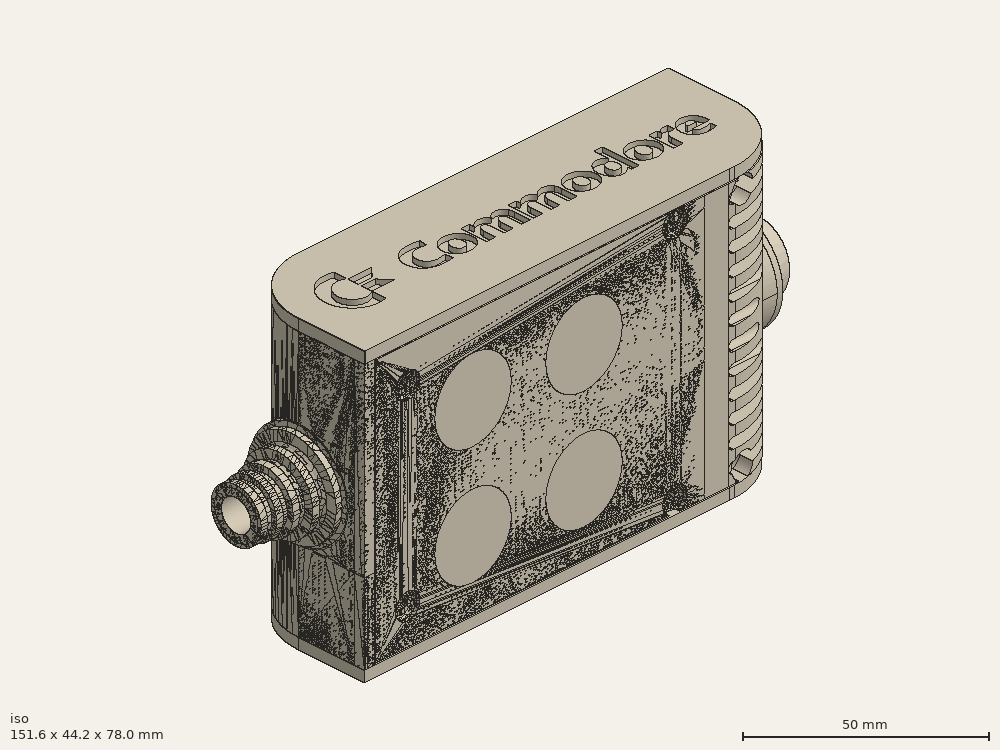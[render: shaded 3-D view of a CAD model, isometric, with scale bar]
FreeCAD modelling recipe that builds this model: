
FCSTD DOCUMENT  (FreeCAD 0.19R0.19.2)
Label: enclosure_225FCStd
License: All rights reserved
LicenseURL: http://en.wikipedia.org/wiki/All_rights_reserved
objects: Part::Revolution×152, Part::MultiFuse×148, Part::Feature×146, Sketcher::SketchObject×94, Part::Extrusion×79, Part::Cut×75, Part::Cylinder×71, Part::Fillet×58, Part::Box×38, App::MeasureDistance×4, Part::Chamfer×4, Part::FeaturePython×2, Image::ImagePlane×1, PartDesign::Body×1, Part::Mirroring×1
note: 869 computed .brp shape members not serialized (recipe doc carries the construction recipe); baked Part::Feature solids carry a one-line shape summary decoded from their .brp

FEATURE [Sketcher::SketchObject] Sketch  label="topSketch"
  FullyConstrained = true
  sketch-geometry (20):
    g0: LineSegment StartX=5.21097e-06 StartY=3 StartZ=0 EndX=5.21097e-06 EndY=19 EndZ=0
    g1: ArcOfCircle CenterX=19 CenterY=19 CenterZ=0 NormalX=0 NormalY=0 NormalZ=1 AngleXU=0 Radius=19 StartAngle=1.5708 EndAngle=3.14159
    g2: ArcOfCircle CenterX=19 CenterY=19 CenterZ=0 NormalX=0 NormalY=0 NormalZ=1 AngleXU=0 Radius=16 StartAngle=1.5708 EndAngle=3.14159
    g3: LineSegment StartX=114 StartY=35 StartZ=0 EndX=19 EndY=35 EndZ=0
    g4: LineSegment StartX=5.21097e-06 StartY=3 StartZ=0 EndX=5.21097e-06 EndY=0 EndZ=0
    g5: LineSegment StartX=3 StartY=0 StartZ=0 EndX=5.21097e-06 EndY=0 EndZ=0
    g6: LineSegment StartX=3 StartY=19 StartZ=0 EndX=3 EndY=0 EndZ=0
    g7: LineSegment StartX=19 StartY=38 StartZ=0 EndX=124 EndY=38 EndZ=0
    g8: Circle CenterX=119 CenterY=35 CenterZ=0 NormalX=0 NormalY=0 NormalZ=1 AngleXU=0 Radius=1
    g9: Circle CenterX=121 CenterY=35 CenterZ=0 NormalX=0 NormalY=0 NormalZ=1 AngleXU=0 Radius=1
    g10: Circle CenterX=121 CenterY=33 CenterZ=0 NormalX=0 NormalY=0 NormalZ=1 AngleXU=0 Radius=1
    g11: BSplineCurve PolesCount=3 KnotsCount=2 Degree=2 IsPeriodic=0
    g12: GeomPoint X=119 Y=35 Z=0
    g13: GeomPoint X=121 Y=33 Z=0
    g14: LineSegment StartX=119 StartY=35 StartZ=0 EndX=114 EndY=35 EndZ=0
    g15: ArcOfCircle CenterX=105 CenterY=19 CenterZ=0 NormalX=0 NormalY=0 NormalZ=1 AngleXU=0 Radius=19 StartAngle=5.7297 EndAngle=6.28319
    g16: ArcOfCircle CenterX=105 CenterY=19 CenterZ=0 NormalX=0 NormalY=0 NormalZ=1 AngleXU=0 Radius=16 StartAngle=5.60905 EndAngle=6.28319
    g17: LineSegment StartX=121 StartY=33 StartZ=0 EndX=121 EndY=19 EndZ=0
    g18: LineSegment StartX=124 StartY=38 StartZ=0 EndX=124 EndY=19 EndZ=0
    g19: LineSegment StartX=117.5 StartY=9.01251 StartZ=0 EndX=121.163 EndY=9.0125 EndZ=0
  constraints (46):
    c: Vertical(g0)
    c: Block(g0)
    c: Coincident(g1,g0)
    c: Block(g1)
    c: Coincident(g2,g1)
    c: Block(g2)
    c: Coincident(g3,g2)
    c: Horizontal(g3)
    c: Tangent(g3,g2)
    c: Coincident(g4,g0)
    c: Distance(g4) = 3
    c: Vertical(g4)
    c: Coincident(g5,g4)
    c: Horizontal(g5)
    c: Coincident(g6,g2)
    c: Coincident(g6,g5)
    c: Vertical(g6)
    c: Horizontal(g7)
    c: Distance(g7) = 105
    c: Coincident(g7,g1)
    c: Block(g3)
    c: Weight(g8) = 1
    c: Equal(g8,g9)
    c: Equal(g8,g10)
    c: InternalAlignment(g8,g11)
    c: InternalAlignment(g9,g11)
    c: InternalAlignment(g10,g11)
    c: InternalAlignment(g12,g11)
    c: InternalAlignment(g13,g11)
    c: Block(g11)
    c: Coincident(g14,g11)
    c: Coincident(g14,g3)
    c: Horizontal(g14)
    c: Block(g15)
    c: Coincident(g16,g15)
    c: Block(g16)
    c: Coincident(g17,g11)
    c: Coincident(g17,g16)
    c: Vertical(g17)
    c: Distance(g17) = 14
    c: Coincident(g18,g7)
    c: Coincident(g18,g15)
    c: Vertical(g18)
    c: Distance(g18) = 19
    c: Coincident(g19,g16)
    c: Coincident(g19,g15)
FEATURE [Sketcher::SketchObject] Sketch001  label="bottomSketch"
  FullyConstrained = true
  sketch-geometry (32):
    g0: LineSegment StartX=3.3 StartY=-6.03275e-07 StartZ=0 EndX=98 EndY=-6.03275e-07 EndZ=0
    g1: ArcOfCircle CenterX=98 CenterY=19 CenterZ=0 NormalX=0 NormalY=0 NormalZ=1 AngleXU=0 Radius=19 StartAngle=4.71239 EndAngle=5.71103
    g2: LineSegment StartX=6.3 StartY=8 StartZ=0 EndX=3.3 EndY=8 EndZ=0
    g3: LineSegment StartX=3.3 StartY=8 StartZ=0 EndX=3.3 EndY=-6.03275e-07 EndZ=0
    g4: ArcOfCircle CenterX=8.3 CenterY=5 CenterZ=0 NormalX=0 NormalY=0 NormalZ=1 AngleXU=0 Radius=2 StartAngle=3.14159 EndAngle=4.71239
    g5: LineSegment StartX=6.3 StartY=8 StartZ=0 EndX=6.3 EndY=5 EndZ=0
    g6: ArcOfCircle CenterX=98 CenterY=19 CenterZ=0 NormalX=0 NormalY=0 NormalZ=1 AngleXU=0 Radius=12.7 StartAngle=4.71239 EndAngle=6.28319
    g7: LineSegment StartX=94.7 StartY=3 StartZ=0 EndX=8.3 EndY=3 EndZ=0
    g8-g12: Circle x5 (B-spline internal-alignment scaffolding for g13; pole/knot coordinates omitted)
    g13: BSplineCurve PolesCount=5 KnotsCount=3 Degree=3 IsPeriodic=0
    g14: GeomPoint X=98 Y=6.3 Z=0
    g15: GeomPoint X=96.3938 Y=4.71946 Z=0
    g16: GeomPoint X=94.7 Y=3 Z=0
    g17-g23: Circle x7 (B-spline internal-alignment scaffolding for g24; pole/knot coordinates omitted)
    g24: BSplineCurve PolesCount=7 KnotsCount=5 Degree=3 IsPeriodic=0
    g25-g29: GeomPoint x5 (B-spline internal-alignment scaffolding for g24; pole/knot coordinates omitted)
    g30: ArcOfCircle CenterX=98 CenterY=19 CenterZ=0 NormalX=0 NormalY=0 NormalZ=1 AngleXU=0 Radius=15.7 StartAngle=5.81226 EndAngle=6.28319
    g31: LineSegment StartX=110.7 StartY=19 StartZ=0 EndX=113.7 EndY=19 EndZ=0
  constraints (41):
    c: Horizontal(g0)
    c: Coincident(g1,g0)
    c: Block(g1)
    c: Horizontal(g2)
    c: Distance(g2) = 3
    c: Coincident(g3,g2)
    c: Vertical(g3)
    c: Coincident(g3,g0)
    c: Block(g4)
    c: Block(g2)
    c: Coincident(g5,g2)
    c: Coincident(g5,g4)
    c: Vertical(g5)
    c: Coincident(g6,g1)
    c: Block(g6)
    c: Coincident(g7,g4)
    c: Horizontal(g7)
    c: Block(g0)
    c: Block(g7)
    c: Block(g3)
    c: Coincident(g13,g6)
    c: Weight(g8) = 1
    c: Equal(g8, g9-g12) x4
    c: Coincident(g13,g7)
    c: InternalAlignment(g8-g12 -> g13) x5
    c: InternalAlignment(g14,g13)
    c: InternalAlignment(g15,g13)
    c: InternalAlignment(g16,g13)
    c: Block(g13)
    c: Weight(g17) = 1
    c: Equal(g17, g18-g23) x6
    c: Coincident(g24,g1)
    c: InternalAlignment(g17-g23 -> g24) x7
    c: InternalAlignment(g25-g29 -> g24) x5
    c: Block(g24)
    c: Coincident(g30,g24)
    c: Coincident(g31,g6)
    c: Coincident(g31,g30)
    c: Horizontal(g31)
    c: Block(g31)
    c: Block(g30)
FEATURE [Part::Extrusion] Extrude  label="top"
  Base = -> Sketch
  Dir = (0,0,1)
  DirMode = 2
  FaceMakerClass = Part::FaceMakerBullseye
  LengthFwd = 72
  LengthRev = 0
  Solid = true
  Symmetric = false
FEATURE [Part::Extrusion] Extrude001  label="bottom"
  Base = -> Sketch001
  Dir = (0,0,1)
  DirMode = 2
  FaceMakerClass = Part::FaceMakerBullseye
  LengthFwd = 71.4
  LengthRev = 0
  Placement = pos=(0,0,0.3) rot=(0,0,1;0rad)
  Solid = true
  Symmetric = false
FEATURE [Sketcher::SketchObject] Sketch002  label="topSketch001"
  FullyConstrained = true
  sketch-geometry (8):
    g0: ArcOfCircle CenterX=19 CenterY=19.0975 CenterZ=0 NormalX=0 NormalY=0 NormalZ=1 AngleXU=0 Radius=18.9025 StartAngle=1.5708 EndAngle=3.14674
    g1: LineSegment StartX=0.0977805 StartY=19.0003 StartZ=0 EndX=0.0977805 EndY=0.000251602 EndZ=0
    g2: LineSegment StartX=19 StartY=38 StartZ=0 EndX=124 EndY=38 EndZ=0
    g3: LineSegment StartX=0.0977805 StartY=0.000251602 StartZ=0 EndX=105.098 EndY=0.000251602 EndZ=0
    g4: LineSegment StartX=124 StartY=38 StartZ=0 EndX=125.616 EndY=38 EndZ=0
    g5: LineSegment StartX=105.098 StartY=0.000251602 StartZ=0 EndX=106.713 EndY=0.000251602 EndZ=0
    g6: ArcOfCircle CenterX=106.616 CenterY=19 CenterZ=0 NormalX=0 NormalY=0 NormalZ=1 AngleXU=0 Radius=19 StartAngle=4.71754 EndAngle=6.28319
    g7: LineSegment StartX=125.616 StartY=38 StartZ=0 EndX=125.616 EndY=19 EndZ=0
  constraints (21):
    c: Block(g0)
    c: Coincident(g1,g0)
    c: Vertical(g1)
    c: Horizontal(g2)
    c: Distance(g2) = 105
    c: Coincident(g2,g0)
    c: Distance(g1) = 19
    c: Coincident(g3,g1)
    c: Horizontal(g3)
    c: Distance(g3) = 105
    c: Coincident(g4,g2)
    c: Horizontal(g4)
    c: Distance(g4) = 1.61553
    c: Horizontal(g5)
    c: Equal(g4,g5) = 1.61553
    c: Coincident(g5,g3)
    c: Block(g6)
    c: Coincident(g6,g5)
    c: Coincident(g7,g4)
    c: Coincident(g7,g6)
    c: Vertical(g7)
FEATURE [Part::Extrusion] Extrude002  label="sideA"
  Base = -> Sketch002
  Dir = (0,0,1)
  DirMode = 2
  FaceMakerClass = Part::FaceMakerBullseye
  LengthFwd = 3
  LengthRev = 0
  Placement = pos=(0,0,-3) rot=(0,0,1;0rad)
  Solid = true
  Symmetric = false
FEATURE [Sketcher::SketchObject] Sketch003  label="topSketch002"
  FullyConstrained = true
  sketch-geometry (6):
    g0: LineSegment StartX=19 StartY=38 StartZ=0 EndX=117 EndY=38 EndZ=0
    g1: ArcOfCircle CenterX=19 CenterY=19 CenterZ=0 NormalX=0 NormalY=0 NormalZ=1 AngleXU=0 Radius=19 StartAngle=1.5708 EndAngle=3.14159
    g2: LineSegment StartX=117 StartY=38 StartZ=0 EndX=117 EndY=19 EndZ=0
    g3: LineSegment StartX=98 StartY=1.0161e-12 StartZ=0 EndX=5.22862e-06 EndY=1.0161e-12 EndZ=0
    g4: LineSegment StartX=5.22862e-06 StartY=19 StartZ=0 EndX=5.22862e-06 EndY=1.0161e-12 EndZ=0
    g5: ArcOfCircle CenterX=98 CenterY=19 CenterZ=0 NormalX=0 NormalY=0 NormalZ=1 AngleXU=0 Radius=19 StartAngle=4.71239 EndAngle=6.28319
  constraints (16):
    c: Horizontal(g0)
    c: Distance(g0) = 98
    c: Coincident(g1,g0)
    c: Block(g1)
    c: Coincident(g2,g0)
    c: Vertical(g2)
    c: Distance(g2) = 19
    c: Horizontal(g3)
    c: Coincident(g4,g1)
    c: Vertical(g4)
    c: Coincident(g3,g4)
    c: Block(g3)
    c: Coincident(g5,g2)
    c: Coincident(g5,g3)
    c: Block(g0)
    c: Block(g5)
FEATURE [Sketcher::SketchObject] Sketch004
  FullyConstrained = true
  MapMode = 3
  Placement = pos=(0,0,0) rot=(1,0,0;1.5708rad)
  Support = -> [Extrude]
  sketch-geometry (8):
    g0: Circle CenterX=80.351 CenterY=-67.6202 CenterZ=0 NormalX=0 NormalY=0 NormalZ=1 AngleXU=0 Radius=2
    g1: Circle CenterX=80.351 CenterY=-67.6202 CenterZ=0 NormalX=0 NormalY=0 NormalZ=1 AngleXU=0 Radius=3
    g2: Circle CenterX=80.351 CenterY=-4.92017 CenterZ=0 NormalX=0 NormalY=0 NormalZ=1 AngleXU=0 Radius=2
    g3: Circle CenterX=80.351 CenterY=-4.92017 CenterZ=0 NormalX=0 NormalY=0 NormalZ=1 AngleXU=0 Radius=3
    g4: Circle CenterX=23.851 CenterY=-4.92017 CenterZ=0 NormalX=0 NormalY=0 NormalZ=1 AngleXU=0 Radius=2
    g5: Circle CenterX=23.851 CenterY=-4.92017 CenterZ=0 NormalX=0 NormalY=0 NormalZ=1 AngleXU=0 Radius=3
    g6: Circle CenterX=23.851 CenterY=-67.6202 CenterZ=0 NormalX=0 NormalY=0 NormalZ=1 AngleXU=0 Radius=2
    g7: Circle CenterX=23.851 CenterY=-67.6202 CenterZ=0 NormalX=0 NormalY=0 NormalZ=1 AngleXU=0 Radius=3
  constraints (8):
    c: Block(g3)
    c: Block(g2)
    c: Block(g1)
    c: Block(g0)
    c: Block(g6)
    c: Block(g7)
    c: Block(g4)
    c: Block(g5)
FEATURE [Part::Extrusion] Extrude004
  Base = -> Sketch004
  Dir = (0,-1,2e-16)
  DirMode = 2
  FaceMakerClass = Part::FaceMakerBullseye
  LengthFwd = 6
  LengthRev = 0
  Placement = pos=(0,9,0) rot=(0,0,1;0rad)
  Solid = true
  Symmetric = false
FEATURE [Sketcher::SketchObject] Sketch005
  FullyConstrained = true
  MapMode = 3
  Placement = pos=(0,0,0) rot=(1,0,0;1.5708rad)
  Support = -> [Extrude]
  sketch-geometry (8):
    g0: Circle CenterX=80.351 CenterY=-67.6202 CenterZ=0 NormalX=0 NormalY=0 NormalZ=1 AngleXU=0 Radius=3
    g1: Circle CenterX=80.351 CenterY=-4.92017 CenterZ=0 NormalX=0 NormalY=0 NormalZ=1 AngleXU=0 Radius=3
    g2: Circle CenterX=23.851 CenterY=-4.92017 CenterZ=0 NormalX=0 NormalY=0 NormalZ=1 AngleXU=0 Radius=3
    g3: Circle CenterX=23.851 CenterY=-67.6202 CenterZ=0 NormalX=0 NormalY=0 NormalZ=1 AngleXU=0 Radius=3
    g4: Circle CenterX=23.851 CenterY=-67.6202 CenterZ=0 NormalX=0 NormalY=0 NormalZ=1 AngleXU=0 Radius=5
    g5: Circle CenterX=80.351 CenterY=-67.6202 CenterZ=0 NormalX=0 NormalY=0 NormalZ=1 AngleXU=0 Radius=5
    g6: Circle CenterX=23.851 CenterY=-4.92017 CenterZ=0 NormalX=0 NormalY=0 NormalZ=1 AngleXU=0 Radius=5
    g7: Circle CenterX=80.351 CenterY=-4.92017 CenterZ=0 NormalX=0 NormalY=0 NormalZ=1 AngleXU=0 Radius=5
  constraints (8):
    c: Block(g1)
    c: Block(g0)
    c: Block(g3)
    c: Block(g2)
    c: Block(g5)
    c: Block(g4)
    c: Block(g6)
    c: Block(g7)
FEATURE [Part::Extrusion] Extrude005
  Base = -> Sketch005
  Dir = (0,-1,2e-16)
  DirMode = 2
  FaceMakerClass = Part::FaceMakerBullseye
  LengthFwd = 2
  LengthRev = 0
  Solid = true
  Symmetric = false
FEATURE [Sketcher::SketchObject] Sketch006
  FullyConstrained = true
  MapMode = 3
  Placement = pos=(0,0,0) rot=(1,0,0;1.5708rad)
  sketch-geometry (8):
    g0: Circle CenterX=80.351 CenterY=-67.6202 CenterZ=0 NormalX=0 NormalY=0 NormalZ=1 AngleXU=0 Radius=3
    g1: Circle CenterX=80.351 CenterY=-4.92017 CenterZ=0 NormalX=0 NormalY=0 NormalZ=1 AngleXU=0 Radius=3
    g2: Circle CenterX=23.851 CenterY=-4.92017 CenterZ=0 NormalX=0 NormalY=0 NormalZ=1 AngleXU=0 Radius=3
    g3: Circle CenterX=23.851 CenterY=-67.6202 CenterZ=0 NormalX=0 NormalY=0 NormalZ=1 AngleXU=0 Radius=3
    g4: Circle CenterX=23.851 CenterY=-67.6202 CenterZ=0 NormalX=0 NormalY=0 NormalZ=1 AngleXU=0 Radius=5
    g5: Circle CenterX=80.351 CenterY=-67.6202 CenterZ=0 NormalX=0 NormalY=0 NormalZ=1 AngleXU=0 Radius=5
    g6: Circle CenterX=23.851 CenterY=-4.92017 CenterZ=0 NormalX=0 NormalY=0 NormalZ=1 AngleXU=0 Radius=5
    g7: Circle CenterX=80.351 CenterY=-4.92017 CenterZ=0 NormalX=0 NormalY=0 NormalZ=1 AngleXU=0 Radius=5
  constraints (8):
    c: Block(g1)
    c: Block(g0)
    c: Block(g3)
    c: Block(g2)
    c: Block(g5)
    c: Block(g4)
    c: Block(g6)
    c: Block(g7)
FEATURE [Part::Extrusion] Extrude007
  Base = -> Sketch006
  Dir = (0,-1,2e-16)
  DirMode = 2
  FaceMakerClass = Part::FaceMakerBullseye
  LengthFwd = 2
  LengthRev = 0
  Solid = true
  Symmetric = false
FEATURE [Part::Fillet] Fillet
  Base = -> Extrude007
  Edges = 4 edges r=1.99: [Edge6,Edge12,Edge18,Edge24]
FEATURE [Part::Cut] Cut
  Base = -> Extrude005
  Placement = pos=(0,5,0) rot=(0,0,1;0rad)
  Tool = -> Fillet
FEATURE [Part::MultiFuse] Fusion  label="pCBScrews"
  Placement = pos=(-2.5,0,72.3) rot=(0,0,1;0rad)
  Shapes = -> [Extrude004,Cut]
FEATURE [App::MeasureDistance] Distance  label="Distance: 0.69 mm"
  Distance = 0.685967
  P1 = (24.0138,2.9647,0.3)
  P2 = (23.8901,3,-0.373787)
FEATURE [App::MeasureDistance] Distance001  label="Distance: 0.53 mm"
  Distance = 0.533607
  P1 = (80.2939,3,72.2334)
  P2 = (80.281,2.99661,71.7)
FEATURE [Part::Fillet] Fillet001
  Base = -> Extrude001
  Edges = 1 edges r=2.4: [Edge17]
FEATURE [Part::Fillet] Fillet002  label="bottom001"
  Base = -> Fillet001
  Edges = 1 edges r=2.4: [Edge36]
FEATURE [Part::Fillet] Fillet003  label="top001"
  Base = -> Extrude
  Edges = 1 edges r=2: [Edge1]
FEATURE [Sketcher::SketchObject] Sketch007
  FullyConstrained = true
  sketch-geometry (16):
    g0: LineSegment StartX=4 StartY=0 StartZ=0 EndX=4 EndY=2.4 EndZ=0
    g1: LineSegment StartX=4 StartY=2.4 StartZ=0 EndX=7 EndY=2.4 EndZ=0
    g2: LineSegment StartX=4 StartY=0 StartZ=0 EndX=5.7 EndY=0 EndZ=0
    g3: LineSegment StartX=5.7 StartY=0 StartZ=0 EndX=5.7 EndY=-5.6 EndZ=0
    g4-g8: Circle x5 (B-spline internal-alignment scaffolding for g9; pole/knot coordinates omitted)
    g9: BSplineCurve PolesCount=5 KnotsCount=3 Degree=3 IsPeriodic=0
    g10: GeomPoint X=7 Y=2.4 Z=0
    g11: GeomPoint X=10.4582 Y=-1.55472 Z=0
    g12: GeomPoint X=14 Y=-5.6 Z=0
    g13: LineSegment StartX=14 StartY=-5.6 StartZ=0 EndX=14 EndY=-14.1 EndZ=0
    g14: LineSegment StartX=14 StartY=-14.1 StartZ=0 EndX=6.5 EndY=-14.1 EndZ=0
    g15: LineSegment StartX=5.7 StartY=-5.6 StartZ=0 EndX=6.5 EndY=-14.1 EndZ=0
  constraints (28):
    c: Distance(g0) = 2.4
    c: Vertical(g0)
    c: Block(g0)
    c: Coincident(g1,g0)
    c: Horizontal(g1)
    c: Distance(g1) = 3
    c: Coincident(g2,g0)
    c: Horizontal(g2)
    c: Distance(g2) = 1.7
    c: Coincident(g3,g2)
    c: Vertical(g3)
    c: Distance(g3) = 5.6
    c: Coincident(g9,g1)
    c: Weight(g4) = 1
    c: Equal(g4, g5-g8) x4
    c: InternalAlignment(g4-g8 -> g9) x5
    c: InternalAlignment(g10,g9)
    c: InternalAlignment(g11,g9)
    c: InternalAlignment(g12,g9)
    c: Block(g9)
    c: Coincident(g13,g9)
    c: Vertical(g13)
    c: Distance(g13) = 8.5
    c: Coincident(g14,g13)
    c: Horizontal(g14)
    c: Distance(g14) = 7.5
    c: Coincident(g15,g3)
    c: Coincident(g15,g14)
FEATURE [Part::Feature] Face
  shape: bbox 10 x 16.5 x 2e-07 mm, 1 faces, 0 solids (baked)
FEATURE [Part::Revolution] Revolve  label="plugHousing"
  Angle = 360
  Axis = (0,1,0)
  Base = (0,0,0)
  FaceMakerClass = Part::FaceMakerBullseye
  Placement = pos=(0,0,36.15) rot=(0,0,1;0rad)
  Solid = false
  Source = -> Face
  Symmetric = false
FEATURE [Part::Feature] Face001
  shape: bbox 10 x 16.5 x 2e-07 mm, 1 faces, 0 solids (baked)
FEATURE [Part::Revolution] Revolve001  label="plugHousing001"
  Angle = 360
  Axis = (0,1,0)
  Base = (0,0,0)
  FaceMakerClass = Part::FaceMakerBullseye
  Placement = pos=(0,0,36.15) rot=(0,0,1;0rad)
  Solid = false
  Source = -> Face001
  Symmetric = false
FEATURE [Part::MultiFuse] Fusion001  label="plugHousing002"
  Placement = pos=(0,0,0) rot=(0,0,1;1.5708rad)
  Shapes = -> [Revolve001,Revolve]
FEATURE [Part::Feature] Face002
  shape: bbox 10 x 16.5 x 2e-07 mm, 1 faces, 0 solids (baked)
FEATURE [Part::Revolution] Revolve003  label="plugHousing005"
  Angle = 360
  Axis = (0,1,0)
  Base = (0,0,0)
  FaceMakerClass = Part::FaceMakerBullseye
  Placement = pos=(0,0,36.15) rot=(0,0,1;0rad)
  Solid = false
  Source = -> Face002
  Symmetric = false
FEATURE [Part::Feature] Face003
  shape: bbox 10 x 16.5 x 2e-07 mm, 1 faces, 0 solids (baked)
FEATURE [Part::Revolution] Revolve002  label="plugHousing003"
  Angle = 360
  Axis = (0,1,0)
  Base = (0,0,0)
  FaceMakerClass = Part::FaceMakerBullseye
  Placement = pos=(0,0,36.15) rot=(0,0,1;0rad)
  Solid = false
  Source = -> Face003
  Symmetric = false
FEATURE [Part::MultiFuse] Fusion002  label="plugHousing004"
  Placement = pos=(0,0,0) rot=(0,0,1;1.5708rad)
  Shapes = -> [Revolve002,Revolve003]
FEATURE [Part::MultiFuse] Fusion003  label="plugHousing006"
  Placement = pos=(0,19,0) rot=(0,0,1;3.14159rad)
  Shapes = -> [Fusion002,Fusion001]
FEATURE [Part::Feature] Face004
  shape: bbox 10 x 16.5 x 2e-07 mm, 1 faces, 0 solids (baked)
FEATURE [Part::Revolution] Revolve006  label="plugHousing010"
  Angle = 360
  Axis = (0,1,0)
  Base = (0,0,0)
  FaceMakerClass = Part::FaceMakerBullseye
  Placement = pos=(0,0,36.15) rot=(0,0,1;0rad)
  Solid = false
  Source = -> Face004
  Symmetric = false
FEATURE [Part::Feature] Face005
  shape: bbox 10 x 16.5 x 2e-07 mm, 1 faces, 0 solids (baked)
FEATURE [Part::Revolution] Revolve007  label="plugHousing011"
  Angle = 360
  Axis = (0,1,0)
  Base = (0,0,0)
  FaceMakerClass = Part::FaceMakerBullseye
  Placement = pos=(0,0,36.15) rot=(0,0,1;0rad)
  Solid = false
  Source = -> Face005
  Symmetric = false
FEATURE [Part::Feature] Face006
  shape: bbox 10 x 16.5 x 2e-07 mm, 1 faces, 0 solids (baked)
FEATURE [Part::Revolution] Revolve004  label="plugHousing007"
  Angle = 360
  Axis = (0,1,0)
  Base = (0,0,0)
  FaceMakerClass = Part::FaceMakerBullseye
  Placement = pos=(0,0,36.15) rot=(0,0,1;0rad)
  Solid = false
  Source = -> Face006
  Symmetric = false
FEATURE [Part::MultiFuse] Fusion004  label="plugHousing009"
  Placement = pos=(0,0,0) rot=(0,0,1;1.5708rad)
  Shapes = -> [Revolve004,Revolve007]
FEATURE [Part::Feature] Face007
  shape: bbox 10 x 16.5 x 2e-07 mm, 1 faces, 0 solids (baked)
FEATURE [Part::Revolution] Revolve005  label="plugHousing008"
  Angle = 360
  Axis = (0,1,0)
  Base = (0,0,0)
  FaceMakerClass = Part::FaceMakerBullseye
  Placement = pos=(0,0,36.15) rot=(0,0,1;0rad)
  Solid = false
  Source = -> Face007
  Symmetric = false
FEATURE [Part::MultiFuse] Fusion005  label="plugHousing012"
  Placement = pos=(0,0,0) rot=(0,0,1;1.5708rad)
  Shapes = -> [Revolve006,Revolve005]
FEATURE [Part::MultiFuse] Fusion006  label="plugHousing013"
  Placement = pos=(0,19,0) rot=(0,0,1;3.14159rad)
  Shapes = -> [Fusion005,Fusion004]
FEATURE [Part::MultiFuse] Fusion007  label="plugHousing014"
  Placement = pos=(122.621,0,-0.15) rot=(0,0,1;0rad)
  Shapes = -> [Fusion003,Fusion006]
FEATURE [Part::Cylinder] Cylinder002
  Angle = 360
  AttacherType = Attacher::AttachEngine3D
  Height = 20
  Placement = pos=(0,0,36.15) rot=(0,0,1;0rad)
  Radius = 4
FEATURE [Part::Cylinder] Cylinder003
  Angle = 360
  AttacherType = Attacher::AttachEngine3D
  Height = 10
  Placement = pos=(0,0,36.15) rot=(0,0,1;0rad)
  Radius = 4
FEATURE [Part::MultiFuse] Fusion009  label="removeToCreateHoleForPlugHousing"
  Placement = pos=(70,19,36.15) rot=(0,1,0;1.5708rad)
  Shapes = -> [Cylinder002,Cylinder003]
FEATURE [Part::Cylinder] Cylinder004
  Angle = 360
  AttacherType = Attacher::AttachEngine3D
  Height = 20
  Placement = pos=(0,0,36.15) rot=(0,0,1;0rad)
  Radius = 4
FEATURE [Part::Cylinder] Cylinder005
  Angle = 360
  AttacherType = Attacher::AttachEngine3D
  Height = 10
  Placement = pos=(0,0,36.15) rot=(0,0,1;0rad)
  Radius = 4
FEATURE [Part::MultiFuse] Fusion010  label="removeToCreateHoleForPlugHousing001"
  Placement = pos=(70,19,36.15) rot=(0,1,0;1.5708rad)
  Shapes = -> [Cylinder004,Cylinder005]
FEATURE [Part::Cut] Cut001
  Base = -> Fillet003
  Tool = -> Fusion010
FEATURE [Part::Cut] Cut002  label="Bottom"
  Base = -> Fillet002
  Tool = -> Fusion009
FEATURE [Part::Feature] Face008
  shape: bbox 10 x 16.5 x 2e-07 mm, 1 faces, 0 solids (baked)
FEATURE [Part::Revolution] Revolve011  label="plugHousing021"
  Angle = 360
  Axis = (0,1,0)
  Base = (0,0,0)
  FaceMakerClass = Part::FaceMakerBullseye
  Placement = pos=(0,0,36.15) rot=(0,0,1;0rad)
  Solid = false
  Source = -> Face008
  Symmetric = false
FEATURE [Part::Feature] Face009
  shape: bbox 10 x 16.5 x 2e-07 mm, 1 faces, 0 solids (baked)
FEATURE [Part::Revolution] Revolve012  label="plugHousing022"
  Angle = 360
  Axis = (0,1,0)
  Base = (0,0,0)
  FaceMakerClass = Part::FaceMakerBullseye
  Placement = pos=(0,0,36.15) rot=(0,0,1;0rad)
  Solid = false
  Source = -> Face009
  Symmetric = false
FEATURE [Part::Feature] Face010 .. Face013  x4 (patterned run collapsed; names and placements below)
  shape: bbox 10 x 16.5 x 2e-07 mm, 1 faces, 0 solids (baked)
FEATURE [Part::Revolution] Revolve015  label="plugHousing027"
  Angle = 360
  Axis = (0,1,0)
  Base = (0,0,0)
  FaceMakerClass = Part::FaceMakerBullseye
  Placement = pos=(0,0,36.15) rot=(0,0,1;0rad)
  Solid = false
  Source = -> Face013
  Symmetric = false
FEATURE [Part::Feature] Face014
  shape: bbox 10 x 16.5 x 2e-07 mm, 1 faces, 0 solids (baked)
FEATURE [Part::Feature] Face015
  shape: bbox 10 x 16.5 x 2e-07 mm, 1 faces, 0 solids (baked)
FEATURE [Part::Feature] Face016
  shape: bbox 10 x 16.5 x 2e-07 mm, 1 faces, 0 solids (baked)
FEATURE [Part::Revolution] Revolve019  label="plugHousing033"
  Angle = 360
  Axis = (0,1,0)
  Base = (0,0,0)
  FaceMakerClass = Part::FaceMakerBullseye
  Placement = pos=(0,0,36.15) rot=(0,0,1;0rad)
  Solid = false
  Source = -> Face016
  Symmetric = false
FEATURE [Part::Feature] Face017
  shape: bbox 10 x 16.5 x 2e-07 mm, 1 faces, 0 solids (baked)
FEATURE [Part::Revolution] Revolve020  label="plugHousing034"
  Angle = 360
  Axis = (0,1,0)
  Base = (0,0,0)
  FaceMakerClass = Part::FaceMakerBullseye
  Placement = pos=(0,0,36.15) rot=(0,0,1;0rad)
  Solid = false
  Source = -> Face017
  Symmetric = false
FEATURE [Part::Feature] Face018
  shape: bbox 10 x 16.5 x 2e-07 mm, 1 faces, 0 solids (baked)
FEATURE [Part::Revolution] Revolve016  label="plugHousing030"
  Angle = 360
  Axis = (0,1,0)
  Base = (0,0,0)
  FaceMakerClass = Part::FaceMakerBullseye
  Placement = pos=(0,0,36.15) rot=(0,0,1;0rad)
  Solid = false
  Source = -> Face018
  Symmetric = false
FEATURE [Part::MultiFuse] Fusion020  label="plugHousing038"
  Placement = pos=(0,0,0) rot=(0,0,1;1.5708rad)
  Shapes = -> [Revolve016,Revolve020]
FEATURE [Part::Feature] Face019
  shape: bbox 10 x 16.5 x 2e-07 mm, 1 faces, 0 solids (baked)
FEATURE [Part::Feature] Face020
  shape: bbox 10 x 16.5 x 2e-07 mm, 1 faces, 0 solids (baked)
FEATURE [Part::Revolution] Revolve017  label="plugHousing031"
  Angle = 360
  Axis = (0,1,0)
  Base = (0,0,0)
  FaceMakerClass = Part::FaceMakerBullseye
  Placement = pos=(0,0,36.15) rot=(0,0,1;0rad)
  Solid = false
  Source = -> Face020
  Symmetric = false
FEATURE [Part::MultiFuse] Fusion021  label="plugHousing039"
  Placement = pos=(0,0,0) rot=(0,0,1;1.5708rad)
  Shapes = -> [Revolve019,Revolve017]
FEATURE [Part::MultiFuse] Fusion023  label="plugHousing041"
  Placement = pos=(0,19,0) rot=(0,0,1;3.14159rad)
  Shapes = -> [Fusion021,Fusion020]
FEATURE [Part::Revolution] Revolve022  label="plugHousing043"
  Angle = 360
  Axis = (0,1,0)
  Base = (0,0,0)
  FaceMakerClass = Part::FaceMakerBullseye
  Placement = pos=(0,0,36.15) rot=(0,0,1;0rad)
  Solid = false
  Source = -> Face019
  Symmetric = false
FEATURE [Part::Feature] Face021
  shape: bbox 10 x 16.5 x 2e-07 mm, 1 faces, 0 solids (baked)
FEATURE [Part::Revolution] Revolve023  label="plugHousing044"
  Angle = 360
  Axis = (0,1,0)
  Base = (0,0,0)
  FaceMakerClass = Part::FaceMakerBullseye
  Placement = pos=(0,0,36.15) rot=(0,0,1;0rad)
  Solid = false
  Source = -> Face021
  Symmetric = false
FEATURE [Part::Feature] Face022
  shape: bbox 10 x 16.5 x 2e-07 mm, 1 faces, 0 solids (baked)
FEATURE [Part::Revolution] Revolve018  label="plugHousing032"
  Angle = 360
  Axis = (0,1,0)
  Base = (0,0,0)
  FaceMakerClass = Part::FaceMakerBullseye
  Placement = pos=(0,0,36.15) rot=(0,0,1;0rad)
  Solid = false
  Source = -> Face022
  Symmetric = false
FEATURE [Part::MultiFuse] Fusion022  label="plugHousing040"
  Placement = pos=(0,0,0) rot=(0,0,1;1.5708rad)
  Shapes = -> [Revolve018,Revolve023]
FEATURE [Part::Feature] Face023
  shape: bbox 10 x 16.5 x 2e-07 mm, 1 faces, 0 solids (baked)
FEATURE [Part::Revolution] Revolve021  label="plugHousing035"
  Angle = 360
  Axis = (0,1,0)
  Base = (0,0,0)
  FaceMakerClass = Part::FaceMakerBullseye
  Placement = pos=(0,0,36.15) rot=(0,0,1;0rad)
  Solid = false
  Source = -> Face023
  Symmetric = false
FEATURE [Part::MultiFuse] Fusion018  label="plugHousing036"
  Placement = pos=(0,0,0) rot=(0,0,1;1.5708rad)
  Shapes = -> [Revolve022,Revolve021]
FEATURE [Part::MultiFuse] Fusion019  label="plugHousing037"
  Placement = pos=(0,19,0) rot=(0,0,1;3.14159rad)
  Shapes = -> [Fusion018,Fusion022]
FEATURE [Part::MultiFuse] Fusion024  label="plugHousing042"
  Placement = pos=(122.621,0,-0.15) rot=(0,0,1;0rad)
  Shapes = -> [Fusion023,Fusion019]
FEATURE [Part::Cylinder] Cylinder006
  Angle = 360
  AttacherType = Attacher::AttachEngine3D
  Height = 20
  Placement = pos=(0,0,36.15) rot=(0,0,1;0rad)
  Radius = 14.3
FEATURE [Part::Cylinder] Cylinder007
  Angle = 360
  AttacherType = Attacher::AttachEngine3D
  Height = 10
  Placement = pos=(0,0,36.15) rot=(0,0,1;0rad)
  Radius = 4
FEATURE [Part::MultiFuse] Fusion026  label="removeToCreteHoleForPlugHousing"
  Placement = pos=(70,19,36) rot=(0,1,0;1.5708rad)
  Shapes = -> [Cylinder006,Cylinder007]
FEATURE [Part::Box] Box001  label="Cube001"
  AttacherType = Attacher::AttachEngine3D
  Height = 28
  Length = 3
  Placement = pos=(110.7,19,22) rot=(0,0,1;0rad)
  Width = 15.7
FEATURE [Part::Cut] Cut003  label="top002"
  Base = -> Cut001
  Tool = -> Fusion007
FEATURE [Part::Revolution] Revolve008  label="plugHousing015"
  Angle = 360
  Axis = (0,1,0)
  Base = (0,0,0)
  FaceMakerClass = Part::FaceMakerBullseye
  Placement = pos=(0,0,36.15) rot=(0,0,1;0rad)
  Solid = false
  Source = -> Face010
  Symmetric = false
FEATURE [Part::MultiFuse] Fusion013  label="plugHousing020"
  Placement = pos=(0,0,0) rot=(0,0,1;1.5708rad)
  Shapes = -> [Revolve008,Revolve012]
FEATURE [Part::Cut] Cut004  label="top003"
  Base = -> Cut003
  Placement = pos=(1,0,0) rot=(0,0,1;0rad)
  Tool = -> Fusion026
FEATURE [Part::Cylinder] Cylinder008
  Angle = 360
  AttacherType = Attacher::AttachEngine3D
  Height = 20
  Placement = pos=(0,0,36.15) rot=(0,0,1;0rad)
  Radius = 10.3
FEATURE [Part::Cylinder] Cylinder009
  Angle = 360
  AttacherType = Attacher::AttachEngine3D
  Height = 10
  Placement = pos=(0,0,36.15) rot=(0,0,1;0rad)
  Radius = 4
FEATURE [Part::MultiFuse] Fusion027  label="removeToCreteHoleForPlugHousing001"
  Placement = pos=(70,19,36) rot=(0,1,0;1.5708rad)
  Shapes = -> [Cylinder008,Cylinder009]
FEATURE [Part::Cut] Cut005  label="plugHousingTab"
  Base = -> Box001
  Tool = -> Fusion027
FEATURE [Part::MultiFuse] Fusion028  label="plugHousing045"
  Shapes = -> [Fusion024,Cut005]
FEATURE [Part::Box] Box002  label="Cube002"
  AttacherType = Attacher::AttachEngine3D
  Height = 28.8
  Length = 3
  Placement = pos=(107.3,28,21.6) rot=(0,0,1;0rad)
  Width = 7
FEATURE [Part::Box] Box003  label="Cube003"
  AttacherType = Attacher::AttachEngine3D
  Height = 3
  Length = 6.4
  Placement = pos=(107.3,28,18.6) rot=(0,0,1;0rad)
  Width = 7
FEATURE [Part::Box] Box004  label="Cube004"
  AttacherType = Attacher::AttachEngine3D
  Height = 3
  Length = 6.4
  Placement = pos=(107.3,28,50.4) rot=(0,0,1;0rad)
  Width = 7
FEATURE [Part::MultiFuse] Fusion029  label="plugHousingBracketHolder"
  Shapes = -> [Box004,Box002,Box003]
FEATURE [Part::Cylinder] Cylinder010
  Angle = 360
  AttacherType = Attacher::AttachEngine3D
  Height = 20
  Placement = pos=(0,0,36.15) rot=(0,0,1;0rad)
  Radius = 14.3
FEATURE [Part::Cylinder] Cylinder011
  Angle = 360
  AttacherType = Attacher::AttachEngine3D
  Height = 10
  Placement = pos=(0,0,36.15) rot=(0,0,1;0rad)
  Radius = 4
FEATURE [Part::MultiFuse] Fusion030  label="removeToCreteHoleForPlugHousing002"
  Placement = pos=(70,19,36) rot=(0,1,0;1.5708rad)
  Shapes = -> [Cylinder010,Cylinder011]
FEATURE [Part::Cut] Cut006  label="plugHousingBracketHolder001"
  Base = -> Fusion029
  Tool = -> Fusion030
FEATURE [Part::Cylinder] Cylinder012
  Angle = 360
  AttacherType = Attacher::AttachEngine3D
  Height = 20
  Placement = pos=(0,0,36.15) rot=(0,0,1;0rad)
  Radius = 7
FEATURE [Part::Cylinder] Cylinder013
  Angle = 360
  AttacherType = Attacher::AttachEngine3D
  Height = 10
  Placement = pos=(0,0,36.15) rot=(0,0,1;0rad)
  Radius = 4
FEATURE [Part::MultiFuse] Fusion032  label="removeToCreteHoleForPlugHousing003"
  Placement = pos=(70,19,36) rot=(0,1,0;1.5708rad)
  Shapes = -> [Cylinder012,Cylinder013]
FEATURE [Part::Cut] Cut007  label="bottom002"
  Base = -> Cut002
  Tool = -> Fusion032
FEATURE [Sketcher::SketchObject] Sketch008
  FullyConstrained = true
  sketch-geometry (54):
    g0: LineSegment StartX=-4.2 StartY=0 StartZ=0 EndX=-6.2 EndY=0 EndZ=0
    g1: LineSegment StartX=-14 StartY=-18 StartZ=0 EndX=-14 EndY=-26.5 EndZ=0
    g2: LineSegment StartX=-4.2 StartY=0 StartZ=0 EndX=-4.2 EndY=-13.4877 EndZ=0
    g3: Circle CenterX=-4.2 CenterY=-13.4877 CenterZ=0 NormalX=0 NormalY=0 NormalZ=1 AngleXU=0 Radius=1
    g4: Circle CenterX=-4.2 CenterY=-26.5 CenterZ=0 NormalX=0 NormalY=0 NormalZ=1 AngleXU=0 Radius=1
    g5: Circle CenterX=-8.2 CenterY=-26.5 CenterZ=0 NormalX=0 NormalY=0 NormalZ=1 AngleXU=0 Radius=1
    g6: BSplineCurve PolesCount=3 KnotsCount=2 Degree=2 IsPeriodic=0
    g7: GeomPoint X=-4.2 Y=-13.4877 Z=0
    g8: GeomPoint X=-8.2 Y=-26.5 Z=0
    g9: LineSegment StartX=-14 StartY=-26.5 StartZ=0 EndX=-8.2 EndY=-26.5 EndZ=0
    g10: LineSegment StartX=-10.15 StartY=-12 StartZ=0 EndX=-10.15 EndY=-14 EndZ=0
    g11: LineSegment StartX=-12.8401 StartY=-16 StartZ=0 EndX=-10.1571 EndY=-16 EndZ=0
    g12: LineSegment StartX=-10.15 StartY=-14 StartZ=0 EndX=-8.70761 EndY=-14 EndZ=0
    g13: LineSegment StartX=-12.8401 StartY=-16 StartZ=0 EndX=-12.8401 EndY=-17.6958 EndZ=0
    g14: LineSegment StartX=-10.15 StartY=-12 StartZ=0 EndX=-7.79258 EndY=-12 EndZ=0
    g15: Circle CenterX=-6.2215 CenterY=-2 CenterZ=0 NormalX=0 NormalY=0 NormalZ=1 AngleXU=0 Radius=1
    g16: Circle CenterX=-6.22762 CenterY=-2.58724 CenterZ=0 NormalX=0 NormalY=0 NormalZ=1 AngleXU=0 Radius=1
    g17: Circle CenterX=-6.32538 CenterY=-4 CenterZ=0 NormalX=0 NormalY=0 NormalZ=1 AngleXU=0 Radius=1
    g18: BSplineCurve PolesCount=3 KnotsCount=2 Degree=2 IsPeriodic=0
    g19: GeomPoint X=-6.2215 Y=-2 Z=0
    g20: GeomPoint X=-6.32538 Y=-4 Z=0
    g21: Circle CenterX=-6.48644 CenterY=-5.99526 CenterZ=0 NormalX=0 NormalY=0 NormalZ=1 AngleXU=0 Radius=1
    g22: Circle CenterX=-6.58486 CenterY=-6.99526 CenterZ=0 NormalX=0 NormalY=0 NormalZ=1 AngleXU=0 Radius=1
    g23: Circle CenterX=-6.77343 CenterY=-8 CenterZ=0 NormalX=0 NormalY=0 NormalZ=1 AngleXU=0 Radius=1
    g24: BSplineCurve PolesCount=3 KnotsCount=2 Degree=2 IsPeriodic=0
    g25: GeomPoint X=-6.48644 Y=-5.99526 Z=0
    g26: GeomPoint X=-6.77343 Y=-8 Z=0
    g27: Circle CenterX=-7.19003 CenterY=-10 CenterZ=0 NormalX=0 NormalY=0 NormalZ=1 AngleXU=0 Radius=1
    g28: Circle CenterX=-7.44407 CenterY=-11.0915 CenterZ=0 NormalX=0 NormalY=0 NormalZ=1 AngleXU=0 Radius=1
    g29: Circle CenterX=-7.79258 CenterY=-12 CenterZ=0 NormalX=0 NormalY=0 NormalZ=1 AngleXU=0 Radius=1
    g30: BSplineCurve PolesCount=3 KnotsCount=2 Degree=2 IsPeriodic=0
    g31: GeomPoint X=-7.19003 Y=-10 Z=0
    g32: GeomPoint X=-7.79258 Y=-12 Z=0
    g33: Circle CenterX=-8.70761 CenterY=-14 CenterZ=0 NormalX=0 NormalY=0 NormalZ=1 AngleXU=0 Radius=1
    g34: Circle CenterX=-9.33087 CenterY=-15.1837 CenterZ=0 NormalX=0 NormalY=0 NormalZ=1 AngleXU=0 Radius=1
    g35: Circle CenterX=-10.1571 CenterY=-16 CenterZ=0 NormalX=0 NormalY=0 NormalZ=1 AngleXU=0 Radius=1
    g36: BSplineCurve PolesCount=3 KnotsCount=2 Degree=2 IsPeriodic=0
    g37: GeomPoint X=-8.70761 Y=-14 Z=0
    g38: GeomPoint X=-10.1571 Y=-16 Z=0
    g39: Circle CenterX=-12.8401 CenterY=-17.6958 CenterZ=0 NormalX=0 NormalY=0 NormalZ=1 AngleXU=0 Radius=1
    g40: Circle CenterX=-13.3521 CenterY=-17.9027 CenterZ=0 NormalX=0 NormalY=0 NormalZ=1 AngleXU=0 Radius=1
    g41: Circle CenterX=-14 CenterY=-18 CenterZ=0 NormalX=0 NormalY=0 NormalZ=1 AngleXU=0 Radius=1
    g42: BSplineCurve PolesCount=3 KnotsCount=2 Degree=2 IsPeriodic=0
    g43: GeomPoint X=-12.8401 Y=-17.6958 Z=0
    g44: GeomPoint X=-14 Y=-18 Z=0
    g45: LineSegment StartX=-6.2 StartY=0 StartZ=0 EndX=-7.2 EndY=0 EndZ=0
    g46: LineSegment StartX=-7.2 StartY=0 StartZ=0 EndX=-7.2 EndY=-2 EndZ=0
    g47: LineSegment StartX=-7.2 StartY=-2 StartZ=0 EndX=-6.2215 EndY=-2 EndZ=0
    g48: LineSegment StartX=-6.32538 StartY=-4 StartZ=0 EndX=-7.65538 EndY=-4 EndZ=0
    g49: LineSegment StartX=-7.65538 StartY=-4 StartZ=0 EndX=-7.65538 EndY=-5.99526 EndZ=0
    g50: LineSegment StartX=-7.65538 StartY=-5.99526 StartZ=0 EndX=-6.48644 EndY=-5.99526 EndZ=0
    g51: LineSegment StartX=-6.77343 StartY=-8 StartZ=0 EndX=-8.43343 EndY=-8 EndZ=0
    g52: LineSegment StartX=-8.43343 StartY=-8 StartZ=0 EndX=-8.43343 EndY=-10 EndZ=0
    g53: LineSegment StartX=-8.43343 StartY=-10 StartZ=0 EndX=-7.19003 EndY=-10 EndZ=0
  constraints (112):
    c: Horizontal(g0)
    c: Distance(g0) = 2
    c: Block(g0)
    c: Vertical(g1)
    c: Coincident(g2,g0)
    c: Vertical(g2)
    c: Block(g2)
    c: Coincident(g6,g2)
    c: Weight(g3) = 1
    c: Equal(g3,g4)
    c: Equal(g3,g5)
    c: InternalAlignment(g3,g6)
    c: InternalAlignment(g4,g6)
    c: InternalAlignment(g5,g6)
    c: InternalAlignment(g7,g6)
    c: InternalAlignment(g8,g6)
    c: Block(g6)
    c: Coincident(g9,g1)
    c: Coincident(g9,g6)
    c: Horizontal(g9)
    c: Vertical(g10)
    c: Block(g10)
    c: Horizontal(g11)
    c: Block(g11)
    c: Coincident(g12,g10)
    c: Horizontal(g12)
    c: Block(g12)
    c: Coincident(g13,g11)
    c: Vertical(g13)
    c: Block(g13)
    c: Coincident(g14,g10)
    c: Horizontal(g14)
    c: Block(g14)
    c: Block(g9)
    c: Block(g1)
    c: Weight(g15) = 1
    c: Equal(g15,g16)
    c: Equal(g15,g17)
    c: InternalAlignment(g15,g18)
    c: InternalAlignment(g16,g18)
    c: InternalAlignment(g17,g18)
    c: InternalAlignment(g19,g18)
    c: InternalAlignment(g20,g18)
    c: Weight(g21) = 1
    c: Equal(g21,g22)
    c: Equal(g21,g23)
    c: InternalAlignment(g21,g24)
    c: InternalAlignment(g22,g24)
    c: InternalAlignment(g23,g24)
    c: InternalAlignment(g25,g24)
    c: InternalAlignment(g26,g24)
    c: Weight(g27) = 1
    c: Equal(g27,g28)
    c: Equal(g27,g29)
    c: Coincident(g30,g14)
    c: InternalAlignment(g27,g30)
    c: InternalAlignment(g28,g30)
    c: InternalAlignment(g29,g30)
    c: InternalAlignment(g31,g30)
    c: InternalAlignment(g32,g30)
    c: Coincident(g36,g12)
    c: Weight(g33) = 1
    c: Equal(g33,g34)
    c: Equal(g33,g35)
    c: Coincident(g36,g11)
    c: InternalAlignment(g33,g36)
    c: InternalAlignment(g34,g36)
    c: InternalAlignment(g35,g36)
    c: InternalAlignment(g37,g36)
    c: InternalAlignment(g38,g36)
    c: Coincident(g42,g13)
    c: Weight(g39) = 1
    c: Equal(g39,g40)
    c: Equal(g39,g41)
    c: Coincident(g42,g1)
    c: InternalAlignment(g39,g42)
    c: InternalAlignment(g40,g42)
    c: InternalAlignment(g41,g42)
    c: InternalAlignment(g43,g42)
    c: InternalAlignment(g44,g42)
    c: Block(g18)
    c: Block(g24)
    c: Block(g30)
    c: Block(g36)
    c: Block(g42)
    c: Horizontal(g45)
    c: Coincident(g45,g0)
    c: Vertical(g46)
    c: Coincident(g46,g45)
    c: Coincident(g47,g46)
    c: Coincident(g47,g18)
    c: Horizontal(g47)
    c: Block(g46)
    c: Coincident(g48,g18)
    c: Horizontal(g48)
    c: Distance(g48) = 1.33
    c: Vertical(g49)
    c: Coincident(g49,g48)
    c: Coincident(g50,g49)
    c: Coincident(g50,g24)
    c: Horizontal(g50)
    c: Tangent(g50,g22)
    c: Horizontal(g51)
    c: Coincident(g51,g24)
    c: Block(g51)
    c: Vertical(g52)
    c: Block(g52)
    c: Coincident(g52,g51)
    c: Coincident(g53,g52)
    c: Coincident(g53,g30)
    c: Horizontal(g53)
    c: Distance(g1) = 8.5
FEATURE [Part::Feature] Face024
  shape: bbox 9.8 x 26.5 x 2e-07 mm, 1 faces, 0 solids (baked)
FEATURE [Part::Revolution] Revolve024
  Angle = 360
  Axis = (0,1,0)
  Base = (0,0,0)
  FaceMakerClass = Part::FaceMakerBullseye
  Placement = pos=(0,0,0) rot=(0,0,1;1.5708rad)
  Solid = false
  Source = -> Face024
  Symmetric = false
FEATURE [Part::Feature] Face025
  shape: bbox 9.8 x 26.5 x 2e-07 mm, 1 faces, 0 solids (baked)
FEATURE [Part::Revolution] Revolve025
  Angle = 360
  Axis = (0,1,0)
  Base = (0,0,0)
  FaceMakerClass = Part::FaceMakerBullseye
  Placement = pos=(0,0,0) rot=(0,0,1;1.5708rad)
  Solid = false
  Source = -> Face025
  Symmetric = false
FEATURE [Part::MultiFuse] Fusion033
  Placement = pos=(-18,19,36) rot=(0,0,1;0rad)
  Shapes = -> [Revolve025,Revolve024]
FEATURE [Part::Cylinder] Cylinder014
  Angle = 360
  AttacherType = Attacher::AttachEngine3D
  Height = 20
  Placement = pos=(0,0,36.15) rot=(0,0,1;0rad)
  Radius = 14.3
FEATURE [Part::Cylinder] Cylinder015
  Angle = 360
  AttacherType = Attacher::AttachEngine3D
  Height = 10
  Placement = pos=(0,0,36.15) rot=(0,0,1;0rad)
  Radius = 4
FEATURE [Part::MultiFuse] Fusion034  label="removeToCreteHoleForPlugHousing004"
  Placement = pos=(-42,19,36) rot=(0,1,0;1.5708rad)
  Shapes = -> [Cylinder014,Cylinder015]
FEATURE [Part::Cut] Cut008  label="top004"
  Base = -> Cut004
  Placement = pos=(-1,0,0) rot=(0,0,1;0rad)
  Tool = -> Fusion034
FEATURE [Part::Box] Box005  label="Cube005"
  AttacherType = Attacher::AttachEngine3D
  Height = 28
  Length = 3
  Placement = pos=(110.7,19,22) rot=(0,0,1;0rad)
  Width = 15.7
FEATURE [Part::Cylinder] Cylinder016
  Angle = 360
  AttacherType = Attacher::AttachEngine3D
  Height = 10
  Placement = pos=(0,0,36.15) rot=(0,0,1;0rad)
  Radius = 4
FEATURE [Part::Cylinder] Cylinder017
  Angle = 360
  AttacherType = Attacher::AttachEngine3D
  Height = 20
  Placement = pos=(0,0,36.15) rot=(0,0,1;0rad)
  Radius = 10.3
FEATURE [Part::MultiFuse] Fusion035  label="removeToCreteHoleForPlugHousing005"
  Placement = pos=(70,19,36) rot=(0,1,0;1.5708rad)
  Shapes = -> [Cylinder017,Cylinder016]
FEATURE [Part::Cut] Cut009  label="plugHousingTab001"
  Base = -> Box005
  Placement = pos=(-107.4,-14,0) rot=(0,0,1;0rad)
  Tool = -> Fusion035
FEATURE [Part::Box] Box006  label="Cube006"
  AttacherType = Attacher::AttachEngine3D
  Height = 28
  Length = 3
  Placement = pos=(110.7,19,22) rot=(0,0,1;0rad)
  Width = 15.7
FEATURE [Part::Cylinder] Cylinder018
  Angle = 360
  AttacherType = Attacher::AttachEngine3D
  Height = 10
  Placement = pos=(0,0,36.15) rot=(0,0,1;0rad)
  Radius = 4
FEATURE [Part::Cylinder] Cylinder019
  Angle = 360
  AttacherType = Attacher::AttachEngine3D
  Height = 20
  Placement = pos=(0,0,36.15) rot=(0,0,1;0rad)
  Radius = 10.3
FEATURE [Part::MultiFuse] Fusion036  label="removeToCreteHoleForPlugHousing006"
  Placement = pos=(70,19,36) rot=(0,1,0;1.5708rad)
  Shapes = -> [Cylinder019,Cylinder018]
FEATURE [Part::Cut] Cut010  label="plugHousingTab002"
  Base = -> Box006
  Placement = pos=(-107.4,-14,0) rot=(0,0,1;0rad)
  Tool = -> Fusion036
FEATURE [Part::MultiFuse] Fusion037
  Placement = pos=(9.6,23,0) rot=(0,0,1;3.14159rad)
  Shapes = -> [Cut009,Cut010]
FEATURE [Part::Box] Box  label="Cube"
  AttacherType = Attacher::AttachEngine3D
  Height = 10
  Length = 3
  Placement = pos=(3.3,4,12) rot=(0,0,1;0rad)
  Width = 10
FEATURE [Part::Fillet] Fillet004
  Base = -> Fusion028
  Edges = 1 edges r=2: [Edge25]
FEATURE [Part::Fillet] Fillet005  label="plugHousing046"
  Base = -> Fillet004
  Edges = 1 edges r=2: [Edge8]
FEATURE [Part::Fillet] Fillet006
  Base = -> Box
  Edges = 1 edges r=2: [Edge11]
FEATURE [Part::Box] Box007  label="Cube007"
  AttacherType = Attacher::AttachEngine3D
  Height = 10
  Length = 3
  Placement = pos=(3.3,4,50) rot=(0,0,1;0rad)
  Width = 10
FEATURE [Part::Fillet] Fillet007
  Base = -> Box007
  Edges = 1 edges r=2: [Edge12]
FEATURE [Part::Box] Box008  label="Cube008"
  AttacherType = Attacher::AttachEngine3D
  Height = 28
  Length = 4
  Placement = pos=(5,0,22) rot=(0,0,1;0rad)
  Width = 10
FEATURE [Part::Fillet] Fillet008
  Base = -> Box008
  Edges = 1 edges r=1: [Edge7]
FEATURE [Part::Fillet] Fillet009
  Base = -> Fillet008
  Edges = 1 edges r=2: [Edge5]
FEATURE [Part::Fillet] Fillet010
  Base = -> Fillet009
  Edges = 1 edges r=2: [Edge2]
FEATURE [Sketcher::SketchObject] Sketch009  label="topSketch003"
  FullyConstrained = true
  sketch-geometry (4):
    g0: LineSegment StartX=16.8446 StartY=31.512 StartZ=0 EndX=16.3251 EndY=34.4666 EndZ=0
    g1: ArcOfCircle CenterX=19 CenterY=19.2524 CenterZ=0 NormalX=0 NormalY=0 NormalZ=1 AngleXU=0 Radius=15.4476 StartAngle=1.74483 EndAngle=2.72717
    g2: ArcOfCircle CenterX=19 CenterY=19.2524 CenterZ=0 NormalX=0 NormalY=0 NormalZ=1 AngleXU=0 Radius=12.4476 StartAngle=1.74483 EndAngle=2.73189
    g3: LineSegment StartX=4.86004 StartY=25.4725 StartZ=0 EndX=7.58253 EndY=24.2107 EndZ=0
  constraints (7):
    c: Block(g0)
    c: Coincident(g1,g0)
    c: Coincident(g2,g0)
    c: Coincident(g3,g1)
    c: Coincident(g3,g2)
    c: Block(g1)
    c: Block(g2)
FEATURE [Part::Extrusion] Extrude008
  Base = -> Sketch009
  Dir = (0,0,1)
  DirMode = 2
  FaceMakerClass = Part::FaceMakerBullseye
  LengthFwd = 10
  LengthRev = 0
  Placement = pos=(0,0,31) rot=(0,0,1;0rad)
  Solid = true
  Symmetric = false
FEATURE [Part::Cylinder] Cylinder020
  Angle = 360
  AttacherType = Attacher::AttachEngine3D
  Height = 20
  Placement = pos=(0,0,36.15) rot=(0,0,1;0rad)
  Radius = 8.2
FEATURE [Part::Cylinder] Cylinder021
  Angle = 360
  AttacherType = Attacher::AttachEngine3D
  Height = 10
  Placement = pos=(0,0,36.15) rot=(0,0,1;0rad)
  Radius = 4
FEATURE [Part::MultiFuse] Fusion038  label="removeToCreteHoleForPlugHousing007"
  Placement = pos=(-42,19,36) rot=(0,1,0;1.5708rad)
  Shapes = -> [Cylinder020,Cylinder021]
FEATURE [Part::Cut] Cut011
  Base = -> Extrude008
  Tool = -> Fusion038
FEATURE [Part::Fillet] Fillet011
  Base = -> Cut011
  Edges = 1 edges r=2: [Edge1]
FEATURE [Part::Fillet] Fillet012
  Base = -> Fillet011
  Edges = 1 edges r=2.5: [Edge1]
FEATURE [Part::Fillet] Fillet013
  Base = -> Fillet012
  Edges = 1 edges r=2.5: [Edge2]
FEATURE [Part::Box] Box010  label="Cube010"
  AttacherType = Attacher::AttachEngine3D
  Height = 16
  Length = 8
  Placement = pos=(12.7,31.52,28) rot=(0,0,1;0rad)
  Width = 4
FEATURE [Sketcher::SketchObject] Sketch010  label="topSketch004"
  FullyConstrained = true
  sketch-geometry (4):
    g0: LineSegment StartX=16.8446 StartY=31.512 StartZ=0 EndX=16.3251 EndY=34.4666 EndZ=0
    g1: ArcOfCircle CenterX=19 CenterY=19.2524 CenterZ=0 NormalX=0 NormalY=0 NormalZ=1 AngleXU=0 Radius=15.4476 StartAngle=1.74483 EndAngle=2.72717
    g2: ArcOfCircle CenterX=19 CenterY=19.2524 CenterZ=0 NormalX=0 NormalY=0 NormalZ=1 AngleXU=0 Radius=12.4476 StartAngle=1.74483 EndAngle=2.73189
    g3: LineSegment StartX=4.86004 StartY=25.4725 StartZ=0 EndX=7.58253 EndY=24.2107 EndZ=0
  constraints (7):
    c: Block(g0)
    c: Coincident(g1,g0)
    c: Coincident(g2,g0)
    c: Coincident(g3,g1)
    c: Coincident(g3,g2)
    c: Block(g1)
    c: Block(g2)
FEATURE [Part::Cylinder] Cylinder022
  Angle = 360
  AttacherType = Attacher::AttachEngine3D
  Height = 10
  Placement = pos=(0,0,36.15) rot=(0,0,1;0rad)
  Radius = 4
FEATURE [Sketcher::SketchObject] Sketch011  label="topSketch005"
  FullyConstrained = true
  sketch-geometry (4):
    g0: LineSegment StartX=16.8446 StartY=31.512 StartZ=0 EndX=16.3251 EndY=34.4666 EndZ=0
    g1: ArcOfCircle CenterX=19 CenterY=19.2524 CenterZ=0 NormalX=0 NormalY=0 NormalZ=1 AngleXU=0 Radius=15.4476 StartAngle=1.74483 EndAngle=2.72717
    g2: ArcOfCircle CenterX=19 CenterY=19.2524 CenterZ=0 NormalX=0 NormalY=0 NormalZ=1 AngleXU=0 Radius=12.4476 StartAngle=1.74483 EndAngle=2.73189
    g3: LineSegment StartX=4.86004 StartY=25.4725 StartZ=0 EndX=7.58253 EndY=24.2107 EndZ=0
  constraints (7):
    c: Block(g0)
    c: Coincident(g1,g0)
    c: Coincident(g2,g0)
    c: Coincident(g3,g1)
    c: Coincident(g3,g2)
    c: Block(g1)
    c: Block(g2)
FEATURE [Part::Extrusion] Extrude010
  Base = -> Sketch011
  Dir = (0,0,1)
  DirMode = 2
  FaceMakerClass = Part::FaceMakerBullseye
  LengthFwd = 10.6
  LengthRev = 0
  Placement = pos=(0,0,31) rot=(0,0,1;0rad)
  Solid = true
  Symmetric = false
FEATURE [Part::Cylinder] Cylinder023
  Angle = 360
  AttacherType = Attacher::AttachEngine3D
  Height = 20
  Placement = pos=(0,0,36.15) rot=(0,0,1;0rad)
  Radius = 8.2
FEATURE [Part::MultiFuse] Fusion039  label="removeToCreteHoleForPlugHousing008"
  Placement = pos=(-42,19,36) rot=(0,1,0;1.5708rad)
  Shapes = -> [Cylinder023,Cylinder022]
FEATURE [Part::Cut] Cut012
  Base = -> Extrude010
  Placement = pos=(0,0,-0.3) rot=(0,0,1;0rad)
  Tool = -> Fusion039
FEATURE [Part::Cut] Cut013
  Base = -> Box010
  Tool = -> Cut012
FEATURE [Part::Fillet] Fillet014
  Base = -> Cut013
  Edges = 1 edges r=0.7: [Edge13]
FEATURE [Part::Fillet] Fillet015
  Base = -> Fillet014
  Edges = 1 edges r=0.7: [Edge13]
FEATURE [Part::Fillet] Fillet016
  Base = -> Fillet015
  Edges = 1 edges r=0.7: [Edge16]
FEATURE [Part::Fillet] Fillet017
  Base = -> Fillet016
  Edges = 1 edges r=0.7: [Edge11]
FEATURE [Part::Fillet] Fillet018
  Base = -> Fillet017
  Edges = 1 edges r=0.7: [Edge10]
FEATURE [Part::Fillet] Fillet019
  Base = -> Fillet018
  Edges = 1 edges r=1.2: [Edge5]
FEATURE [Part::Fillet] Fillet020
  Base = -> Fillet019
  Edges = 1 edges r=1.2: [Edge12]
FEATURE [Part::Fillet] Fillet021
  Base = -> Fillet020
  Edges = 1 edges r=2: [Edge1]
  Placement = pos=(0.3,0,0) rot=(0,0,1;0rad)
FEATURE [Part::MultiFuse] Fusion040  label="top005"
  Shapes = -> [Cut008,Fillet021]
FEATURE [Part::MultiFuse] Fusion041  label="wireHolder"
  Shapes = -> [Fusion033,Fillet013]
FEATURE [Part::MultiFuse] Fusion042
  Shapes = -> [Fillet007,Fusion041]
FEATURE [Part::MultiFuse] Fusion043  label="wireHolder001"
  Shapes = -> [Fusion042,Fillet010]
FEATURE [Part::MultiFuse] Fusion044  label="wireHolder002"
  Shapes = -> [Fillet006,Fusion037,Fusion043]
FEATURE [Part::Feature] Face026
  shape: bbox 11 x 6 x 2e-07 mm, 1 faces, 0 solids (baked)
FEATURE [Part::Revolution] Revolve026
  Angle = 360
  Axis = (0,1,0)
  Base = (0,0,0)
  FaceMakerClass = Part::FaceMakerBullseye
  Placement = pos=(30.3,-1,19.7) rot=(0,0,1;0rad)
  Solid = false
  Source = -> Face026
  Symmetric = false
FEATURE [Sketcher::SketchObject] Sketch013  label="topSketch006"
  FullyConstrained = true
  sketch-geometry (13):
    g0: LineSegment StartX=117 StartY=19 StartZ=0 EndX=117 EndY=38 EndZ=0
    g1: ArcOfCircle CenterX=98 CenterY=19 CenterZ=0 NormalX=0 NormalY=0 NormalZ=1 AngleXU=0 Radius=19 StartAngle=5.7297 EndAngle=6.28319
    g2: LineSegment StartX=0 StartY=3 StartZ=0 EndX=0 EndY=19 EndZ=0
    g3: LineSegment StartX=19 StartY=38 StartZ=0 EndX=117 EndY=38 EndZ=0
    g4: ArcOfCircle CenterX=19 CenterY=19 CenterZ=0 NormalX=0 NormalY=0 NormalZ=1 AngleXU=0 Radius=19 StartAngle=1.5708 EndAngle=3.14159
    g5: ArcOfCircle CenterX=19 CenterY=19 CenterZ=0 NormalX=0 NormalY=0 NormalZ=1 AngleXU=0 Radius=16 StartAngle=1.5708 EndAngle=3.14159
    g6: ArcOfCircle CenterX=98 CenterY=19 CenterZ=0 NormalX=0 NormalY=0 NormalZ=1 AngleXU=0 Radius=16 StartAngle=5.60905 EndAngle=6.28319
    g7: LineSegment StartX=114 StartY=19 StartZ=0 EndX=114 EndY=35 EndZ=0
    g8: LineSegment StartX=110.5 StartY=9.01251 StartZ=0 EndX=114.163 EndY=9.01251 EndZ=0
    g9: LineSegment StartX=114 StartY=35 StartZ=0 EndX=19 EndY=35 EndZ=0
    g10: LineSegment StartX=0 StartY=3 StartZ=0 EndX=0 EndY=0 EndZ=0
    g11: LineSegment StartX=3 StartY=0 StartZ=0 EndX=0 EndY=0 EndZ=0
    g12: LineSegment StartX=3 StartY=19 StartZ=0 EndX=3 EndY=0 EndZ=0
  constraints (33):
    c: Vertical(g0)
    c: Distance(g0) = 19
    c: Block(g0)
    c: Coincident(g1,g0)
    c: Block(g1)
    c: Vertical(g2)
    c: Block(g2)
    c: Coincident(g3,g0)
    c: Horizontal(g3)
    c: Distance(g3) = 98
    c: Coincident(g4,g3)
    c: Coincident(g4,g2)
    c: Block(g4)
    c: Coincident(g5,g4)
    c: Coincident(g6,g1)
    c: Block(g6)
    c: Block(g5)
    c: Coincident(g7,g6)
    c: Vertical(g7)
    c: Coincident(g8,g6)
    c: Coincident(g8,g1)
    c: Coincident(g9,g7)
    c: Coincident(g9,g5)
    c: Horizontal(g9)
    c: Tangent(g9,g5)
    c: Coincident(g10,g2)
    c: Distance(g10) = 3
    c: Vertical(g10)
    c: Coincident(g11,g10)
    c: Horizontal(g11)
    c: Coincident(g12,g5)
    c: Coincident(g12,g11)
    c: Vertical(g12)
FEATURE [Part::Extrusion] Extrude011  label="top006"
  Base = -> Sketch013
  Dir = (0,0,1)
  DirMode = 2
  FaceMakerClass = Part::FaceMakerBullseye
  LengthFwd = 72
  LengthRev = 0
  Solid = true
  Symmetric = false
FEATURE [Sketcher::SketchObject] Sketch014
  FullyConstrained = true
  MapMode = 3
  Placement = pos=(0,0,0) rot=(1,0,0;1.5708rad)
  Support = -> [Extrude011]
  sketch-geometry (8):
    g0: Circle CenterX=80.351 CenterY=-67.6202 CenterZ=0 NormalX=0 NormalY=0 NormalZ=1 AngleXU=0 Radius=2
    g1: Circle CenterX=80.351 CenterY=-67.6202 CenterZ=0 NormalX=0 NormalY=0 NormalZ=1 AngleXU=0 Radius=3
    g2: Circle CenterX=80.351 CenterY=-4.92017 CenterZ=0 NormalX=0 NormalY=0 NormalZ=1 AngleXU=0 Radius=2
    g3: Circle CenterX=80.351 CenterY=-4.92017 CenterZ=0 NormalX=0 NormalY=0 NormalZ=1 AngleXU=0 Radius=3
    g4: Circle CenterX=23.851 CenterY=-4.92017 CenterZ=0 NormalX=0 NormalY=0 NormalZ=1 AngleXU=0 Radius=2
    g5: Circle CenterX=23.851 CenterY=-4.92017 CenterZ=0 NormalX=0 NormalY=0 NormalZ=1 AngleXU=0 Radius=3
    g6: Circle CenterX=23.851 CenterY=-67.6202 CenterZ=0 NormalX=0 NormalY=0 NormalZ=1 AngleXU=0 Radius=2
    g7: Circle CenterX=23.851 CenterY=-67.6202 CenterZ=0 NormalX=0 NormalY=0 NormalZ=1 AngleXU=0 Radius=3
  constraints (8):
    c: Block(g3)
    c: Block(g2)
    c: Block(g1)
    c: Block(g0)
    c: Block(g6)
    c: Block(g7)
    c: Block(g4)
    c: Block(g5)
FEATURE [Part::Feature] Face027
  shape: bbox 11 x 6 x 2e-07 mm, 1 faces, 0 solids (baked)
FEATURE [Part::Revolution] Revolve027
  Angle = 360
  Axis = (0,1,0)
  Base = (0,0,0)
  FaceMakerClass = Part::FaceMakerBullseye
  Placement = pos=(30.3,-1,51.7) rot=(0,0,1;0rad)
  Solid = false
  Source = -> Face027
  Symmetric = false
FEATURE [Part::Feature] Face028
  shape: bbox 11 x 6 x 2e-07 mm, 1 faces, 0 solids (baked)
FEATURE [Part::Revolution] Revolve028
  Angle = 360
  Axis = (0,1,0)
  Base = (0,0,0)
  FaceMakerClass = Part::FaceMakerBullseye
  Placement = pos=(62.3,-1,19.7) rot=(0,0,1;0rad)
  Solid = false
  Source = -> Face028
  Symmetric = false
FEATURE [Part::Feature] Face029
  shape: bbox 11 x 6 x 2e-07 mm, 1 faces, 0 solids (baked)
FEATURE [Part::Revolution] Revolve029
  Angle = 360
  Axis = (0,1,0)
  Base = (0,0,0)
  FaceMakerClass = Part::FaceMakerBullseye
  Placement = pos=(62.3,-1,51.7) rot=(0,0,1;0rad)
  Solid = false
  Source = -> Face029
  Symmetric = false
FEATURE [Part::Feature] Wire
  shape: bbox 11 x 5.2 x 2e-07 mm, 0 faces, 0 solids (baked)
FEATURE [Part::Revolution] Revolve030
  Angle = 360
  Axis = (0,1,0)
  Base = (0,0,0)
  FaceMakerClass = Part::FaceMakerBullseye
  Placement = pos=(30.3,38,19.7) rot=(0,0,1;0rad)
  Solid = true
  Source = -> Wire
  Symmetric = false
FEATURE [Part::Feature] Wire001
  shape: bbox 11 x 5.2 x 2e-07 mm, 0 faces, 0 solids (baked)
FEATURE [Part::Revolution] Revolve031
  Angle = 360
  Axis = (0,1,0)
  Base = (0,0,0)
  FaceMakerClass = Part::FaceMakerBullseye
  Placement = pos=(30.3,38,51.7) rot=(0,0,1;0rad)
  Solid = true
  Source = -> Wire001
  Symmetric = false
FEATURE [Part::Feature] Wire002
  shape: bbox 11 x 5.2 x 2e-07 mm, 0 faces, 0 solids (baked)
FEATURE [Part::Revolution] Revolve032
  Angle = 360
  Axis = (0,1,0)
  Base = (0,0,0)
  FaceMakerClass = Part::FaceMakerBullseye
  Placement = pos=(62.3,38,51.7) rot=(0,0,1;0rad)
  Solid = true
  Source = -> Wire002
  Symmetric = false
FEATURE [Part::Feature] Wire003
  shape: bbox 11 x 5.2 x 2e-07 mm, 0 faces, 0 solids (baked)
FEATURE [Part::Revolution] Revolve033
  Angle = 360
  Axis = (0,1,0)
  Base = (0,0,0)
  FaceMakerClass = Part::FaceMakerBullseye
  Placement = pos=(62.3,38,19.7) rot=(0,0,1;0rad)
  Solid = true
  Source = -> Wire003
  Symmetric = false
FEATURE [Part::MultiFuse] Fusion045  label="altRandScrewHousing"
  Shapes = -> [Revolve029,Revolve027,Revolve028,Revolve026]
FEATURE [Part::MultiFuse] Fusion046  label="fanScrewHousing"
  Shapes = -> [Revolve033,Revolve032,Revolve031,Revolve030]
FEATURE [Sketcher::SketchObject] Sketch015
  FullyConstrained = true
  sketch-geometry (17):
    g0: Circle CenterX=-3.5 CenterY=23.5 CenterZ=0 NormalX=0 NormalY=0 NormalZ=1 AngleXU=0 Radius=1
    g1: Circle CenterX=-1 CenterY=15.25 CenterZ=0 NormalX=0 NormalY=0 NormalZ=1 AngleXU=0 Radius=1
    g2: Circle CenterX=-3.5 CenterY=7 CenterZ=0 NormalX=0 NormalY=0 NormalZ=1 AngleXU=0 Radius=1
    g3: BSplineCurve PolesCount=3 KnotsCount=2 Degree=2 IsPeriodic=0
    g4: GeomPoint X=-3.5 Y=23.5 Z=0
    g5: GeomPoint X=-3.5 Y=7 Z=0
    g6: Circle CenterX=-4.8 CenterY=30.5 CenterZ=0 NormalX=0 NormalY=0 NormalZ=1 AngleXU=0 Radius=1
    g7: Circle CenterX=-3.5 CenterY=30.5 CenterZ=0 NormalX=0 NormalY=0 NormalZ=1 AngleXU=0 Radius=1
    g8: Circle CenterX=-3.5 CenterY=29.2 CenterZ=0 NormalX=0 NormalY=0 NormalZ=1 AngleXU=0 Radius=1
    g9: BSplineCurve PolesCount=3 KnotsCount=2 Degree=2 IsPeriodic=0
    g10: GeomPoint X=-4.8 Y=30.5 Z=0
    g11: GeomPoint X=-3.5 Y=29.2 Z=0
    g12: LineSegment StartX=-3.5 StartY=29.2 StartZ=0 EndX=-3.5 EndY=23.5 EndZ=0
    g13: LineSegment StartX=-4.8 StartY=30.5 StartZ=0 EndX=0 EndY=30.5 EndZ=0
    g14: LineSegment StartX=-3.5 StartY=0.3 StartZ=0 EndX=0 EndY=0.3 EndZ=0
    g15: LineSegment StartX=-3.5 StartY=0.3 StartZ=0 EndX=-3.5 EndY=7 EndZ=0
    g16: LineSegment StartX=0 StartY=0.3 StartZ=0 EndX=0 EndY=30.5 EndZ=0
  constraints (34):
    c: Weight(g0) = 1
    c: Equal(g0,g1)
    c: Equal(g0,g2)
    c: InternalAlignment(g0,g3)
    c: InternalAlignment(g1,g3)
    c: InternalAlignment(g2,g3)
    c: InternalAlignment(g4,g3)
    c: InternalAlignment(g5,g3)
    c: Block(g3)
    c: Weight(g6) = 1
    c: Equal(g6,g7)
    c: Equal(g6,g8)
    c: InternalAlignment(g6,g9)
    c: InternalAlignment(g7,g9)
    c: InternalAlignment(g8,g9)
    c: InternalAlignment(g10,g9)
    c: InternalAlignment(g11,g9)
    c: Block(g9)
    c: Coincident(g12,g9)
    c: Coincident(g12,g3)
    c: Vertical(g12)
    c: Coincident(g13,g9)
    c: Horizontal(g13)
    c: Distance(g13) = 4.8
    c: Horizontal(g14)
    c: Block(g14)
    c: Coincident(g15,g14)
    c: Coincident(g15,g3)
    c: Vertical(g15)
    c: Coincident(g16,g14)
    c: Coincident(g16,g13)
    c: Vertical(g16)
    c: Tangent(g16,g1)
    c: Distance(g14) = 3.5
FEATURE [Sketcher::SketchObject] Sketch016
  FullyConstrained = true
  sketch-geometry (16):
    g0: Circle CenterX=-3.5 CenterY=23.5 CenterZ=0 NormalX=0 NormalY=0 NormalZ=1 AngleXU=0 Radius=1
    g1: Circle CenterX=-1 CenterY=15.25 CenterZ=0 NormalX=0 NormalY=0 NormalZ=1 AngleXU=0 Radius=1
    g2: Circle CenterX=-3.5 CenterY=7 CenterZ=0 NormalX=0 NormalY=0 NormalZ=1 AngleXU=0 Radius=1
    g3: BSplineCurve PolesCount=3 KnotsCount=2 Degree=2 IsPeriodic=0
    g4: GeomPoint X=-3.5 Y=23.5 Z=0
    g5: GeomPoint X=-3.5 Y=7 Z=0
    g6: LineSegment StartX=-3.5 StartY=28.2 StartZ=0 EndX=-3.5 EndY=23.5 EndZ=0
    g7: LineSegment StartX=0 StartY=29.5 StartZ=0 EndX=0 EndY=30 EndZ=0
    g8: LineSegment StartX=-3.5 StartY=28.2 StartZ=0 EndX=-3.5 EndY=30 EndZ=0
    g9: LineSegment StartX=0 StartY=30 StartZ=0 EndX=0 EndY=30.5 EndZ=0
    g10: LineSegment StartX=0 StartY=30.5 StartZ=0 EndX=-3.5 EndY=30.5 EndZ=0
    g11: LineSegment StartX=-3.5 StartY=30.5 StartZ=0 EndX=-3.5 EndY=30 EndZ=0
    g12: LineSegment StartX=0 StartY=29.5 StartZ=0 EndX=0 EndY=5 EndZ=0
    g13: LineSegment StartX=-3.5 StartY=0.3 StartZ=0 EndX=-3.5 EndY=7 EndZ=0
    g14: LineSegment StartX=-3.5 StartY=0.3 StartZ=0 EndX=0 EndY=0.3 EndZ=0
    g15: LineSegment StartX=0 StartY=5 StartZ=0 EndX=0 EndY=0.3 EndZ=0
  constraints (39):
    c: Weight(g0) = 1
    c: Equal(g0,g1)
    c: Equal(g0,g2)
    c: InternalAlignment(g0,g3)
    c: InternalAlignment(g1,g3)
    c: InternalAlignment(g2,g3)
    c: InternalAlignment(g4,g3)
    c: InternalAlignment(g5,g3)
    c: Block(g3)
    c: Coincident(g6,g3)
    c: Vertical(g6)
    c: Vertical(g7)
    c: Distance(g7) = 0.5
    c: Coincident(g8,g6)
    c: Vertical(g8)
    c: Block(g6)
    c: Block(g7)
    c: Vertical(g9)
    c: Equal(g7,g9) = 0.5
    c: Block(g9)
    c: Coincident(g9,g7)
    c: Horizontal(g10)
    c: Coincident(g10,g9)
    c: Coincident(g11,g10)
    c: Coincident(g11,g8)
    c: Vertical(g11)
    c: Block(g11)
    c: Coincident(g12,g7)
    c: Vertical(g12)
    c: Coincident(g13,g3)
    c: Vertical(g13)
    c: Distance(g13) = 6.7
    c: Coincident(g14,g13)
    c: Horizontal(g14)
    c: Block(g14)
    c: Coincident(g15,g12)
    c: Coincident(g15,g14)
    c: Vertical(g15)
    c: Block(g15)
FEATURE [Sketcher::SketchObject] Sketch017
  FullyConstrained = true
  sketch-geometry (11):
    g0: LineSegment StartX=-3.5 StartY=1e-16 StartZ=0 EndX=-1.6 EndY=1e-16 EndZ=0
    g1: LineSegment StartX=-1.6 StartY=1e-16 StartZ=0 EndX=-1.6 EndY=1.5 EndZ=0
    g2: LineSegment StartX=-3.5 StartY=1.5 StartZ=0 EndX=-1.6 EndY=1.5 EndZ=0
    g3: LineSegment StartX=-3.5 StartY=1e-16 StartZ=0 EndX=-4.8 EndY=1e-16 EndZ=0
    g4: Circle CenterX=-3.5 CenterY=1.3 CenterZ=0 NormalX=0 NormalY=0 NormalZ=1 AngleXU=0 Radius=1
    g5: Circle CenterX=-3.5 CenterY=1e-16 CenterZ=0 NormalX=0 NormalY=0 NormalZ=1 AngleXU=0 Radius=1
    g6: Circle CenterX=-4.8 CenterY=1e-16 CenterZ=0 NormalX=0 NormalY=0 NormalZ=1 AngleXU=0 Radius=1
    g7: BSplineCurve PolesCount=3 KnotsCount=2 Degree=2 IsPeriodic=0
    g8: GeomPoint X=-3.5 Y=1.3 Z=0
    g9: GeomPoint X=-4.8 Y=1e-16 Z=0
    g10: LineSegment StartX=-3.5 StartY=1.3 StartZ=0 EndX=-3.5 EndY=1.5 EndZ=0
  constraints (24):
    c: Horizontal(g0)
    c: Distance(g0) = 1.9
    c: Block(g0)
    c: Coincident(g1,g0)
    c: Vertical(g1)
    c: Coincident(g2,g1)
    c: Horizontal(g2)
    c: Coincident(g3,g0)
    c: Horizontal(g3)
    c: Distance(g3) = 1.3
    c: Weight(g4) = 1
    c: Equal(g4,g5)
    c: Coincident(g5,g0)
    c: Equal(g4,g6)
    c: Coincident(g7,g3)
    c: InternalAlignment(g4,g7)
    c: InternalAlignment(g5,g7)
    c: InternalAlignment(g6,g7)
    c: InternalAlignment(g8,g7)
    c: InternalAlignment(g9,g7)
    c: Coincident(g10,g7)
    c: Coincident(g10,g2)
    c: Vertical(g10)
    c: Block(g10)
FEATURE [Part::Feature] Face035
  shape: bbox 3.2 x 1.5 x 2e-07 mm, 1 faces, 0 solids (baked)
FEATURE [Part::Revolution] Revolve039  label="backCaseScrewRetainer"
  Angle = 360
  Axis = (0,1,0)
  Base = (0,0,0)
  FaceMakerClass = Part::FaceMakerBullseye
  Placement = pos=(12.5,3,62) rot=(0,0,1;0rad)
  Solid = false
  Source = -> Face035
  Symmetric = false
FEATURE [Part::Feature] Face036
  shape: bbox 3.2 x 1.5 x 2e-07 mm, 1 faces, 0 solids (baked)
FEATURE [Part::Feature] Face039
  shape: bbox 4.8 x 30.2 x 2e-07 mm, 1 faces, 0 solids (baked)
FEATURE [Part::Revolution] Revolve043  label="frontCaseScrewPost002"
  Angle = 360
  Axis = (0,1,0)
  Base = (0,0,0)
  FaceMakerClass = Part::FaceMakerBullseye
  Placement = pos=(89.5,4.5,3.5) rot=(0,0,1;0rad)
  Solid = false
  Source = -> Face039
  Symmetric = false
FEATURE [Part::Feature] Face042
  shape: bbox 4.8 x 30.2 x 2e-07 mm, 1 faces, 0 solids (baked)
FEATURE [Part::Revolution] Revolve046  label="frontCaseScrewPost003"
  Angle = 360
  Axis = (0,1,0)
  Base = (0,0,0)
  FaceMakerClass = Part::FaceMakerBullseye
  Placement = pos=(89.5,4.5,68.5) rot=(0,0,1;0rad)
  Solid = false
  Source = -> Face042
  Symmetric = false
FEATURE [Part::Feature] Face043
  shape: bbox 3.2 x 1.5 x 2e-07 mm, 1 faces, 0 solids (baked)
FEATURE [Part::Revolution] Revolve047  label="frontCaseScrewRetainer002"
  Angle = 360
  Axis = (0,1,0)
  Base = (0,0,0)
  FaceMakerClass = Part::FaceMakerBullseye
  Placement = pos=(89.5,3,68.5) rot=(0,0,1;0rad)
  Solid = false
  Source = -> Face043
  Symmetric = false
FEATURE [Part::Feature] Face044
  shape: bbox 3.2 x 1.5 x 2e-07 mm, 1 faces, 0 solids (baked)
FEATURE [Part::Revolution] Revolve048  label="frontCaseScrewRetainer003"
  Angle = 360
  Axis = (0,1,0)
  Base = (0,0,0)
  FaceMakerClass = Part::FaceMakerBullseye
  Placement = pos=(89.5,3,3.5) rot=(0,0,1;0rad)
  Solid = false
  Source = -> Face044
  Symmetric = false
FEATURE [App::MeasureDistance] Distance002  label="Distance: 1.67 mm"
  Distance = 1.66921
  P1 = (99.2361,4.7524,71.7)
  P2 = (99.2347,6.42161,71.7)
FEATURE [Sketcher::SketchObject] Sketch018
  FullyConstrained = true
  sketch-geometry (7):
    g0: LineSegment StartX=0 StartY=0 StartZ=0 EndX=0 EndY=6 EndZ=0
    g1: Circle CenterX=0 CenterY=0 CenterZ=0 NormalX=0 NormalY=0 NormalZ=1 AngleXU=0 Radius=1
    g2: Circle CenterX=8 CenterY=6 CenterZ=0 NormalX=0 NormalY=0 NormalZ=1 AngleXU=0 Radius=1
    g3: BSplineCurve PolesCount=3 KnotsCount=2 Degree=2 IsPeriodic=0
    g4: GeomPoint X=0 Y=0 Z=0
    g5: GeomPoint X=8 Y=6 Z=0
    g6: LineSegment StartX=0 StartY=6 StartZ=0 EndX=8 EndY=6 EndZ=0
  constraints (14):
    c: Coincident(g0,g-1)
    c: Distance(g0) = 6
    c: Vertical(g0)
    c: Coincident(g3,g0)
    c: Weight(g1) = 1
    c: Equal(g1,g2)
    c: InternalAlignment(g1,g3)
    c: InternalAlignment(g2,g3)
    c: InternalAlignment(g4,g3)
    c: InternalAlignment(g5,g3)
    c: Block(g3)
    c: Coincident(g6,g0)
    c: Coincident(g6,g3)
    c: Horizontal(g6)
FEATURE [Part::Extrusion] Extrude012  label="caseScrewPillarBracket"
  Base = -> Sketch018
  Dir = (0,0,1)
  DirMode = 2
  FaceMakerClass = Part::FaceMakerBullseye
  LengthFwd = 2.4
  LengthRev = 0
  Placement = pos=(15.76,29,8.8) rot=(0,1,0;0rad)
  Solid = true
  Symmetric = false
FEATURE [Sketcher::SketchObject] Sketch019
  FullyConstrained = true
  sketch-geometry (7):
    g0: LineSegment StartX=0 StartY=0 StartZ=0 EndX=0 EndY=6 EndZ=0
    g1: Circle CenterX=0 CenterY=0 CenterZ=0 NormalX=0 NormalY=0 NormalZ=1 AngleXU=0 Radius=1
    g2: Circle CenterX=8 CenterY=6 CenterZ=0 NormalX=0 NormalY=0 NormalZ=1 AngleXU=0 Radius=1
    g3: BSplineCurve PolesCount=3 KnotsCount=2 Degree=2 IsPeriodic=0
    g4: GeomPoint X=0 Y=0 Z=0
    g5: GeomPoint X=8 Y=6 Z=0
    g6: LineSegment StartX=0 StartY=6 StartZ=0 EndX=8 EndY=6 EndZ=0
  constraints (14):
    c: Coincident(g0,g-1)
    c: Distance(g0) = 6
    c: Vertical(g0)
    c: Coincident(g3,g0)
    c: Weight(g1) = 1
    c: Equal(g1,g2)
    c: InternalAlignment(g1,g3)
    c: InternalAlignment(g2,g3)
    c: InternalAlignment(g4,g3)
    c: InternalAlignment(g5,g3)
    c: Block(g3)
    c: Coincident(g6,g0)
    c: Coincident(g6,g3)
    c: Horizontal(g6)
FEATURE [Part::Extrusion] Extrude013  label="caseScrewPillarBracket001"
  Base = -> Sketch019
  Dir = (0,0,1)
  DirMode = 2
  FaceMakerClass = Part::FaceMakerBullseye
  LengthFwd = 2.4
  LengthRev = 0
  Placement = pos=(15.76,29,60.8) rot=(0,0,1;0rad)
  Solid = true
  Symmetric = false
FEATURE [Sketcher::SketchObject] Sketch020
  FullyConstrained = true
  sketch-geometry (7):
    g0: LineSegment StartX=0 StartY=0 StartZ=0 EndX=0 EndY=6 EndZ=0
    g1: Circle CenterX=0 CenterY=0 CenterZ=0 NormalX=0 NormalY=0 NormalZ=1 AngleXU=0 Radius=1
    g2: Circle CenterX=8 CenterY=6 CenterZ=0 NormalX=0 NormalY=0 NormalZ=1 AngleXU=0 Radius=1
    g3: BSplineCurve PolesCount=3 KnotsCount=2 Degree=2 IsPeriodic=0
    g4: GeomPoint X=0 Y=0 Z=0
    g5: GeomPoint X=8 Y=6 Z=0
    g6: LineSegment StartX=0 StartY=6 StartZ=0 EndX=8 EndY=6 EndZ=0
  constraints (14):
    c: Coincident(g0,g-1)
    c: Distance(g0) = 6
    c: Vertical(g0)
    c: Coincident(g3,g0)
    c: Weight(g1) = 1
    c: Equal(g1,g2)
    c: InternalAlignment(g1,g3)
    c: InternalAlignment(g2,g3)
    c: InternalAlignment(g4,g3)
    c: InternalAlignment(g5,g3)
    c: Block(g3)
    c: Coincident(g6,g0)
    c: Coincident(g6,g3)
    c: Horizontal(g6)
FEATURE [Part::Extrusion] Extrude014  label="caseScrewPillarBracket002"
  Base = -> Sketch020
  Dir = (0,0,1)
  DirMode = 2
  FaceMakerClass = Part::FaceMakerBullseye
  LengthFwd = 2.4
  LengthRev = 0
  Placement = pos=(13.7,29,13.26) rot=(0,-1,0;1.5708rad)
  Solid = true
  Symmetric = false
FEATURE [Sketcher::SketchObject] Sketch021
  FullyConstrained = true
  sketch-geometry (7):
    g0: LineSegment StartX=0 StartY=0 StartZ=0 EndX=0 EndY=6 EndZ=0
    g1: Circle CenterX=0 CenterY=0 CenterZ=0 NormalX=0 NormalY=0 NormalZ=1 AngleXU=0 Radius=1
    g2: Circle CenterX=8 CenterY=6 CenterZ=0 NormalX=0 NormalY=0 NormalZ=1 AngleXU=0 Radius=1
    g3: BSplineCurve PolesCount=3 KnotsCount=2 Degree=2 IsPeriodic=0
    g4: GeomPoint X=0 Y=0 Z=0
    g5: GeomPoint X=8 Y=6 Z=0
    g6: LineSegment StartX=0 StartY=6 StartZ=0 EndX=8 EndY=6 EndZ=0
  constraints (14):
    c: Coincident(g0,g-1)
    c: Distance(g0) = 6
    c: Vertical(g0)
    c: Coincident(g3,g0)
    c: Weight(g1) = 1
    c: Equal(g1,g2)
    c: InternalAlignment(g1,g3)
    c: InternalAlignment(g2,g3)
    c: InternalAlignment(g4,g3)
    c: InternalAlignment(g5,g3)
    c: Block(g3)
    c: Coincident(g6,g0)
    c: Coincident(g6,g3)
    c: Horizontal(g6)
FEATURE [Part::Extrusion] Extrude015  label="caseScrewPillarBracket003"
  Base = -> Sketch021
  Dir = (0,0,1)
  DirMode = 2
  FaceMakerClass = Part::FaceMakerBullseye
  LengthFwd = 2.4
  LengthRev = 0
  Placement = pos=(11.3,29,58.74) rot=(0,1,0;1.5708rad)
  Solid = true
  Symmetric = false
FEATURE [Sketcher::SketchObject] Sketch022
  FullyConstrained = true
  sketch-geometry (7):
    g0: LineSegment StartX=0 StartY=0 StartZ=0 EndX=0 EndY=6 EndZ=0
    g1: Circle CenterX=0 CenterY=0 CenterZ=0 NormalX=0 NormalY=0 NormalZ=1 AngleXU=0 Radius=1
    g2: Circle CenterX=8 CenterY=6 CenterZ=0 NormalX=0 NormalY=0 NormalZ=1 AngleXU=0 Radius=1
    g3: BSplineCurve PolesCount=3 KnotsCount=2 Degree=2 IsPeriodic=0
    g4: GeomPoint X=0 Y=0 Z=0
    g5: GeomPoint X=8 Y=6 Z=0
    g6: LineSegment StartX=0 StartY=6 StartZ=0 EndX=8 EndY=6 EndZ=0
  constraints (14):
    c: Coincident(g0,g-1)
    c: Distance(g0) = 6
    c: Vertical(g0)
    c: Coincident(g3,g0)
    c: Weight(g1) = 1
    c: Equal(g1,g2)
    c: InternalAlignment(g1,g3)
    c: InternalAlignment(g2,g3)
    c: InternalAlignment(g4,g3)
    c: InternalAlignment(g5,g3)
    c: Block(g3)
    c: Coincident(g6,g0)
    c: Coincident(g6,g3)
    c: Horizontal(g6)
FEATURE [Part::Extrusion] Extrude016  label="caseScrewPillarBracket004"
  Base = -> Sketch022
  Dir = (0,0,1)
  DirMode = 2
  FaceMakerClass = Part::FaceMakerBullseye
  LengthFwd = 2.4
  LengthRev = 0
  Placement = pos=(88.3,29,65.23) rot=(0,1,0;1.5708rad)
  Solid = true
  Symmetric = false
FEATURE [Sketcher::SketchObject] Sketch023
  FullyConstrained = true
  sketch-geometry (7):
    g0: LineSegment StartX=0 StartY=0 StartZ=0 EndX=0 EndY=6 EndZ=0
    g1: Circle CenterX=0 CenterY=0 CenterZ=0 NormalX=0 NormalY=0 NormalZ=1 AngleXU=0 Radius=1
    g2: Circle CenterX=8 CenterY=6 CenterZ=0 NormalX=0 NormalY=0 NormalZ=1 AngleXU=0 Radius=1
    g3: BSplineCurve PolesCount=3 KnotsCount=2 Degree=2 IsPeriodic=0
    g4: GeomPoint X=0 Y=0 Z=0
    g5: GeomPoint X=8 Y=6 Z=0
    g6: LineSegment StartX=0 StartY=6 StartZ=0 EndX=8 EndY=6 EndZ=0
  constraints (14):
    c: Coincident(g0,g-1)
    c: Distance(g0) = 6
    c: Vertical(g0)
    c: Coincident(g3,g0)
    c: Weight(g1) = 1
    c: Equal(g1,g2)
    c: InternalAlignment(g1,g3)
    c: InternalAlignment(g2,g3)
    c: InternalAlignment(g4,g3)
    c: InternalAlignment(g5,g3)
    c: Block(g3)
    c: Coincident(g6,g0)
    c: Coincident(g6,g3)
    c: Horizontal(g6)
FEATURE [Part::Extrusion] Extrude017  label="caseScrewPillarBracket005"
  Base = -> Sketch023
  Dir = (0,0,1)
  DirMode = 2
  FaceMakerClass = Part::FaceMakerBullseye
  LengthFwd = 2.4
  LengthRev = 0
  Placement = pos=(90.7,29,6.77) rot=(0,-1,0;1.5708rad)
  Solid = true
  Symmetric = false
FEATURE [Sketcher::SketchObject] Sketch024
  FullyConstrained = true
  sketch-geometry (7):
    g0: LineSegment StartX=0 StartY=0 StartZ=0 EndX=0 EndY=6 EndZ=0
    g1: Circle CenterX=0 CenterY=0 CenterZ=0 NormalX=0 NormalY=0 NormalZ=1 AngleXU=0 Radius=1
    g2: Circle CenterX=8 CenterY=6 CenterZ=0 NormalX=0 NormalY=0 NormalZ=1 AngleXU=0 Radius=1
    g3: BSplineCurve PolesCount=3 KnotsCount=2 Degree=2 IsPeriodic=0
    g4: GeomPoint X=0 Y=0 Z=0
    g5: GeomPoint X=8 Y=6 Z=0
    g6: LineSegment StartX=0 StartY=6 StartZ=0 EndX=8 EndY=6 EndZ=0
  constraints (14):
    c: Coincident(g0,g-1)
    c: Distance(g0) = 6
    c: Vertical(g0)
    c: Coincident(g3,g0)
    c: Weight(g1) = 1
    c: Equal(g1,g2)
    c: InternalAlignment(g1,g3)
    c: InternalAlignment(g2,g3)
    c: InternalAlignment(g4,g3)
    c: InternalAlignment(g5,g3)
    c: Block(g3)
    c: Coincident(g6,g0)
    c: Coincident(g6,g3)
    c: Horizontal(g6)
FEATURE [Part::Extrusion] Extrude018  label="caseScrewPillarBracket006"
  Base = -> Sketch024
  Dir = (0,0,1)
  DirMode = 2
  FaceMakerClass = Part::FaceMakerBullseye
  LengthFwd = 2.4
  LengthRev = 0
  Placement = pos=(103.7,29,6.77) rot=(0,-1,0;1.5708rad)
  Solid = true
  Symmetric = false
FEATURE [Sketcher::SketchObject] Sketch025
  FullyConstrained = true
  sketch-geometry (7):
    g0: LineSegment StartX=0 StartY=0 StartZ=0 EndX=0 EndY=6 EndZ=0
    g1: Circle CenterX=0 CenterY=0 CenterZ=0 NormalX=0 NormalY=0 NormalZ=1 AngleXU=0 Radius=1
    g2: Circle CenterX=8 CenterY=6 CenterZ=0 NormalX=0 NormalY=0 NormalZ=1 AngleXU=0 Radius=1
    g3: BSplineCurve PolesCount=3 KnotsCount=2 Degree=2 IsPeriodic=0
    g4: GeomPoint X=0 Y=0 Z=0
    g5: GeomPoint X=8 Y=6 Z=0
    g6: LineSegment StartX=0 StartY=6 StartZ=0 EndX=8 EndY=6 EndZ=0
  constraints (14):
    c: Coincident(g0,g-1)
    c: Distance(g0) = 6
    c: Vertical(g0)
    c: Coincident(g3,g0)
    c: Weight(g1) = 1
    c: Equal(g1,g2)
    c: InternalAlignment(g1,g3)
    c: InternalAlignment(g2,g3)
    c: InternalAlignment(g4,g3)
    c: InternalAlignment(g5,g3)
    c: Block(g3)
    c: Coincident(g6,g0)
    c: Coincident(g6,g3)
    c: Horizontal(g6)
FEATURE [Part::Extrusion] Extrude019  label="caseScrewPillarBracket007"
  Base = -> Sketch025
  Dir = (0,0,1)
  DirMode = 2
  FaceMakerClass = Part::FaceMakerBullseye
  LengthFwd = 2.4
  LengthRev = 0
  Placement = pos=(101.3,29,65.23) rot=(0,1,0;1.5708rad)
  Solid = true
  Symmetric = false
FEATURE [Part::Box] Box011  label="frontCaseScrewPillarBracket"
  AttacherType = Attacher::AttachEngine3D
  Height = 2.4
  Length = 16
  Placement = pos=(87,28,2.3) rot=(0,0,1;0rad)
  Width = 7
FEATURE [Part::Box] Box012  label="frontCaseScrewPillarBracket001"
  AttacherType = Attacher::AttachEngine3D
  Height = 2.4
  Length = 16
  Placement = pos=(87,28,67.3) rot=(0,0,1;0rad)
  Width = 7
FEATURE [Sketcher::SketchObject] Sketch026
  FullyConstrained = true
  sketch-geometry (17):
    g0: Circle CenterX=-3.5 CenterY=23.5 CenterZ=0 NormalX=0 NormalY=0 NormalZ=1 AngleXU=0 Radius=1
    g1: Circle CenterX=-1 CenterY=15.25 CenterZ=0 NormalX=0 NormalY=0 NormalZ=1 AngleXU=0 Radius=1
    g2: Circle CenterX=-3.5 CenterY=7 CenterZ=0 NormalX=0 NormalY=0 NormalZ=1 AngleXU=0 Radius=1
    g3: BSplineCurve PolesCount=3 KnotsCount=2 Degree=2 IsPeriodic=0
    g4: GeomPoint X=-3.5 Y=23.5 Z=0
    g5: GeomPoint X=-3.5 Y=7 Z=0
    g6: Circle CenterX=-4.8 CenterY=30.5 CenterZ=0 NormalX=0 NormalY=0 NormalZ=1 AngleXU=0 Radius=1
    g7: Circle CenterX=-3.5 CenterY=30.5 CenterZ=0 NormalX=0 NormalY=0 NormalZ=1 AngleXU=0 Radius=1
    g8: Circle CenterX=-3.5 CenterY=29.2 CenterZ=0 NormalX=0 NormalY=0 NormalZ=1 AngleXU=0 Radius=1
    g9: BSplineCurve PolesCount=3 KnotsCount=2 Degree=2 IsPeriodic=0
    g10: GeomPoint X=-4.8 Y=30.5 Z=0
    g11: GeomPoint X=-3.5 Y=29.2 Z=0
    g12: LineSegment StartX=-3.5 StartY=29.2 StartZ=0 EndX=-3.5 EndY=23.5 EndZ=0
    g13: LineSegment StartX=-4.8 StartY=30.5 StartZ=0 EndX=0 EndY=30.5 EndZ=0
    g14: LineSegment StartX=-3.5 StartY=5 StartZ=0 EndX=-3.5 EndY=7 EndZ=0
    g15: LineSegment StartX=0 StartY=5 StartZ=0 EndX=0 EndY=30.5 EndZ=0
    g16: LineSegment StartX=-3.5 StartY=5 StartZ=0 EndX=0 EndY=5 EndZ=0
  constraints (33):
    c: Weight(g0) = 1
    c: Equal(g0,g1)
    c: Equal(g0,g2)
    c: InternalAlignment(g0,g3)
    c: InternalAlignment(g1,g3)
    c: InternalAlignment(g2,g3)
    c: InternalAlignment(g4,g3)
    c: InternalAlignment(g5,g3)
    c: Block(g3)
    c: Weight(g6) = 1
    c: Equal(g6,g7)
    c: Equal(g6,g8)
    c: InternalAlignment(g6,g9)
    c: InternalAlignment(g7,g9)
    c: InternalAlignment(g8,g9)
    c: InternalAlignment(g10,g9)
    c: InternalAlignment(g11,g9)
    c: Block(g9)
    c: Coincident(g12,g9)
    c: Coincident(g12,g3)
    c: Vertical(g12)
    c: Coincident(g13,g9)
    c: Horizontal(g13)
    c: Distance(g13) = 4.8
    c: Coincident(g14,g3)
    c: Vertical(g14)
    c: Coincident(g15,g13)
    c: Vertical(g15)
    c: Tangent(g15,g1)
    c: Distance(g14) = 2
    c: Coincident(g16,g14)
    c: Horizontal(g16)
    c: Coincident(g15,g16)
FEATURE [Part::Feature] Face050
  shape: bbox 4.8 x 25.5 x 2e-07 mm, 1 faces, 0 solids (baked)
FEATURE [Part::Revolution] Revolve054  label="moreFrontCaseScrewPost001"
  Angle = 360
  Axis = (0,1,0)
  Base = (0,0,0)
  FaceMakerClass = Part::FaceMakerBullseye
  Placement = pos=(102.5,4.5,3.5) rot=(0,0,1;0rad)
  Solid = false
  Source = -> Face050
  Symmetric = false
FEATURE [Part::Feature] Face051
  shape: bbox 4.8 x 25.5 x 2e-07 mm, 1 faces, 0 solids (baked)
FEATURE [Part::Revolution] Revolve055  label="moreFrontCaseScrewPost002"
  Angle = 360
  Axis = (0,1,0)
  Base = (0,0,0)
  FaceMakerClass = Part::FaceMakerBullseye
  Placement = pos=(102.5,4.5,68.5) rot=(0,0,1;0rad)
  Solid = false
  Source = -> Face051
  Symmetric = false
FEATURE [Sketcher::SketchObject] Sketch027
  FullyConstrained = true
  sketch-geometry (10):
    g0: LineSegment StartX=-1.6 StartY=4.7 StartZ=0 EndX=-1.6 EndY=1.7 EndZ=0
    g1: LineSegment StartX=-3.5 StartY=4.7 StartZ=0 EndX=-1.6 EndY=4.7 EndZ=0
    g2: LineSegment StartX=-1.6 StartY=1.7 StartZ=0 EndX=-1.6 EndY=1.5 EndZ=0
    g3: LineSegment StartX=-1.6 StartY=1.5 StartZ=0 EndX=-5.2 EndY=1.5 EndZ=0
    g4: Circle CenterX=-3.5 CenterY=4.7 CenterZ=0 NormalX=0 NormalY=0 NormalZ=1 AngleXU=0 Radius=1
    g5: Circle CenterX=-3.59627 CenterY=2.99743 CenterZ=0 NormalX=0 NormalY=0 NormalZ=1 AngleXU=0 Radius=1
    g6: Circle CenterX=-5.2 CenterY=1.5 CenterZ=0 NormalX=0 NormalY=0 NormalZ=1 AngleXU=0 Radius=1
    g7: BSplineCurve PolesCount=3 KnotsCount=2 Degree=2 IsPeriodic=0
    g8: GeomPoint X=-3.5 Y=4.7 Z=0
    g9: GeomPoint X=-5.2 Y=1.5 Z=0
  constraints (23):
    c: Vertical(g0)
    c: Distance(g0) = 3
    c: Coincident(g1,g0)
    c: Horizontal(g1)
    c: Block(g0)
    c: Block(g1)
    c: Coincident(g2,g0)
    c: Vertical(g2)
    c: Distance(g2) = 0.2
    c: Coincident(g3,g2)
    c: Horizontal(g3)
    c: Block(g3)
    c: Coincident(g7,g1)
    c: Weight(g4) = 1
    c: Equal(g4,g5)
    c: Equal(g4,g6)
    c: Coincident(g7,g3)
    c: InternalAlignment(g4,g7)
    c: InternalAlignment(g5,g7)
    c: InternalAlignment(g6,g7)
    c: InternalAlignment(g8,g7)
    c: InternalAlignment(g9,g7)
    c: Block(g7)
FEATURE [Sketcher::SketchObject] Sketch028
  FullyConstrained = true
  sketch-geometry (18):
    g0: LineSegment StartX=0 StartY=3e-16 StartZ=0 EndX=0 EndY=1.7 EndZ=0
    g1: LineSegment StartX=-3.5 StartY=0 StartZ=0 EndX=-3.5 EndY=0.9 EndZ=0
    g2: Circle CenterX=-2.7 CenterY=1.7 CenterZ=0 NormalX=0 NormalY=0 NormalZ=1 AngleXU=0 Radius=1
    g3: Circle CenterX=-3.5 CenterY=1.7 CenterZ=0 NormalX=0 NormalY=0 NormalZ=1 AngleXU=0 Radius=1
    g4: Circle CenterX=-3.5 CenterY=0.9 CenterZ=0 NormalX=0 NormalY=0 NormalZ=1 AngleXU=0 Radius=1
    g5: BSplineCurve PolesCount=3 KnotsCount=2 Degree=2 IsPeriodic=0
    g6: GeomPoint X=-2.7 Y=1.7 Z=0
    g7: GeomPoint X=-3.5 Y=0.9 Z=0
    g8: LineSegment StartX=-3.5 StartY=0 StartZ=0 EndX=-3.5 EndY=-7 EndZ=0
    g9: LineSegment StartX=0 StartY=3e-16 StartZ=0 EndX=0 EndY=-7 EndZ=0
    g10: LineSegment StartX=-3.5 StartY=-7 StartZ=0 EndX=0 EndY=-7 EndZ=0
    g11: LineSegment StartX=-2.7 StartY=1.7 StartZ=0 EndX=-1.6 EndY=1.7 EndZ=0
    g12: LineSegment StartX=0 StartY=1.7 StartZ=0 EndX=0 EndY=4.5 EndZ=0
    g13: LineSegment StartX=0 StartY=4.5 StartZ=0 EndX=0 EndY=10.8 EndZ=0
    g14: LineSegment StartX=0 StartY=10.8 StartZ=0 EndX=-2 EndY=10.8 EndZ=0
    g15: LineSegment StartX=-1.6 StartY=4.7 StartZ=0 EndX=-1.6 EndY=1.7 EndZ=0
    g16: LineSegment StartX=-1.6 StartY=4.7 StartZ=0 EndX=-2 EndY=4.7 EndZ=0
    g17: LineSegment StartX=-2 StartY=4.7 StartZ=0 EndX=-2 EndY=10.8 EndZ=0
  constraints (44):
    c: Vertical(g0)
    c: Vertical(g1)
    c: Distance(g1) = 0.9
    c: Block(g0)
    c: Distance(g0) = 1.7
    c: Weight(g2) = 1
    c: Equal(g2,g3)
    c: Equal(g2,g4)
    c: Coincident(g5,g1)
    c: InternalAlignment(g2,g5)
    c: InternalAlignment(g3,g5)
    c: InternalAlignment(g4,g5)
    c: InternalAlignment(g6,g5)
    c: InternalAlignment(g7,g5)
    c: Block(g5)
    c: Coincident(g8,g1)
    c: Vertical(g8)
    c: Distance(g8) = 7
    c: Vertical(g9)
    c: Equal(g8,g9) = 7
    c: Coincident(g9,g0)
    c: Coincident(g10,g8)
    c: Coincident(g10,g9)
    c: Horizontal(g10)
    c: Coincident(g11,g5)
    c: Horizontal(g11)
    c: Coincident(g12,g0)
    c: Vertical(g12)
    c: Distance(g12) = 2.8
    c: Coincident(g13,g12)
    c: Vertical(g13)
    c: Distance(g13) = 6.3
    c: Coincident(g14,g13)
    c: Horizontal(g14)
    c: Distance(g14) = 2
    c: Vertical(g15)
    c: Distance(g15) = 3
    c: Block(g11)
    c: Coincident(g15,g11)
    c: Coincident(g16,g15)
    c: Horizontal(g16)
    c: Coincident(g17,g16)
    c: Coincident(g17,g14)
    c: Vertical(g17)
FEATURE [Part::Revolution] Revolve040  label="backCaseScrewRetainer001"
  Angle = 360
  Axis = (0,1,0)
  Base = (0,0,0)
  FaceMakerClass = Part::FaceMakerBullseye
  Placement = pos=(12.5,3,10) rot=(0,0,1;0rad)
  Solid = false
  Source = -> Face036
  Symmetric = false
FEATURE [Part::Feature] Face055
  shape: bbox 3.5 x 30.2 x 2e-07 mm, 1 faces, 0 solids (baked)
FEATURE [Part::Revolution] Revolve059  label="backCaseScrewPost"
  Angle = 360
  Axis = (0,1,0)
  Base = (0,0,0)
  FaceMakerClass = Part::FaceMakerBullseye
  Placement = pos=(12.5,4.5,10) rot=(0,0,1;0rad)
  Solid = false
  Source = -> Face055
  Symmetric = false
FEATURE [Part::Feature] Face056
  shape: bbox 3.5 x 30.2 x 2e-07 mm, 1 faces, 0 solids (baked)
FEATURE [Part::Revolution] Revolve060  label="backCaseScrewPost001"
  Angle = 360
  Axis = (0,1,0)
  Base = (0,0,0)
  FaceMakerClass = Part::FaceMakerBullseye
  Placement = pos=(12.5,4.5,62) rot=(0,0,1;0rad)
  Solid = false
  Source = -> Face056
  Symmetric = false
FEATURE [Part::Feature] Face057
  shape: bbox 3.5 x 17.8 x 2e-07 mm, 1 faces, 0 solids (baked)
FEATURE [Part::Revolution] Revolve061  label="removeToCreateScrewAndThreadedInsertHole"
  Angle = 360
  Axis = (0,1,0)
  Base = (0,0,0)
  FaceMakerClass = Part::FaceMakerBullseye
  Placement = pos=(12.5,0,10) rot=(0,0,1;0rad)
  Solid = false
  Source = -> Face057
  Symmetric = false
FEATURE [Part::Feature] Face058
  shape: bbox 3.5 x 17.8 x 2e-07 mm, 1 faces, 0 solids (baked)
FEATURE [Part::Revolution] Revolve062  label="removeToCreateScrewAndThreadedInsertHole001"
  Angle = 360
  Axis = (0,1,0)
  Base = (0,0,0)
  FaceMakerClass = Part::FaceMakerBullseye
  Placement = pos=(12.5,0,62) rot=(0,0,1;0rad)
  Solid = false
  Source = -> Face058
  Symmetric = false
FEATURE [Part::Feature] Face059
  shape: bbox 3.5 x 17.8 x 2e-07 mm, 1 faces, 0 solids (baked)
FEATURE [Part::Revolution] Revolve063  label="removeToCreateScrewAndThreadedInsertHole002"
  Angle = 360
  Axis = (0,1,0)
  Base = (0,0,0)
  FaceMakerClass = Part::FaceMakerBullseye
  Placement = pos=(89.5,0,68.5) rot=(0,0,1;0rad)
  Solid = false
  Source = -> Face059
  Symmetric = false
FEATURE [Part::Feature] Face060
  shape: bbox 3.5 x 17.8 x 2e-07 mm, 1 faces, 0 solids (baked)
FEATURE [Part::Revolution] Revolve064  label="removeToCreateScrewAndThreadedInsertHole003"
  Angle = 360
  Axis = (0,1,0)
  Base = (0,0,0)
  FaceMakerClass = Part::FaceMakerBullseye
  Placement = pos=(89.5,0,3.5) rot=(0,0,1;0rad)
  Solid = false
  Source = -> Face060
  Symmetric = false
FEATURE [Part::Feature] Face061
  shape: bbox 3.5 x 17.8 x 2e-07 mm, 1 faces, 0 solids (baked)
FEATURE [Part::Revolution] Revolve065  label="removeToCreateScrewAndThreadedInsertHole004"
  Angle = 360
  Axis = (0,1,0)
  Base = (0,0,0)
  FaceMakerClass = Part::FaceMakerBullseye
  Placement = pos=(102.5,4.7,3.5) rot=(0,0,1;0rad)
  Solid = false
  Source = -> Face061
  Symmetric = false
FEATURE [Part::Feature] Face062
  shape: bbox 3.5 x 17.8 x 2e-07 mm, 1 faces, 0 solids (baked)
FEATURE [Part::Revolution] Revolve066  label="removeToCreateScrewAndThreadedInsertHole005"
  Angle = 360
  Axis = (0,1,0)
  Base = (0,0,0)
  FaceMakerClass = Part::FaceMakerBullseye
  Placement = pos=(102.5,4.7,68.5) rot=(0,0,1;0rad)
  Solid = false
  Source = -> Face062
  Symmetric = false
FEATURE [Part::MultiFuse] Fusion047  label="makeHoles"
  Shapes = -> [Revolve066,Revolve065,Revolve064,Revolve063,Revolve062,Revolve061]
FEATURE [Part::Feature] Face063
  shape: bbox 3.6 x 3.2 x 2e-07 mm, 1 faces, 0 solids (baked)
FEATURE [Part::Revolution] Revolve067  label="moreFrontCaseScrewRetainer002"
  Angle = 360
  Axis = (0,1,0)
  Base = (0,0,0)
  FaceMakerClass = Part::FaceMakerBullseye
  Placement = pos=(102.5,4.5,68.5) rot=(0,0,1;0rad)
  Solid = false
  Source = -> Face063
  Symmetric = false
FEATURE [Part::Feature] Face064
  shape: bbox 3.6 x 3.2 x 2e-07 mm, 1 faces, 0 solids (baked)
FEATURE [Part::Revolution] Revolve068  label="moreFrontCaseScrewRetainer003"
  Angle = 360
  Axis = (0,1,0)
  Base = (0,0,0)
  FaceMakerClass = Part::FaceMakerBullseye
  Placement = pos=(102.5,4.5,3.5) rot=(0,0,1;0rad)
  Solid = false
  Source = -> Face064
  Symmetric = false
FEATURE [Part::Feature] Face065
  shape: bbox 3.5 x 17.8 x 2e-07 mm, 1 faces, 0 solids (baked)
FEATURE [Part::Revolution] Revolve069  label="removeToCreateScrewAndThreadedInsertHole006"
  Angle = 360
  Axis = (0,1,0)
  Base = (0,0,0)
  FaceMakerClass = Part::FaceMakerBullseye
  Placement = pos=(12.5,0,10) rot=(0,0,1;0rad)
  Solid = false
  Source = -> Face065
  Symmetric = false
FEATURE [Part::Feature] Face066
  shape: bbox 3.5 x 17.8 x 2e-07 mm, 1 faces, 0 solids (baked)
FEATURE [Part::Revolution] Revolve070  label="removeToCreateScrewAndThreadedInsertHole007"
  Angle = 360
  Axis = (0,1,0)
  Base = (0,0,0)
  FaceMakerClass = Part::FaceMakerBullseye
  Placement = pos=(12.5,0,62) rot=(0,0,1;0rad)
  Solid = false
  Source = -> Face066
  Symmetric = false
FEATURE [Part::Feature] Face067
  shape: bbox 3.5 x 17.8 x 2e-07 mm, 1 faces, 0 solids (baked)
FEATURE [Part::Revolution] Revolve071  label="removeToCreateScrewAndThreadedInsertHole008"
  Angle = 360
  Axis = (0,1,0)
  Base = (0,0,0)
  FaceMakerClass = Part::FaceMakerBullseye
  Placement = pos=(89.5,0,68.5) rot=(0,0,1;0rad)
  Solid = false
  Source = -> Face067
  Symmetric = false
FEATURE [Part::Feature] Face068
  shape: bbox 3.5 x 17.8 x 2e-07 mm, 1 faces, 0 solids (baked)
FEATURE [Part::Revolution] Revolve072  label="removeToCreateScrewAndThreadedInsertHole009"
  Angle = 360
  Axis = (0,1,0)
  Base = (0,0,0)
  FaceMakerClass = Part::FaceMakerBullseye
  Placement = pos=(89.5,0,3.5) rot=(0,0,1;0rad)
  Solid = false
  Source = -> Face068
  Symmetric = false
FEATURE [Part::Feature] Face069
  shape: bbox 3.5 x 17.8 x 2e-07 mm, 1 faces, 0 solids (baked)
FEATURE [Part::Feature] Face070
  shape: bbox 3.5 x 17.8 x 2e-07 mm, 1 faces, 0 solids (baked)
FEATURE [Part::Revolution] Revolve073  label="removeToCreateScrewAndThreadedInsertHole010"
  Angle = 360
  Axis = (0,1,0)
  Base = (0,0,0)
  FaceMakerClass = Part::FaceMakerBullseye
  Placement = pos=(102.5,4.7,3.5) rot=(0,0,1;0rad)
  Solid = false
  Source = -> Face069
  Symmetric = false
FEATURE [Part::Revolution] Revolve074  label="removeToCreateScrewAndThreadedInsertHole011"
  Angle = 360
  Axis = (0,1,0)
  Base = (0,0,0)
  FaceMakerClass = Part::FaceMakerBullseye
  Placement = pos=(102.5,4.7,68.5) rot=(0,0,1;0rad)
  Solid = false
  Source = -> Face070
  Symmetric = false
FEATURE [Part::MultiFuse] Fusion048  label="makeHoles001"
  Shapes = -> [Revolve074,Revolve073,Revolve072,Revolve071,Revolve070,Revolve069]
FEATURE [Part::MultiFuse] Fusion049  label="caseScrewRetainers"
  Shapes = -> [Revolve067,Revolve068,Revolve048,Revolve047,Revolve039,Revolve040]
FEATURE [Part::Cut] Cut015  label="caseScrewRetainers001"
  Base = -> Fusion049
  Tool = -> Fusion048
FEATURE [Part::MultiFuse] Fusion050  label="casePillars"
  Shapes = -> [Revolve055,Revolve054,Revolve043,Revolve046,Revolve059,Revolve060]
FEATURE [Part::Feature] Face071 .. Face076  x6 (patterned run collapsed; names and placements below)
  shape: bbox 3.5 x 17.8 x 2e-07 mm, 1 faces, 0 solids (baked)
FEATURE [Part::Revolution] Revolve075  label="removeToCreateScrewAndThreadedInsertHole012"
  Angle = 360
  Axis = (0,1,0)
  Base = (0,0,0)
  FaceMakerClass = Part::FaceMakerBullseye
  Placement = pos=(12.5,0,10) rot=(0,0,1;0rad)
  Solid = false
  Source = -> Face071
  Symmetric = false
FEATURE [Part::Revolution] Revolve076  label="removeToCreateScrewAndThreadedInsertHole013"
  Angle = 360
  Axis = (0,1,0)
  Base = (0,0,0)
  FaceMakerClass = Part::FaceMakerBullseye
  Placement = pos=(12.5,0,62) rot=(0,0,1;0rad)
  Solid = false
  Source = -> Face072
  Symmetric = false
FEATURE [Part::Revolution] Revolve077  label="removeToCreateScrewAndThreadedInsertHole014"
  Angle = 360
  Axis = (0,1,0)
  Base = (0,0,0)
  FaceMakerClass = Part::FaceMakerBullseye
  Placement = pos=(89.5,0,68.5) rot=(0,0,1;0rad)
  Solid = false
  Source = -> Face073
  Symmetric = false
FEATURE [Part::Revolution] Revolve078  label="removeToCreateScrewAndThreadedInsertHole015"
  Angle = 360
  Axis = (0,1,0)
  Base = (0,0,0)
  FaceMakerClass = Part::FaceMakerBullseye
  Placement = pos=(89.5,0,3.5) rot=(0,0,1;0rad)
  Solid = false
  Source = -> Face074
  Symmetric = false
FEATURE [Part::Revolution] Revolve079  label="removeToCreateScrewAndThreadedInsertHole016"
  Angle = 360
  Axis = (0,1,0)
  Base = (0,0,0)
  FaceMakerClass = Part::FaceMakerBullseye
  Placement = pos=(102.5,4.7,3.5) rot=(0,0,1;0rad)
  Solid = false
  Source = -> Face075
  Symmetric = false
FEATURE [Part::Revolution] Revolve080  label="removeToCreateScrewAndThreadedInsertHole017"
  Angle = 360
  Axis = (0,1,0)
  Base = (0,0,0)
  FaceMakerClass = Part::FaceMakerBullseye
  Placement = pos=(102.5,4.7,68.5) rot=(0,0,1;0rad)
  Solid = false
  Source = -> Face076
  Symmetric = false
FEATURE [Part::MultiFuse] Fusion051  label="makeHoles002"
  Shapes = -> [Revolve080,Revolve079,Revolve078,Revolve077,Revolve076,Revolve075]
FEATURE [Part::Cut] Cut016  label="caesPillars"
  Base = -> Fusion050
  Tool = -> Fusion051
FEATURE [Part::Revolution] Revolve009  label="plugHousing016"
  Angle = 360
  Axis = (0,1,0)
  Base = (0,0,0)
  FaceMakerClass = Part::FaceMakerBullseye
  Placement = pos=(0,0,36.15) rot=(0,0,1;0rad)
  Solid = false
  Source = -> Face012
  Symmetric = false
FEATURE [Part::MultiFuse] Fusion014  label="plugHousing023"
  Placement = pos=(0,0,0) rot=(0,0,1;1.5708rad)
  Shapes = -> [Revolve011,Revolve009]
FEATURE [Part::Revolution] Revolve010  label="plugHousing017"
  Angle = 360
  Axis = (0,1,0)
  Base = (0,0,0)
  FaceMakerClass = Part::FaceMakerBullseye
  Placement = pos=(0,0,36.15) rot=(0,0,1;0rad)
  Solid = false
  Source = -> Face014
  Symmetric = false
FEATURE [Part::MultiFuse] Fusion015  label="plugHousing024"
  Placement = pos=(0,0,0) rot=(0,0,1;1.5708rad)
  Shapes = -> [Revolve010,Revolve015]
FEATURE [Part::Revolution] Revolve014  label="plugHousing026"
  Angle = 360
  Axis = (0,1,0)
  Base = (0,0,0)
  FaceMakerClass = Part::FaceMakerBullseye
  Placement = pos=(0,0,36.15) rot=(0,0,1;0rad)
  Solid = false
  Source = -> Face011
  Symmetric = false
FEATURE [Part::Revolution] Revolve013  label="plugHousing025"
  Angle = 360
  Axis = (0,1,0)
  Base = (0,0,0)
  FaceMakerClass = Part::FaceMakerBullseye
  Placement = pos=(0,0,36.15) rot=(0,0,1;0rad)
  Solid = false
  Source = -> Face015
  Symmetric = false
FEATURE [Part::MultiFuse] Fusion016  label="plugHousing028"
  Placement = pos=(0,19,0) rot=(0,0,1;3.14159rad)
  Shapes = -> [Fusion014,Fusion013]
FEATURE [Part::MultiFuse] Fusion011  label="plugHousing018"
  Placement = pos=(0,0,0) rot=(0,0,1;1.5708rad)
  Shapes = -> [Revolve014,Revolve013]
FEATURE [Part::MultiFuse] Fusion012  label="plugHousing019"
  Placement = pos=(0,19,0) rot=(0,0,1;3.14159rad)
  Shapes = -> [Fusion011,Fusion015]
FEATURE [Part::MultiFuse] Fusion017  label="plugHousing029"
  Placement = pos=(122.621,0,-0.15) rot=(0,0,1;0rad)
  Shapes = -> [Fusion016,Fusion012]
FEATURE [Part::MultiFuse] Fusion052  label="casePillarRetainers"
  Shapes = -> [Extrude012,Extrude013,Extrude014,Extrude015,Extrude016,Extrude017,Extrude018,Extrude019,Box011,Box012]
FEATURE [Part::Feature] Face077
  shape: bbox 3.5 x 17.8 x 2e-07 mm, 1 faces, 0 solids (baked)
FEATURE [Part::Revolution] Revolve081  label="removeToCreateScrewAndThreadedInsertHole018"
  Angle = 360
  Axis = (0,1,0)
  Base = (0,0,0)
  FaceMakerClass = Part::FaceMakerBullseye
  Placement = pos=(62.3,30.3,19.7) rot=(0,0,1;0rad)
  Solid = false
  Source = -> Face077
  Symmetric = false
FEATURE [Part::Feature] Face078
  shape: bbox 3.5 x 17.8 x 2e-07 mm, 1 faces, 0 solids (baked)
FEATURE [Part::Revolution] Revolve082  label="removeToCreateScrewAndThreadedInsertHole019"
  Angle = 360
  Axis = (0,1,0)
  Base = (0,0,0)
  FaceMakerClass = Part::FaceMakerBullseye
  Placement = pos=(62.3,30.3,51.7) rot=(0,0,1;0rad)
  Solid = false
  Source = -> Face078
  Symmetric = false
FEATURE [Part::Feature] Face079
  shape: bbox 3.5 x 17.8 x 2e-07 mm, 1 faces, 0 solids (baked)
FEATURE [Part::Revolution] Revolve083  label="removeToCreateScrewAndThreadedInsertHole020"
  Angle = 360
  Axis = (0,1,0)
  Base = (0,0,0)
  FaceMakerClass = Part::FaceMakerBullseye
  Placement = pos=(30.3,30.3,19.7) rot=(0,0,1;0rad)
  Solid = false
  Source = -> Face079
  Symmetric = false
FEATURE [Part::Feature] Face080
  shape: bbox 3.5 x 17.8 x 2e-07 mm, 1 faces, 0 solids (baked)
FEATURE [Part::Revolution] Revolve084  label="removeToCreateScrewAndThreadedInsertHole021"
  Angle = 360
  Axis = (0,1,0)
  Base = (0,0,0)
  FaceMakerClass = Part::FaceMakerBullseye
  Placement = pos=(30.3,30.3,51.7) rot=(0,0,1;0rad)
  Solid = false
  Source = -> Face080
  Symmetric = false
FEATURE [Part::MultiFuse] Fusion053  label="createThreadedInsertHolesForFan"
  Shapes = -> [Revolve081,Revolve082,Revolve083,Revolve084]
FEATURE [Part::Cut] Cut017  label="fanScrewHousing001"
  Base = -> Fusion046
  Tool = -> Fusion053
FEATURE [Part::Feature] Face081
  shape: bbox 3.5 x 17.8 x 2e-07 mm, 1 faces, 0 solids (baked)
FEATURE [Part::Revolution] Revolve085  label="removeToCreateScrewAndThreadedInsertHole022"
  Angle = 360
  Axis = (0,1,0)
  Base = (0,0,0)
  FaceMakerClass = Part::FaceMakerBullseye
  Placement = pos=(62.3,30.3,19.7) rot=(0,0,1;0rad)
  Solid = false
  Source = -> Face081
  Symmetric = false
FEATURE [Part::Feature] Face082
  shape: bbox 3.5 x 17.8 x 2e-07 mm, 1 faces, 0 solids (baked)
FEATURE [Part::Revolution] Revolve086  label="removeToCreateScrewAndThreadedInsertHole023"
  Angle = 360
  Axis = (0,1,0)
  Base = (0,0,0)
  FaceMakerClass = Part::FaceMakerBullseye
  Placement = pos=(62.3,30.3,51.7) rot=(0,0,1;0rad)
  Solid = false
  Source = -> Face082
  Symmetric = false
FEATURE [Part::Feature] Face083
  shape: bbox 3.5 x 17.8 x 2e-07 mm, 1 faces, 0 solids (baked)
FEATURE [Part::Revolution] Revolve087  label="removeToCreateScrewAndThreadedInsertHole024"
  Angle = 360
  Axis = (0,1,0)
  Base = (0,0,0)
  FaceMakerClass = Part::FaceMakerBullseye
  Placement = pos=(30.3,30.3,19.7) rot=(0,0,1;0rad)
  Solid = false
  Source = -> Face083
  Symmetric = false
FEATURE [Part::Feature] Face084
  shape: bbox 3.5 x 17.8 x 2e-07 mm, 1 faces, 0 solids (baked)
FEATURE [Part::Revolution] Revolve088  label="removeToCreateScrewAndThreadedInsertHole025"
  Angle = 360
  Axis = (0,1,0)
  Base = (0,0,0)
  FaceMakerClass = Part::FaceMakerBullseye
  Placement = pos=(30.3,30.3,51.7) rot=(0,0,1;0rad)
  Solid = false
  Source = -> Face084
  Symmetric = false
FEATURE [Part::MultiFuse] Fusion054  label="createThreadedInsertHolesForFan001"
  Shapes = -> [Revolve085,Revolve086,Revolve087,Revolve088]
FEATURE [Part::Cut] Cut018  label="top007"
  Base = -> Fusion040
  Tool = -> Fusion054
FEATURE [Sketcher::SketchObject] Sketch029
  FullyConstrained = false
  Placement = pos=(0,0,0) rot=(1,0,0;1.5708rad)
  sketch-geometry (24):
    g0: ArcOfCircle CenterX=-4 CenterY=-10.5 CenterZ=0 NormalX=0 NormalY=0 NormalZ=1 AngleXU=0 Radius=1.5 StartAngle=6e-16 EndAngle=3.14159
    g1: ArcOfCircle CenterX=-34.2 CenterY=-10.5 CenterZ=0 NormalX=0 NormalY=0 NormalZ=1 AngleXU=0 Radius=1.5 StartAngle=0 EndAngle=3.14159
    g2: ArcOfCircle CenterX=-34.2 CenterY=-27.7 CenterZ=0 NormalX=0 NormalY=0 NormalZ=1 AngleXU=0 Radius=1.5 StartAngle=3.14159 EndAngle=6.28319
    g3: ArcOfCircle CenterX=-4 CenterY=-27.7 CenterZ=0 NormalX=0 NormalY=0 NormalZ=1 AngleXU=0 Radius=1.5 StartAngle=3.1416 EndAngle=6.28319
    g4: ArcOfCircle CenterX=-10 CenterY=-4.3 CenterZ=0 NormalX=0 NormalY=0 NormalZ=1 AngleXU=0 Radius=1.5 StartAngle=2e-16 EndAngle=3.14159
    g5: ArcOfCircle CenterX=-16.1 CenterY=-1.8 CenterZ=0 NormalX=0 NormalY=0 NormalZ=1 AngleXU=0 Radius=1.5 StartAngle=5e-16 EndAngle=3.14159
    g6: ArcOfCircle CenterX=-22.1 CenterY=-1.8 CenterZ=0 NormalX=0 NormalY=0 NormalZ=1 AngleXU=0 Radius=1.5 StartAngle=5e-16 EndAngle=3.14159
    g7: ArcOfCircle CenterX=-28.2 CenterY=-4.3 CenterZ=0 NormalX=0 NormalY=0 NormalZ=1 AngleXU=0 Radius=1.5 StartAngle=2e-16 EndAngle=3.14159
    g8: ArcOfCircle CenterX=-10 CenterY=-33.9 CenterZ=0 NormalX=0 NormalY=0 NormalZ=1 AngleXU=0 Radius=1.5 StartAngle=3.14159 EndAngle=6.28319
    g9: ArcOfCircle CenterX=-16.1 CenterY=-36.4 CenterZ=0 NormalX=0 NormalY=0 NormalZ=1 AngleXU=0 Radius=1.5 StartAngle=3.14159 EndAngle=6.28319
    g10: ArcOfCircle CenterX=-22.1 CenterY=-36.4 CenterZ=0 NormalX=0 NormalY=0 NormalZ=1 AngleXU=0 Radius=1.5 StartAngle=3.14159 EndAngle=6.28319
    g11: ArcOfCircle CenterX=-28.2 CenterY=-33.9 CenterZ=0 NormalX=0 NormalY=0 NormalZ=1 AngleXU=0 Radius=1.5 StartAngle=3.14159 EndAngle=6.28319
    g12: LineSegment StartX=-35.7 StartY=-10.5 StartZ=0 EndX=-35.7 EndY=-27.7 EndZ=0
    g13: LineSegment StartX=-32.7 StartY=-10.5 StartZ=0 EndX=-32.7 EndY=-27.7 EndZ=0
    g14: LineSegment StartX=-29.7 StartY=-33.9 StartZ=0 EndX=-29.7 EndY=-4.3 EndZ=0
    g15: LineSegment StartX=-26.7 StartY=-33.9 StartZ=0 EndX=-26.7 EndY=-4.3 EndZ=0
    g16: LineSegment StartX=-2.5 StartY=-10.5 StartZ=0 EndX=-2.5 EndY=-27.7 EndZ=0
    g17: LineSegment StartX=-8.5 StartY=-4.3 StartZ=0 EndX=-8.5 EndY=-33.9 EndZ=0
    g18: LineSegment StartX=-5.5 StartY=-10.5 StartZ=0 EndX=-5.5 EndY=-27.7 EndZ=0
    g19: LineSegment StartX=-11.5 StartY=-4.3 StartZ=0 EndX=-11.5 EndY=-33.9 EndZ=0
    g20: LineSegment StartX=-14.6 StartY=-1.8 StartZ=0 EndX=-14.6 EndY=-36.4 EndZ=0
    g21: LineSegment StartX=-17.6 StartY=-1.8 StartZ=0 EndX=-17.6 EndY=-36.4 EndZ=0
    g22: LineSegment StartX=-20.6 StartY=-36.4 StartZ=0 EndX=-20.6 EndY=-1.8 EndZ=0
    g23: LineSegment StartX=-23.6 StartY=-1.8 StartZ=0 EndX=-23.6 EndY=-36.4 EndZ=0
  constraints (48):
    c: Block(g0)
    c: Block(g1)
    c: Block(g2)
    c: Block(g3)
    c: Block(g4)
    c: Block(g5)
    c: Block(g6)
    c: Block(g7)
    c: Block(g8)
    c: Block(g9)
    c: Block(g10)
    c: Block(g11)
    c: Coincident(g12,g1)
    c: Coincident(g12,g2)
    c: Vertical(g12)
    c: Coincident(g13,g1)
    c: Coincident(g13,g2)
    c: Vertical(g13)
    c: Coincident(g14,g11)
    c: Coincident(g14,g7)
    c: Vertical(g14)
    c: Coincident(g15,g11)
    c: Coincident(g15,g7)
    c: Vertical(g15)
    c: Coincident(g16,g0)
    c: Coincident(g16,g3)
    c: Vertical(g16)
    c: Coincident(g17,g4)
    c: Coincident(g17,g8)
    c: Vertical(g17)
    c: Coincident(g18,g0)
    c: Coincident(g18,g3)
    c: Vertical(g18)
    c: Coincident(g19,g4)
    c: Coincident(g19,g8)
    c: Vertical(g19)
    c: Coincident(g20,g5)
    c: Coincident(g20,g9)
    c: Vertical(g20)
    c: Coincident(g21,g5)
    c: Coincident(g21,g9)
    c: Vertical(g21)
    c: Coincident(g22,g10)
    c: Coincident(g22,g6)
    c: Vertical(g22)
    c: Coincident(g23,g6)
    c: Coincident(g23,g10)
    c: Vertical(g23)
FEATURE [Part::Extrusion] Extrude020  label="removeToCreateFanGrillHoles"
  Base = -> Sketch029
  Dir = (0,-1,6e-16)
  DirMode = 2
  FaceMakerClass = Part::FaceMakerBullseye
  LengthFwd = 10
  LengthRev = 0
  Placement = pos=(65.4,44,54.82) rot=(0,0,1;0rad)
  Solid = true
  Symmetric = false
FEATURE [Part::MultiFuse] Fusion055  label="top008"
  Shapes = -> [Cut017,Cut018]
FEATURE [Part::Cut] Cut019  label="top009"
  Base = -> Fusion055
  Tool = -> Extrude020
FEATURE [App::MeasureDistance] Distance003  label="Distance: 71.95 mm"
  Distance = 71.9513
  P1 = (117,38,72)
  P2 = (117,38,0.0487319)
FEATURE [Sketcher::SketchObject] Sketch030
  FullyConstrained = true
  Placement = pos=(117,19,0) rot=(0.57735,0.57735,0.57735;2.0944rad)
  sketch-geometry (48):
    g0: LineSegment StartX=-49.19 StartY=69.25 StartZ=0 EndX=-49.19 EndY=66.25 EndZ=0
    g1: LineSegment StartX=-49.19 StartY=63.5 StartZ=0 EndX=-49.19 EndY=60.5 EndZ=0
    g2: LineSegment StartX=-49.19 StartY=57.75 StartZ=0 EndX=-49.19 EndY=54.75 EndZ=0
    g3: LineSegment StartX=-49.19 StartY=52 StartZ=0 EndX=-49.19 EndY=49 EndZ=0
    g4: LineSegment StartX=-49.19 StartY=46.25 StartZ=0 EndX=-49.19 EndY=43.25 EndZ=0
    g5: LineSegment StartX=-49.19 StartY=40.5 StartZ=0 EndX=-49.19 EndY=37.5 EndZ=0
    g6: LineSegment StartX=-49.19 StartY=34.5 StartZ=0 EndX=-49.19 EndY=31.5 EndZ=0
    g7: LineSegment StartX=-49.19 StartY=28.75 StartZ=0 EndX=-49.19 EndY=25.75 EndZ=0
    g8: LineSegment StartX=-49.19 StartY=23 StartZ=0 EndX=-49.19 EndY=20 EndZ=0
    g9: LineSegment StartX=-49.19 StartY=17.25 StartZ=0 EndX=-49.19 EndY=14.25 EndZ=0
    g10: LineSegment StartX=-49.19 StartY=11.5 StartZ=0 EndX=-49.19 EndY=8.5 EndZ=0
    g11: LineSegment StartX=-49.19 StartY=5.75 StartZ=0 EndX=-49.19 EndY=2.75 EndZ=0
    g12: ArcOfCircle CenterX=-1.5 CenterY=67.75 CenterZ=0 NormalX=0 NormalY=0 NormalZ=1 AngleXU=0 Radius=1.5 StartAngle=4.71239 EndAngle=7.85398
    g13: ArcOfCircle CenterX=-1.5 CenterY=62 CenterZ=0 NormalX=0 NormalY=0 NormalZ=1 AngleXU=0 Radius=1.5 StartAngle=4.71239 EndAngle=7.85398
    g14: ArcOfCircle CenterX=-1.5 CenterY=56.25 CenterZ=0 NormalX=0 NormalY=0 NormalZ=1 AngleXU=0 Radius=1.5 StartAngle=4.71239 EndAngle=7.85398
    g15: ArcOfCircle CenterX=-11.49 CenterY=50.5 CenterZ=0 NormalX=0 NormalY=0 NormalZ=1 AngleXU=0 Radius=1.5 StartAngle=4.71239 EndAngle=7.85398
    g16: ArcOfCircle CenterX=-16.28 CenterY=44.75 CenterZ=0 NormalX=0 NormalY=0 NormalZ=1 AngleXU=0 Radius=1.5 StartAngle=4.71239 EndAngle=7.85398
    g17: ArcOfCircle CenterX=-18.2337 CenterY=39 CenterZ=0 NormalX=0 NormalY=0 NormalZ=1 AngleXU=0 Radius=1.5 StartAngle=4.71485 EndAngle=7.85398
    g18: ArcOfCircle CenterX=-16.2837 CenterY=27.25 CenterZ=0 NormalX=0 NormalY=0 NormalZ=1 AngleXU=0 Radius=1.5 StartAngle=4.71485 EndAngle=7.85398
    g19: ArcOfCircle CenterX=-18.2337 CenterY=33 CenterZ=0 NormalX=0 NormalY=0 NormalZ=1 AngleXU=0 Radius=1.5 StartAngle=4.71485 EndAngle=7.85398
    g20: ArcOfCircle CenterX=-11.49 CenterY=21.5 CenterZ=0 NormalX=0 NormalY=0 NormalZ=1 AngleXU=0 Radius=1.5 StartAngle=4.71239 EndAngle=7.85398
    g21: ArcOfCircle CenterX=-1.5 CenterY=4.25 CenterZ=0 NormalX=0 NormalY=0 NormalZ=1 AngleXU=0 Radius=1.5 StartAngle=4.71239 EndAngle=7.85398
    g22: ArcOfCircle CenterX=-1.5 CenterY=10 CenterZ=0 NormalX=0 NormalY=0 NormalZ=1 AngleXU=0 Radius=1.5 StartAngle=4.71239 EndAngle=7.85398
    g23: ArcOfCircle CenterX=-1.5 CenterY=15.75 CenterZ=0 NormalX=0 NormalY=0 NormalZ=1 AngleXU=0 Radius=1.5 StartAngle=4.71239 EndAngle=7.85398
    g24: LineSegment StartX=-49.19 StartY=69.25 StartZ=0 EndX=-1.5 EndY=69.25 EndZ=0
    g25: LineSegment StartX=-49.19 StartY=66.25 StartZ=0 EndX=-1.5 EndY=66.25 EndZ=0
    g26: LineSegment StartX=-49.19 StartY=63.5 StartZ=0 EndX=-1.5 EndY=63.5 EndZ=0
    g27: LineSegment StartX=-49.19 StartY=60.5 StartZ=0 EndX=-1.5 EndY=60.5 EndZ=0
    g28: LineSegment StartX=-49.19 StartY=57.75 StartZ=0 EndX=-1.5 EndY=57.75 EndZ=0
    g29: LineSegment StartX=-49.19 StartY=54.75 StartZ=0 EndX=-1.5 EndY=54.75 EndZ=0
    g30: LineSegment StartX=-49.19 StartY=52 StartZ=0 EndX=-11.49 EndY=52 EndZ=0
    g31: LineSegment StartX=-49.19 StartY=49 StartZ=0 EndX=-11.49 EndY=49 EndZ=0
    g32: LineSegment StartX=-49.19 StartY=46.25 StartZ=0 EndX=-16.28 EndY=46.25 EndZ=0
    g33: LineSegment StartX=-49.19 StartY=43.25 StartZ=0 EndX=-16.28 EndY=43.25 EndZ=0
    g34: LineSegment StartX=-49.19 StartY=40.5 StartZ=0 EndX=-18.2337 EndY=40.5 EndZ=0
    g35: LineSegment StartX=-49.19 StartY=37.5 StartZ=0 EndX=-18.23 EndY=37.5 EndZ=0
    g36: LineSegment StartX=-49.19 StartY=34.5 StartZ=0 EndX=-18.2337 EndY=34.5 EndZ=0
    g37: LineSegment StartX=-49.19 StartY=31.5 StartZ=0 EndX=-18.23 EndY=31.5 EndZ=0
    g38: LineSegment StartX=-49.19 StartY=28.75 StartZ=0 EndX=-16.2837 EndY=28.75 EndZ=0
    g39: LineSegment StartX=-49.19 StartY=25.75 StartZ=0 EndX=-16.28 EndY=25.75 EndZ=0
    g40: LineSegment StartX=-49.19 StartY=23 StartZ=0 EndX=-11.49 EndY=23 EndZ=0
    g41: LineSegment StartX=-49.19 StartY=20 StartZ=0 EndX=-11.49 EndY=20 EndZ=0
    g42: LineSegment StartX=-49.19 StartY=17.25 StartZ=0 EndX=-1.5 EndY=17.25 EndZ=0
    g43: LineSegment StartX=-49.19 StartY=14.25 StartZ=0 EndX=-1.5 EndY=14.25 EndZ=0
    g44: LineSegment StartX=-49.19 StartY=11.5 StartZ=0 EndX=-1.5 EndY=11.5 EndZ=0
    g45: LineSegment StartX=-49.19 StartY=8.5 StartZ=0 EndX=-1.5 EndY=8.5 EndZ=0
    g46: LineSegment StartX=-49.19 StartY=5.75 StartZ=0 EndX=-1.5 EndY=5.75 EndZ=0
    g47: LineSegment StartX=-49.19 StartY=2.75 StartZ=0 EndX=-1.5 EndY=2.75 EndZ=0
  constraints (120):
    c: Vertical(g0)
    c: Distance(g0) = 3
    c: Block(g0)
    c: Vertical(g1)
    c: Distance(g1) = 3
    c: Vertical(g2)
    c: Equal(g0,g2) = 3
    c: Block(g2)
    c: Vertical(g3)
    c: Equal(g1,g3) = 3
    c: Vertical(g4)
    c: Equal(g0,g4) = 3
    c: Block(g4)
    c: Vertical(g5)
    c: Equal(g1,g5) = 3
    c: Vertical(g6)
    c: Equal(g0,g6) = 3
    c: Block(g6)
    c: Vertical(g7)
    c: Equal(g1,g7) = 3
    c: Vertical(g8)
    c: Equal(g0,g8) = 3
    c: Block(g8)
    c: Vertical(g9)
    c: Equal(g1,g9) = 3
    c: Vertical(g10)
    c: Equal(g0,g10) = 3
    c: Block(g10)
    c: Vertical(g11)
    c: Equal(g1,g11) = 3
    c: Block(g12)
    c: Block(g13)
    c: Block(g14)
    c: Block(g15)
    c: Block(g16)
    c: Block(g17)
    c: Block(g18)
    c: Block(g19)
    c: Block(g20)
    c: Block(g21)
    c: Block(g22)
    c: Block(g23)
    c: Block(g11)
    c: Block(g9)
    c: Block(g7)
    c: Block(g5)
    c: Block(g3)
    c: Block(g1)
    c: Coincident(g24,g0)
    c: Coincident(g24,g12)
    c: Horizontal(g24)
    c: Coincident(g25,g0)
    c: Coincident(g25,g12)
    c: Horizontal(g25)
    c: Coincident(g26,g1)
    c: Coincident(g26,g13)
    c: Horizontal(g26)
    c: Coincident(g27,g1)
    c: Coincident(g27,g13)
    c: Horizontal(g27)
    c: Coincident(g28,g2)
    c: Coincident(g28,g14)
    c: Horizontal(g28)
    c: Coincident(g29,g2)
    c: Coincident(g29,g14)
    c: Horizontal(g29)
    c: Coincident(g30,g3)
    c: Coincident(g30,g15)
    c: Horizontal(g30)
    c: Coincident(g31,g3)
    c: Coincident(g31,g15)
    c: Horizontal(g31)
    c: Coincident(g32,g4)
    c: Coincident(g32,g16)
    c: Horizontal(g32)
    c: Coincident(g33,g4)
    c: Coincident(g33,g16)
    c: Horizontal(g33)
    c: Coincident(g34,g5)
    c: Coincident(g34,g17)
    c: Horizontal(g34)
    c: Coincident(g35,g5)
    c: Coincident(g35,g17)
    c: Horizontal(g35)
    c: Coincident(g36,g6)
    c: Coincident(g36,g19)
    c: Horizontal(g36)
    c: Coincident(g37,g6)
    c: Coincident(g37,g19)
    c: Horizontal(g37)
    c: Coincident(g38,g7)
    c: Coincident(g38,g18)
    c: Horizontal(g38)
    c: Coincident(g39,g7)
    c: Coincident(g39,g18)
    c: Horizontal(g39)
    c: Coincident(g40,g8)
    c: Coincident(g40,g20)
    c: Horizontal(g40)
    c: Coincident(g41,g8)
    c: Coincident(g41,g20)
    c: Horizontal(g41)
    c: Coincident(g42,g9)
    c: Coincident(g42,g23)
    c: Horizontal(g42)
    c: Coincident(g43,g9)
    c: Coincident(g43,g23)
    c: Horizontal(g43)
    c: Coincident(g44,g10)
    c: Coincident(g44,g22)
    c: Horizontal(g44)
    c: Coincident(g45,g10)
    c: Coincident(g45,g22)
    c: Horizontal(g45)
    c: Coincident(g46,g11)
    c: Coincident(g46,g21)
    c: Horizontal(g46)
    c: Coincident(g47,g11)
    c: Coincident(g47,g21)
    c: Horizontal(g47)
FEATURE [Sketcher::SketchObject] Sketch031
  FullyConstrained = true
  Placement = pos=(117,19,0) rot=(0.57735,0.57735,0.57735;2.0944rad)
  sketch-geometry (24):
    g0: ArcOfCircle CenterX=-49.19 CenterY=67.75 CenterZ=0 NormalX=0 NormalY=0 NormalZ=1 AngleXU=0 Radius=1.5 StartAngle=1.5708 EndAngle=4.71239
    g1: ArcOfCircle CenterX=-49.19 CenterY=62 CenterZ=0 NormalX=0 NormalY=0 NormalZ=1 AngleXU=0 Radius=1.5 StartAngle=1.5708 EndAngle=4.71239
    g2: ArcOfCircle CenterX=-49.19 CenterY=56.25 CenterZ=0 NormalX=0 NormalY=0 NormalZ=1 AngleXU=0 Radius=1.5 StartAngle=1.5708 EndAngle=4.71239
    g3: ArcOfCircle CenterX=-49.19 CenterY=50.5 CenterZ=0 NormalX=0 NormalY=0 NormalZ=1 AngleXU=0 Radius=1.5 StartAngle=1.5708 EndAngle=4.71239
    g4: ArcOfCircle CenterX=-49.19 CenterY=44.75 CenterZ=0 NormalX=0 NormalY=0 NormalZ=1 AngleXU=0 Radius=1.5 StartAngle=1.5708 EndAngle=4.71239
    g5: ArcOfCircle CenterX=-49.19 CenterY=39 CenterZ=0 NormalX=0 NormalY=0 NormalZ=1 AngleXU=0 Radius=1.5 StartAngle=1.5708 EndAngle=4.71239
    g6: ArcOfCircle CenterX=-49.19 CenterY=33 CenterZ=0 NormalX=0 NormalY=0 NormalZ=1 AngleXU=0 Radius=1.5 StartAngle=1.5708 EndAngle=4.71239
    g7: ArcOfCircle CenterX=-49.19 CenterY=27.25 CenterZ=0 NormalX=0 NormalY=0 NormalZ=1 AngleXU=0 Radius=1.5 StartAngle=1.5708 EndAngle=4.71239
    g8: ArcOfCircle CenterX=-49.19 CenterY=21.5 CenterZ=0 NormalX=0 NormalY=0 NormalZ=1 AngleXU=0 Radius=1.5 StartAngle=1.5708 EndAngle=4.71239
    g9: ArcOfCircle CenterX=-49.19 CenterY=15.75 CenterZ=0 NormalX=0 NormalY=0 NormalZ=1 AngleXU=0 Radius=1.5 StartAngle=1.5708 EndAngle=4.71239
    g10: ArcOfCircle CenterX=-49.19 CenterY=10 CenterZ=0 NormalX=0 NormalY=0 NormalZ=1 AngleXU=0 Radius=1.5 StartAngle=1.5708 EndAngle=4.71239
    g11: ArcOfCircle CenterX=-49.19 CenterY=4.25 CenterZ=0 NormalX=0 NormalY=0 NormalZ=1 AngleXU=0 Radius=1.5 StartAngle=1.5708 EndAngle=4.71239
    g12: LineSegment StartX=-49.19 StartY=69.25 StartZ=0 EndX=-49.19 EndY=66.25 EndZ=0
    g13: LineSegment StartX=-49.19 StartY=63.5 StartZ=0 EndX=-49.19 EndY=60.5 EndZ=0
    g14: LineSegment StartX=-49.19 StartY=57.75 StartZ=0 EndX=-49.19 EndY=54.75 EndZ=0
    g15: LineSegment StartX=-49.19 StartY=52 StartZ=0 EndX=-49.19 EndY=49 EndZ=0
    g16: LineSegment StartX=-49.19 StartY=46.25 StartZ=0 EndX=-49.19 EndY=43.25 EndZ=0
    g17: LineSegment StartX=-49.19 StartY=40.5 StartZ=0 EndX=-49.19 EndY=37.5 EndZ=0
    g18: LineSegment StartX=-49.19 StartY=34.5 StartZ=0 EndX=-49.19 EndY=31.5 EndZ=0
    g19: LineSegment StartX=-49.19 StartY=28.75 StartZ=0 EndX=-49.19 EndY=25.75 EndZ=0
    g20: LineSegment StartX=-49.19 StartY=23 StartZ=0 EndX=-49.19 EndY=20 EndZ=0
    g21: LineSegment StartX=-49.19 StartY=17.25 StartZ=0 EndX=-49.19 EndY=14.25 EndZ=0
    g22: LineSegment StartX=-49.19 StartY=11.5 StartZ=0 EndX=-49.19 EndY=8.5 EndZ=0
    g23: LineSegment StartX=-49.19 StartY=5.75 StartZ=0 EndX=-49.19 EndY=2.75 EndZ=0
  constraints (48):
    c: Block(g0)
    c: Block(g1)
    c: Block(g2)
    c: Block(g3)
    c: Block(g4)
    c: Block(g5)
    c: Block(g6)
    c: Block(g7)
    c: Block(g8)
    c: Block(g9)
    c: Block(g10)
    c: Block(g11)
    c: Coincident(g12,g0)
    c: Coincident(g12,g0)
    c: Vertical(g12)
    c: Vertical(g13)
    c: Coincident(g13,g1)
    c: Vertical(g14)
    c: Coincident(g14,g2)
    c: Vertical(g15)
    c: Coincident(g15,g3)
    c: Vertical(g16)
    c: Coincident(g16,g4)
    c: Vertical(g17)
    c: Coincident(g17,g5)
    c: Vertical(g18)
    c: Coincident(g18,g6)
    c: Vertical(g19)
    c: Coincident(g19,g7)
    c: Vertical(g20)
    c: Coincident(g20,g8)
    c: Vertical(g21)
    c: Coincident(g21,g9)
    c: Vertical(g22)
    c: Coincident(g22,g10)
    c: Vertical(g23)
    c: Coincident(g23,g11)
    c: Block(g23)
    c: Block(g22)
    c: Block(g21)
    c: Block(g20)
    c: Block(g13)
    c: Block(g14)
    c: Block(g15)
    c: Block(g16)
    c: Block(g17)
    c: Block(g18)
    c: Block(g19)
FEATURE [Part::Extrusion] Extrude022
  Base = -> Sketch030
  Dir = (1,-2e-16,2e-16)
  DirMode = 2
  FaceMakerClass = Part::FaceMakerBullseye
  LengthFwd = 19
  LengthRev = 0
  Placement = pos=(-19,0,0) rot=(0,0,1;0rad)
  Solid = true
  Symmetric = false
FEATURE [Part::Fillet] Fillet022
  Base = -> Extrude022
  Edges = 24 edges r=1.49: [Edge6,Edge11,Edge18,Edge23,Edge30,Edge35,Edge42,Edge47,Edge54,Edge59,Edge66,Edge71,Edge78,Edge83,Edge90,Edge95,Edge102,Edge107,Edge114,Edge119,Edge126,Edge131,Edge138,Edge143]
FEATURE [Part::Cut] Cut020  label="top010"
  Base = -> Cut019
  Tool = -> Fillet022
FEATURE [Sketcher::SketchObject] Sketch032
  FullyConstrained = true
  Placement = pos=(117,19,0) rot=(0.57735,0.57735,0.57735;2.0944rad)
  sketch-geometry (48):
    g0: LineSegment StartX=-49.19 StartY=69.25 StartZ=0 EndX=-49.19 EndY=66.25 EndZ=0
    g1: LineSegment StartX=-49.19 StartY=63.5 StartZ=0 EndX=-49.19 EndY=60.5 EndZ=0
    g2: LineSegment StartX=-49.19 StartY=57.75 StartZ=0 EndX=-49.19 EndY=54.75 EndZ=0
    g3: LineSegment StartX=-49.19 StartY=52 StartZ=0 EndX=-49.19 EndY=49 EndZ=0
    g4: LineSegment StartX=-49.19 StartY=46.25 StartZ=0 EndX=-49.19 EndY=43.25 EndZ=0
    g5: LineSegment StartX=-49.19 StartY=40.5 StartZ=0 EndX=-49.19 EndY=37.5 EndZ=0
    g6: LineSegment StartX=-49.19 StartY=34.5 StartZ=0 EndX=-49.19 EndY=31.5 EndZ=0
    g7: LineSegment StartX=-49.19 StartY=28.75 StartZ=0 EndX=-49.19 EndY=25.75 EndZ=0
    g8: LineSegment StartX=-49.19 StartY=23 StartZ=0 EndX=-49.19 EndY=20 EndZ=0
    g9: LineSegment StartX=-49.19 StartY=17.25 StartZ=0 EndX=-49.19 EndY=14.25 EndZ=0
    g10: LineSegment StartX=-49.19 StartY=11.5 StartZ=0 EndX=-49.19 EndY=8.5 EndZ=0
    g11: LineSegment StartX=-49.19 StartY=5.75 StartZ=0 EndX=-49.19 EndY=2.75 EndZ=0
    g12: ArcOfCircle CenterX=-1.5 CenterY=67.75 CenterZ=0 NormalX=0 NormalY=0 NormalZ=1 AngleXU=0 Radius=1.5 StartAngle=4.71239 EndAngle=7.85398
    g13: ArcOfCircle CenterX=-1.5 CenterY=62 CenterZ=0 NormalX=0 NormalY=0 NormalZ=1 AngleXU=0 Radius=1.5 StartAngle=4.71239 EndAngle=7.85398
    g14: ArcOfCircle CenterX=-1.5 CenterY=56.25 CenterZ=0 NormalX=0 NormalY=0 NormalZ=1 AngleXU=0 Radius=1.5 StartAngle=4.71239 EndAngle=7.85398
    g15: ArcOfCircle CenterX=-11.49 CenterY=50.5 CenterZ=0 NormalX=0 NormalY=0 NormalZ=1 AngleXU=0 Radius=1.5 StartAngle=4.71239 EndAngle=7.85398
    g16: ArcOfCircle CenterX=-16.28 CenterY=44.75 CenterZ=0 NormalX=0 NormalY=0 NormalZ=1 AngleXU=0 Radius=1.5 StartAngle=4.71239 EndAngle=7.85398
    g17: ArcOfCircle CenterX=-18.2337 CenterY=39 CenterZ=0 NormalX=0 NormalY=0 NormalZ=1 AngleXU=0 Radius=1.5 StartAngle=4.71485 EndAngle=7.85398
    g18: ArcOfCircle CenterX=-16.2837 CenterY=27.25 CenterZ=0 NormalX=0 NormalY=0 NormalZ=1 AngleXU=0 Radius=1.5 StartAngle=4.71485 EndAngle=7.85398
    g19: ArcOfCircle CenterX=-18.2337 CenterY=33 CenterZ=0 NormalX=0 NormalY=0 NormalZ=1 AngleXU=0 Radius=1.5 StartAngle=4.71485 EndAngle=7.85398
    g20: ArcOfCircle CenterX=-11.49 CenterY=21.5 CenterZ=0 NormalX=0 NormalY=0 NormalZ=1 AngleXU=0 Radius=1.5 StartAngle=4.71239 EndAngle=7.85398
    g21: ArcOfCircle CenterX=-1.5 CenterY=4.25 CenterZ=0 NormalX=0 NormalY=0 NormalZ=1 AngleXU=0 Radius=1.5 StartAngle=4.71239 EndAngle=7.85398
    g22: ArcOfCircle CenterX=-1.5 CenterY=10 CenterZ=0 NormalX=0 NormalY=0 NormalZ=1 AngleXU=0 Radius=1.5 StartAngle=4.71239 EndAngle=7.85398
    g23: ArcOfCircle CenterX=-1.5 CenterY=15.75 CenterZ=0 NormalX=0 NormalY=0 NormalZ=1 AngleXU=0 Radius=1.5 StartAngle=4.71239 EndAngle=7.85398
    g24: LineSegment StartX=-49.19 StartY=69.25 StartZ=0 EndX=-1.5 EndY=69.25 EndZ=0
    g25: LineSegment StartX=-49.19 StartY=66.25 StartZ=0 EndX=-1.5 EndY=66.25 EndZ=0
    g26: LineSegment StartX=-49.19 StartY=63.5 StartZ=0 EndX=-1.5 EndY=63.5 EndZ=0
    g27: LineSegment StartX=-49.19 StartY=60.5 StartZ=0 EndX=-1.5 EndY=60.5 EndZ=0
    g28: LineSegment StartX=-49.19 StartY=57.75 StartZ=0 EndX=-1.5 EndY=57.75 EndZ=0
    g29: LineSegment StartX=-49.19 StartY=54.75 StartZ=0 EndX=-1.5 EndY=54.75 EndZ=0
    g30: LineSegment StartX=-49.19 StartY=52 StartZ=0 EndX=-11.49 EndY=52 EndZ=0
    g31: LineSegment StartX=-49.19 StartY=49 StartZ=0 EndX=-11.49 EndY=49 EndZ=0
    g32: LineSegment StartX=-49.19 StartY=46.25 StartZ=0 EndX=-16.28 EndY=46.25 EndZ=0
    g33: LineSegment StartX=-49.19 StartY=43.25 StartZ=0 EndX=-16.28 EndY=43.25 EndZ=0
    g34: LineSegment StartX=-49.19 StartY=40.5 StartZ=0 EndX=-18.2337 EndY=40.5 EndZ=0
    g35: LineSegment StartX=-49.19 StartY=37.5 StartZ=0 EndX=-18.23 EndY=37.5 EndZ=0
    g36: LineSegment StartX=-49.19 StartY=34.5 StartZ=0 EndX=-18.2337 EndY=34.5 EndZ=0
    g37: LineSegment StartX=-49.19 StartY=31.5 StartZ=0 EndX=-18.23 EndY=31.5 EndZ=0
    g38: LineSegment StartX=-49.19 StartY=28.75 StartZ=0 EndX=-16.2837 EndY=28.75 EndZ=0
    g39: LineSegment StartX=-49.19 StartY=25.75 StartZ=0 EndX=-16.28 EndY=25.75 EndZ=0
    g40: LineSegment StartX=-49.19 StartY=23 StartZ=0 EndX=-11.49 EndY=23 EndZ=0
    g41: LineSegment StartX=-49.19 StartY=20 StartZ=0 EndX=-11.49 EndY=20 EndZ=0
    g42: LineSegment StartX=-49.19 StartY=17.25 StartZ=0 EndX=-1.5 EndY=17.25 EndZ=0
    g43: LineSegment StartX=-49.19 StartY=14.25 StartZ=0 EndX=-1.5 EndY=14.25 EndZ=0
    g44: LineSegment StartX=-49.19 StartY=11.5 StartZ=0 EndX=-1.5 EndY=11.5 EndZ=0
    g45: LineSegment StartX=-49.19 StartY=8.5 StartZ=0 EndX=-1.5 EndY=8.5 EndZ=0
    g46: LineSegment StartX=-49.19 StartY=5.75 StartZ=0 EndX=-1.5 EndY=5.75 EndZ=0
    g47: LineSegment StartX=-49.19 StartY=2.75 StartZ=0 EndX=-1.5 EndY=2.75 EndZ=0
  constraints (120):
    c: Vertical(g0)
    c: Distance(g0) = 3
    c: Block(g0)
    c: Vertical(g1)
    c: Distance(g1) = 3
    c: Vertical(g2)
    c: Equal(g0,g2) = 3
    c: Block(g2)
    c: Vertical(g3)
    c: Equal(g1,g3) = 3
    c: Vertical(g4)
    c: Equal(g0,g4) = 3
    c: Block(g4)
    c: Vertical(g5)
    c: Equal(g1,g5) = 3
    c: Vertical(g6)
    c: Equal(g0,g6) = 3
    c: Block(g6)
    c: Vertical(g7)
    c: Equal(g1,g7) = 3
    c: Vertical(g8)
    c: Equal(g0,g8) = 3
    c: Block(g8)
    c: Vertical(g9)
    c: Equal(g1,g9) = 3
    c: Vertical(g10)
    c: Equal(g0,g10) = 3
    c: Block(g10)
    c: Vertical(g11)
    c: Equal(g1,g11) = 3
    c: Block(g12)
    c: Block(g13)
    c: Block(g14)
    c: Block(g15)
    c: Block(g16)
    c: Block(g17)
    c: Block(g18)
    c: Block(g19)
    c: Block(g20)
    c: Block(g21)
    c: Block(g22)
    c: Block(g23)
    c: Block(g11)
    c: Block(g9)
    c: Block(g7)
    c: Block(g5)
    c: Block(g3)
    c: Block(g1)
    c: Coincident(g24,g0)
    c: Coincident(g24,g12)
    c: Horizontal(g24)
    c: Coincident(g25,g0)
    c: Coincident(g25,g12)
    c: Horizontal(g25)
    c: Coincident(g26,g1)
    c: Coincident(g26,g13)
    c: Horizontal(g26)
    c: Coincident(g27,g1)
    c: Coincident(g27,g13)
    c: Horizontal(g27)
    c: Coincident(g28,g2)
    c: Coincident(g28,g14)
    c: Horizontal(g28)
    c: Coincident(g29,g2)
    c: Coincident(g29,g14)
    c: Horizontal(g29)
    c: Coincident(g30,g3)
    c: Coincident(g30,g15)
    c: Horizontal(g30)
    c: Coincident(g31,g3)
    c: Coincident(g31,g15)
    c: Horizontal(g31)
    c: Coincident(g32,g4)
    c: Coincident(g32,g16)
    c: Horizontal(g32)
    c: Coincident(g33,g4)
    c: Coincident(g33,g16)
    c: Horizontal(g33)
    c: Coincident(g34,g5)
    c: Coincident(g34,g17)
    c: Horizontal(g34)
    c: Coincident(g35,g5)
    c: Coincident(g35,g17)
    c: Horizontal(g35)
    c: Coincident(g36,g6)
    c: Coincident(g36,g19)
    c: Horizontal(g36)
    c: Coincident(g37,g6)
    c: Coincident(g37,g19)
    c: Horizontal(g37)
    c: Coincident(g38,g7)
    c: Coincident(g38,g18)
    c: Horizontal(g38)
    c: Coincident(g39,g7)
    c: Coincident(g39,g18)
    c: Horizontal(g39)
    c: Coincident(g40,g8)
    c: Coincident(g40,g20)
    c: Horizontal(g40)
    c: Coincident(g41,g8)
    c: Coincident(g41,g20)
    c: Horizontal(g41)
    c: Coincident(g42,g9)
    c: Coincident(g42,g23)
    c: Horizontal(g42)
    c: Coincident(g43,g9)
    c: Coincident(g43,g23)
    c: Horizontal(g43)
    c: Coincident(g44,g10)
    c: Coincident(g44,g22)
    c: Horizontal(g44)
    c: Coincident(g45,g10)
    c: Coincident(g45,g22)
    c: Horizontal(g45)
    c: Coincident(g46,g11)
    c: Coincident(g46,g21)
    c: Horizontal(g46)
    c: Coincident(g47,g11)
    c: Coincident(g47,g21)
    c: Horizontal(g47)
FEATURE [Part::Extrusion] Extrude023
  Base = -> Sketch032
  Dir = (1,-2e-16,2e-16)
  DirMode = 2
  FaceMakerClass = Part::FaceMakerBullseye
  LengthFwd = 19
  LengthRev = 0
  Placement = pos=(-19,0,0) rot=(0,0,1;0rad)
  Solid = true
  Symmetric = false
FEATURE [Part::Fillet] Fillet023
  Base = -> Extrude023
  Edges = <same value as first occurrence — deduplicated (x6 in doc)>
  Placement = pos=(0,0.05,0) rot=(0,0,1;0rad)
FEATURE [Part::Cut] Cut014  label="bottom003"
  Base = -> Cut007
  Tool = -> Fusion047
FEATURE [Part::Cut] Cut021  label="bottom004"
  Base = -> Cut014
  Tool = -> Fillet023
FEATURE [Sketcher::SketchObject] Sketch033
  FullyConstrained = true
  Placement = pos=(117,19,0) rot=(0.57735,0.57735,0.57735;2.0944rad)
  sketch-geometry (8):
    g0: LineSegment StartX=-49.19 StartY=69.25 StartZ=0 EndX=-49.19 EndY=66.25 EndZ=0
    g1: LineSegment StartX=-49.19 StartY=5.75 StartZ=0 EndX=-49.19 EndY=2.75 EndZ=0
    g2: ArcOfCircle CenterX=-1.5 CenterY=67.75 CenterZ=0 NormalX=0 NormalY=0 NormalZ=1 AngleXU=0 Radius=1.5 StartAngle=4.71239 EndAngle=7.85398
    g3: ArcOfCircle CenterX=-1.5 CenterY=4.25 CenterZ=0 NormalX=0 NormalY=0 NormalZ=1 AngleXU=0 Radius=1.5 StartAngle=4.71239 EndAngle=7.85398
    g4: LineSegment StartX=-49.19 StartY=69.25 StartZ=0 EndX=-1.5 EndY=69.25 EndZ=0
    g5: LineSegment StartX=-49.19 StartY=66.25 StartZ=0 EndX=-1.5 EndY=66.25 EndZ=0
    g6: LineSegment StartX=-49.19 StartY=5.75 StartZ=0 EndX=-1.5 EndY=5.75 EndZ=0
    g7: LineSegment StartX=-49.19 StartY=2.75 StartZ=0 EndX=-1.5 EndY=2.75 EndZ=0
  constraints (19):
    c: Vertical(g0)
    c: Distance(g0) = 3
    c: Block(g0)
    c: Vertical(g1)
    c: Block(g2)
    c: Block(g3)
    c: Block(g1)
    c: Coincident(g4,g0)
    c: Coincident(g4,g2)
    c: Horizontal(g4)
    c: Coincident(g5,g0)
    c: Coincident(g5,g2)
    c: Horizontal(g5)
    c: Coincident(g6,g1)
    c: Coincident(g6,g3)
    c: Horizontal(g6)
    c: Coincident(g7,g1)
    c: Coincident(g7,g3)
    c: Horizontal(g7)
FEATURE [Sketcher::SketchObject] Sketch034
  FullyConstrained = true
  Placement = pos=(117,19,0) rot=(0.57735,0.57735,0.57735;2.0944rad)
  sketch-geometry (8):
    g0: LineSegment StartX=-49.19 StartY=63.5 StartZ=0 EndX=-49.19 EndY=60.5 EndZ=0
    g1: LineSegment StartX=-49.19 StartY=11.5 StartZ=0 EndX=-49.19 EndY=8.5 EndZ=0
    g2: ArcOfCircle CenterX=-1.5 CenterY=62 CenterZ=0 NormalX=0 NormalY=0 NormalZ=1 AngleXU=0 Radius=1.5 StartAngle=4.71239 EndAngle=7.85398
    g3: ArcOfCircle CenterX=-1.5 CenterY=10 CenterZ=0 NormalX=0 NormalY=0 NormalZ=1 AngleXU=0 Radius=1.5 StartAngle=4.71239 EndAngle=7.85398
    g4: LineSegment StartX=-49.19 StartY=63.5 StartZ=0 EndX=-1.5 EndY=63.5 EndZ=0
    g5: LineSegment StartX=-49.19 StartY=60.5 StartZ=0 EndX=-1.5 EndY=60.5 EndZ=0
    g6: LineSegment StartX=-49.19 StartY=11.5 StartZ=0 EndX=-1.5 EndY=11.5 EndZ=0
    g7: LineSegment StartX=-49.19 StartY=8.5 StartZ=0 EndX=-1.5 EndY=8.5 EndZ=0
  constraints (19):
    c: Vertical(g0)
    c: Distance(g0) = 3
    c: Vertical(g1)
    c: Block(g1)
    c: Block(g2)
    c: Block(g3)
    c: Block(g0)
    c: Coincident(g4,g0)
    c: Coincident(g4,g2)
    c: Horizontal(g4)
    c: Coincident(g5,g0)
    c: Coincident(g5,g2)
    c: Horizontal(g5)
    c: Coincident(g6,g1)
    c: Coincident(g6,g3)
    c: Horizontal(g6)
    c: Coincident(g7,g1)
    c: Coincident(g7,g3)
    c: Horizontal(g7)
FEATURE [Part::Extrusion] Extrude024
  Base = -> Sketch033
  Dir = (1,0,0)
  DirMode = 2
  FaceMakerClass = Part::FaceMakerBullseye
  LengthFwd = 10
  LengthRev = 0
  Solid = true
  Symmetric = false
FEATURE [Part::Extrusion] Extrude025
  Base = -> Sketch034
  Dir = (1,0,0)
  DirMode = 2
  FaceMakerClass = Part::FaceMakerBullseye
  LengthFwd = 10
  LengthRev = 0
  Solid = true
  Symmetric = false
FEATURE [Part::Fillet] Fillet024  label="removeFromtMoreFrontCaseScrewRetainers"
  Base = -> Extrude024
  Edges = 4 edges r=1.49: [Edge6,Edge11,Edge18,Edge23]
  Placement = pos=(-11,0,0) rot=(0,0,1;0rad)
FEATURE [Part::Fillet] Fillet025  label="removeFromtMoreFrontCaseScrewRetainers001"
  Base = -> Extrude025
  Edges = 4 edges r=1.49: [Edge6,Edge11,Edge18,Edge23]
  Placement = pos=(-19,0,0) rot=(0,0,1;0rad)
FEATURE [Part::Cut] Cut022
  Base = -> Cut015
  Tool = -> Fillet025
FEATURE [Part::Cut] Cut023  label="screwRetainers"
  Base = -> Cut022
  Tool = -> Fillet024
FEATURE [Part::MultiFuse] Fusion056  label="bottom005"
  Shapes = -> [Fusion044,Cut021]
FEATURE [Part::MultiFuse] Fusion057  label="casePillars001"
  Shapes = -> [Cut016,Fusion052]
FEATURE [Part::MultiFuse] Fusion058  label="bottom006"
  Shapes = -> [Fusion056,Cut023]
FEATURE [Part::MultiFuse] Fusion059  label="bottom007"
  Shapes = -> [Fusion058,Fillet005]
FEATURE [Part::MultiFuse] Fusion060  label="bottom008"
  Shapes = -> [Fusion059,Fusion]
FEATURE [Part::MultiFuse] Fusion061  label="top011"
  Shapes = -> [Cut006,Cut020]
FEATURE [Part::MultiFuse] Fusion062  label="top012"
  Shapes = -> [Fusion057,Fusion061]
FEATURE [Sketcher::SketchObject] Sketch035  label="topSketch007"
  FullyConstrained = true
  sketch-geometry (6):
    g0: LineSegment StartX=19 StartY=38 StartZ=0 EndX=117 EndY=38 EndZ=0
    g1: ArcOfCircle CenterX=19 CenterY=19 CenterZ=0 NormalX=0 NormalY=0 NormalZ=1 AngleXU=0 Radius=19 StartAngle=1.5708 EndAngle=3.14159
    g2: LineSegment StartX=117 StartY=38 StartZ=0 EndX=117 EndY=19 EndZ=0
    g3: LineSegment StartX=98 StartY=1.0161e-12 StartZ=0 EndX=5.22862e-06 EndY=1.0161e-12 EndZ=0
    g4: LineSegment StartX=5.22862e-06 StartY=19 StartZ=0 EndX=5.22862e-06 EndY=1.0161e-12 EndZ=0
    g5: ArcOfCircle CenterX=98 CenterY=19 CenterZ=0 NormalX=0 NormalY=0 NormalZ=1 AngleXU=0 Radius=19 StartAngle=4.71239 EndAngle=6.28319
  constraints (16):
    c: Horizontal(g0)
    c: Distance(g0) = 98
    c: Coincident(g1,g0)
    c: Block(g1)
    c: Coincident(g2,g0)
    c: Vertical(g2)
    c: Distance(g2) = 19
    c: Horizontal(g3)
    c: Coincident(g4,g1)
    c: Vertical(g4)
    c: Coincident(g3,g4)
    c: Block(g3)
    c: Coincident(g5,g2)
    c: Coincident(g5,g3)
    c: Block(g0)
    c: Block(g5)
FEATURE [Part::Extrusion] Extrude026  label="sideA001"
  Base = -> Sketch035
  Dir = (0,0,1)
  DirMode = 2
  FaceMakerClass = Part::FaceMakerBullseye
  LengthFwd = 3
  LengthRev = 0
  Placement = pos=(0,0,-2.7) rot=(0,0,1;0rad)
  Solid = true
  Symmetric = false
FEATURE [Sketcher::SketchObject] Sketch036  label="topSketch008"
  FullyConstrained = true
  sketch-geometry (6):
    g0: LineSegment StartX=19 StartY=38 StartZ=0 EndX=117 EndY=38 EndZ=0
    g1: ArcOfCircle CenterX=19 CenterY=19 CenterZ=0 NormalX=0 NormalY=0 NormalZ=1 AngleXU=0 Radius=19 StartAngle=1.5708 EndAngle=3.14159
    g2: LineSegment StartX=117 StartY=38 StartZ=0 EndX=117 EndY=19 EndZ=0
    g3: LineSegment StartX=98 StartY=1.0161e-12 StartZ=0 EndX=5.22862e-06 EndY=1.0161e-12 EndZ=0
    g4: LineSegment StartX=5.22862e-06 StartY=19 StartZ=0 EndX=5.22862e-06 EndY=1.0161e-12 EndZ=0
    g5: ArcOfCircle CenterX=98 CenterY=19 CenterZ=0 NormalX=0 NormalY=0 NormalZ=1 AngleXU=0 Radius=19 StartAngle=4.71239 EndAngle=6.28319
  constraints (16):
    c: Horizontal(g0)
    c: Distance(g0) = 98
    c: Coincident(g1,g0)
    c: Block(g1)
    c: Coincident(g2,g0)
    c: Vertical(g2)
    c: Distance(g2) = 19
    c: Horizontal(g3)
    c: Coincident(g4,g1)
    c: Vertical(g4)
    c: Coincident(g3,g4)
    c: Block(g3)
    c: Coincident(g5,g2)
    c: Coincident(g5,g3)
    c: Block(g0)
    c: Block(g5)
FEATURE [Part::Extrusion] Extrude027  label="sideB001"
  Base = -> Sketch036
  Dir = (0,0,1)
  DirMode = 2
  FaceMakerClass = Part::FaceMakerBullseye
  LengthFwd = 3
  LengthRev = 0
  Placement = pos=(0,0,71.7) rot=(0,0,1;0rad)
  Solid = true
  Symmetric = false
FEATURE [Part::MultiFuse] Fusion064  label="removeFromBottom"
  Shapes = -> [Extrude026,Extrude027]
FEATURE [Part::Cut] Cut024  label="bottom009"
  Base = -> Fusion060
  Tool = -> Fusion064
FEATURE [Sketcher::SketchObject] Sketch037  label="topSketch009"
  FullyConstrained = true
  sketch-geometry (8):
    g0: ArcOfCircle CenterX=19 CenterY=19.1201 CenterZ=0 NormalX=0 NormalY=0 NormalZ=1 AngleXU=0 Radius=18.8799 StartAngle=1.5708 EndAngle=3.14793
    g1: LineSegment StartX=0.120501 StartY=19.0004 StartZ=0 EndX=0.120501 EndY=0.000382114 EndZ=0
    g2: LineSegment StartX=19 StartY=38 StartZ=0 EndX=124 EndY=38 EndZ=0
    g3: LineSegment StartX=0.120501 StartY=0.000382114 StartZ=0 EndX=105.121 EndY=0.000382114 EndZ=0
    g4: LineSegment StartX=124 StartY=38 StartZ=0 EndX=125.616 EndY=38 EndZ=0
    g5: LineSegment StartX=105.121 StartY=0.000382114 StartZ=0 EndX=106.736 EndY=0.000382114 EndZ=0
    g6: ArcOfCircle CenterX=106.616 CenterY=19 CenterZ=0 NormalX=0 NormalY=0 NormalZ=1 AngleXU=0 Radius=19 StartAngle=4.71873 EndAngle=6.28319
    g7: LineSegment StartX=125.616 StartY=38 StartZ=0 EndX=125.616 EndY=19 EndZ=0
  constraints (21):
    c: Block(g0)
    c: Coincident(g1,g0)
    c: Vertical(g1)
    c: Horizontal(g2)
    c: Distance(g2) = 105
    c: Coincident(g2,g0)
    c: Distance(g1) = 19
    c: Coincident(g3,g1)
    c: Horizontal(g3)
    c: Distance(g3) = 105
    c: Coincident(g4,g2)
    c: Horizontal(g4)
    c: Distance(g4) = 1.61553
    c: Horizontal(g5)
    c: Equal(g4,g5) = 1.61553
    c: Coincident(g5,g3)
    c: Block(g6)
    c: Coincident(g6,g5)
    c: Coincident(g7,g4)
    c: Coincident(g7,g6)
    c: Vertical(g7)
FEATURE [Part::Extrusion] Extrude028  label="sideB"
  Base = -> Sketch037
  Dir = (0,0,1)
  DirMode = 2
  FaceMakerClass = Part::FaceMakerBullseye
  LengthFwd = 3
  LengthRev = 0
  Placement = pos=(0,0,72) rot=(0,0,1;0rad)
  Solid = true
  Symmetric = false
FEATURE [Sketcher::SketchObject] Sketch038  label="topSketch010"
  FullyConstrained = true
  sketch-geometry (22):
    g0: LineSegment StartX=5.21097e-06 StartY=3 StartZ=0 EndX=5.21097e-06 EndY=19 EndZ=0
    g1: ArcOfCircle CenterX=19 CenterY=19 CenterZ=0 NormalX=0 NormalY=0 NormalZ=1 AngleXU=0 Radius=19 StartAngle=1.5708 EndAngle=3.14159
    g2: ArcOfCircle CenterX=19 CenterY=19 CenterZ=0 NormalX=0 NormalY=0 NormalZ=1 AngleXU=0 Radius=16 StartAngle=1.5708 EndAngle=3.14159
    g3: LineSegment StartX=114 StartY=35 StartZ=0 EndX=19 EndY=35 EndZ=0
    g4: LineSegment StartX=5.21097e-06 StartY=3 StartZ=0 EndX=5.21097e-06 EndY=0 EndZ=0
    g5: LineSegment StartX=3 StartY=0 StartZ=0 EndX=5.21097e-06 EndY=0 EndZ=0
    g6: LineSegment StartX=3 StartY=19 StartZ=0 EndX=3 EndY=0 EndZ=0
    g7: LineSegment StartX=19 StartY=38 StartZ=0 EndX=124 EndY=38 EndZ=0
    g8: Circle CenterX=119 CenterY=35 CenterZ=0 NormalX=0 NormalY=0 NormalZ=1 AngleXU=0 Radius=1
    g9: Circle CenterX=121 CenterY=35 CenterZ=0 NormalX=0 NormalY=0 NormalZ=1 AngleXU=0 Radius=1
    g10: Circle CenterX=121 CenterY=33 CenterZ=0 NormalX=0 NormalY=0 NormalZ=1 AngleXU=0 Radius=1
    g11: BSplineCurve PolesCount=3 KnotsCount=2 Degree=2 IsPeriodic=0
    g12: GeomPoint X=119 Y=35 Z=0
    g13: GeomPoint X=121 Y=33 Z=0
    g14: LineSegment StartX=119 StartY=35 StartZ=0 EndX=114 EndY=35 EndZ=0
    g15: ArcOfCircle CenterX=105 CenterY=19 CenterZ=0 NormalX=0 NormalY=0 NormalZ=1 AngleXU=0 Radius=16 StartAngle=5.60905 EndAngle=6.28319
    g16: LineSegment StartX=121 StartY=33 StartZ=0 EndX=121 EndY=19 EndZ=0
    g17: LineSegment StartX=117.5 StartY=9.01251 StartZ=0 EndX=121.163 EndY=9.0125 EndZ=0
    g18: ArcOfCircle CenterX=105 CenterY=19 CenterZ=0 NormalX=0 NormalY=0 NormalZ=1 AngleXU=0 Radius=20.6155 StartAngle=5.7297 EndAngle=6.28319
    g19: LineSegment StartX=121.163 StartY=9.0125 StartZ=0 EndX=122.538 EndY=8.16329 EndZ=0
    g20: LineSegment StartX=124 StartY=38 StartZ=0 EndX=125.616 EndY=38 EndZ=0
    g21: LineSegment StartX=125.616 StartY=19 StartZ=0 EndX=125.616 EndY=38 EndZ=0
  constraints (49):
    c: Vertical(g0)
    c: Block(g0)
    c: Coincident(g1,g0)
    c: Block(g1)
    c: Coincident(g2,g1)
    c: Block(g2)
    c: Coincident(g3,g2)
    c: Horizontal(g3)
    c: Tangent(g3,g2)
    c: Coincident(g4,g0)
    c: Distance(g4) = 3
    c: Vertical(g4)
    c: Coincident(g5,g4)
    c: Horizontal(g5)
    c: Coincident(g6,g2)
    c: Coincident(g6,g5)
    c: Vertical(g6)
    c: Horizontal(g7)
    c: Distance(g7) = 105
    c: Coincident(g7,g1)
    c: Block(g3)
    c: Weight(g8) = 1
    c: Equal(g8,g9)
    c: Equal(g8,g10)
    c: InternalAlignment(g8,g11)
    c: InternalAlignment(g9,g11)
    c: InternalAlignment(g10,g11)
    c: InternalAlignment(g12,g11)
    c: InternalAlignment(g13,g11)
    c: Block(g11)
    c: Coincident(g14,g11)
    c: Coincident(g14,g3)
    c: Horizontal(g14)
    c: Block(g15)
    c: Coincident(g16,g11)
    c: Coincident(g16,g15)
    c: Vertical(g16)
    c: Distance(g16) = 14
    c: Coincident(g17,g15)
    c: Block(g18)
    c: Coincident(g19,g18)
    c: Coincident(g20,g7)
    c: Horizontal(g20)
    c: Vertical(g21)
    c: Coincident(g20,g21)
    c: Block(g20)
    c: Block(g21)
    c: Block(g19)
    c: Block(g17)
FEATURE [Part::Extrusion] Extrude029
  Base = -> Sketch038
  Dir = (0,0,1)
  DirMode = 2
  FaceMakerClass = Part::FaceMakerBullseye
  LengthFwd = 72
  LengthRev = 0
  Solid = true
  Symmetric = false
FEATURE [Part::Feature] Face085
  shape: bbox 4.8 x 25.5 x 2e-07 mm, 1 faces, 0 solids (baked)
FEATURE [Part::Revolution] Revolve089  label="moreFrontCaseScrewPost003"
  Angle = 360
  Axis = (0,1,0)
  Base = (0,0,0)
  FaceMakerClass = Part::FaceMakerBullseye
  Placement = pos=(109.5,4.5,3.5) rot=(0,0,1;0rad)
  Solid = false
  Source = -> Face085
  Symmetric = false
FEATURE [Part::Feature] Face086
  shape: bbox 4.8 x 25.5 x 2e-07 mm, 1 faces, 0 solids (baked)
FEATURE [Part::Revolution] Revolve090  label="moreFrontCaseScrewPost004"
  Angle = 360
  Axis = (0,1,0)
  Base = (0,0,0)
  FaceMakerClass = Part::FaceMakerBullseye
  Placement = pos=(109.5,4.5,68.5) rot=(0,0,1;0rad)
  Solid = false
  Source = -> Face086
  Symmetric = false
FEATURE [Part::Fillet] Fillet026  label="top013"
  Base = -> Extrude029
  Edges = 1 edges r=2: [Edge35]
FEATURE [Sketcher::SketchObject] Sketch039
  FullyConstrained = true
  sketch-geometry (7):
    g0: LineSegment StartX=0 StartY=0 StartZ=0 EndX=0 EndY=6 EndZ=0
    g1: Circle CenterX=0 CenterY=0 CenterZ=0 NormalX=0 NormalY=0 NormalZ=1 AngleXU=0 Radius=1
    g2: Circle CenterX=8 CenterY=6 CenterZ=0 NormalX=0 NormalY=0 NormalZ=1 AngleXU=0 Radius=1
    g3: BSplineCurve PolesCount=3 KnotsCount=2 Degree=2 IsPeriodic=0
    g4: GeomPoint X=0 Y=0 Z=0
    g5: GeomPoint X=8 Y=6 Z=0
    g6: LineSegment StartX=0 StartY=6 StartZ=0 EndX=8 EndY=6 EndZ=0
  constraints (14):
    c: Coincident(g0,g-1)
    c: Distance(g0) = 6
    c: Vertical(g0)
    c: Coincident(g3,g0)
    c: Weight(g1) = 1
    c: Equal(g1,g2)
    c: InternalAlignment(g1,g3)
    c: InternalAlignment(g2,g3)
    c: InternalAlignment(g4,g3)
    c: InternalAlignment(g5,g3)
    c: Block(g3)
    c: Coincident(g6,g0)
    c: Coincident(g6,g3)
    c: Horizontal(g6)
FEATURE [Sketcher::SketchObject] Sketch040
  FullyConstrained = true
  sketch-geometry (7):
    g0: LineSegment StartX=0 StartY=0 StartZ=0 EndX=0 EndY=6 EndZ=0
    g1: Circle CenterX=0 CenterY=0 CenterZ=0 NormalX=0 NormalY=0 NormalZ=1 AngleXU=0 Radius=1
    g2: Circle CenterX=8 CenterY=6 CenterZ=0 NormalX=0 NormalY=0 NormalZ=1 AngleXU=0 Radius=1
    g3: BSplineCurve PolesCount=3 KnotsCount=2 Degree=2 IsPeriodic=0
    g4: GeomPoint X=0 Y=0 Z=0
    g5: GeomPoint X=8 Y=6 Z=0
    g6: LineSegment StartX=0 StartY=6 StartZ=0 EndX=8 EndY=6 EndZ=0
  constraints (14):
    c: Coincident(g0,g-1)
    c: Distance(g0) = 6
    c: Vertical(g0)
    c: Coincident(g3,g0)
    c: Weight(g1) = 1
    c: Equal(g1,g2)
    c: InternalAlignment(g1,g3)
    c: InternalAlignment(g2,g3)
    c: InternalAlignment(g4,g3)
    c: InternalAlignment(g5,g3)
    c: Block(g3)
    c: Coincident(g6,g0)
    c: Coincident(g6,g3)
    c: Horizontal(g6)
FEATURE [Sketcher::SketchObject] Sketch041
  FullyConstrained = true
  sketch-geometry (7):
    g0: LineSegment StartX=0 StartY=0 StartZ=0 EndX=0 EndY=6 EndZ=0
    g1: Circle CenterX=0 CenterY=0 CenterZ=0 NormalX=0 NormalY=0 NormalZ=1 AngleXU=0 Radius=1
    g2: Circle CenterX=8 CenterY=6 CenterZ=0 NormalX=0 NormalY=0 NormalZ=1 AngleXU=0 Radius=1
    g3: BSplineCurve PolesCount=3 KnotsCount=2 Degree=2 IsPeriodic=0
    g4: GeomPoint X=0 Y=0 Z=0
    g5: GeomPoint X=8 Y=6 Z=0
    g6: LineSegment StartX=0 StartY=6 StartZ=0 EndX=8 EndY=6 EndZ=0
  constraints (14):
    c: Coincident(g0,g-1)
    c: Distance(g0) = 6
    c: Vertical(g0)
    c: Coincident(g3,g0)
    c: Weight(g1) = 1
    c: Equal(g1,g2)
    c: InternalAlignment(g1,g3)
    c: InternalAlignment(g2,g3)
    c: InternalAlignment(g4,g3)
    c: InternalAlignment(g5,g3)
    c: Block(g3)
    c: Coincident(g6,g0)
    c: Coincident(g6,g3)
    c: Horizontal(g6)
FEATURE [Sketcher::SketchObject] Sketch042
  FullyConstrained = true
  sketch-geometry (7):
    g0: LineSegment StartX=0 StartY=0 StartZ=0 EndX=0 EndY=6 EndZ=0
    g1: Circle CenterX=0 CenterY=0 CenterZ=0 NormalX=0 NormalY=0 NormalZ=1 AngleXU=0 Radius=1
    g2: Circle CenterX=8 CenterY=6 CenterZ=0 NormalX=0 NormalY=0 NormalZ=1 AngleXU=0 Radius=1
    g3: BSplineCurve PolesCount=3 KnotsCount=2 Degree=2 IsPeriodic=0
    g4: GeomPoint X=0 Y=0 Z=0
    g5: GeomPoint X=8 Y=6 Z=0
    g6: LineSegment StartX=0 StartY=6 StartZ=0 EndX=8 EndY=6 EndZ=0
  constraints (14):
    c: Coincident(g0,g-1)
    c: Distance(g0) = 6
    c: Vertical(g0)
    c: Coincident(g3,g0)
    c: Weight(g1) = 1
    c: Equal(g1,g2)
    c: InternalAlignment(g1,g3)
    c: InternalAlignment(g2,g3)
    c: InternalAlignment(g4,g3)
    c: InternalAlignment(g5,g3)
    c: Block(g3)
    c: Coincident(g6,g0)
    c: Coincident(g6,g3)
    c: Horizontal(g6)
FEATURE [Part::Extrusion] Extrude030  label="caseScrewPillarBracket008"
  Base = -> Sketch039
  Dir = (0,0,1)
  DirMode = 2
  FaceMakerClass = Part::FaceMakerBullseye
  LengthFwd = 2.4
  LengthRev = 0
  Placement = pos=(15.76,29,8.8) rot=(0,1,0;0rad)
  Solid = true
  Symmetric = false
FEATURE [Part::Extrusion] Extrude031  label="caseScrewPillarBracket009"
  Base = -> Sketch040
  Dir = (0,0,1)
  DirMode = 2
  FaceMakerClass = Part::FaceMakerBullseye
  LengthFwd = 2.4
  LengthRev = 0
  Placement = pos=(15.76,29,60.8) rot=(0,0,1;0rad)
  Solid = true
  Symmetric = false
FEATURE [Part::Extrusion] Extrude032  label="caseScrewPillarBracket010"
  Base = -> Sketch041
  Dir = (0,0,1)
  DirMode = 2
  FaceMakerClass = Part::FaceMakerBullseye
  LengthFwd = 2.4
  LengthRev = 0
  Placement = pos=(13.7,29,13.26) rot=(0,-1,0;1.5708rad)
  Solid = true
  Symmetric = false
FEATURE [Part::Extrusion] Extrude033  label="caseScrewPillarBracket011"
  Base = -> Sketch042
  Dir = (0,0,1)
  DirMode = 2
  FaceMakerClass = Part::FaceMakerBullseye
  LengthFwd = 2.4
  LengthRev = 0
  Placement = pos=(11.3,29,58.74) rot=(0,1,0;1.5708rad)
  Solid = true
  Symmetric = false
FEATURE [Sketcher::SketchObject] Sketch043
  FullyConstrained = true
  sketch-geometry (7):
    g0: LineSegment StartX=0 StartY=0 StartZ=0 EndX=0 EndY=6 EndZ=0
    g1: Circle CenterX=0 CenterY=0 CenterZ=0 NormalX=0 NormalY=0 NormalZ=1 AngleXU=0 Radius=1
    g2: Circle CenterX=8 CenterY=6 CenterZ=0 NormalX=0 NormalY=0 NormalZ=1 AngleXU=0 Radius=1
    g3: BSplineCurve PolesCount=3 KnotsCount=2 Degree=2 IsPeriodic=0
    g4: GeomPoint X=0 Y=0 Z=0
    g5: GeomPoint X=8 Y=6 Z=0
    g6: LineSegment StartX=0 StartY=6 StartZ=0 EndX=8 EndY=6 EndZ=0
  constraints (14):
    c: Coincident(g0,g-1)
    c: Distance(g0) = 6
    c: Vertical(g0)
    c: Coincident(g3,g0)
    c: Weight(g1) = 1
    c: Equal(g1,g2)
    c: InternalAlignment(g1,g3)
    c: InternalAlignment(g2,g3)
    c: InternalAlignment(g4,g3)
    c: InternalAlignment(g5,g3)
    c: Block(g3)
    c: Coincident(g6,g0)
    c: Coincident(g6,g3)
    c: Horizontal(g6)
FEATURE [Part::Extrusion] Extrude034  label="caseScrewPillarBracket012"
  Base = -> Sketch043
  Dir = (0,0,1)
  DirMode = 2
  FaceMakerClass = Part::FaceMakerBullseye
  LengthFwd = 2.4
  LengthRev = 0
  Placement = pos=(88.3,29,65.23) rot=(0,1,0;1.5708rad)
  Solid = true
  Symmetric = false
FEATURE [Sketcher::SketchObject] Sketch044
  FullyConstrained = true
  sketch-geometry (7):
    g0: LineSegment StartX=0 StartY=0 StartZ=0 EndX=0 EndY=6 EndZ=0
    g1: Circle CenterX=0 CenterY=0 CenterZ=0 NormalX=0 NormalY=0 NormalZ=1 AngleXU=0 Radius=1
    g2: Circle CenterX=8 CenterY=6 CenterZ=0 NormalX=0 NormalY=0 NormalZ=1 AngleXU=0 Radius=1
    g3: BSplineCurve PolesCount=3 KnotsCount=2 Degree=2 IsPeriodic=0
    g4: GeomPoint X=0 Y=0 Z=0
    g5: GeomPoint X=8 Y=6 Z=0
    g6: LineSegment StartX=0 StartY=6 StartZ=0 EndX=8 EndY=6 EndZ=0
  constraints (14):
    c: Coincident(g0,g-1)
    c: Distance(g0) = 6
    c: Vertical(g0)
    c: Coincident(g3,g0)
    c: Weight(g1) = 1
    c: Equal(g1,g2)
    c: InternalAlignment(g1,g3)
    c: InternalAlignment(g2,g3)
    c: InternalAlignment(g4,g3)
    c: InternalAlignment(g5,g3)
    c: Block(g3)
    c: Coincident(g6,g0)
    c: Coincident(g6,g3)
    c: Horizontal(g6)
FEATURE [Part::Extrusion] Extrude035  label="caseScrewPillarBracket013"
  Base = -> Sketch044
  Dir = (0,0,1)
  DirMode = 2
  FaceMakerClass = Part::FaceMakerBullseye
  LengthFwd = 2.4
  LengthRev = 0
  Placement = pos=(90.7,29,6.77) rot=(0,-1,0;1.5708rad)
  Solid = true
  Symmetric = false
FEATURE [Sketcher::SketchObject] Sketch045
  FullyConstrained = true
  sketch-geometry (7):
    g0: LineSegment StartX=0 StartY=0 StartZ=0 EndX=0 EndY=6 EndZ=0
    g1: Circle CenterX=0 CenterY=0 CenterZ=0 NormalX=0 NormalY=0 NormalZ=1 AngleXU=0 Radius=1
    g2: Circle CenterX=8 CenterY=6 CenterZ=0 NormalX=0 NormalY=0 NormalZ=1 AngleXU=0 Radius=1
    g3: BSplineCurve PolesCount=3 KnotsCount=2 Degree=2 IsPeriodic=0
    g4: GeomPoint X=0 Y=0 Z=0
    g5: GeomPoint X=8 Y=6 Z=0
    g6: LineSegment StartX=0 StartY=6 StartZ=0 EndX=8 EndY=6 EndZ=0
  constraints (14):
    c: Coincident(g0,g-1)
    c: Distance(g0) = 6
    c: Vertical(g0)
    c: Coincident(g3,g0)
    c: Weight(g1) = 1
    c: Equal(g1,g2)
    c: InternalAlignment(g1,g3)
    c: InternalAlignment(g2,g3)
    c: InternalAlignment(g4,g3)
    c: InternalAlignment(g5,g3)
    c: Block(g3)
    c: Coincident(g6,g0)
    c: Coincident(g6,g3)
    c: Horizontal(g6)
FEATURE [Sketcher::SketchObject] Sketch046
  FullyConstrained = true
  sketch-geometry (7):
    g0: LineSegment StartX=0 StartY=0 StartZ=0 EndX=0 EndY=6 EndZ=0
    g1: Circle CenterX=0 CenterY=0 CenterZ=0 NormalX=0 NormalY=0 NormalZ=1 AngleXU=0 Radius=1
    g2: Circle CenterX=8 CenterY=6 CenterZ=0 NormalX=0 NormalY=0 NormalZ=1 AngleXU=0 Radius=1
    g3: BSplineCurve PolesCount=3 KnotsCount=2 Degree=2 IsPeriodic=0
    g4: GeomPoint X=0 Y=0 Z=0
    g5: GeomPoint X=8 Y=6 Z=0
    g6: LineSegment StartX=0 StartY=6 StartZ=0 EndX=8 EndY=6 EndZ=0
  constraints (14):
    c: Coincident(g0,g-1)
    c: Distance(g0) = 6
    c: Vertical(g0)
    c: Coincident(g3,g0)
    c: Weight(g1) = 1
    c: Equal(g1,g2)
    c: InternalAlignment(g1,g3)
    c: InternalAlignment(g2,g3)
    c: InternalAlignment(g4,g3)
    c: InternalAlignment(g5,g3)
    c: Block(g3)
    c: Coincident(g6,g0)
    c: Coincident(g6,g3)
    c: Horizontal(g6)
FEATURE [Part::Extrusion] Extrude036  label="caseScrewPillarBracket014"
  Base = -> Sketch045
  Dir = (0,0,1)
  DirMode = 2
  FaceMakerClass = Part::FaceMakerBullseye
  LengthFwd = 2.4
  LengthRev = 0
  Placement = pos=(110.7,29,6.77) rot=(0,-1,0;1.5708rad)
  Solid = true
  Symmetric = false
FEATURE [Part::Extrusion] Extrude037  label="caseScrewPillarBracket015"
  Base = -> Sketch046
  Dir = (0,0,1)
  DirMode = 2
  FaceMakerClass = Part::FaceMakerBullseye
  LengthFwd = 2.4
  LengthRev = 0
  Placement = pos=(108.3,29,65.23) rot=(0,1,0;1.5708rad)
  Solid = true
  Symmetric = false
FEATURE [Part::Box] Box013  label="frontCaseScrewPillarBracket002"
  AttacherType = Attacher::AttachEngine3D
  Height = 2.4
  Length = 22
  Placement = pos=(87,28,2.3) rot=(0,0,1;0rad)
  Width = 7
FEATURE [Part::Box] Box014  label="frontCaseScrewPillarBracket003"
  AttacherType = Attacher::AttachEngine3D
  Height = 2.4
  Length = 22
  Placement = pos=(87,28,67.3) rot=(0,0,1;0rad)
  Width = 7
FEATURE [Part::Feature] Face087
  shape: bbox 4.8 x 30.2 x 2e-07 mm, 1 faces, 0 solids (baked)
FEATURE [Part::Revolution] Revolve091  label="frontCaseScrewPost004"
  Angle = 360
  Axis = (0,1,0)
  Base = (0,0,0)
  FaceMakerClass = Part::FaceMakerBullseye
  Placement = pos=(89.5,4.5,3.5) rot=(0,0,1;0rad)
  Solid = false
  Source = -> Face087
  Symmetric = false
FEATURE [Part::Feature] Face088
  shape: bbox 4.8 x 30.2 x 2e-07 mm, 1 faces, 0 solids (baked)
FEATURE [Part::Revolution] Revolve092  label="frontCaseScrewPost005"
  Angle = 360
  Axis = (0,1,0)
  Base = (0,0,0)
  FaceMakerClass = Part::FaceMakerBullseye
  Placement = pos=(89.5,4.5,68.5) rot=(0,0,1;0rad)
  Solid = false
  Source = -> Face088
  Symmetric = false
FEATURE [Part::Feature] Face089
  shape: bbox 3.5 x 30.2 x 2e-07 mm, 1 faces, 0 solids (baked)
FEATURE [Part::Revolution] Revolve093  label="backCaseScrewPost002"
  Angle = 360
  Axis = (0,1,0)
  Base = (0,0,0)
  FaceMakerClass = Part::FaceMakerBullseye
  Placement = pos=(12.5,4.5,10) rot=(0,0,1;0rad)
  Solid = false
  Source = -> Face089
  Symmetric = false
FEATURE [Part::Feature] Face090
  shape: bbox 3.5 x 30.2 x 2e-07 mm, 1 faces, 0 solids (baked)
FEATURE [Part::Revolution] Revolve094  label="backCaseScrewPost003"
  Angle = 360
  Axis = (0,1,0)
  Base = (0,0,0)
  FaceMakerClass = Part::FaceMakerBullseye
  Placement = pos=(12.5,4.5,62) rot=(0,0,1;0rad)
  Solid = false
  Source = -> Face090
  Symmetric = false
FEATURE [Part::Box] Box015  label="Cube011"
  AttacherType = Attacher::AttachEngine3D
  Height = 28.8
  Length = 3
  Placement = pos=(107.3,28,21.6) rot=(0,0,1;0rad)
  Width = 7
FEATURE [Part::Box] Box016  label="Cube012"
  AttacherType = Attacher::AttachEngine3D
  Height = 3
  Length = 7.4
  Placement = pos=(107.3,28,18.6) rot=(0,0,1;0rad)
  Width = 7
FEATURE [Part::Box] Box017  label="Cube013"
  AttacherType = Attacher::AttachEngine3D
  Height = 3
  Length = 7.4
  Placement = pos=(107.3,28,50.4) rot=(0,0,1;0rad)
  Width = 7
FEATURE [Part::Cylinder] Cylinder024
  Angle = 360
  AttacherType = Attacher::AttachEngine3D
  Height = 20
  Placement = pos=(0,0,36.15) rot=(0,0,1;0rad)
  Radius = 14.3
FEATURE [Part::Cylinder] Cylinder025
  Angle = 360
  AttacherType = Attacher::AttachEngine3D
  Height = 10
  Placement = pos=(0,0,36.15) rot=(0,0,1;0rad)
  Radius = 4
FEATURE [Part::MultiFuse] Fusion066  label="removeToCreteHoleForPlugHousing009"
  Placement = pos=(70,19,36) rot=(0,1,0;1.5708rad)
  Shapes = -> [Cylinder024,Cylinder025]
FEATURE [Part::MultiFuse] Fusion065  label="plugHousingBracketHolder002"
  Shapes = -> [Box017,Box015,Box016]
FEATURE [Part::Cut] Cut025  label="plugHousingBracketHolder003"
  Base = -> Fusion065
  Placement = pos=(7,0,0) rot=(0,0,1;0rad)
  Tool = -> Fusion066
FEATURE [Sketcher::SketchObject] Sketch047
  FullyConstrained = false
  Placement = pos=(0,0,0) rot=(1,0,0;1.5708rad)
  sketch-geometry (24):
    g0: ArcOfCircle CenterX=-4 CenterY=-10.5 CenterZ=0 NormalX=0 NormalY=0 NormalZ=1 AngleXU=0 Radius=1.5 StartAngle=6e-16 EndAngle=3.14159
    g1: ArcOfCircle CenterX=-34.2 CenterY=-10.5 CenterZ=0 NormalX=0 NormalY=0 NormalZ=1 AngleXU=0 Radius=1.5 StartAngle=0 EndAngle=3.14159
    g2: ArcOfCircle CenterX=-34.2 CenterY=-27.7 CenterZ=0 NormalX=0 NormalY=0 NormalZ=1 AngleXU=0 Radius=1.5 StartAngle=3.14159 EndAngle=6.28319
    g3: ArcOfCircle CenterX=-4 CenterY=-27.7 CenterZ=0 NormalX=0 NormalY=0 NormalZ=1 AngleXU=0 Radius=1.5 StartAngle=3.1416 EndAngle=6.28319
    g4: ArcOfCircle CenterX=-10 CenterY=-4.3 CenterZ=0 NormalX=0 NormalY=0 NormalZ=1 AngleXU=0 Radius=1.5 StartAngle=2e-16 EndAngle=3.14159
    g5: ArcOfCircle CenterX=-16.1 CenterY=-1.8 CenterZ=0 NormalX=0 NormalY=0 NormalZ=1 AngleXU=0 Radius=1.5 StartAngle=5e-16 EndAngle=3.14159
    g6: ArcOfCircle CenterX=-22.1 CenterY=-1.8 CenterZ=0 NormalX=0 NormalY=0 NormalZ=1 AngleXU=0 Radius=1.5 StartAngle=5e-16 EndAngle=3.14159
    g7: ArcOfCircle CenterX=-28.2 CenterY=-4.3 CenterZ=0 NormalX=0 NormalY=0 NormalZ=1 AngleXU=0 Radius=1.5 StartAngle=2e-16 EndAngle=3.14159
    g8: ArcOfCircle CenterX=-10 CenterY=-33.9 CenterZ=0 NormalX=0 NormalY=0 NormalZ=1 AngleXU=0 Radius=1.5 StartAngle=3.14159 EndAngle=6.28319
    g9: ArcOfCircle CenterX=-16.1 CenterY=-36.4 CenterZ=0 NormalX=0 NormalY=0 NormalZ=1 AngleXU=0 Radius=1.5 StartAngle=3.14159 EndAngle=6.28319
    g10: ArcOfCircle CenterX=-22.1 CenterY=-36.4 CenterZ=0 NormalX=0 NormalY=0 NormalZ=1 AngleXU=0 Radius=1.5 StartAngle=3.14159 EndAngle=6.28319
    g11: ArcOfCircle CenterX=-28.2 CenterY=-33.9 CenterZ=0 NormalX=0 NormalY=0 NormalZ=1 AngleXU=0 Radius=1.5 StartAngle=3.14159 EndAngle=6.28319
    g12: LineSegment StartX=-35.7 StartY=-10.5 StartZ=0 EndX=-35.7 EndY=-27.7 EndZ=0
    g13: LineSegment StartX=-32.7 StartY=-10.5 StartZ=0 EndX=-32.7 EndY=-27.7 EndZ=0
    g14: LineSegment StartX=-29.7 StartY=-33.9 StartZ=0 EndX=-29.7 EndY=-4.3 EndZ=0
    g15: LineSegment StartX=-26.7 StartY=-33.9 StartZ=0 EndX=-26.7 EndY=-4.3 EndZ=0
    g16: LineSegment StartX=-2.5 StartY=-10.5 StartZ=0 EndX=-2.5 EndY=-27.7 EndZ=0
    g17: LineSegment StartX=-8.5 StartY=-4.3 StartZ=0 EndX=-8.5 EndY=-33.9 EndZ=0
    g18: LineSegment StartX=-5.5 StartY=-10.5 StartZ=0 EndX=-5.5 EndY=-27.7 EndZ=0
    g19: LineSegment StartX=-11.5 StartY=-4.3 StartZ=0 EndX=-11.5 EndY=-33.9 EndZ=0
    g20: LineSegment StartX=-14.6 StartY=-1.8 StartZ=0 EndX=-14.6 EndY=-36.4 EndZ=0
    g21: LineSegment StartX=-17.6 StartY=-1.8 StartZ=0 EndX=-17.6 EndY=-36.4 EndZ=0
    g22: LineSegment StartX=-20.6 StartY=-36.4 StartZ=0 EndX=-20.6 EndY=-1.8 EndZ=0
    g23: LineSegment StartX=-23.6 StartY=-1.8 StartZ=0 EndX=-23.6 EndY=-36.4 EndZ=0
  constraints (48):
    c: Block(g0)
    c: Block(g1)
    c: Block(g2)
    c: Block(g3)
    c: Block(g4)
    c: Block(g5)
    c: Block(g6)
    c: Block(g7)
    c: Block(g8)
    c: Block(g9)
    c: Block(g10)
    c: Block(g11)
    c: Coincident(g12,g1)
    c: Coincident(g12,g2)
    c: Vertical(g12)
    c: Coincident(g13,g1)
    c: Coincident(g13,g2)
    c: Vertical(g13)
    c: Coincident(g14,g11)
    c: Coincident(g14,g7)
    c: Vertical(g14)
    c: Coincident(g15,g11)
    c: Coincident(g15,g7)
    c: Vertical(g15)
    c: Coincident(g16,g0)
    c: Coincident(g16,g3)
    c: Vertical(g16)
    c: Coincident(g17,g4)
    c: Coincident(g17,g8)
    c: Vertical(g17)
    c: Coincident(g18,g0)
    c: Coincident(g18,g3)
    c: Vertical(g18)
    c: Coincident(g19,g4)
    c: Coincident(g19,g8)
    c: Vertical(g19)
    c: Coincident(g20,g5)
    c: Coincident(g20,g9)
    c: Vertical(g20)
    c: Coincident(g21,g5)
    c: Coincident(g21,g9)
    c: Vertical(g21)
    c: Coincident(g22,g10)
    c: Coincident(g22,g6)
    c: Vertical(g22)
    c: Coincident(g23,g6)
    c: Coincident(g23,g10)
    c: Vertical(g23)
FEATURE [Part::Extrusion] Extrude038  label="removeToCreateFanGrillHoles001"
  Base = -> Sketch047
  Dir = (0,-1,6e-16)
  DirMode = 2
  FaceMakerClass = Part::FaceMakerBullseye
  LengthFwd = 10
  LengthRev = 0
  Placement = pos=(65.4,44,54.82) rot=(0,0,1;0rad)
  Solid = true
  Symmetric = false
FEATURE [Part::Feature] Wire004
  shape: bbox 11 x 5.2 x 2e-07 mm, 0 faces, 0 solids (baked)
FEATURE [Part::Revolution] Revolve095
  Angle = 360
  Axis = (0,1,0)
  Base = (0,0,0)
  FaceMakerClass = Part::FaceMakerBullseye
  Placement = pos=(30.3,38,19.7) rot=(0,0,1;0rad)
  Solid = true
  Source = -> Wire004
  Symmetric = false
FEATURE [Part::Feature] Wire005
  shape: bbox 11 x 5.2 x 2e-07 mm, 0 faces, 0 solids (baked)
FEATURE [Part::Revolution] Revolve096
  Angle = 360
  Axis = (0,1,0)
  Base = (0,0,0)
  FaceMakerClass = Part::FaceMakerBullseye
  Placement = pos=(30.3,38,51.7) rot=(0,0,1;0rad)
  Solid = true
  Source = -> Wire005
  Symmetric = false
FEATURE [Part::Feature] Wire006
  shape: bbox 11 x 5.2 x 2e-07 mm, 0 faces, 0 solids (baked)
FEATURE [Part::Revolution] Revolve097
  Angle = 360
  Axis = (0,1,0)
  Base = (0,0,0)
  FaceMakerClass = Part::FaceMakerBullseye
  Placement = pos=(62.3,38,51.7) rot=(0,0,1;0rad)
  Solid = true
  Source = -> Wire006
  Symmetric = false
FEATURE [Part::Feature] Wire007
  shape: bbox 11 x 5.2 x 2e-07 mm, 0 faces, 0 solids (baked)
FEATURE [Part::Revolution] Revolve098
  Angle = 360
  Axis = (0,1,0)
  Base = (0,0,0)
  FaceMakerClass = Part::FaceMakerBullseye
  Placement = pos=(62.3,38,19.7) rot=(0,0,1;0rad)
  Solid = true
  Source = -> Wire007
  Symmetric = false
FEATURE [Part::MultiFuse] Fusion067  label="fanScrewHousing002"
  Shapes = -> [Revolve098,Revolve097,Revolve096,Revolve095]
FEATURE [Part::Feature] Face091 .. Face094  x4 (patterned run collapsed; names and placements below)
  shape: bbox 3.5 x 17.8 x 2e-07 mm, 1 faces, 0 solids (baked)
FEATURE [Part::Revolution] Revolve099  label="removeToCreateScrewAndThreadedInsertHole026"
  Angle = 360
  Axis = (0,1,0)
  Base = (0,0,0)
  FaceMakerClass = Part::FaceMakerBullseye
  Placement = pos=(62.3,30.3,19.7) rot=(0,0,1;0rad)
  Solid = false
  Source = -> Face091
  Symmetric = false
FEATURE [Part::Revolution] Revolve100  label="removeToCreateScrewAndThreadedInsertHole027"
  Angle = 360
  Axis = (0,1,0)
  Base = (0,0,0)
  FaceMakerClass = Part::FaceMakerBullseye
  Placement = pos=(62.3,30.3,51.7) rot=(0,0,1;0rad)
  Solid = false
  Source = -> Face092
  Symmetric = false
FEATURE [Part::Revolution] Revolve101  label="removeToCreateScrewAndThreadedInsertHole028"
  Angle = 360
  Axis = (0,1,0)
  Base = (0,0,0)
  FaceMakerClass = Part::FaceMakerBullseye
  Placement = pos=(30.3,30.3,19.7) rot=(0,0,1;0rad)
  Solid = false
  Source = -> Face093
  Symmetric = false
FEATURE [Part::Revolution] Revolve102  label="removeToCreateScrewAndThreadedInsertHole029"
  Angle = 360
  Axis = (0,1,0)
  Base = (0,0,0)
  FaceMakerClass = Part::FaceMakerBullseye
  Placement = pos=(30.3,30.3,51.7) rot=(0,0,1;0rad)
  Solid = false
  Source = -> Face094
  Symmetric = false
FEATURE [Part::MultiFuse] Fusion068  label="createThreadedInsertHolesForFan002"
  Shapes = -> [Revolve099,Revolve100,Revolve101,Revolve102]
FEATURE [Part::Cut] Cut026  label="fanScrewHousing003"
  Base = -> Fusion067
  Tool = -> Fusion068
FEATURE [Sketcher::SketchObject] Sketch048
  FullyConstrained = false
  Placement = pos=(0,0,0) rot=(1,0,0;1.5708rad)
  sketch-geometry (24):
    g0: ArcOfCircle CenterX=-4 CenterY=-10.5 CenterZ=0 NormalX=0 NormalY=0 NormalZ=1 AngleXU=0 Radius=1.5 StartAngle=6e-16 EndAngle=3.14159
    g1: ArcOfCircle CenterX=-34.2 CenterY=-10.5 CenterZ=0 NormalX=0 NormalY=0 NormalZ=1 AngleXU=0 Radius=1.5 StartAngle=0 EndAngle=3.14159
    g2: ArcOfCircle CenterX=-34.2 CenterY=-27.7 CenterZ=0 NormalX=0 NormalY=0 NormalZ=1 AngleXU=0 Radius=1.5 StartAngle=3.14159 EndAngle=6.28319
    g3: ArcOfCircle CenterX=-4 CenterY=-27.7 CenterZ=0 NormalX=0 NormalY=0 NormalZ=1 AngleXU=0 Radius=1.5 StartAngle=3.1416 EndAngle=6.28319
    g4: ArcOfCircle CenterX=-10 CenterY=-4.3 CenterZ=0 NormalX=0 NormalY=0 NormalZ=1 AngleXU=0 Radius=1.5 StartAngle=2e-16 EndAngle=3.14159
    g5: ArcOfCircle CenterX=-16.1 CenterY=-1.8 CenterZ=0 NormalX=0 NormalY=0 NormalZ=1 AngleXU=0 Radius=1.5 StartAngle=5e-16 EndAngle=3.14159
    g6: ArcOfCircle CenterX=-22.1 CenterY=-1.8 CenterZ=0 NormalX=0 NormalY=0 NormalZ=1 AngleXU=0 Radius=1.5 StartAngle=5e-16 EndAngle=3.14159
    g7: ArcOfCircle CenterX=-28.2 CenterY=-4.3 CenterZ=0 NormalX=0 NormalY=0 NormalZ=1 AngleXU=0 Radius=1.5 StartAngle=2e-16 EndAngle=3.14159
    g8: ArcOfCircle CenterX=-10 CenterY=-33.9 CenterZ=0 NormalX=0 NormalY=0 NormalZ=1 AngleXU=0 Radius=1.5 StartAngle=3.14159 EndAngle=6.28319
    g9: ArcOfCircle CenterX=-16.1 CenterY=-36.4 CenterZ=0 NormalX=0 NormalY=0 NormalZ=1 AngleXU=0 Radius=1.5 StartAngle=3.14159 EndAngle=6.28319
    g10: ArcOfCircle CenterX=-22.1 CenterY=-36.4 CenterZ=0 NormalX=0 NormalY=0 NormalZ=1 AngleXU=0 Radius=1.5 StartAngle=3.14159 EndAngle=6.28319
    g11: ArcOfCircle CenterX=-28.2 CenterY=-33.9 CenterZ=0 NormalX=0 NormalY=0 NormalZ=1 AngleXU=0 Radius=1.5 StartAngle=3.14159 EndAngle=6.28319
    g12: LineSegment StartX=-35.7 StartY=-10.5 StartZ=0 EndX=-35.7 EndY=-27.7 EndZ=0
    g13: LineSegment StartX=-32.7 StartY=-10.5 StartZ=0 EndX=-32.7 EndY=-27.7 EndZ=0
    g14: LineSegment StartX=-29.7 StartY=-33.9 StartZ=0 EndX=-29.7 EndY=-4.3 EndZ=0
    g15: LineSegment StartX=-26.7 StartY=-33.9 StartZ=0 EndX=-26.7 EndY=-4.3 EndZ=0
    g16: LineSegment StartX=-2.5 StartY=-10.5 StartZ=0 EndX=-2.5 EndY=-27.7 EndZ=0
    g17: LineSegment StartX=-8.5 StartY=-4.3 StartZ=0 EndX=-8.5 EndY=-33.9 EndZ=0
    g18: LineSegment StartX=-5.5 StartY=-10.5 StartZ=0 EndX=-5.5 EndY=-27.7 EndZ=0
    g19: LineSegment StartX=-11.5 StartY=-4.3 StartZ=0 EndX=-11.5 EndY=-33.9 EndZ=0
    g20: LineSegment StartX=-14.6 StartY=-1.8 StartZ=0 EndX=-14.6 EndY=-36.4 EndZ=0
    g21: LineSegment StartX=-17.6 StartY=-1.8 StartZ=0 EndX=-17.6 EndY=-36.4 EndZ=0
    g22: LineSegment StartX=-20.6 StartY=-36.4 StartZ=0 EndX=-20.6 EndY=-1.8 EndZ=0
    g23: LineSegment StartX=-23.6 StartY=-1.8 StartZ=0 EndX=-23.6 EndY=-36.4 EndZ=0
  constraints (48):
    c: Block(g0)
    c: Block(g1)
    c: Block(g2)
    c: Block(g3)
    c: Block(g4)
    c: Block(g5)
    c: Block(g6)
    c: Block(g7)
    c: Block(g8)
    c: Block(g9)
    c: Block(g10)
    c: Block(g11)
    c: Coincident(g12,g1)
    c: Coincident(g12,g2)
    c: Vertical(g12)
    c: Coincident(g13,g1)
    c: Coincident(g13,g2)
    c: Vertical(g13)
    c: Coincident(g14,g11)
    c: Coincident(g14,g7)
    c: Vertical(g14)
    c: Coincident(g15,g11)
    c: Coincident(g15,g7)
    c: Vertical(g15)
    c: Coincident(g16,g0)
    c: Coincident(g16,g3)
    c: Vertical(g16)
    c: Coincident(g17,g4)
    c: Coincident(g17,g8)
    c: Vertical(g17)
    c: Coincident(g18,g0)
    c: Coincident(g18,g3)
    c: Vertical(g18)
    c: Coincident(g19,g4)
    c: Coincident(g19,g8)
    c: Vertical(g19)
    c: Coincident(g20,g5)
    c: Coincident(g20,g9)
    c: Vertical(g20)
    c: Coincident(g21,g5)
    c: Coincident(g21,g9)
    c: Vertical(g21)
    c: Coincident(g22,g10)
    c: Coincident(g22,g6)
    c: Vertical(g22)
    c: Coincident(g23,g6)
    c: Coincident(g23,g10)
    c: Vertical(g23)
FEATURE [Part::Extrusion] Extrude039  label="removeToCreateFanGrillHoles002"
  Base = -> Sketch048
  Dir = (0,-1,6e-16)
  DirMode = 2
  FaceMakerClass = Part::FaceMakerBullseye
  LengthFwd = 10
  LengthRev = 0
  Placement = pos=(65.4,44,54.82) rot=(0,0,1;0rad)
  Solid = true
  Symmetric = false
FEATURE [Part::Cut] Cut027  label="fanScrewHousing004"
  Base = -> Cut026
  Tool = -> Extrude038
FEATURE [Part::Cut] Cut028  label="top014"
  Base = -> Fillet026
  Tool = -> Extrude039
FEATURE [Part::Feature] Face095 .. Face098  x4 (patterned run collapsed; names and placements below)
  shape: bbox 3.5 x 17.8 x 2e-07 mm, 1 faces, 0 solids (baked)
FEATURE [Part::Revolution] Revolve103  label="removeToCreateScrewAndThreadedInsertHole030"
  Angle = 360
  Axis = (0,1,0)
  Base = (0,0,0)
  FaceMakerClass = Part::FaceMakerBullseye
  Placement = pos=(62.3,30.3,19.7) rot=(0,0,1;0rad)
  Solid = false
  Source = -> Face095
  Symmetric = false
FEATURE [Part::Revolution] Revolve104  label="removeToCreateScrewAndThreadedInsertHole031"
  Angle = 360
  Axis = (0,1,0)
  Base = (0,0,0)
  FaceMakerClass = Part::FaceMakerBullseye
  Placement = pos=(62.3,30.3,51.7) rot=(0,0,1;0rad)
  Solid = false
  Source = -> Face096
  Symmetric = false
FEATURE [Part::Revolution] Revolve105  label="removeToCreateScrewAndThreadedInsertHole032"
  Angle = 360
  Axis = (0,1,0)
  Base = (0,0,0)
  FaceMakerClass = Part::FaceMakerBullseye
  Placement = pos=(30.3,30.3,19.7) rot=(0,0,1;0rad)
  Solid = false
  Source = -> Face097
  Symmetric = false
FEATURE [Part::Revolution] Revolve106  label="removeToCreateScrewAndThreadedInsertHole033"
  Angle = 360
  Axis = (0,1,0)
  Base = (0,0,0)
  FaceMakerClass = Part::FaceMakerBullseye
  Placement = pos=(30.3,30.3,51.7) rot=(0,0,1;0rad)
  Solid = false
  Source = -> Face098
  Symmetric = false
FEATURE [Part::MultiFuse] Fusion069  label="createThreadedInsertHolesForFan003"
  Shapes = -> [Revolve103,Revolve104,Revolve105,Revolve106]
FEATURE [Part::Cut] Cut029  label="top015"
  Base = -> Cut028
  Tool = -> Fusion054
FEATURE [Part::Cut] Cut030  label="fanScrewHousing005"
  Base = -> Cut027
  Tool = -> Fusion069
FEATURE [Part::Cylinder] Cylinder026  label="removeToCreteHoleForPlugHousing010"
  Angle = 360
  AttacherType = Attacher::AttachEngine3D
  Height = 20
  Placement = pos=(-2,19,36) rot=(0,1,0;1.5708rad)
  Radius = 14.3
FEATURE [Part::Box] Box018  label="removeToCreteHoleForPlugHousing011"
  AttacherType = Attacher::AttachEngine3D
  Height = 28.6
  Length = 10
  Placement = pos=(-2,0,21.7) rot=(0,0,1;0rad)
  Width = 19
FEATURE [Part::Box] Box019  label="wireHolderBottomCaseBit"
  AttacherType = Attacher::AttachEngine3D
  Height = 28
  Length = 3
  Placement = pos=(0,0,22) rot=(0,0,1;0rad)
  Width = 21
FEATURE [Part::Cylinder] Cylinder027  label="removeToCreteHoleForPlugHousing012"
  Angle = 360
  AttacherType = Attacher::AttachEngine3D
  Height = 20
  Placement = pos=(-2,19,36) rot=(0,1,0;1.5708rad)
  Radius = 14.3
FEATURE [Part::Cut] Cut031  label="wireHolderBottomCaseBit001"
  Base = -> Box019
  Tool = -> Cylinder027
FEATURE [Part::MultiFuse] Fusion070  label="removeToCreteHoleForPlugHousing013"
  Shapes = -> [Box018,Cylinder026]
FEATURE [Part::Cut] Cut032  label="top016"
  Base = -> Cut029
  Tool = -> Fusion070
FEATURE [Part::Cylinder] Cylinder028
  Angle = 360
  AttacherType = Attacher::AttachEngine3D
  Height = 20
  Placement = pos=(0,0,36.15) rot=(0,0,1;0rad)
  Radius = 14.3
FEATURE [Part::Cylinder] Cylinder029
  Angle = 360
  AttacherType = Attacher::AttachEngine3D
  Height = 10
  Placement = pos=(0,0,36.15) rot=(0,0,1;0rad)
  Radius = 4
FEATURE [Part::MultiFuse] Fusion071  label="removeToCreteHoleForPlugHousing014"
  Placement = pos=(70,19,36) rot=(0,1,0;1.5708rad)
  Shapes = -> [Cylinder028,Cylinder029]
FEATURE [Sketcher::SketchObject] Sketch049  label="topSketch011"
  FullyConstrained = true
  sketch-geometry (4):
    g0: ArcOfCircle CenterX=105 CenterY=19 CenterZ=0 NormalX=0 NormalY=0 NormalZ=1 AngleXU=0 Radius=20.6155 StartAngle=5.54125 EndAngle=6.28319
    g1: ArcOfCircle CenterX=105 CenterY=19 CenterZ=0 NormalX=0 NormalY=0 NormalZ=1 AngleXU=0 Radius=13 StartAngle=5.54125 EndAngle=6.28319
    g2: LineSegment StartX=118 StartY=19 StartZ=0 EndX=125.616 EndY=19 EndZ=0
    g3: LineSegment StartX=114.583 StartY=10.2157 StartZ=0 EndX=120.197 EndY=5.06982 EndZ=0
  constraints (7):
    c: Block(g0)
    c: Block(g1)
    c: Coincident(g2,g1)
    c: Coincident(g2,g0)
    c: Horizontal(g2)
    c: Coincident(g3,g1)
    c: Coincident(g3,g0)
FEATURE [Part::Box] Box020  label="removeToCreteHoleForPlugHousing015"
  AttacherType = Attacher::AttachEngine3D
  Height = 28.6
  Length = 20
  Placement = pos=(106.15,0,21.7) rot=(0,0,1;0rad)
  Width = 19
FEATURE [Part::MultiFuse] Fusion072  label="removeToCreteHoleForPlugHousing016"
  Shapes = -> [Box020,Fusion071]
FEATURE [Part::Cut] Cut033  label="removeToCreteHoleForPlugHousing017"
  Base = -> Cut032
  Tool = -> Fusion072
FEATURE [Part::Cylinder] Cylinder030
  Angle = 360
  AttacherType = Attacher::AttachEngine3D
  Height = 20
  Placement = pos=(0,0,36.15) rot=(0,0,1;0rad)
  Radius = 14.3
FEATURE [Part::Cylinder] Cylinder031
  Angle = 360
  AttacherType = Attacher::AttachEngine3D
  Height = 10
  Placement = pos=(0,0,36.15) rot=(0,0,1;0rad)
  Radius = 4
FEATURE [Part::Box] Box021  label="removeToCreteHoleForPlugHousing019"
  AttacherType = Attacher::AttachEngine3D
  Height = 28.6
  Length = 20
  Placement = pos=(106.15,0,21.7) rot=(0,0,1;0rad)
  Width = 19
FEATURE [Part::MultiFuse] Fusion074  label="removeToCreteHoleForPlugHousing020"
  Placement = pos=(70,19,36) rot=(0,1,0;1.5708rad)
  Shapes = -> [Cylinder030,Cylinder031]
FEATURE [Part::MultiFuse] Fusion073  label="removeToCreteHoleForPlugHousing018"
  Placement = pos=(0,0,28.3) rot=(0,0,1;0rad)
  Shapes = -> [Box021,Fusion074]
FEATURE [Part::Cylinder] Cylinder032
  Angle = 360
  AttacherType = Attacher::AttachEngine3D
  Height = 20
  Placement = pos=(0,0,36.15) rot=(0,0,1;0rad)
  Radius = 14.3
FEATURE [Part::Cylinder] Cylinder033
  Angle = 360
  AttacherType = Attacher::AttachEngine3D
  Height = 10
  Placement = pos=(0,0,36.15) rot=(0,0,1;0rad)
  Radius = 4
FEATURE [Part::Box] Box022  label="removeToCreteHoleForPlugHousing021"
  AttacherType = Attacher::AttachEngine3D
  Height = 28.6
  Length = 20
  Placement = pos=(106.15,0,21.7) rot=(0,0,1;0rad)
  Width = 19
FEATURE [Part::MultiFuse] Fusion076  label="removeToCreteHoleForPlugHousing023"
  Placement = pos=(70,19,36) rot=(0,1,0;1.5708rad)
  Shapes = -> [Cylinder032,Cylinder033]
FEATURE [Part::MultiFuse] Fusion075  label="removeToCreteHoleForPlugHousing022"
  Placement = pos=(0,0,-28.3) rot=(0,0,1;0rad)
  Shapes = -> [Box022,Fusion076]
FEATURE [Part::MultiFuse] Fusion077  label="removeToCreatePlugHousingBottomBit"
  Shapes = -> [Fusion075,Fusion073]
FEATURE [Part::Cylinder] Cylinder034
  Angle = 360
  AttacherType = Attacher::AttachEngine3D
  Height = 20
  Placement = pos=(0,0,36.15) rot=(0,0,1;0rad)
  Radius = 14
FEATURE [Part::Cylinder] Cylinder035
  Angle = 360
  AttacherType = Attacher::AttachEngine3D
  Height = 10
  Placement = pos=(0,0,36.15) rot=(0,0,1;0rad)
  Radius = 4
FEATURE [Part::MultiFuse] Fusion078  label="removeToCreteHoleForPlugHousing024"
  Placement = pos=(70,19,36) rot=(0,1,0;1.5708rad)
  Shapes = -> [Cylinder034,Cylinder035]
FEATURE [Part::MultiFuse] Fusion079  label="removeToCreatePlugHousingBottomBit001"
  Shapes = -> [Fusion078,Fusion077]
FEATURE [Part::Extrusion] Extrude040  label="bottomPlugHousingBit"
  Base = -> Sketch049
  Dir = (0,0,1)
  DirMode = 2
  FaceMakerClass = Part::FaceMakerBullseye
  LengthFwd = 72
  LengthRev = 0
  Solid = true
  Symmetric = false
FEATURE [Part::Cut] Cut034  label="bottomPlugHousingBit001"
  Base = -> Extrude040
  Placement = pos=(-0.09,0,0) rot=(0,0,1;0rad)
  Tool = -> Fusion079
FEATURE [Part::Box] Box023  label="Cube014"
  AttacherType = Attacher::AttachEngine3D
  Height = 16
  Length = 8
  Placement = pos=(12.7,31.52,28) rot=(0,0,1;0rad)
  Width = 4
FEATURE [Part::Cylinder] Cylinder036
  Angle = 360
  AttacherType = Attacher::AttachEngine3D
  Height = 10
  Placement = pos=(0,0,36.15) rot=(0,0,1;0rad)
  Radius = 4
FEATURE [Part::Cylinder] Cylinder037
  Angle = 360
  AttacherType = Attacher::AttachEngine3D
  Height = 20
  Placement = pos=(0,0,36.15) rot=(0,0,1;0rad)
  Radius = 8.2
FEATURE [Part::MultiFuse] Fusion080  label="removeToCreteHoleForPlugHousing025"
  Placement = pos=(-42,19,36) rot=(0,1,0;1.5708rad)
  Shapes = -> [Cylinder037,Cylinder036]
FEATURE [Sketcher::SketchObject] Sketch050  label="topSketch012"
  FullyConstrained = true
  sketch-geometry (4):
    g0: LineSegment StartX=16.8446 StartY=31.512 StartZ=0 EndX=16.3251 EndY=34.4666 EndZ=0
    g1: ArcOfCircle CenterX=19 CenterY=19.2524 CenterZ=0 NormalX=0 NormalY=0 NormalZ=1 AngleXU=0 Radius=15.4476 StartAngle=1.74483 EndAngle=2.72717
    g2: ArcOfCircle CenterX=19 CenterY=19.2524 CenterZ=0 NormalX=0 NormalY=0 NormalZ=1 AngleXU=0 Radius=12.4476 StartAngle=1.74483 EndAngle=2.73189
    g3: LineSegment StartX=4.86004 StartY=25.4725 StartZ=0 EndX=7.58253 EndY=24.2107 EndZ=0
  constraints (7):
    c: Block(g0)
    c: Coincident(g1,g0)
    c: Coincident(g2,g0)
    c: Coincident(g3,g1)
    c: Coincident(g3,g2)
    c: Block(g1)
    c: Block(g2)
FEATURE [Part::Extrusion] Extrude041
  Base = -> Sketch050
  Dir = (0,0,1)
  DirMode = 2
  FaceMakerClass = Part::FaceMakerBullseye
  LengthFwd = 10.6
  LengthRev = 0
  Placement = pos=(0,0,31) rot=(0,0,1;0rad)
  Solid = true
  Symmetric = false
FEATURE [Part::Cut] Cut035
  Base = -> Extrude041
  Placement = pos=(0,0,-0.3) rot=(0,0,1;0rad)
  Tool = -> Fusion080
FEATURE [Part::Cut] Cut036
  Base = -> Box023
  Tool = -> Cut035
FEATURE [Part::Fillet] Fillet027
  Base = -> Cut036
  Edges = 1 edges r=0.7: [Edge13]
FEATURE [Part::Fillet] Fillet028
  Base = -> Fillet027
  Edges = 1 edges r=0.7: [Edge13]
FEATURE [Part::Fillet] Fillet029
  Base = -> Fillet028
  Edges = 1 edges r=0.7: [Edge16]
FEATURE [Part::Fillet] Fillet030
  Base = -> Fillet029
  Edges = 1 edges r=0.7: [Edge11]
FEATURE [Part::Fillet] Fillet031
  Base = -> Fillet030
  Edges = 1 edges r=0.7: [Edge10]
FEATURE [Part::Fillet] Fillet032
  Base = -> Fillet031
  Edges = 1 edges r=1.2: [Edge5]
FEATURE [Part::Fillet] Fillet033
  Base = -> Fillet032
  Edges = 1 edges r=1.2: [Edge12]
FEATURE [Part::Fillet] Fillet034  label="wireHousingRetainer"
  Base = -> Fillet033
  Edges = 1 edges r=2: [Edge1]
  Placement = pos=(0.3,0,0) rot=(0,0,1;0rad)
FEATURE [Part::Feature] Face099
  shape: bbox 3.5 x 17.8 x 2e-07 mm, 1 faces, 0 solids (baked)
FEATURE [Part::Revolution] Revolve107  label="removeToCreateScrewAndThreadedInsertHole034"
  Angle = 360
  Axis = (0,1,0)
  Base = (0,0,0)
  FaceMakerClass = Part::FaceMakerBullseye
  Placement = pos=(12.5,0,10) rot=(0,0,1;0rad)
  Solid = false
  Source = -> Face099
  Symmetric = false
FEATURE [Part::Feature] Face100
  shape: bbox 3.5 x 17.8 x 2e-07 mm, 1 faces, 0 solids (baked)
FEATURE [Part::Revolution] Revolve108  label="removeToCreateScrewAndThreadedInsertHole035"
  Angle = 360
  Axis = (0,1,0)
  Base = (0,0,0)
  FaceMakerClass = Part::FaceMakerBullseye
  Placement = pos=(12.5,0,62) rot=(0,0,1;0rad)
  Solid = false
  Source = -> Face100
  Symmetric = false
FEATURE [Part::Feature] Face101
  shape: bbox 3.5 x 17.8 x 2e-07 mm, 1 faces, 0 solids (baked)
FEATURE [Part::Revolution] Revolve109  label="removeToCreateScrewAndThreadedInsertHole036"
  Angle = 360
  Axis = (0,1,0)
  Base = (0,0,0)
  FaceMakerClass = Part::FaceMakerBullseye
  Placement = pos=(89.5,0,68.5) rot=(0,0,1;0rad)
  Solid = false
  Source = -> Face101
  Symmetric = false
FEATURE [Part::Feature] Face102
  shape: bbox 3.5 x 17.8 x 2e-07 mm, 1 faces, 0 solids (baked)
FEATURE [Part::Revolution] Revolve110  label="removeToCreateScrewAndThreadedInsertHole037"
  Angle = 360
  Axis = (0,1,0)
  Base = (0,0,0)
  FaceMakerClass = Part::FaceMakerBullseye
  Placement = pos=(89.5,0,3.5) rot=(0,0,1;0rad)
  Solid = false
  Source = -> Face102
  Symmetric = false
FEATURE [Part::Feature] Face103
  shape: bbox 3.5 x 17.8 x 2e-07 mm, 1 faces, 0 solids (baked)
FEATURE [Part::Revolution] Revolve111  label="removeToCreateScrewAndThreadedInsertHole038"
  Angle = 360
  Axis = (0,1,0)
  Base = (0,0,0)
  FaceMakerClass = Part::FaceMakerBullseye
  Placement = pos=(109.5,4.7,3.5) rot=(0,0,1;0rad)
  Solid = false
  Source = -> Face103
  Symmetric = false
FEATURE [Part::Feature] Face104
  shape: bbox 3.5 x 17.8 x 2e-07 mm, 1 faces, 0 solids (baked)
FEATURE [Part::Revolution] Revolve112  label="removeToCreateScrewAndThreadedInsertHole039"
  Angle = 360
  Axis = (0,1,0)
  Base = (0,0,0)
  FaceMakerClass = Part::FaceMakerBullseye
  Placement = pos=(109.5,4.7,68.5) rot=(0,0,1;0rad)
  Solid = false
  Source = -> Face104
  Symmetric = false
FEATURE [Part::MultiFuse] Fusion081  label="removeToCreateScrewAndThreadedInsertHole040"
  Shapes = -> [Revolve107,Revolve108,Revolve109,Revolve110,Revolve111,Revolve112]
FEATURE [Part::MultiFuse] Fusion082  label="casePillars002"
  Shapes = -> [Revolve094,Revolve092,Revolve090,Revolve089,Revolve091,Revolve093]
FEATURE [Part::Cut] Cut037  label="casePillars003"
  Base = -> Fusion082
  Tool = -> Fusion081
FEATURE [Sketcher::SketchObject] Sketch051
  FullyConstrained = true
  Placement = pos=(117,19,0) rot=(0.57735,0.57735,0.57735;2.0944rad)
  sketch-geometry (48):
    g0: LineSegment StartX=-49.19 StartY=69.25 StartZ=0 EndX=-49.19 EndY=66.25 EndZ=0
    g1: LineSegment StartX=-49.19 StartY=63.5 StartZ=0 EndX=-49.19 EndY=60.5 EndZ=0
    g2: LineSegment StartX=-49.19 StartY=57.75 StartZ=0 EndX=-49.19 EndY=54.75 EndZ=0
    g3: LineSegment StartX=-49.19 StartY=52 StartZ=0 EndX=-49.19 EndY=49 EndZ=0
    g4: LineSegment StartX=-49.19 StartY=46.25 StartZ=0 EndX=-49.19 EndY=43.25 EndZ=0
    g5: LineSegment StartX=-49.19 StartY=40.5 StartZ=0 EndX=-49.19 EndY=37.5 EndZ=0
    g6: LineSegment StartX=-49.19 StartY=34.5 StartZ=0 EndX=-49.19 EndY=31.5 EndZ=0
    g7: LineSegment StartX=-49.19 StartY=28.75 StartZ=0 EndX=-49.19 EndY=25.75 EndZ=0
    g8: LineSegment StartX=-49.19 StartY=23 StartZ=0 EndX=-49.19 EndY=20 EndZ=0
    g9: LineSegment StartX=-49.19 StartY=17.25 StartZ=0 EndX=-49.19 EndY=14.25 EndZ=0
    g10: LineSegment StartX=-49.19 StartY=11.5 StartZ=0 EndX=-49.19 EndY=8.5 EndZ=0
    g11: LineSegment StartX=-49.19 StartY=5.75 StartZ=0 EndX=-49.19 EndY=2.75 EndZ=0
    g12: ArcOfCircle CenterX=-1.5 CenterY=67.75 CenterZ=0 NormalX=0 NormalY=0 NormalZ=1 AngleXU=0 Radius=1.5 StartAngle=4.71239 EndAngle=7.85398
    g13: ArcOfCircle CenterX=-1.5 CenterY=62 CenterZ=0 NormalX=0 NormalY=0 NormalZ=1 AngleXU=0 Radius=1.5 StartAngle=4.71239 EndAngle=7.85398
    g14: ArcOfCircle CenterX=-1.5 CenterY=56.25 CenterZ=0 NormalX=0 NormalY=0 NormalZ=1 AngleXU=0 Radius=1.5 StartAngle=4.71239 EndAngle=7.85398
    g15: ArcOfCircle CenterX=-11.49 CenterY=50.5 CenterZ=0 NormalX=0 NormalY=0 NormalZ=1 AngleXU=0 Radius=1.5 StartAngle=4.71239 EndAngle=7.85398
    g16: ArcOfCircle CenterX=-16.28 CenterY=44.75 CenterZ=0 NormalX=0 NormalY=0 NormalZ=1 AngleXU=0 Radius=1.5 StartAngle=4.71239 EndAngle=7.85398
    g17: ArcOfCircle CenterX=-18.2337 CenterY=39 CenterZ=0 NormalX=0 NormalY=0 NormalZ=1 AngleXU=0 Radius=1.5 StartAngle=4.71485 EndAngle=7.85398
    g18: ArcOfCircle CenterX=-16.2837 CenterY=27.25 CenterZ=0 NormalX=0 NormalY=0 NormalZ=1 AngleXU=0 Radius=1.5 StartAngle=4.71485 EndAngle=7.85398
    g19: ArcOfCircle CenterX=-18.2337 CenterY=33 CenterZ=0 NormalX=0 NormalY=0 NormalZ=1 AngleXU=0 Radius=1.5 StartAngle=4.71485 EndAngle=7.85398
    g20: ArcOfCircle CenterX=-11.49 CenterY=21.5 CenterZ=0 NormalX=0 NormalY=0 NormalZ=1 AngleXU=0 Radius=1.5 StartAngle=4.71239 EndAngle=7.85398
    g21: ArcOfCircle CenterX=-1.5 CenterY=4.25 CenterZ=0 NormalX=0 NormalY=0 NormalZ=1 AngleXU=0 Radius=1.5 StartAngle=4.71239 EndAngle=7.85398
    g22: ArcOfCircle CenterX=-1.5 CenterY=10 CenterZ=0 NormalX=0 NormalY=0 NormalZ=1 AngleXU=0 Radius=1.5 StartAngle=4.71239 EndAngle=7.85398
    g23: ArcOfCircle CenterX=-1.5 CenterY=15.75 CenterZ=0 NormalX=0 NormalY=0 NormalZ=1 AngleXU=0 Radius=1.5 StartAngle=4.71239 EndAngle=7.85398
    g24: LineSegment StartX=-49.19 StartY=69.25 StartZ=0 EndX=-1.5 EndY=69.25 EndZ=0
    g25: LineSegment StartX=-49.19 StartY=66.25 StartZ=0 EndX=-1.5 EndY=66.25 EndZ=0
    g26: LineSegment StartX=-49.19 StartY=63.5 StartZ=0 EndX=-1.5 EndY=63.5 EndZ=0
    g27: LineSegment StartX=-49.19 StartY=60.5 StartZ=0 EndX=-1.5 EndY=60.5 EndZ=0
    g28: LineSegment StartX=-49.19 StartY=57.75 StartZ=0 EndX=-1.5 EndY=57.75 EndZ=0
    g29: LineSegment StartX=-49.19 StartY=54.75 StartZ=0 EndX=-1.5 EndY=54.75 EndZ=0
    g30: LineSegment StartX=-49.19 StartY=52 StartZ=0 EndX=-11.49 EndY=52 EndZ=0
    g31: LineSegment StartX=-49.19 StartY=49 StartZ=0 EndX=-11.49 EndY=49 EndZ=0
    g32: LineSegment StartX=-49.19 StartY=46.25 StartZ=0 EndX=-16.28 EndY=46.25 EndZ=0
    g33: LineSegment StartX=-49.19 StartY=43.25 StartZ=0 EndX=-16.28 EndY=43.25 EndZ=0
    g34: LineSegment StartX=-49.19 StartY=40.5 StartZ=0 EndX=-18.2337 EndY=40.5 EndZ=0
    g35: LineSegment StartX=-49.19 StartY=37.5 StartZ=0 EndX=-18.23 EndY=37.5 EndZ=0
    g36: LineSegment StartX=-49.19 StartY=34.5 StartZ=0 EndX=-18.2337 EndY=34.5 EndZ=0
    g37: LineSegment StartX=-49.19 StartY=31.5 StartZ=0 EndX=-18.23 EndY=31.5 EndZ=0
    g38: LineSegment StartX=-49.19 StartY=28.75 StartZ=0 EndX=-16.2837 EndY=28.75 EndZ=0
    g39: LineSegment StartX=-49.19 StartY=25.75 StartZ=0 EndX=-16.28 EndY=25.75 EndZ=0
    g40: LineSegment StartX=-49.19 StartY=23 StartZ=0 EndX=-11.49 EndY=23 EndZ=0
    g41: LineSegment StartX=-49.19 StartY=20 StartZ=0 EndX=-11.49 EndY=20 EndZ=0
    g42: LineSegment StartX=-49.19 StartY=17.25 StartZ=0 EndX=-1.5 EndY=17.25 EndZ=0
    g43: LineSegment StartX=-49.19 StartY=14.25 StartZ=0 EndX=-1.5 EndY=14.25 EndZ=0
    g44: LineSegment StartX=-49.19 StartY=11.5 StartZ=0 EndX=-1.5 EndY=11.5 EndZ=0
    g45: LineSegment StartX=-49.19 StartY=8.5 StartZ=0 EndX=-1.5 EndY=8.5 EndZ=0
    g46: LineSegment StartX=-49.19 StartY=5.75 StartZ=0 EndX=-1.5 EndY=5.75 EndZ=0
    g47: LineSegment StartX=-49.19 StartY=2.75 StartZ=0 EndX=-1.5 EndY=2.75 EndZ=0
  constraints (120):
    c: Vertical(g0)
    c: Distance(g0) = 3
    c: Block(g0)
    c: Vertical(g1)
    c: Distance(g1) = 3
    c: Vertical(g2)
    c: Equal(g0,g2) = 3
    c: Block(g2)
    c: Vertical(g3)
    c: Equal(g1,g3) = 3
    c: Vertical(g4)
    c: Equal(g0,g4) = 3
    c: Block(g4)
    c: Vertical(g5)
    c: Equal(g1,g5) = 3
    c: Vertical(g6)
    c: Equal(g0,g6) = 3
    c: Block(g6)
    c: Vertical(g7)
    c: Equal(g1,g7) = 3
    c: Vertical(g8)
    c: Equal(g0,g8) = 3
    c: Block(g8)
    c: Vertical(g9)
    c: Equal(g1,g9) = 3
    c: Vertical(g10)
    c: Equal(g0,g10) = 3
    c: Block(g10)
    c: Vertical(g11)
    c: Equal(g1,g11) = 3
    c: Block(g12)
    c: Block(g13)
    c: Block(g14)
    c: Block(g15)
    c: Block(g16)
    c: Block(g17)
    c: Block(g18)
    c: Block(g19)
    c: Block(g20)
    c: Block(g21)
    c: Block(g22)
    c: Block(g23)
    c: Block(g11)
    c: Block(g9)
    c: Block(g7)
    c: Block(g5)
    c: Block(g3)
    c: Block(g1)
    c: Coincident(g24,g0)
    c: Coincident(g24,g12)
    c: Horizontal(g24)
    c: Coincident(g25,g0)
    c: Coincident(g25,g12)
    c: Horizontal(g25)
    c: Coincident(g26,g1)
    c: Coincident(g26,g13)
    c: Horizontal(g26)
    c: Coincident(g27,g1)
    c: Coincident(g27,g13)
    c: Horizontal(g27)
    c: Coincident(g28,g2)
    c: Coincident(g28,g14)
    c: Horizontal(g28)
    c: Coincident(g29,g2)
    c: Coincident(g29,g14)
    c: Horizontal(g29)
    c: Coincident(g30,g3)
    c: Coincident(g30,g15)
    c: Horizontal(g30)
    c: Coincident(g31,g3)
    c: Coincident(g31,g15)
    c: Horizontal(g31)
    c: Coincident(g32,g4)
    c: Coincident(g32,g16)
    c: Horizontal(g32)
    c: Coincident(g33,g4)
    c: Coincident(g33,g16)
    c: Horizontal(g33)
    c: Coincident(g34,g5)
    c: Coincident(g34,g17)
    c: Horizontal(g34)
    c: Coincident(g35,g5)
    c: Coincident(g35,g17)
    c: Horizontal(g35)
    c: Coincident(g36,g6)
    c: Coincident(g36,g19)
    c: Horizontal(g36)
    c: Coincident(g37,g6)
    c: Coincident(g37,g19)
    c: Horizontal(g37)
    c: Coincident(g38,g7)
    c: Coincident(g38,g18)
    c: Horizontal(g38)
    c: Coincident(g39,g7)
    c: Coincident(g39,g18)
    c: Horizontal(g39)
    c: Coincident(g40,g8)
    c: Coincident(g40,g20)
    c: Horizontal(g40)
    c: Coincident(g41,g8)
    c: Coincident(g41,g20)
    c: Horizontal(g41)
    c: Coincident(g42,g9)
    c: Coincident(g42,g23)
    c: Horizontal(g42)
    c: Coincident(g43,g9)
    c: Coincident(g43,g23)
    c: Horizontal(g43)
    c: Coincident(g44,g10)
    c: Coincident(g44,g22)
    c: Horizontal(g44)
    c: Coincident(g45,g10)
    c: Coincident(g45,g22)
    c: Horizontal(g45)
    c: Coincident(g46,g11)
    c: Coincident(g46,g21)
    c: Horizontal(g46)
    c: Coincident(g47,g11)
    c: Coincident(g47,g21)
    c: Horizontal(g47)
FEATURE [Part::Extrusion] Extrude042
  Base = -> Sketch051
  Dir = (1,-2e-16,2e-16)
  DirMode = 2
  FaceMakerClass = Part::FaceMakerBullseye
  LengthFwd = 19
  LengthRev = 0
  Placement = pos=(-19,0,0) rot=(0,0,1;0rad)
  Solid = true
  Symmetric = false
FEATURE [Part::Fillet] Fillet035  label="removeToCreateVentalationHoles"
  Base = -> Extrude042
  Edges = <same value as first occurrence — deduplicated (x6 in doc)>
  Placement = pos=(7,0,0) rot=(0,0,1;0rad)
FEATURE [Part::Cut] Cut038  label="top017"
  Base = -> Cut033
  Tool = -> Fillet035
FEATURE [Sketcher::SketchObject] Sketch052  label="bottomSketch001"
  FullyConstrained = true
  sketch-geometry (45):
    g0: LineSegment StartX=6.29999 StartY=8 StartZ=0 EndX=3.29999 EndY=8 EndZ=0
    g1: LineSegment StartX=3.29999 StartY=8 StartZ=0 EndX=3.29999 EndY=-6.03275e-07 EndZ=0
    g2: ArcOfCircle CenterX=8.29999 CenterY=5 CenterZ=0 NormalX=0 NormalY=0 NormalZ=1 AngleXU=0 Radius=2 StartAngle=3.14159 EndAngle=4.71239
    g3: LineSegment StartX=6.29999 StartY=8 StartZ=0 EndX=6.29999 EndY=5 EndZ=0
    g4: ArcOfCircle CenterX=105 CenterY=19 CenterZ=0 NormalX=0 NormalY=0 NormalZ=1 AngleXU=0 Radius=12.7 StartAngle=4.71239 EndAngle=5.94289
    g5-g11: Circle x7 (B-spline internal-alignment scaffolding for g12; pole/knot coordinates omitted)
    g12: BSplineCurve PolesCount=7 KnotsCount=5 Degree=3 IsPeriodic=0
    g13-g17: GeomPoint x5 (B-spline internal-alignment scaffolding for g12; pole/knot coordinates omitted)
    g18: ArcOfCircle CenterX=105 CenterY=19 CenterZ=0 NormalX=0 NormalY=0 NormalZ=1 AngleXU=0 Radius=15.7 StartAngle=5.81226 EndAngle=6.28319
    g19: BSplineCurve PolesCount=5 KnotsCount=3 Degree=3 IsPeriodic=0
    g20: LineSegment StartX=8.29999 StartY=3 StartZ=0 EndX=101.7 EndY=3 EndZ=0
    g21: LineSegment StartX=3.29999 StartY=-6.03275e-07 StartZ=0 EndX=105 EndY=-6.03275e-07 EndZ=0
    g22: LineSegment StartX=120.974 StartY=8.71251 StartZ=0 EndX=122.332 EndY=7.83778 EndZ=0
    g23: LineSegment StartX=105 StartY=-6.03274e-07 StartZ=0 EndX=113 EndY=-6.03274e-07 EndZ=0
    g24: ArcOfCircle CenterX=105 CenterY=19 CenterZ=0 NormalX=0 NormalY=0 NormalZ=1 AngleXU=0 Radius=20.6155 StartAngle=5.11091 EndAngle=5.71103
    g25: ArcOfCircle CenterX=117.7 CenterY=19 CenterZ=0 NormalX=0 NormalY=0 NormalZ=1 AngleXU=0 Radius=3 StartAngle=1.2e-15 EndAngle=2.10468
    g26: Circle CenterX=116.345 CenterY=16.3232 CenterZ=0 NormalX=0 NormalY=0 NormalZ=1 AngleXU=0 Radius=1
    g27: Circle CenterX=117.24 CenterY=15.7584 CenterZ=0 NormalX=0 NormalY=0 NormalZ=1 AngleXU=0 Radius=1
    g28: Circle CenterX=116.972 CenterY=14.7612 CenterZ=0 NormalX=0 NormalY=0 NormalZ=1 AngleXU=0 Radius=1
    g29: BSplineCurve PolesCount=3 KnotsCount=2 Degree=2 IsPeriodic=0
    g30: GeomPoint X=116.345 Y=16.3232 Z=0
    g31: GeomPoint X=116.972 Y=14.7612 Z=0
    g32: Circle CenterX=115.828 CenterY=17.157 CenterZ=0 NormalX=0 NormalY=0 NormalZ=1 AngleXU=0 Radius=1
    g33: Circle CenterX=115.841 CenterY=16.639 CenterZ=0 NormalX=0 NormalY=0 NormalZ=1 AngleXU=0 Radius=1
    g34: Circle CenterX=116.345 CenterY=16.3232 CenterZ=0 NormalX=0 NormalY=0 NormalZ=1 AngleXU=0 Radius=1
    g35: BSplineCurve PolesCount=3 KnotsCount=2 Degree=2 IsPeriodic=0
    g36: GeomPoint X=115.828 Y=17.157 Z=0
    g37: GeomPoint X=116.345 Y=16.3232 Z=0
    g38: LineSegment StartX=115.828 StartY=17.157 StartZ=0 EndX=115.828 EndY=20.8307 EndZ=0
    g39: Circle CenterX=115.828 CenterY=20.8307 CenterZ=0 NormalX=0 NormalY=0 NormalZ=1 AngleXU=0 Radius=1
    g40: Circle CenterX=115.831 CenterY=21.3396 CenterZ=0 NormalX=0 NormalY=0 NormalZ=1 AngleXU=0 Radius=1
    g41: Circle CenterX=116.173 CenterY=21.5825 CenterZ=0 NormalX=0 NormalY=0 NormalZ=1 AngleXU=0 Radius=1
    g42: BSplineCurve PolesCount=3 KnotsCount=2 Degree=2 IsPeriodic=0
    g43: GeomPoint X=115.828 Y=20.8307 Z=0
    g44: GeomPoint X=116.173 Y=21.5825 Z=0
  constraints (70):
    c: Horizontal(g0)
    c: Distance(g0) = 3
    c: Coincident(g1,g0)
    c: Vertical(g1)
    c: Block(g2)
    c: Block(g0)
    c: Coincident(g3,g0)
    c: Coincident(g3,g2)
    c: Vertical(g3)
    c: Block(g1)
    c: Block(g4)
    c: Coincident(g19,g4)
    c: Block(g19)
    c: Equal(g5, g6-g11) x6
    c: InternalAlignment(g5-g11 -> g12) x7
    c: InternalAlignment(g13-g17 -> g12) x5
    c: Block(g12)
    c: Coincident(g18,g12)
    c: Block(g18)
    c: Coincident(g20,g2)
    c: Coincident(g20,g19)
    c: Horizontal(g20)
    c: Distance(g20) = 93.4
    c: Coincident(g21,g1)
    c: Horizontal(g21)
    c: Distance(g21) = 101.7
    c: Horizontal(g23)
    c: Distance(g23) = 8
    c: Coincident(g24,g23)
    c: Block(g23)
    c: Coincident(g22,g24)
    c: Block(g24)
    c: Block(g22)
    c: Distance(g22) = 1.61553
    c: Coincident(g25,g18)
    c: Block(g25)
    c: Weight(g26) = 1
    c: Equal(g26,g27)
    c: Equal(g26,g28)
    c: Coincident(g29,g4)
    c: InternalAlignment(g26,g29)
    c: InternalAlignment(g27,g29)
    c: InternalAlignment(g28,g29)
    c: InternalAlignment(g30,g29)
    c: InternalAlignment(g31,g29)
    c: Block(g29)
    c: Weight(g32) = 1
    c: Equal(g32,g33)
    c: Equal(g32,g34)
    c: Coincident(g35,g29)
    c: InternalAlignment(g32,g35)
    c: InternalAlignment(g33,g35)
    c: InternalAlignment(g34,g35)
    c: InternalAlignment(g36,g35)
    c: InternalAlignment(g37,g35)
    c: Block(g35)
    c: Coincident(g38,g35)
    c: Vertical(g38)
    c: Block(g38)
    c: Coincident(g42,g38)
    c: Weight(g39) = 1
    c: Equal(g39,g40)
    c: Equal(g39,g41)
    c: Coincident(g42,g25)
    c: InternalAlignment(g39,g42)
    c: InternalAlignment(g40,g42)
    c: InternalAlignment(g41,g42)
    c: InternalAlignment(g43,g42)
    c: InternalAlignment(g44,g42)
    c: Block(g42)
FEATURE [Part::Extrusion] Extrude043  label="bottom010"
  Base = -> Sketch052
  Dir = (0,0,1)
  DirMode = 2
  FaceMakerClass = Part::FaceMakerBullseye
  LengthFwd = 71.4
  LengthRev = 0
  Placement = pos=(0,0,0.3) rot=(0,0,1;0rad)
  Solid = true
  Symmetric = false
FEATURE [Sketcher::SketchObject] Sketch053  label="topSketch013"
  FullyConstrained = true
  sketch-geometry (22):
    g0: LineSegment StartX=5.21097e-06 StartY=3 StartZ=0 EndX=5.21097e-06 EndY=19 EndZ=0
    g1: ArcOfCircle CenterX=19 CenterY=19 CenterZ=0 NormalX=0 NormalY=0 NormalZ=1 AngleXU=0 Radius=19 StartAngle=1.5708 EndAngle=3.14159
    g2: ArcOfCircle CenterX=19 CenterY=19 CenterZ=0 NormalX=0 NormalY=0 NormalZ=1 AngleXU=0 Radius=16 StartAngle=1.5708 EndAngle=3.14159
    g3: LineSegment StartX=114 StartY=35 StartZ=0 EndX=19 EndY=35 EndZ=0
    g4: LineSegment StartX=5.21097e-06 StartY=3 StartZ=0 EndX=5.21097e-06 EndY=0 EndZ=0
    g5: LineSegment StartX=3 StartY=0 StartZ=0 EndX=5.21097e-06 EndY=0 EndZ=0
    g6: LineSegment StartX=3 StartY=19 StartZ=0 EndX=3 EndY=0 EndZ=0
    g7: LineSegment StartX=19 StartY=38 StartZ=0 EndX=124 EndY=38 EndZ=0
    g8: Circle CenterX=119 CenterY=35 CenterZ=0 NormalX=0 NormalY=0 NormalZ=1 AngleXU=0 Radius=1
    g9: Circle CenterX=121 CenterY=35 CenterZ=0 NormalX=0 NormalY=0 NormalZ=1 AngleXU=0 Radius=1
    g10: Circle CenterX=121 CenterY=33 CenterZ=0 NormalX=0 NormalY=0 NormalZ=1 AngleXU=0 Radius=1
    g11: BSplineCurve PolesCount=3 KnotsCount=2 Degree=2 IsPeriodic=0
    g12: GeomPoint X=119 Y=35 Z=0
    g13: GeomPoint X=121 Y=33 Z=0
    g14: LineSegment StartX=119 StartY=35 StartZ=0 EndX=114 EndY=35 EndZ=0
    g15: ArcOfCircle CenterX=105 CenterY=19 CenterZ=0 NormalX=0 NormalY=0 NormalZ=1 AngleXU=0 Radius=16 StartAngle=5.60905 EndAngle=6.28319
    g16: LineSegment StartX=121 StartY=33 StartZ=0 EndX=121 EndY=19 EndZ=0
    g17: LineSegment StartX=117.5 StartY=9.01251 StartZ=0 EndX=121.163 EndY=9.0125 EndZ=0
    g18: ArcOfCircle CenterX=105 CenterY=19 CenterZ=0 NormalX=0 NormalY=0 NormalZ=1 AngleXU=0 Radius=20.6155 StartAngle=5.7297 EndAngle=6.28319
    g19: LineSegment StartX=121.163 StartY=9.0125 StartZ=0 EndX=122.538 EndY=8.16329 EndZ=0
    g20: LineSegment StartX=124 StartY=38 StartZ=0 EndX=125.616 EndY=38 EndZ=0
    g21: LineSegment StartX=125.616 StartY=19 StartZ=0 EndX=125.616 EndY=38 EndZ=0
  constraints (50):
    c: Vertical(g0)
    c: Block(g0)
    c: Coincident(g1,g0)
    c: Block(g1)
    c: Coincident(g2,g1)
    c: Block(g2)
    c: Coincident(g3,g2)
    c: Horizontal(g3)
    c: Tangent(g3,g2)
    c: Coincident(g4,g0)
    c: Distance(g4) = 3
    c: Vertical(g4)
    c: Coincident(g5,g4)
    c: Horizontal(g5)
    c: Coincident(g6,g2)
    c: Coincident(g6,g5)
    c: Vertical(g6)
    c: Horizontal(g7)
    c: Distance(g7) = 105
    c: Coincident(g7,g1)
    c: Block(g3)
    c: Weight(g8) = 1
    c: Equal(g8,g9)
    c: Equal(g8,g10)
    c: InternalAlignment(g8,g11)
    c: InternalAlignment(g9,g11)
    c: InternalAlignment(g10,g11)
    c: InternalAlignment(g12,g11)
    c: InternalAlignment(g13,g11)
    c: Block(g11)
    c: Coincident(g14,g11)
    c: Coincident(g14,g3)
    c: Horizontal(g14)
    c: Block(g15)
    c: Coincident(g16,g11)
    c: Coincident(g16,g15)
    c: Vertical(g16)
    c: Distance(g16) = 14
    c: Coincident(g17,g15)
    c: Block(g18)
    c: Coincident(g19,g18)
    c: Coincident(g20,g7)
    c: Horizontal(g20)
    c: Vertical(g21)
    c: Coincident(g20,g21)
    c: Block(g20)
    c: Block(g21)
    c: Block(g19)
    c: Block(g17)
    c: Distance(g20) = 1.61553
FEATURE [Part::Extrusion] Extrude044
  Base = -> Sketch053
  Dir = (0,0,1)
  DirMode = 2
  FaceMakerClass = Part::FaceMakerBullseye
  LengthFwd = 72
  LengthRev = 0
  Solid = true
  Symmetric = false
FEATURE [Part::Fillet] Fillet036  label="top018"
  Base = -> Extrude044
  Edges = 1 edges r=2: [Edge41]
FEATURE [Sketcher::SketchObject] Sketch054
  FullyConstrained = false
  Placement = pos=(0,0,0) rot=(1,0,0;1.5708rad)
  sketch-geometry (24):
    g0: ArcOfCircle CenterX=-4 CenterY=-10.5 CenterZ=0 NormalX=0 NormalY=0 NormalZ=1 AngleXU=0 Radius=1.5 StartAngle=6e-16 EndAngle=3.14159
    g1: ArcOfCircle CenterX=-34.2 CenterY=-10.5 CenterZ=0 NormalX=0 NormalY=0 NormalZ=1 AngleXU=0 Radius=1.5 StartAngle=0 EndAngle=3.14159
    g2: ArcOfCircle CenterX=-34.2 CenterY=-27.7 CenterZ=0 NormalX=0 NormalY=0 NormalZ=1 AngleXU=0 Radius=1.5 StartAngle=3.14159 EndAngle=6.28319
    g3: ArcOfCircle CenterX=-4 CenterY=-27.7 CenterZ=0 NormalX=0 NormalY=0 NormalZ=1 AngleXU=0 Radius=1.5 StartAngle=3.1416 EndAngle=6.28319
    g4: ArcOfCircle CenterX=-10 CenterY=-4.3 CenterZ=0 NormalX=0 NormalY=0 NormalZ=1 AngleXU=0 Radius=1.5 StartAngle=2e-16 EndAngle=3.14159
    g5: ArcOfCircle CenterX=-16.1 CenterY=-1.8 CenterZ=0 NormalX=0 NormalY=0 NormalZ=1 AngleXU=0 Radius=1.5 StartAngle=5e-16 EndAngle=3.14159
    g6: ArcOfCircle CenterX=-22.1 CenterY=-1.8 CenterZ=0 NormalX=0 NormalY=0 NormalZ=1 AngleXU=0 Radius=1.5 StartAngle=5e-16 EndAngle=3.14159
    g7: ArcOfCircle CenterX=-28.2 CenterY=-4.3 CenterZ=0 NormalX=0 NormalY=0 NormalZ=1 AngleXU=0 Radius=1.5 StartAngle=2e-16 EndAngle=3.14159
    g8: ArcOfCircle CenterX=-10 CenterY=-33.9 CenterZ=0 NormalX=0 NormalY=0 NormalZ=1 AngleXU=0 Radius=1.5 StartAngle=3.14159 EndAngle=6.28319
    g9: ArcOfCircle CenterX=-16.1 CenterY=-36.4 CenterZ=0 NormalX=0 NormalY=0 NormalZ=1 AngleXU=0 Radius=1.5 StartAngle=3.14159 EndAngle=6.28319
    g10: ArcOfCircle CenterX=-22.1 CenterY=-36.4 CenterZ=0 NormalX=0 NormalY=0 NormalZ=1 AngleXU=0 Radius=1.5 StartAngle=3.14159 EndAngle=6.28319
    g11: ArcOfCircle CenterX=-28.2 CenterY=-33.9 CenterZ=0 NormalX=0 NormalY=0 NormalZ=1 AngleXU=0 Radius=1.5 StartAngle=3.14159 EndAngle=6.28319
    g12: LineSegment StartX=-35.7 StartY=-10.5 StartZ=0 EndX=-35.7 EndY=-27.7 EndZ=0
    g13: LineSegment StartX=-32.7 StartY=-10.5 StartZ=0 EndX=-32.7 EndY=-27.7 EndZ=0
    g14: LineSegment StartX=-29.7 StartY=-33.9 StartZ=0 EndX=-29.7 EndY=-4.3 EndZ=0
    g15: LineSegment StartX=-26.7 StartY=-33.9 StartZ=0 EndX=-26.7 EndY=-4.3 EndZ=0
    g16: LineSegment StartX=-2.5 StartY=-10.5 StartZ=0 EndX=-2.5 EndY=-27.7 EndZ=0
    g17: LineSegment StartX=-8.5 StartY=-4.3 StartZ=0 EndX=-8.5 EndY=-33.9 EndZ=0
    g18: LineSegment StartX=-5.5 StartY=-10.5 StartZ=0 EndX=-5.5 EndY=-27.7 EndZ=0
    g19: LineSegment StartX=-11.5 StartY=-4.3 StartZ=0 EndX=-11.5 EndY=-33.9 EndZ=0
    g20: LineSegment StartX=-14.6 StartY=-1.8 StartZ=0 EndX=-14.6 EndY=-36.4 EndZ=0
    g21: LineSegment StartX=-17.6 StartY=-1.8 StartZ=0 EndX=-17.6 EndY=-36.4 EndZ=0
    g22: LineSegment StartX=-20.6 StartY=-36.4 StartZ=0 EndX=-20.6 EndY=-1.8 EndZ=0
    g23: LineSegment StartX=-23.6 StartY=-1.8 StartZ=0 EndX=-23.6 EndY=-36.4 EndZ=0
  constraints (48):
    c: Block(g0)
    c: Block(g1)
    c: Block(g2)
    c: Block(g3)
    c: Block(g4)
    c: Block(g5)
    c: Block(g6)
    c: Block(g7)
    c: Block(g8)
    c: Block(g9)
    c: Block(g10)
    c: Block(g11)
    c: Coincident(g12,g1)
    c: Coincident(g12,g2)
    c: Vertical(g12)
    c: Coincident(g13,g1)
    c: Coincident(g13,g2)
    c: Vertical(g13)
    c: Coincident(g14,g11)
    c: Coincident(g14,g7)
    c: Vertical(g14)
    c: Coincident(g15,g11)
    c: Coincident(g15,g7)
    c: Vertical(g15)
    c: Coincident(g16,g0)
    c: Coincident(g16,g3)
    c: Vertical(g16)
    c: Coincident(g17,g4)
    c: Coincident(g17,g8)
    c: Vertical(g17)
    c: Coincident(g18,g0)
    c: Coincident(g18,g3)
    c: Vertical(g18)
    c: Coincident(g19,g4)
    c: Coincident(g19,g8)
    c: Vertical(g19)
    c: Coincident(g20,g5)
    c: Coincident(g20,g9)
    c: Vertical(g20)
    c: Coincident(g21,g5)
    c: Coincident(g21,g9)
    c: Vertical(g21)
    c: Coincident(g22,g10)
    c: Coincident(g22,g6)
    c: Vertical(g22)
    c: Coincident(g23,g6)
    c: Coincident(g23,g10)
    c: Vertical(g23)
FEATURE [Part::Extrusion] Extrude045  label="removeToCreateFanGrillHoles003"
  Base = -> Sketch054
  Dir = (0,-1,6e-16)
  DirMode = 2
  FaceMakerClass = Part::FaceMakerBullseye
  LengthFwd = 10
  LengthRev = 0
  Placement = pos=(65.4,44,54.82) rot=(0,0,1;0rad)
  Solid = true
  Symmetric = false
FEATURE [Part::Feature] Face105 .. Face108  x4 (patterned run collapsed; names and placements below)
  shape: bbox 3.5 x 17.8 x 2e-07 mm, 1 faces, 0 solids (baked)
FEATURE [Part::Revolution] Revolve113  label="removeToCreateScrewAndThreadedInsertHole041"
  Angle = 360
  Axis = (0,1,0)
  Base = (0,0,0)
  FaceMakerClass = Part::FaceMakerBullseye
  Placement = pos=(62.3,30.3,19.7) rot=(0,0,1;0rad)
  Solid = false
  Source = -> Face105
  Symmetric = false
FEATURE [Part::Revolution] Revolve114  label="removeToCreateScrewAndThreadedInsertHole042"
  Angle = 360
  Axis = (0,1,0)
  Base = (0,0,0)
  FaceMakerClass = Part::FaceMakerBullseye
  Placement = pos=(62.3,30.3,51.7) rot=(0,0,1;0rad)
  Solid = false
  Source = -> Face106
  Symmetric = false
FEATURE [Part::Revolution] Revolve115  label="removeToCreateScrewAndThreadedInsertHole043"
  Angle = 360
  Axis = (0,1,0)
  Base = (0,0,0)
  FaceMakerClass = Part::FaceMakerBullseye
  Placement = pos=(30.3,30.3,19.7) rot=(0,0,1;0rad)
  Solid = false
  Source = -> Face107
  Symmetric = false
FEATURE [Part::Revolution] Revolve116  label="removeToCreateScrewAndThreadedInsertHole044"
  Angle = 360
  Axis = (0,1,0)
  Base = (0,0,0)
  FaceMakerClass = Part::FaceMakerBullseye
  Placement = pos=(30.3,30.3,51.7) rot=(0,0,1;0rad)
  Solid = false
  Source = -> Face108
  Symmetric = false
FEATURE [Part::MultiFuse] Fusion083  label="createThreadedInsertHolesForFan004"
  Shapes = -> [Revolve113,Revolve114,Revolve115,Revolve116]
FEATURE [Part::Box] Box024  label="removeToCreteHoleForPlugHousing026"
  AttacherType = Attacher::AttachEngine3D
  Height = 28.6
  Length = 10
  Placement = pos=(-2,0,21.7) rot=(0,0,1;0rad)
  Width = 19
FEATURE [Part::Cylinder] Cylinder038  label="removeToCreteHoleForPlugHousing027"
  Angle = 360
  AttacherType = Attacher::AttachEngine3D
  Height = 20
  Placement = pos=(-2,19,36) rot=(0,1,0;1.5708rad)
  Radius = 14.3
FEATURE [Part::MultiFuse] Fusion084  label="removeToCreteHoleForPlugHousing028"
  Shapes = -> [Box024,Cylinder038]
FEATURE [Part::Cylinder] Cylinder039
  Angle = 360
  AttacherType = Attacher::AttachEngine3D
  Height = 20
  Placement = pos=(0,0,36.15) rot=(0,0,1;0rad)
  Radius = 14.3
FEATURE [Part::Cylinder] Cylinder040
  Angle = 360
  AttacherType = Attacher::AttachEngine3D
  Height = 10
  Placement = pos=(0,0,36.15) rot=(0,0,1;0rad)
  Radius = 4
FEATURE [Part::Box] Box025  label="removeToCreteHoleForPlugHousing030"
  AttacherType = Attacher::AttachEngine3D
  Height = 28.6
  Length = 20
  Placement = pos=(106.15,0,21.7) rot=(0,0,1;0rad)
  Width = 19
FEATURE [Part::MultiFuse] Fusion086  label="removeToCreteHoleForPlugHousing031"
  Placement = pos=(70,19,36) rot=(0,1,0;1.5708rad)
  Shapes = -> [Cylinder039,Cylinder040]
FEATURE [Part::MultiFuse] Fusion085  label="removeToCreteHoleForPlugHousing029"
  Shapes = -> [Box025,Fusion086]
FEATURE [Sketcher::SketchObject] Sketch055
  FullyConstrained = true
  Placement = pos=(117,19,0) rot=(0.57735,0.57735,0.57735;2.0944rad)
  sketch-geometry (48):
    g0: LineSegment StartX=-49.19 StartY=69.25 StartZ=0 EndX=-49.19 EndY=66.25 EndZ=0
    g1: LineSegment StartX=-49.19 StartY=63.5 StartZ=0 EndX=-49.19 EndY=60.5 EndZ=0
    g2: LineSegment StartX=-49.19 StartY=57.75 StartZ=0 EndX=-49.19 EndY=54.75 EndZ=0
    g3: LineSegment StartX=-49.19 StartY=52 StartZ=0 EndX=-49.19 EndY=49 EndZ=0
    g4: LineSegment StartX=-49.19 StartY=46.25 StartZ=0 EndX=-49.19 EndY=43.25 EndZ=0
    g5: LineSegment StartX=-49.19 StartY=40.5 StartZ=0 EndX=-49.19 EndY=37.5 EndZ=0
    g6: LineSegment StartX=-49.19 StartY=34.5 StartZ=0 EndX=-49.19 EndY=31.5 EndZ=0
    g7: LineSegment StartX=-49.19 StartY=28.75 StartZ=0 EndX=-49.19 EndY=25.75 EndZ=0
    g8: LineSegment StartX=-49.19 StartY=23 StartZ=0 EndX=-49.19 EndY=20 EndZ=0
    g9: LineSegment StartX=-49.19 StartY=17.25 StartZ=0 EndX=-49.19 EndY=14.25 EndZ=0
    g10: LineSegment StartX=-49.19 StartY=11.5 StartZ=0 EndX=-49.19 EndY=8.5 EndZ=0
    g11: LineSegment StartX=-49.19 StartY=5.75 StartZ=0 EndX=-49.19 EndY=2.75 EndZ=0
    g12: ArcOfCircle CenterX=-1.5 CenterY=67.75 CenterZ=0 NormalX=0 NormalY=0 NormalZ=1 AngleXU=0 Radius=1.5 StartAngle=4.71239 EndAngle=7.85398
    g13: ArcOfCircle CenterX=-1.5 CenterY=62 CenterZ=0 NormalX=0 NormalY=0 NormalZ=1 AngleXU=0 Radius=1.5 StartAngle=4.71239 EndAngle=7.85398
    g14: ArcOfCircle CenterX=-1.5 CenterY=56.25 CenterZ=0 NormalX=0 NormalY=0 NormalZ=1 AngleXU=0 Radius=1.5 StartAngle=4.71239 EndAngle=7.85398
    g15: ArcOfCircle CenterX=-11.49 CenterY=50.5 CenterZ=0 NormalX=0 NormalY=0 NormalZ=1 AngleXU=0 Radius=1.5 StartAngle=4.71239 EndAngle=7.85398
    g16: ArcOfCircle CenterX=-16.28 CenterY=44.75 CenterZ=0 NormalX=0 NormalY=0 NormalZ=1 AngleXU=0 Radius=1.5 StartAngle=4.71239 EndAngle=7.85398
    g17: ArcOfCircle CenterX=-18.2337 CenterY=39 CenterZ=0 NormalX=0 NormalY=0 NormalZ=1 AngleXU=0 Radius=1.5 StartAngle=4.71485 EndAngle=7.85398
    g18: ArcOfCircle CenterX=-16.2837 CenterY=27.25 CenterZ=0 NormalX=0 NormalY=0 NormalZ=1 AngleXU=0 Radius=1.5 StartAngle=4.71485 EndAngle=7.85398
    g19: ArcOfCircle CenterX=-18.2337 CenterY=33 CenterZ=0 NormalX=0 NormalY=0 NormalZ=1 AngleXU=0 Radius=1.5 StartAngle=4.71485 EndAngle=7.85398
    g20: ArcOfCircle CenterX=-11.49 CenterY=21.5 CenterZ=0 NormalX=0 NormalY=0 NormalZ=1 AngleXU=0 Radius=1.5 StartAngle=4.71239 EndAngle=7.85398
    g21: ArcOfCircle CenterX=-1.5 CenterY=4.25 CenterZ=0 NormalX=0 NormalY=0 NormalZ=1 AngleXU=0 Radius=1.5 StartAngle=4.71239 EndAngle=7.85398
    g22: ArcOfCircle CenterX=-1.5 CenterY=10 CenterZ=0 NormalX=0 NormalY=0 NormalZ=1 AngleXU=0 Radius=1.5 StartAngle=4.71239 EndAngle=7.85398
    g23: ArcOfCircle CenterX=-1.5 CenterY=15.75 CenterZ=0 NormalX=0 NormalY=0 NormalZ=1 AngleXU=0 Radius=1.5 StartAngle=4.71239 EndAngle=7.85398
    g24: LineSegment StartX=-49.19 StartY=69.25 StartZ=0 EndX=-1.5 EndY=69.25 EndZ=0
    g25: LineSegment StartX=-49.19 StartY=66.25 StartZ=0 EndX=-1.5 EndY=66.25 EndZ=0
    g26: LineSegment StartX=-49.19 StartY=63.5 StartZ=0 EndX=-1.5 EndY=63.5 EndZ=0
    g27: LineSegment StartX=-49.19 StartY=60.5 StartZ=0 EndX=-1.5 EndY=60.5 EndZ=0
    g28: LineSegment StartX=-49.19 StartY=57.75 StartZ=0 EndX=-1.5 EndY=57.75 EndZ=0
    g29: LineSegment StartX=-49.19 StartY=54.75 StartZ=0 EndX=-1.5 EndY=54.75 EndZ=0
    g30: LineSegment StartX=-49.19 StartY=52 StartZ=0 EndX=-11.49 EndY=52 EndZ=0
    g31: LineSegment StartX=-49.19 StartY=49 StartZ=0 EndX=-11.49 EndY=49 EndZ=0
    g32: LineSegment StartX=-49.19 StartY=46.25 StartZ=0 EndX=-16.28 EndY=46.25 EndZ=0
    g33: LineSegment StartX=-49.19 StartY=43.25 StartZ=0 EndX=-16.28 EndY=43.25 EndZ=0
    g34: LineSegment StartX=-49.19 StartY=40.5 StartZ=0 EndX=-18.2337 EndY=40.5 EndZ=0
    g35: LineSegment StartX=-49.19 StartY=37.5 StartZ=0 EndX=-18.23 EndY=37.5 EndZ=0
    g36: LineSegment StartX=-49.19 StartY=34.5 StartZ=0 EndX=-18.2337 EndY=34.5 EndZ=0
    g37: LineSegment StartX=-49.19 StartY=31.5 StartZ=0 EndX=-18.23 EndY=31.5 EndZ=0
    g38: LineSegment StartX=-49.19 StartY=28.75 StartZ=0 EndX=-16.2837 EndY=28.75 EndZ=0
    g39: LineSegment StartX=-49.19 StartY=25.75 StartZ=0 EndX=-16.28 EndY=25.75 EndZ=0
    g40: LineSegment StartX=-49.19 StartY=23 StartZ=0 EndX=-11.49 EndY=23 EndZ=0
    g41: LineSegment StartX=-49.19 StartY=20 StartZ=0 EndX=-11.49 EndY=20 EndZ=0
    g42: LineSegment StartX=-49.19 StartY=17.25 StartZ=0 EndX=-1.5 EndY=17.25 EndZ=0
    g43: LineSegment StartX=-49.19 StartY=14.25 StartZ=0 EndX=-1.5 EndY=14.25 EndZ=0
    g44: LineSegment StartX=-49.19 StartY=11.5 StartZ=0 EndX=-1.5 EndY=11.5 EndZ=0
    g45: LineSegment StartX=-49.19 StartY=8.5 StartZ=0 EndX=-1.5 EndY=8.5 EndZ=0
    g46: LineSegment StartX=-49.19 StartY=5.75 StartZ=0 EndX=-1.5 EndY=5.75 EndZ=0
    g47: LineSegment StartX=-49.19 StartY=2.75 StartZ=0 EndX=-1.5 EndY=2.75 EndZ=0
  constraints (120):
    c: Vertical(g0)
    c: Distance(g0) = 3
    c: Block(g0)
    c: Vertical(g1)
    c: Distance(g1) = 3
    c: Vertical(g2)
    c: Equal(g0,g2) = 3
    c: Block(g2)
    c: Vertical(g3)
    c: Equal(g1,g3) = 3
    c: Vertical(g4)
    c: Equal(g0,g4) = 3
    c: Block(g4)
    c: Vertical(g5)
    c: Equal(g1,g5) = 3
    c: Vertical(g6)
    c: Equal(g0,g6) = 3
    c: Block(g6)
    c: Vertical(g7)
    c: Equal(g1,g7) = 3
    c: Vertical(g8)
    c: Equal(g0,g8) = 3
    c: Block(g8)
    c: Vertical(g9)
    c: Equal(g1,g9) = 3
    c: Vertical(g10)
    c: Equal(g0,g10) = 3
    c: Block(g10)
    c: Vertical(g11)
    c: Equal(g1,g11) = 3
    c: Block(g12)
    c: Block(g13)
    c: Block(g14)
    c: Block(g15)
    c: Block(g16)
    c: Block(g17)
    c: Block(g18)
    c: Block(g19)
    c: Block(g20)
    c: Block(g21)
    c: Block(g22)
    c: Block(g23)
    c: Block(g11)
    c: Block(g9)
    c: Block(g7)
    c: Block(g5)
    c: Block(g3)
    c: Block(g1)
    c: Coincident(g24,g0)
    c: Coincident(g24,g12)
    c: Horizontal(g24)
    c: Coincident(g25,g0)
    c: Coincident(g25,g12)
    c: Horizontal(g25)
    c: Coincident(g26,g1)
    c: Coincident(g26,g13)
    c: Horizontal(g26)
    c: Coincident(g27,g1)
    c: Coincident(g27,g13)
    c: Horizontal(g27)
    c: Coincident(g28,g2)
    c: Coincident(g28,g14)
    c: Horizontal(g28)
    c: Coincident(g29,g2)
    c: Coincident(g29,g14)
    c: Horizontal(g29)
    c: Coincident(g30,g3)
    c: Coincident(g30,g15)
    c: Horizontal(g30)
    c: Coincident(g31,g3)
    c: Coincident(g31,g15)
    c: Horizontal(g31)
    c: Coincident(g32,g4)
    c: Coincident(g32,g16)
    c: Horizontal(g32)
    c: Coincident(g33,g4)
    c: Coincident(g33,g16)
    c: Horizontal(g33)
    c: Coincident(g34,g5)
    c: Coincident(g34,g17)
    c: Horizontal(g34)
    c: Coincident(g35,g5)
    c: Coincident(g35,g17)
    c: Horizontal(g35)
    c: Coincident(g36,g6)
    c: Coincident(g36,g19)
    c: Horizontal(g36)
    c: Coincident(g37,g6)
    c: Coincident(g37,g19)
    c: Horizontal(g37)
    c: Coincident(g38,g7)
    c: Coincident(g38,g18)
    c: Horizontal(g38)
    c: Coincident(g39,g7)
    c: Coincident(g39,g18)
    c: Horizontal(g39)
    c: Coincident(g40,g8)
    c: Coincident(g40,g20)
    c: Horizontal(g40)
    c: Coincident(g41,g8)
    c: Coincident(g41,g20)
    c: Horizontal(g41)
    c: Coincident(g42,g9)
    c: Coincident(g42,g23)
    c: Horizontal(g42)
    c: Coincident(g43,g9)
    c: Coincident(g43,g23)
    c: Horizontal(g43)
    c: Coincident(g44,g10)
    c: Coincident(g44,g22)
    c: Horizontal(g44)
    c: Coincident(g45,g10)
    c: Coincident(g45,g22)
    c: Horizontal(g45)
    c: Coincident(g46,g11)
    c: Coincident(g46,g21)
    c: Horizontal(g46)
    c: Coincident(g47,g11)
    c: Coincident(g47,g21)
    c: Horizontal(g47)
FEATURE [Part::Extrusion] Extrude046
  Base = -> Sketch055
  Dir = (1,0,0)
  DirMode = 2
  FaceMakerClass = Part::FaceMakerBullseye
  LengthFwd = 23
  LengthRev = 0
  Placement = pos=(-19,0,0) rot=(0,0,1;0rad)
  Solid = true
  Symmetric = false
FEATURE [Part::Fillet] Fillet038  label="removeToCreateVentalationHoles001"
  Base = -> Extrude046
  Edges = <same value as first occurrence — deduplicated (x6 in doc)>
  Placement = pos=(7,0,0) rot=(0,0,1;0rad)
FEATURE [Sketcher::SketchObject] Sketch056  label="topSketch014"
  FullyConstrained = true
  sketch-geometry (22):
    g0: LineSegment StartX=5.21097e-06 StartY=3 StartZ=0 EndX=5.21097e-06 EndY=19 EndZ=0
    g1: ArcOfCircle CenterX=19 CenterY=19 CenterZ=0 NormalX=0 NormalY=0 NormalZ=1 AngleXU=0 Radius=19 StartAngle=1.5708 EndAngle=3.14159
    g2: ArcOfCircle CenterX=19 CenterY=19 CenterZ=0 NormalX=0 NormalY=0 NormalZ=1 AngleXU=0 Radius=16 StartAngle=1.5708 EndAngle=3.14159
    g3: LineSegment StartX=114 StartY=35 StartZ=0 EndX=19 EndY=35 EndZ=0
    g4: LineSegment StartX=5.21097e-06 StartY=3 StartZ=0 EndX=5.21097e-06 EndY=0 EndZ=0
    g5: LineSegment StartX=3 StartY=0 StartZ=0 EndX=5.21097e-06 EndY=0 EndZ=0
    g6: LineSegment StartX=3 StartY=19 StartZ=0 EndX=3 EndY=0 EndZ=0
    g7: LineSegment StartX=19 StartY=38 StartZ=0 EndX=124 EndY=38 EndZ=0
    g8: Circle CenterX=119 CenterY=35 CenterZ=0 NormalX=0 NormalY=0 NormalZ=1 AngleXU=0 Radius=1
    g9: Circle CenterX=121 CenterY=35 CenterZ=0 NormalX=0 NormalY=0 NormalZ=1 AngleXU=0 Radius=1
    g10: Circle CenterX=121 CenterY=33 CenterZ=0 NormalX=0 NormalY=0 NormalZ=1 AngleXU=0 Radius=1
    g11: BSplineCurve PolesCount=3 KnotsCount=2 Degree=2 IsPeriodic=0
    g12: GeomPoint X=119 Y=35 Z=0
    g13: GeomPoint X=121 Y=33 Z=0
    g14: LineSegment StartX=119 StartY=35 StartZ=0 EndX=114 EndY=35 EndZ=0
    g15: ArcOfCircle CenterX=105 CenterY=19 CenterZ=0 NormalX=0 NormalY=0 NormalZ=1 AngleXU=0 Radius=16 StartAngle=5.60905 EndAngle=6.28319
    g16: LineSegment StartX=121 StartY=33 StartZ=0 EndX=121 EndY=19 EndZ=0
    g17: LineSegment StartX=117.5 StartY=9.01251 StartZ=0 EndX=121.163 EndY=9.0125 EndZ=0
    g18: ArcOfCircle CenterX=105 CenterY=19 CenterZ=0 NormalX=0 NormalY=0 NormalZ=1 AngleXU=0 Radius=20.6155 StartAngle=5.7297 EndAngle=6.28319
    g19: LineSegment StartX=121.163 StartY=9.0125 StartZ=0 EndX=122.538 EndY=8.16329 EndZ=0
    g20: LineSegment StartX=124 StartY=38 StartZ=0 EndX=125.616 EndY=38 EndZ=0
    g21: LineSegment StartX=125.616 StartY=19 StartZ=0 EndX=125.616 EndY=38 EndZ=0
  constraints (49):
    c: Vertical(g0)
    c: Block(g0)
    c: Coincident(g1,g0)
    c: Block(g1)
    c: Coincident(g2,g1)
    c: Block(g2)
    c: Coincident(g3,g2)
    c: Horizontal(g3)
    c: Tangent(g3,g2)
    c: Coincident(g4,g0)
    c: Distance(g4) = 3
    c: Vertical(g4)
    c: Coincident(g5,g4)
    c: Horizontal(g5)
    c: Coincident(g6,g2)
    c: Coincident(g6,g5)
    c: Vertical(g6)
    c: Horizontal(g7)
    c: Distance(g7) = 105
    c: Coincident(g7,g1)
    c: Block(g3)
    c: Weight(g8) = 1
    c: Equal(g8,g9)
    c: Equal(g8,g10)
    c: InternalAlignment(g8,g11)
    c: InternalAlignment(g9,g11)
    c: InternalAlignment(g10,g11)
    c: InternalAlignment(g12,g11)
    c: InternalAlignment(g13,g11)
    c: Block(g11)
    c: Coincident(g14,g11)
    c: Coincident(g14,g3)
    c: Horizontal(g14)
    c: Block(g15)
    c: Coincident(g16,g11)
    c: Coincident(g16,g15)
    c: Vertical(g16)
    c: Distance(g16) = 14
    c: Coincident(g17,g15)
    c: Block(g18)
    c: Coincident(g19,g18)
    c: Coincident(g20,g7)
    c: Horizontal(g20)
    c: Vertical(g21)
    c: Coincident(g20,g21)
    c: Block(g20)
    c: Block(g21)
    c: Block(g19)
    c: Block(g17)
FEATURE [Part::Box] Box026  label="removeToCreteHoleForPlugHousing032"
  AttacherType = Attacher::AttachEngine3D
  Height = 28.6
  Length = 10
  Placement = pos=(-2,0,21.7) rot=(0,0,1;0rad)
  Width = 19
FEATURE [Part::Feature] Face109 .. Face112  x4 (patterned run collapsed; names and placements below)
  shape: bbox 3.5 x 17.8 x 2e-07 mm, 1 faces, 0 solids (baked)
FEATURE [Part::Revolution] Revolve117  label="removeToCreateScrewAndThreadedInsertHole045"
  Angle = 360
  Axis = (0,1,0)
  Base = (0,0,0)
  FaceMakerClass = Part::FaceMakerBullseye
  Placement = pos=(62.3,30.3,19.7) rot=(0,0,1;0rad)
  Solid = false
  Source = -> Face109
  Symmetric = false
FEATURE [Part::Revolution] Revolve118  label="removeToCreateScrewAndThreadedInsertHole046"
  Angle = 360
  Axis = (0,1,0)
  Base = (0,0,0)
  FaceMakerClass = Part::FaceMakerBullseye
  Placement = pos=(62.3,30.3,51.7) rot=(0,0,1;0rad)
  Solid = false
  Source = -> Face110
  Symmetric = false
FEATURE [Part::Revolution] Revolve119  label="removeToCreateScrewAndThreadedInsertHole047"
  Angle = 360
  Axis = (0,1,0)
  Base = (0,0,0)
  FaceMakerClass = Part::FaceMakerBullseye
  Placement = pos=(30.3,30.3,19.7) rot=(0,0,1;0rad)
  Solid = false
  Source = -> Face111
  Symmetric = false
FEATURE [Part::Revolution] Revolve120  label="removeToCreateScrewAndThreadedInsertHole048"
  Angle = 360
  Axis = (0,1,0)
  Base = (0,0,0)
  FaceMakerClass = Part::FaceMakerBullseye
  Placement = pos=(30.3,30.3,51.7) rot=(0,0,1;0rad)
  Solid = false
  Source = -> Face112
  Symmetric = false
FEATURE [Part::MultiFuse] Fusion087  label="createThreadedInsertHolesForFan005"
  Shapes = -> [Revolve117,Revolve118,Revolve119,Revolve120]
FEATURE [Part::Extrusion] Extrude047
  Base = -> Sketch056
  Dir = (0,0,1)
  DirMode = 2
  FaceMakerClass = Part::FaceMakerBullseye
  LengthFwd = 72
  LengthRev = 0
  Solid = true
  Symmetric = false
FEATURE [Part::Fillet] Fillet039  label="top019"
  Base = -> Extrude047
  Edges = 1 edges r=2: [Edge35]
FEATURE [Sketcher::SketchObject] Sketch057
  FullyConstrained = false
  Placement = pos=(0,0,0) rot=(1,0,0;1.5708rad)
  sketch-geometry (24):
    g0: ArcOfCircle CenterX=-4 CenterY=-10.5 CenterZ=0 NormalX=0 NormalY=0 NormalZ=1 AngleXU=0 Radius=1.5 StartAngle=6e-16 EndAngle=3.14159
    g1: ArcOfCircle CenterX=-34.2 CenterY=-10.5 CenterZ=0 NormalX=0 NormalY=0 NormalZ=1 AngleXU=0 Radius=1.5 StartAngle=0 EndAngle=3.14159
    g2: ArcOfCircle CenterX=-34.2 CenterY=-27.7 CenterZ=0 NormalX=0 NormalY=0 NormalZ=1 AngleXU=0 Radius=1.5 StartAngle=3.14159 EndAngle=6.28319
    g3: ArcOfCircle CenterX=-4 CenterY=-27.7 CenterZ=0 NormalX=0 NormalY=0 NormalZ=1 AngleXU=0 Radius=1.5 StartAngle=3.1416 EndAngle=6.28319
    g4: ArcOfCircle CenterX=-10 CenterY=-4.3 CenterZ=0 NormalX=0 NormalY=0 NormalZ=1 AngleXU=0 Radius=1.5 StartAngle=2e-16 EndAngle=3.14159
    g5: ArcOfCircle CenterX=-16.1 CenterY=-1.8 CenterZ=0 NormalX=0 NormalY=0 NormalZ=1 AngleXU=0 Radius=1.5 StartAngle=5e-16 EndAngle=3.14159
    g6: ArcOfCircle CenterX=-22.1 CenterY=-1.8 CenterZ=0 NormalX=0 NormalY=0 NormalZ=1 AngleXU=0 Radius=1.5 StartAngle=5e-16 EndAngle=3.14159
    g7: ArcOfCircle CenterX=-28.2 CenterY=-4.3 CenterZ=0 NormalX=0 NormalY=0 NormalZ=1 AngleXU=0 Radius=1.5 StartAngle=2e-16 EndAngle=3.14159
    g8: ArcOfCircle CenterX=-10 CenterY=-33.9 CenterZ=0 NormalX=0 NormalY=0 NormalZ=1 AngleXU=0 Radius=1.5 StartAngle=3.14159 EndAngle=6.28319
    g9: ArcOfCircle CenterX=-16.1 CenterY=-36.4 CenterZ=0 NormalX=0 NormalY=0 NormalZ=1 AngleXU=0 Radius=1.5 StartAngle=3.14159 EndAngle=6.28319
    g10: ArcOfCircle CenterX=-22.1 CenterY=-36.4 CenterZ=0 NormalX=0 NormalY=0 NormalZ=1 AngleXU=0 Radius=1.5 StartAngle=3.14159 EndAngle=6.28319
    g11: ArcOfCircle CenterX=-28.2 CenterY=-33.9 CenterZ=0 NormalX=0 NormalY=0 NormalZ=1 AngleXU=0 Radius=1.5 StartAngle=3.14159 EndAngle=6.28319
    g12: LineSegment StartX=-35.7 StartY=-10.5 StartZ=0 EndX=-35.7 EndY=-27.7 EndZ=0
    g13: LineSegment StartX=-32.7 StartY=-10.5 StartZ=0 EndX=-32.7 EndY=-27.7 EndZ=0
    g14: LineSegment StartX=-29.7 StartY=-33.9 StartZ=0 EndX=-29.7 EndY=-4.3 EndZ=0
    g15: LineSegment StartX=-26.7 StartY=-33.9 StartZ=0 EndX=-26.7 EndY=-4.3 EndZ=0
    g16: LineSegment StartX=-2.5 StartY=-10.5 StartZ=0 EndX=-2.5 EndY=-27.7 EndZ=0
    g17: LineSegment StartX=-8.5 StartY=-4.3 StartZ=0 EndX=-8.5 EndY=-33.9 EndZ=0
    g18: LineSegment StartX=-5.5 StartY=-10.5 StartZ=0 EndX=-5.5 EndY=-27.7 EndZ=0
    g19: LineSegment StartX=-11.5 StartY=-4.3 StartZ=0 EndX=-11.5 EndY=-33.9 EndZ=0
    g20: LineSegment StartX=-14.6 StartY=-1.8 StartZ=0 EndX=-14.6 EndY=-36.4 EndZ=0
    g21: LineSegment StartX=-17.6 StartY=-1.8 StartZ=0 EndX=-17.6 EndY=-36.4 EndZ=0
    g22: LineSegment StartX=-20.6 StartY=-36.4 StartZ=0 EndX=-20.6 EndY=-1.8 EndZ=0
    g23: LineSegment StartX=-23.6 StartY=-1.8 StartZ=0 EndX=-23.6 EndY=-36.4 EndZ=0
  constraints (48):
    c: Block(g0)
    c: Block(g1)
    c: Block(g2)
    c: Block(g3)
    c: Block(g4)
    c: Block(g5)
    c: Block(g6)
    c: Block(g7)
    c: Block(g8)
    c: Block(g9)
    c: Block(g10)
    c: Block(g11)
    c: Coincident(g12,g1)
    c: Coincident(g12,g2)
    c: Vertical(g12)
    c: Coincident(g13,g1)
    c: Coincident(g13,g2)
    c: Vertical(g13)
    c: Coincident(g14,g11)
    c: Coincident(g14,g7)
    c: Vertical(g14)
    c: Coincident(g15,g11)
    c: Coincident(g15,g7)
    c: Vertical(g15)
    c: Coincident(g16,g0)
    c: Coincident(g16,g3)
    c: Vertical(g16)
    c: Coincident(g17,g4)
    c: Coincident(g17,g8)
    c: Vertical(g17)
    c: Coincident(g18,g0)
    c: Coincident(g18,g3)
    c: Vertical(g18)
    c: Coincident(g19,g4)
    c: Coincident(g19,g8)
    c: Vertical(g19)
    c: Coincident(g20,g5)
    c: Coincident(g20,g9)
    c: Vertical(g20)
    c: Coincident(g21,g5)
    c: Coincident(g21,g9)
    c: Vertical(g21)
    c: Coincident(g22,g10)
    c: Coincident(g22,g6)
    c: Vertical(g22)
    c: Coincident(g23,g6)
    c: Coincident(g23,g10)
    c: Vertical(g23)
FEATURE [Part::Extrusion] Extrude048  label="removeToCreateFanGrillHoles004"
  Base = -> Sketch057
  Dir = (0,-1,6e-16)
  DirMode = 2
  FaceMakerClass = Part::FaceMakerBullseye
  LengthFwd = 10
  LengthRev = 0
  Placement = pos=(65.4,44,54.82) rot=(0,0,1;0rad)
  Solid = true
  Symmetric = false
FEATURE [Part::Cut] Cut040  label="top021"
  Base = -> Fillet039
  Tool = -> Extrude048
FEATURE [Part::Cylinder] Cylinder041  label="removeToCreteHoleForPlugHousing034"
  Angle = 360
  AttacherType = Attacher::AttachEngine3D
  Height = 20
  Placement = pos=(-2,19,36) rot=(0,1,0;1.5708rad)
  Radius = 14.3
FEATURE [Part::MultiFuse] Fusion089  label="removeToCreteHoleForPlugHousing035"
  Shapes = -> [Box026,Cylinder041]
FEATURE [Part::Cylinder] Cylinder042
  Angle = 360
  AttacherType = Attacher::AttachEngine3D
  Height = 20
  Placement = pos=(0,0,36.15) rot=(0,0,1;0rad)
  Radius = 14.3
FEATURE [Part::Cylinder] Cylinder043
  Angle = 360
  AttacherType = Attacher::AttachEngine3D
  Height = 10
  Placement = pos=(0,0,36.15) rot=(0,0,1;0rad)
  Radius = 4
FEATURE [Part::Box] Box027  label="removeToCreteHoleForPlugHousing036"
  AttacherType = Attacher::AttachEngine3D
  Height = 28.6
  Length = 20
  Placement = pos=(106.15,0,21.7) rot=(0,0,1;0rad)
  Width = 19
FEATURE [Part::Cut] Cut041  label="top022"
  Base = -> Cut040
  Tool = -> Fusion087
FEATURE [Part::Cut] Cut039  label="top020"
  Base = -> Cut041
  Tool = -> Fusion089
FEATURE [Part::MultiFuse] Fusion090  label="removeToCreteHoleForPlugHousing037"
  Placement = pos=(70,19,36) rot=(0,1,0;1.5708rad)
  Shapes = -> [Cylinder042,Cylinder043]
FEATURE [Part::MultiFuse] Fusion088  label="removeToCreteHoleForPlugHousing033"
  Shapes = -> [Box027,Fusion090]
FEATURE [Part::Cut] Cut042  label="removeToCreteHoleForPlugHousing038"
  Base = -> Cut039
  Tool = -> Fusion088
FEATURE [Part::MultiFuse] Fusion091  label="removeFromTop"
  Shapes = -> [Fillet038,Fusion085,Fusion084,Fusion083,Extrude045]
FEATURE [Part::Cut] Cut043  label="REAL TOP ====="
  Base = -> Fillet036
  Tool = -> Fusion091
FEATURE [Part::MultiFuse] Fusion092  label="caseScrewPillarBracket016"
  Shapes = -> [Extrude030,Extrude031,Extrude032,Extrude033,Extrude034,Extrude035,Extrude036,Extrude037,Box013,Box014]
FEATURE [Sketcher::SketchObject] Sketch058  label="topSketch015"
  FullyConstrained = true
  sketch-geometry (20):
    g0: LineSegment StartX=5.21097e-06 StartY=3 StartZ=0 EndX=5.21097e-06 EndY=19 EndZ=0
    g1: ArcOfCircle CenterX=19 CenterY=19 CenterZ=0 NormalX=0 NormalY=0 NormalZ=1 AngleXU=0 Radius=19 StartAngle=1.5708 EndAngle=3.14159
    g2: ArcOfCircle CenterX=19 CenterY=19 CenterZ=0 NormalX=0 NormalY=0 NormalZ=1 AngleXU=0 Radius=16 StartAngle=1.5708 EndAngle=3.14159
    g3: LineSegment StartX=114 StartY=35 StartZ=0 EndX=19 EndY=35 EndZ=0
    g4: LineSegment StartX=5.21097e-06 StartY=3 StartZ=0 EndX=5.21097e-06 EndY=0 EndZ=0
    g5: LineSegment StartX=3 StartY=0 StartZ=0 EndX=5.21097e-06 EndY=0 EndZ=0
    g6: LineSegment StartX=3 StartY=19 StartZ=0 EndX=3 EndY=0 EndZ=0
    g7: LineSegment StartX=19 StartY=38 StartZ=0 EndX=124 EndY=38 EndZ=0
    g8: Circle CenterX=119 CenterY=35 CenterZ=0 NormalX=0 NormalY=0 NormalZ=1 AngleXU=0 Radius=1
    g9: Circle CenterX=121 CenterY=35 CenterZ=0 NormalX=0 NormalY=0 NormalZ=1 AngleXU=0 Radius=1
    g10: Circle CenterX=121 CenterY=33 CenterZ=0 NormalX=0 NormalY=0 NormalZ=1 AngleXU=0 Radius=1
    g11: BSplineCurve PolesCount=3 KnotsCount=2 Degree=2 IsPeriodic=0
    g12: GeomPoint X=119 Y=35 Z=0
    g13: GeomPoint X=121 Y=33 Z=0
    g14: LineSegment StartX=119 StartY=35 StartZ=0 EndX=114 EndY=35 EndZ=0
    g15: ArcOfCircle CenterX=105 CenterY=19 CenterZ=0 NormalX=0 NormalY=0 NormalZ=1 AngleXU=0 Radius=19 StartAngle=5.7297 EndAngle=6.28319
    g16: ArcOfCircle CenterX=105 CenterY=19 CenterZ=0 NormalX=0 NormalY=0 NormalZ=1 AngleXU=0 Radius=16 StartAngle=5.60905 EndAngle=6.28319
    g17: LineSegment StartX=121 StartY=33 StartZ=0 EndX=121 EndY=19 EndZ=0
    g18: LineSegment StartX=124 StartY=38 StartZ=0 EndX=124 EndY=19 EndZ=0
    g19: LineSegment StartX=117.5 StartY=9.01251 StartZ=0 EndX=121.163 EndY=9.0125 EndZ=0
  constraints (46):
    c: Vertical(g0)
    c: Block(g0)
    c: Coincident(g1,g0)
    c: Block(g1)
    c: Coincident(g2,g1)
    c: Block(g2)
    c: Coincident(g3,g2)
    c: Horizontal(g3)
    c: Tangent(g3,g2)
    c: Coincident(g4,g0)
    c: Distance(g4) = 3
    c: Vertical(g4)
    c: Coincident(g5,g4)
    c: Horizontal(g5)
    c: Coincident(g6,g2)
    c: Coincident(g6,g5)
    c: Vertical(g6)
    c: Horizontal(g7)
    c: Distance(g7) = 105
    c: Coincident(g7,g1)
    c: Block(g3)
    c: Weight(g8) = 1
    c: Equal(g8,g9)
    c: Equal(g8,g10)
    c: InternalAlignment(g8,g11)
    c: InternalAlignment(g9,g11)
    c: InternalAlignment(g10,g11)
    c: InternalAlignment(g12,g11)
    c: InternalAlignment(g13,g11)
    c: Block(g11)
    c: Coincident(g14,g11)
    c: Coincident(g14,g3)
    c: Horizontal(g14)
    c: Block(g15)
    c: Coincident(g16,g15)
    c: Block(g16)
    c: Coincident(g17,g11)
    c: Coincident(g17,g16)
    c: Vertical(g17)
    c: Distance(g17) = 14
    c: Coincident(g18,g7)
    c: Coincident(g18,g15)
    c: Vertical(g18)
    c: Distance(g18) = 19
    c: Coincident(g19,g16)
    c: Coincident(g19,g15)
FEATURE [Part::Extrusion] Extrude049  label="top023"
  Base = -> Sketch058
  Dir = (0,0,1)
  DirMode = 2
  FaceMakerClass = Part::FaceMakerBullseye
  LengthFwd = 72
  LengthRev = 0
  Solid = true
  Symmetric = false
FEATURE [Sketcher::SketchObject] Sketch059
  FullyConstrained = true
  MapMode = 3
  Placement = pos=(0,0,0) rot=(1,0,0;1.5708rad)
  Support = -> [Extrude049]
  sketch-geometry (8):
    g0: Circle CenterX=80.351 CenterY=-67.6202 CenterZ=0 NormalX=0 NormalY=0 NormalZ=1 AngleXU=0 Radius=2
    g1: Circle CenterX=80.351 CenterY=-67.6202 CenterZ=0 NormalX=0 NormalY=0 NormalZ=1 AngleXU=0 Radius=3
    g2: Circle CenterX=80.351 CenterY=-4.92017 CenterZ=0 NormalX=0 NormalY=0 NormalZ=1 AngleXU=0 Radius=2
    g3: Circle CenterX=80.351 CenterY=-4.92017 CenterZ=0 NormalX=0 NormalY=0 NormalZ=1 AngleXU=0 Radius=3
    g4: Circle CenterX=23.851 CenterY=-4.92017 CenterZ=0 NormalX=0 NormalY=0 NormalZ=1 AngleXU=0 Radius=2
    g5: Circle CenterX=23.851 CenterY=-4.92017 CenterZ=0 NormalX=0 NormalY=0 NormalZ=1 AngleXU=0 Radius=3
    g6: Circle CenterX=23.851 CenterY=-67.6202 CenterZ=0 NormalX=0 NormalY=0 NormalZ=1 AngleXU=0 Radius=2
    g7: Circle CenterX=23.851 CenterY=-67.6202 CenterZ=0 NormalX=0 NormalY=0 NormalZ=1 AngleXU=0 Radius=3
  constraints (8):
    c: Block(g3)
    c: Block(g2)
    c: Block(g1)
    c: Block(g0)
    c: Block(g6)
    c: Block(g7)
    c: Block(g4)
    c: Block(g5)
FEATURE [Sketcher::SketchObject] Sketch060
  FullyConstrained = true
  MapMode = 3
  Placement = pos=(0,0,0) rot=(1,0,0;1.5708rad)
  Support = -> [Extrude049]
  sketch-geometry (8):
    g0: Circle CenterX=80.351 CenterY=-67.6202 CenterZ=0 NormalX=0 NormalY=0 NormalZ=1 AngleXU=0 Radius=3
    g1: Circle CenterX=80.351 CenterY=-4.92017 CenterZ=0 NormalX=0 NormalY=0 NormalZ=1 AngleXU=0 Radius=3
    g2: Circle CenterX=23.851 CenterY=-4.92017 CenterZ=0 NormalX=0 NormalY=0 NormalZ=1 AngleXU=0 Radius=3
    g3: Circle CenterX=23.851 CenterY=-67.6202 CenterZ=0 NormalX=0 NormalY=0 NormalZ=1 AngleXU=0 Radius=3
    g4: Circle CenterX=23.851 CenterY=-67.6202 CenterZ=0 NormalX=0 NormalY=0 NormalZ=1 AngleXU=0 Radius=5
    g5: Circle CenterX=80.351 CenterY=-67.6202 CenterZ=0 NormalX=0 NormalY=0 NormalZ=1 AngleXU=0 Radius=5
    g6: Circle CenterX=23.851 CenterY=-4.92017 CenterZ=0 NormalX=0 NormalY=0 NormalZ=1 AngleXU=0 Radius=5
    g7: Circle CenterX=80.351 CenterY=-4.92017 CenterZ=0 NormalX=0 NormalY=0 NormalZ=1 AngleXU=0 Radius=5
  constraints (8):
    c: Block(g1)
    c: Block(g0)
    c: Block(g3)
    c: Block(g2)
    c: Block(g5)
    c: Block(g4)
    c: Block(g6)
    c: Block(g7)
FEATURE [Sketcher::SketchObject] Sketch061
  FullyConstrained = true
  MapMode = 3
  Placement = pos=(0,0,0) rot=(1,0,0;1.5708rad)
  sketch-geometry (8):
    g0: Circle CenterX=80.351 CenterY=-67.6202 CenterZ=0 NormalX=0 NormalY=0 NormalZ=1 AngleXU=0 Radius=3
    g1: Circle CenterX=80.351 CenterY=-4.92017 CenterZ=0 NormalX=0 NormalY=0 NormalZ=1 AngleXU=0 Radius=3
    g2: Circle CenterX=23.851 CenterY=-4.92017 CenterZ=0 NormalX=0 NormalY=0 NormalZ=1 AngleXU=0 Radius=3
    g3: Circle CenterX=23.851 CenterY=-67.6202 CenterZ=0 NormalX=0 NormalY=0 NormalZ=1 AngleXU=0 Radius=3
    g4: Circle CenterX=23.851 CenterY=-67.6202 CenterZ=0 NormalX=0 NormalY=0 NormalZ=1 AngleXU=0 Radius=5
    g5: Circle CenterX=80.351 CenterY=-67.6202 CenterZ=0 NormalX=0 NormalY=0 NormalZ=1 AngleXU=0 Radius=5
    g6: Circle CenterX=23.851 CenterY=-4.92017 CenterZ=0 NormalX=0 NormalY=0 NormalZ=1 AngleXU=0 Radius=5
    g7: Circle CenterX=80.351 CenterY=-4.92017 CenterZ=0 NormalX=0 NormalY=0 NormalZ=1 AngleXU=0 Radius=5
  constraints (8):
    c: Block(g1)
    c: Block(g0)
    c: Block(g3)
    c: Block(g2)
    c: Block(g5)
    c: Block(g4)
    c: Block(g6)
    c: Block(g7)
FEATURE [Sketcher::SketchObject] Sketch062  label="topSketch016"
  FullyConstrained = true
  sketch-geometry (20):
    g0: LineSegment StartX=5.21097e-06 StartY=3 StartZ=0 EndX=5.21097e-06 EndY=19 EndZ=0
    g1: ArcOfCircle CenterX=19 CenterY=19 CenterZ=0 NormalX=0 NormalY=0 NormalZ=1 AngleXU=0 Radius=19 StartAngle=1.5708 EndAngle=3.14159
    g2: ArcOfCircle CenterX=19 CenterY=19 CenterZ=0 NormalX=0 NormalY=0 NormalZ=1 AngleXU=0 Radius=16 StartAngle=1.5708 EndAngle=3.14159
    g3: LineSegment StartX=114 StartY=35 StartZ=0 EndX=19 EndY=35 EndZ=0
    g4: LineSegment StartX=5.21097e-06 StartY=3 StartZ=0 EndX=5.21097e-06 EndY=0 EndZ=0
    g5: LineSegment StartX=3 StartY=0 StartZ=0 EndX=5.21097e-06 EndY=0 EndZ=0
    g6: LineSegment StartX=3 StartY=19 StartZ=0 EndX=3 EndY=0 EndZ=0
    g7: LineSegment StartX=19 StartY=38 StartZ=0 EndX=124 EndY=38 EndZ=0
    g8: Circle CenterX=119 CenterY=35 CenterZ=0 NormalX=0 NormalY=0 NormalZ=1 AngleXU=0 Radius=1
    g9: Circle CenterX=121 CenterY=35 CenterZ=0 NormalX=0 NormalY=0 NormalZ=1 AngleXU=0 Radius=1
    g10: Circle CenterX=121 CenterY=33 CenterZ=0 NormalX=0 NormalY=0 NormalZ=1 AngleXU=0 Radius=1
    g11: BSplineCurve PolesCount=3 KnotsCount=2 Degree=2 IsPeriodic=0
    g12: GeomPoint X=119 Y=35 Z=0
    g13: GeomPoint X=121 Y=33 Z=0
    g14: LineSegment StartX=119 StartY=35 StartZ=0 EndX=114 EndY=35 EndZ=0
    g15: ArcOfCircle CenterX=105 CenterY=19 CenterZ=0 NormalX=0 NormalY=0 NormalZ=1 AngleXU=0 Radius=19 StartAngle=5.7297 EndAngle=6.28319
    g16: ArcOfCircle CenterX=105 CenterY=19 CenterZ=0 NormalX=0 NormalY=0 NormalZ=1 AngleXU=0 Radius=16 StartAngle=5.60905 EndAngle=6.28319
    g17: LineSegment StartX=121 StartY=33 StartZ=0 EndX=121 EndY=19 EndZ=0
    g18: LineSegment StartX=124 StartY=38 StartZ=0 EndX=124 EndY=19 EndZ=0
    g19: LineSegment StartX=117.5 StartY=9.01251 StartZ=0 EndX=121.163 EndY=9.0125 EndZ=0
  constraints (46):
    c: Vertical(g0)
    c: Block(g0)
    c: Coincident(g1,g0)
    c: Block(g1)
    c: Coincident(g2,g1)
    c: Block(g2)
    c: Coincident(g3,g2)
    c: Horizontal(g3)
    c: Tangent(g3,g2)
    c: Coincident(g4,g0)
    c: Distance(g4) = 3
    c: Vertical(g4)
    c: Coincident(g5,g4)
    c: Horizontal(g5)
    c: Coincident(g6,g2)
    c: Coincident(g6,g5)
    c: Vertical(g6)
    c: Horizontal(g7)
    c: Distance(g7) = 105
    c: Coincident(g7,g1)
    c: Block(g3)
    c: Weight(g8) = 1
    c: Equal(g8,g9)
    c: Equal(g8,g10)
    c: InternalAlignment(g8,g11)
    c: InternalAlignment(g9,g11)
    c: InternalAlignment(g10,g11)
    c: InternalAlignment(g12,g11)
    c: InternalAlignment(g13,g11)
    c: Block(g11)
    c: Coincident(g14,g11)
    c: Coincident(g14,g3)
    c: Horizontal(g14)
    c: Block(g15)
    c: Coincident(g16,g15)
    c: Block(g16)
    c: Coincident(g17,g11)
    c: Coincident(g17,g16)
    c: Vertical(g17)
    c: Distance(g17) = 14
    c: Coincident(g18,g7)
    c: Coincident(g18,g15)
    c: Vertical(g18)
    c: Distance(g18) = 19
    c: Coincident(g19,g16)
    c: Coincident(g19,g15)
FEATURE [Part::Extrusion] Extrude053  label="top024"
  Base = -> Sketch062
  Dir = (0,0,1)
  DirMode = 2
  FaceMakerClass = Part::FaceMakerBullseye
  LengthFwd = 72
  LengthRev = 0
  Solid = true
  Symmetric = false
FEATURE [Sketcher::SketchObject] Sketch063
  FullyConstrained = true
  MapMode = 3
  Placement = pos=(0,0,0) rot=(1,0,0;1.5708rad)
  Support = -> [Extrude053]
  sketch-geometry (8):
    g0: Circle CenterX=80.351 CenterY=-67.6202 CenterZ=0 NormalX=0 NormalY=0 NormalZ=1 AngleXU=0 Radius=2
    g1: Circle CenterX=80.351 CenterY=-67.6202 CenterZ=0 NormalX=0 NormalY=0 NormalZ=1 AngleXU=0 Radius=3
    g2: Circle CenterX=80.351 CenterY=-4.92017 CenterZ=0 NormalX=0 NormalY=0 NormalZ=1 AngleXU=0 Radius=2
    g3: Circle CenterX=80.351 CenterY=-4.92017 CenterZ=0 NormalX=0 NormalY=0 NormalZ=1 AngleXU=0 Radius=3
    g4: Circle CenterX=23.851 CenterY=-4.92017 CenterZ=0 NormalX=0 NormalY=0 NormalZ=1 AngleXU=0 Radius=2
    g5: Circle CenterX=23.851 CenterY=-4.92017 CenterZ=0 NormalX=0 NormalY=0 NormalZ=1 AngleXU=0 Radius=3
    g6: Circle CenterX=23.851 CenterY=-67.6202 CenterZ=0 NormalX=0 NormalY=0 NormalZ=1 AngleXU=0 Radius=2
    g7: Circle CenterX=23.851 CenterY=-67.6202 CenterZ=0 NormalX=0 NormalY=0 NormalZ=1 AngleXU=0 Radius=3
  constraints (8):
    c: Block(g3)
    c: Block(g2)
    c: Block(g1)
    c: Block(g0)
    c: Block(g6)
    c: Block(g7)
    c: Block(g4)
    c: Block(g5)
FEATURE [Part::Extrusion] Extrude054
  Base = -> Sketch063
  Dir = (0,-1,2e-16)
  DirMode = 2
  FaceMakerClass = Part::FaceMakerBullseye
  LengthFwd = 6
  LengthRev = 0
  Placement = pos=(0,9,0) rot=(0,0,1;0rad)
  Solid = true
  Symmetric = false
FEATURE [Sketcher::SketchObject] Sketch064  label="topSketch017"
  FullyConstrained = true
  sketch-geometry (20):
    g0: LineSegment StartX=5.21097e-06 StartY=3 StartZ=0 EndX=5.21097e-06 EndY=19 EndZ=0
    g1: ArcOfCircle CenterX=19 CenterY=19 CenterZ=0 NormalX=0 NormalY=0 NormalZ=1 AngleXU=0 Radius=19 StartAngle=1.5708 EndAngle=3.14159
    g2: ArcOfCircle CenterX=19 CenterY=19 CenterZ=0 NormalX=0 NormalY=0 NormalZ=1 AngleXU=0 Radius=16 StartAngle=1.5708 EndAngle=3.14159
    g3: LineSegment StartX=114 StartY=35 StartZ=0 EndX=19 EndY=35 EndZ=0
    g4: LineSegment StartX=5.21097e-06 StartY=3 StartZ=0 EndX=5.21097e-06 EndY=0 EndZ=0
    g5: LineSegment StartX=3 StartY=0 StartZ=0 EndX=5.21097e-06 EndY=0 EndZ=0
    g6: LineSegment StartX=3 StartY=19 StartZ=0 EndX=3 EndY=0 EndZ=0
    g7: LineSegment StartX=19 StartY=38 StartZ=0 EndX=124 EndY=38 EndZ=0
    g8: Circle CenterX=119 CenterY=35 CenterZ=0 NormalX=0 NormalY=0 NormalZ=1 AngleXU=0 Radius=1
    g9: Circle CenterX=121 CenterY=35 CenterZ=0 NormalX=0 NormalY=0 NormalZ=1 AngleXU=0 Radius=1
    g10: Circle CenterX=121 CenterY=33 CenterZ=0 NormalX=0 NormalY=0 NormalZ=1 AngleXU=0 Radius=1
    g11: BSplineCurve PolesCount=3 KnotsCount=2 Degree=2 IsPeriodic=0
    g12: GeomPoint X=119 Y=35 Z=0
    g13: GeomPoint X=121 Y=33 Z=0
    g14: LineSegment StartX=119 StartY=35 StartZ=0 EndX=114 EndY=35 EndZ=0
    g15: ArcOfCircle CenterX=105 CenterY=19 CenterZ=0 NormalX=0 NormalY=0 NormalZ=1 AngleXU=0 Radius=19 StartAngle=5.7297 EndAngle=6.28319
    g16: ArcOfCircle CenterX=105 CenterY=19 CenterZ=0 NormalX=0 NormalY=0 NormalZ=1 AngleXU=0 Radius=16 StartAngle=5.60905 EndAngle=6.28319
    g17: LineSegment StartX=121 StartY=33 StartZ=0 EndX=121 EndY=19 EndZ=0
    g18: LineSegment StartX=124 StartY=38 StartZ=0 EndX=124 EndY=19 EndZ=0
    g19: LineSegment StartX=117.5 StartY=9.01251 StartZ=0 EndX=121.163 EndY=9.0125 EndZ=0
  constraints (46):
    c: Vertical(g0)
    c: Block(g0)
    c: Coincident(g1,g0)
    c: Block(g1)
    c: Coincident(g2,g1)
    c: Block(g2)
    c: Coincident(g3,g2)
    c: Horizontal(g3)
    c: Tangent(g3,g2)
    c: Coincident(g4,g0)
    c: Distance(g4) = 3
    c: Vertical(g4)
    c: Coincident(g5,g4)
    c: Horizontal(g5)
    c: Coincident(g6,g2)
    c: Coincident(g6,g5)
    c: Vertical(g6)
    c: Horizontal(g7)
    c: Distance(g7) = 105
    c: Coincident(g7,g1)
    c: Block(g3)
    c: Weight(g8) = 1
    c: Equal(g8,g9)
    c: Equal(g8,g10)
    c: InternalAlignment(g8,g11)
    c: InternalAlignment(g9,g11)
    c: InternalAlignment(g10,g11)
    c: InternalAlignment(g12,g11)
    c: InternalAlignment(g13,g11)
    c: Block(g11)
    c: Coincident(g14,g11)
    c: Coincident(g14,g3)
    c: Horizontal(g14)
    c: Block(g15)
    c: Coincident(g16,g15)
    c: Block(g16)
    c: Coincident(g17,g11)
    c: Coincident(g17,g16)
    c: Vertical(g17)
    c: Distance(g17) = 14
    c: Coincident(g18,g7)
    c: Coincident(g18,g15)
    c: Vertical(g18)
    c: Distance(g18) = 19
    c: Coincident(g19,g16)
    c: Coincident(g19,g15)
FEATURE [Sketcher::SketchObject] Sketch065
  FullyConstrained = true
  MapMode = 3
  Placement = pos=(0,0,0) rot=(1,0,0;1.5708rad)
  sketch-geometry (8):
    g0: Circle CenterX=80.351 CenterY=-67.6202 CenterZ=0 NormalX=0 NormalY=0 NormalZ=1 AngleXU=0 Radius=3
    g1: Circle CenterX=80.351 CenterY=-4.92017 CenterZ=0 NormalX=0 NormalY=0 NormalZ=1 AngleXU=0 Radius=3
    g2: Circle CenterX=23.851 CenterY=-4.92017 CenterZ=0 NormalX=0 NormalY=0 NormalZ=1 AngleXU=0 Radius=3
    g3: Circle CenterX=23.851 CenterY=-67.6202 CenterZ=0 NormalX=0 NormalY=0 NormalZ=1 AngleXU=0 Radius=3
    g4: Circle CenterX=23.851 CenterY=-67.6202 CenterZ=0 NormalX=0 NormalY=0 NormalZ=1 AngleXU=0 Radius=5
    g5: Circle CenterX=80.351 CenterY=-67.6202 CenterZ=0 NormalX=0 NormalY=0 NormalZ=1 AngleXU=0 Radius=5
    g6: Circle CenterX=23.851 CenterY=-4.92017 CenterZ=0 NormalX=0 NormalY=0 NormalZ=1 AngleXU=0 Radius=5
    g7: Circle CenterX=80.351 CenterY=-4.92017 CenterZ=0 NormalX=0 NormalY=0 NormalZ=1 AngleXU=0 Radius=5
  constraints (8):
    c: Block(g1)
    c: Block(g0)
    c: Block(g3)
    c: Block(g2)
    c: Block(g5)
    c: Block(g4)
    c: Block(g6)
    c: Block(g7)
FEATURE [Part::Extrusion] Extrude056
  Base = -> Sketch065
  Dir = (0,-1,2e-16)
  DirMode = 2
  FaceMakerClass = Part::FaceMakerBullseye
  LengthFwd = 2
  LengthRev = 0
  Solid = true
  Symmetric = false
FEATURE [Part::Extrusion] Extrude057  label="top025"
  Base = -> Sketch064
  Dir = (0,0,1)
  DirMode = 2
  FaceMakerClass = Part::FaceMakerBullseye
  LengthFwd = 72
  LengthRev = 0
  Solid = true
  Symmetric = false
FEATURE [Sketcher::SketchObject] Sketch066
  FullyConstrained = true
  MapMode = 3
  Placement = pos=(0,0,0) rot=(1,0,0;1.5708rad)
  Support = -> [Extrude057]
  sketch-geometry (8):
    g0: Circle CenterX=80.351 CenterY=-67.6202 CenterZ=0 NormalX=0 NormalY=0 NormalZ=1 AngleXU=0 Radius=3
    g1: Circle CenterX=80.351 CenterY=-4.92017 CenterZ=0 NormalX=0 NormalY=0 NormalZ=1 AngleXU=0 Radius=3
    g2: Circle CenterX=23.851 CenterY=-4.92017 CenterZ=0 NormalX=0 NormalY=0 NormalZ=1 AngleXU=0 Radius=3
    g3: Circle CenterX=23.851 CenterY=-67.6202 CenterZ=0 NormalX=0 NormalY=0 NormalZ=1 AngleXU=0 Radius=3
    g4: Circle CenterX=23.851 CenterY=-67.6202 CenterZ=0 NormalX=0 NormalY=0 NormalZ=1 AngleXU=0 Radius=5
    g5: Circle CenterX=80.351 CenterY=-67.6202 CenterZ=0 NormalX=0 NormalY=0 NormalZ=1 AngleXU=0 Radius=5
    g6: Circle CenterX=23.851 CenterY=-4.92017 CenterZ=0 NormalX=0 NormalY=0 NormalZ=1 AngleXU=0 Radius=5
    g7: Circle CenterX=80.351 CenterY=-4.92017 CenterZ=0 NormalX=0 NormalY=0 NormalZ=1 AngleXU=0 Radius=5
  constraints (8):
    c: Block(g1)
    c: Block(g0)
    c: Block(g3)
    c: Block(g2)
    c: Block(g5)
    c: Block(g4)
    c: Block(g6)
    c: Block(g7)
FEATURE [Part::Extrusion] Extrude055
  Base = -> Sketch066
  Dir = (0,-1,2e-16)
  DirMode = 2
  FaceMakerClass = Part::FaceMakerBullseye
  LengthFwd = 2
  LengthRev = 0
  Solid = true
  Symmetric = false
FEATURE [Part::Fillet] Fillet041
  Base = -> Extrude056
  Edges = 4 edges r=1.99: [Edge6,Edge12,Edge18,Edge24]
FEATURE [Part::Cut] Cut045
  Base = -> Extrude055
  Placement = pos=(0,6,0) rot=(0,0,1;0rad)
  Tool = -> Fillet041
FEATURE [Part::MultiFuse] Fusion095  label="pcbScrewPillars"
  Placement = pos=(-3.2,-1,72.3) rot=(0,0,1;0rad)
  Shapes = -> [Cut045,Extrude054]
FEATURE [Part::Feature] Face113
  shape: bbox 3.2 x 1.5 x 2e-07 mm, 1 faces, 0 solids (baked)
FEATURE [Part::Revolution] Revolve121  label="backCaseScrewRetainer002"
  Angle = 360
  Axis = (0,1,0)
  Base = (0,0,0)
  FaceMakerClass = Part::FaceMakerBullseye
  Placement = pos=(12.5,3,62) rot=(0,0,1;0rad)
  Solid = false
  Source = -> Face113
  Symmetric = false
FEATURE [Part::Feature] Face114
  shape: bbox 3.2 x 1.5 x 2e-07 mm, 1 faces, 0 solids (baked)
FEATURE [Part::Feature] Face115
  shape: bbox 3.2 x 1.5 x 2e-07 mm, 1 faces, 0 solids (baked)
FEATURE [Part::Feature] Face116
  shape: bbox 3.2 x 1.5 x 2e-07 mm, 1 faces, 0 solids (baked)
FEATURE [Part::Revolution] Revolve122  label="frontCaseScrewRetainer004"
  Angle = 360
  Axis = (0,1,0)
  Base = (0,0,0)
  FaceMakerClass = Part::FaceMakerBullseye
  Placement = pos=(89.5,3,68.5) rot=(0,0,1;0rad)
  Solid = false
  Source = -> Face115
  Symmetric = false
FEATURE [Part::Revolution] Revolve123  label="frontCaseScrewRetainer005"
  Angle = 360
  Axis = (0,1,0)
  Base = (0,0,0)
  FaceMakerClass = Part::FaceMakerBullseye
  Placement = pos=(89.5,3,3.5) rot=(0,0,1;0rad)
  Solid = false
  Source = -> Face116
  Symmetric = false
FEATURE [Part::Revolution] Revolve124  label="backCaseScrewRetainer003"
  Angle = 360
  Axis = (0,1,0)
  Base = (0,0,0)
  FaceMakerClass = Part::FaceMakerBullseye
  Placement = pos=(12.5,3,10) rot=(0,0,1;0rad)
  Solid = false
  Source = -> Face114
  Symmetric = false
FEATURE [Part::Feature] Face117
  shape: bbox 3.6 x 3.2 x 2e-07 mm, 1 faces, 0 solids (baked)
FEATURE [Part::Revolution] Revolve125  label="moreFrontCaseScrewRetainer004"
  Angle = 360
  Axis = (0,1,0)
  Base = (0,0,0)
  FaceMakerClass = Part::FaceMakerBullseye
  Placement = pos=(109.5,4.5,68.5) rot=(0,0,1;0rad)
  Solid = false
  Source = -> Face117
  Symmetric = false
FEATURE [Part::Feature] Face118
  shape: bbox 3.6 x 3.2 x 2e-07 mm, 1 faces, 0 solids (baked)
FEATURE [Part::Revolution] Revolve126  label="moreFrontCaseScrewRetainer005"
  Angle = 360
  Axis = (0,1,0)
  Base = (0,0,0)
  FaceMakerClass = Part::FaceMakerBullseye
  Placement = pos=(109.5,4.5,3.5) rot=(0,0,1;0rad)
  Solid = false
  Source = -> Face118
  Symmetric = false
FEATURE [Part::MultiFuse] Fusion096  label="screwRetainers001"
  Shapes = -> [Revolve126,Revolve125,Revolve124,Revolve123,Revolve122,Revolve121]
FEATURE [Part::Feature] Face119
  shape: bbox 10 x 16.5 x 2e-07 mm, 1 faces, 0 solids (baked)
FEATURE [Part::Revolution] Revolve130  label="plugHousing050"
  Angle = 360
  Axis = (0,1,0)
  Base = (0,0,0)
  FaceMakerClass = Part::FaceMakerBullseye
  Placement = pos=(0,0,36.15) rot=(0,0,1;0rad)
  Solid = false
  Source = -> Face119
  Symmetric = false
FEATURE [Part::Feature] Face120
  shape: bbox 10 x 16.5 x 2e-07 mm, 1 faces, 0 solids (baked)
FEATURE [Part::Feature] Face121
  shape: bbox 10 x 16.5 x 2e-07 mm, 1 faces, 0 solids (baked)
FEATURE [Part::Revolution] Revolve127  label="plugHousing047"
  Angle = 360
  Axis = (0,1,0)
  Base = (0,0,0)
  FaceMakerClass = Part::FaceMakerBullseye
  Placement = pos=(0,0,36.15) rot=(0,0,1;0rad)
  Solid = false
  Source = -> Face121
  Symmetric = false
FEATURE [Part::Feature] Face122
  shape: bbox 10 x 16.5 x 2e-07 mm, 1 faces, 0 solids (baked)
FEATURE [Part::Feature] Face123
  shape: bbox 10 x 16.5 x 2e-07 mm, 1 faces, 0 solids (baked)
FEATURE [Part::Revolution] Revolve128  label="plugHousing048"
  Angle = 360
  Axis = (0,1,0)
  Base = (0,0,0)
  FaceMakerClass = Part::FaceMakerBullseye
  Placement = pos=(0,0,36.15) rot=(0,0,1;0rad)
  Solid = false
  Source = -> Face123
  Symmetric = false
FEATURE [Part::MultiFuse] Fusion100  label="plugHousing054"
  Placement = pos=(0,0,0) rot=(0,0,1;1.5708rad)
  Shapes = -> [Revolve130,Revolve128]
FEATURE [Part::Feature] Face124
  shape: bbox 10 x 16.5 x 2e-07 mm, 1 faces, 0 solids (baked)
FEATURE [Part::Feature] Face125
  shape: bbox 10 x 16.5 x 2e-07 mm, 1 faces, 0 solids (baked)
FEATURE [Part::Revolution] Revolve129  label="plugHousing049"
  Angle = 360
  Axis = (0,1,0)
  Base = (0,0,0)
  FaceMakerClass = Part::FaceMakerBullseye
  Placement = pos=(0,0,36.15) rot=(0,0,1;0rad)
  Solid = false
  Source = -> Face125
  Symmetric = false
FEATURE [Part::Feature] Face126
  shape: bbox 10 x 16.5 x 2e-07 mm, 1 faces, 0 solids (baked)
FEATURE [Part::Revolution] Revolve131  label="plugHousing058"
  Angle = 360
  Axis = (0,1,0)
  Base = (0,0,0)
  FaceMakerClass = Part::FaceMakerBullseye
  Placement = pos=(0,0,36.15) rot=(0,0,1;0rad)
  Solid = false
  Source = -> Face120
  Symmetric = false
FEATURE [Part::MultiFuse] Fusion099  label="plugHousing053"
  Placement = pos=(0,0,0) rot=(0,0,1;1.5708rad)
  Shapes = -> [Revolve127,Revolve131]
FEATURE [Part::MultiFuse] Fusion102  label="plugHousing056"
  Placement = pos=(0,19,0) rot=(0,0,1;3.14159rad)
  Shapes = -> [Fusion100,Fusion099]
FEATURE [Part::Revolution] Revolve132  label="plugHousing059"
  Angle = 360
  Axis = (0,1,0)
  Base = (0,0,0)
  FaceMakerClass = Part::FaceMakerBullseye
  Placement = pos=(0,0,36.15) rot=(0,0,1;0rad)
  Solid = false
  Source = -> Face126
  Symmetric = false
FEATURE [Part::Revolution] Revolve133  label="plugHousing060"
  Angle = 360
  Axis = (0,1,0)
  Base = (0,0,0)
  FaceMakerClass = Part::FaceMakerBullseye
  Placement = pos=(0,0,36.15) rot=(0,0,1;0rad)
  Solid = false
  Source = -> Face122
  Symmetric = false
FEATURE [Part::MultiFuse] Fusion097  label="plugHousing051"
  Placement = pos=(0,0,0) rot=(0,0,1;1.5708rad)
  Shapes = -> [Revolve133,Revolve132]
FEATURE [Part::Revolution] Revolve134  label="plugHousing061"
  Angle = 360
  Axis = (0,1,0)
  Base = (0,0,0)
  FaceMakerClass = Part::FaceMakerBullseye
  Placement = pos=(0,0,36.15) rot=(0,0,1;0rad)
  Solid = false
  Source = -> Face124
  Symmetric = false
FEATURE [Part::MultiFuse] Fusion101  label="plugHousing055"
  Placement = pos=(0,0,0) rot=(0,0,1;1.5708rad)
  Shapes = -> [Revolve129,Revolve134]
FEATURE [Part::MultiFuse] Fusion098  label="plugHousing052"
  Placement = pos=(0,19,0) rot=(0,0,1;3.14159rad)
  Shapes = -> [Fusion097,Fusion101]
FEATURE [Part::MultiFuse] Fusion103  label="plugHousing057"
  Placement = pos=(122.621,0,-0.15) rot=(0,0,1;0rad)
  Shapes = -> [Fusion102,Fusion098]
FEATURE [Part::Box] Box028  label="Cube015"
  AttacherType = Attacher::AttachEngine3D
  Height = 28
  Length = 3
  Placement = pos=(110.7,19,22) rot=(0,0,1;0rad)
  Width = 15.7
FEATURE [Part::Cylinder] Cylinder044
  Angle = 360
  AttacherType = Attacher::AttachEngine3D
  Height = 20
  Placement = pos=(0,0,36.15) rot=(0,0,1;0rad)
  Radius = 10.3
FEATURE [Part::Cylinder] Cylinder045
  Angle = 360
  AttacherType = Attacher::AttachEngine3D
  Height = 10
  Placement = pos=(0,0,36.15) rot=(0,0,1;0rad)
  Radius = 4
FEATURE [Part::MultiFuse] Fusion104  label="removeToCreteHoleForPlugHousing040"
  Placement = pos=(70,19,36) rot=(0,1,0;1.5708rad)
  Shapes = -> [Cylinder044,Cylinder045]
FEATURE [Part::Cut] Cut046  label="plugHousingTab003"
  Base = -> Box028
  Tool = -> Fusion104
FEATURE [Part::MultiFuse] Fusion105  label="plugHousing062"
  Shapes = -> [Fusion103,Cut046]
FEATURE [Part::Fillet] Fillet042
  Base = -> Fusion105
  Edges = 1 edges r=2: [Edge25]
FEATURE [Part::Fillet] Fillet043  label="plugHousing063"
  Base = -> Fillet042
  Edges = 1 edges r=2: [Edge8]
  Placement = pos=(7,0,0) rot=(0,0,1;0rad)
FEATURE [Part::Feature] Face127
  shape: bbox 10 x 16.5 x 2e-07 mm, 1 faces, 0 solids (baked)
FEATURE [Part::Feature] Face128
  shape: bbox 10 x 16.5 x 2e-07 mm, 1 faces, 0 solids (baked)
FEATURE [Part::Revolution] Revolve137  label="plugHousing070"
  Angle = 360
  Axis = (0,1,0)
  Base = (0,0,0)
  FaceMakerClass = Part::FaceMakerBullseye
  Placement = pos=(0,0,36.15) rot=(0,0,1;0rad)
  Solid = false
  Source = -> Face127
  Symmetric = false
FEATURE [Part::Revolution] Revolve140  label="plugHousing073"
  Angle = 360
  Axis = (0,1,0)
  Base = (0,0,0)
  FaceMakerClass = Part::FaceMakerBullseye
  Placement = pos=(0,0,36.15) rot=(0,0,1;0rad)
  Solid = false
  Source = -> Face128
  Symmetric = false
FEATURE [Part::Feature] Face129
  shape: bbox 10 x 16.5 x 2e-07 mm, 1 faces, 0 solids (baked)
FEATURE [Part::Revolution] Revolve138  label="plugHousing071"
  Angle = 360
  Axis = (0,1,0)
  Base = (0,0,0)
  FaceMakerClass = Part::FaceMakerBullseye
  Placement = pos=(0,0,36.15) rot=(0,0,1;0rad)
  Solid = false
  Source = -> Face129
  Symmetric = false
FEATURE [Part::Feature] Face130
  shape: bbox 10 x 16.5 x 2e-07 mm, 1 faces, 0 solids (baked)
FEATURE [Part::Revolution] Revolve139  label="plugHousing072"
  Angle = 360
  Axis = (0,1,0)
  Base = (0,0,0)
  FaceMakerClass = Part::FaceMakerBullseye
  Placement = pos=(0,0,36.15) rot=(0,0,1;0rad)
  Solid = false
  Source = -> Face130
  Symmetric = false
FEATURE [Part::Feature] Face131
  shape: bbox 10 x 16.5 x 2e-07 mm, 1 faces, 0 solids (baked)
FEATURE [Part::Revolution] Revolve135  label="plugHousing068"
  Angle = 360
  Axis = (0,1,0)
  Base = (0,0,0)
  FaceMakerClass = Part::FaceMakerBullseye
  Placement = pos=(0,0,36.15) rot=(0,0,1;0rad)
  Solid = false
  Source = -> Face131
  Symmetric = false
FEATURE [Part::MultiFuse] Fusion112  label="plugHousing078"
  Placement = pos=(0,0,0) rot=(0,0,1;1.5708rad)
  Shapes = -> [Revolve135,Revolve139]
FEATURE [Part::Feature] Face132
  shape: bbox 10 x 16.5 x 2e-07 mm, 1 faces, 0 solids (baked)
FEATURE [Part::Revolution] Revolve141  label="plugHousing074"
  Angle = 360
  Axis = (0,1,0)
  Base = (0,0,0)
  FaceMakerClass = Part::FaceMakerBullseye
  Placement = pos=(0,0,36.15) rot=(0,0,1;0rad)
  Solid = false
  Source = -> Face132
  Symmetric = false
FEATURE [Part::MultiFuse] Fusion110  label="plugHousing076"
  Placement = pos=(0,0,0) rot=(0,0,1;1.5708rad)
  Shapes = -> [Revolve141,Revolve140]
FEATURE [Part::Feature] Face133
  shape: bbox 10 x 16.5 x 2e-07 mm, 1 faces, 0 solids (baked)
FEATURE [Part::Revolution] Revolve136  label="plugHousing069"
  Angle = 360
  Axis = (0,1,0)
  Base = (0,0,0)
  FaceMakerClass = Part::FaceMakerBullseye
  Placement = pos=(0,0,36.15) rot=(0,0,1;0rad)
  Solid = false
  Source = -> Face133
  Symmetric = false
FEATURE [Part::MultiFuse] Fusion106  label="plugHousing064"
  Placement = pos=(0,0,0) rot=(0,0,1;1.5708rad)
  Shapes = -> [Revolve138,Revolve136]
FEATURE [Part::MultiFuse] Fusion108  label="plugHousing066"
  Placement = pos=(0,19,0) rot=(0,0,1;3.14159rad)
  Shapes = -> [Fusion106,Fusion112]
FEATURE [Part::Feature] Face134
  shape: bbox 10 x 16.5 x 2e-07 mm, 1 faces, 0 solids (baked)
FEATURE [Part::Revolution] Revolve142  label="plugHousing075"
  Angle = 360
  Axis = (0,1,0)
  Base = (0,0,0)
  FaceMakerClass = Part::FaceMakerBullseye
  Placement = pos=(0,0,36.15) rot=(0,0,1;0rad)
  Solid = false
  Source = -> Face134
  Symmetric = false
FEATURE [Part::MultiFuse] Fusion107  label="plugHousing065"
  Placement = pos=(0,0,0) rot=(0,0,1;1.5708rad)
  Shapes = -> [Revolve137,Revolve142]
FEATURE [Part::MultiFuse] Fusion111  label="plugHousing077"
  Placement = pos=(0,19,0) rot=(0,0,1;3.14159rad)
  Shapes = -> [Fusion110,Fusion107]
FEATURE [Part::MultiFuse] Fusion109  label="plugHousing067"
  Placement = pos=(131.236,0,-0.15) rot=(0,0,1;0rad)
  Shapes = -> [Fusion108,Fusion111]
FEATURE [Part::MultiFuse] Fusion113  label="plugHousing079"
  Shapes = -> [Fillet043,Fusion109]
FEATURE [Part::Feature] Face135
  shape: bbox 3.5 x 17.8 x 2e-07 mm, 1 faces, 0 solids (baked)
FEATURE [Part::Revolution] Revolve143  label="removeToCreateScrewAndThreadedInsertHole049"
  Angle = 360
  Axis = (0,1,0)
  Base = (0,0,0)
  FaceMakerClass = Part::FaceMakerBullseye
  Placement = pos=(12.5,0,10) rot=(0,0,1;0rad)
  Solid = false
  Source = -> Face135
  Symmetric = false
FEATURE [Part::Feature] Face136
  shape: bbox 3.5 x 17.8 x 2e-07 mm, 1 faces, 0 solids (baked)
FEATURE [Part::Revolution] Revolve144  label="removeToCreateScrewAndThreadedInsertHole050"
  Angle = 360
  Axis = (0,1,0)
  Base = (0,0,0)
  FaceMakerClass = Part::FaceMakerBullseye
  Placement = pos=(12.5,0,62) rot=(0,0,1;0rad)
  Solid = false
  Source = -> Face136
  Symmetric = false
FEATURE [Part::Feature] Face137
  shape: bbox 3.5 x 17.8 x 2e-07 mm, 1 faces, 0 solids (baked)
FEATURE [Part::Revolution] Revolve145  label="removeToCreateScrewAndThreadedInsertHole051"
  Angle = 360
  Axis = (0,1,0)
  Base = (0,0,0)
  FaceMakerClass = Part::FaceMakerBullseye
  Placement = pos=(89.5,0,68.5) rot=(0,0,1;0rad)
  Solid = false
  Source = -> Face137
  Symmetric = false
FEATURE [Part::Feature] Face138
  shape: bbox 3.5 x 17.8 x 2e-07 mm, 1 faces, 0 solids (baked)
FEATURE [Part::Revolution] Revolve146  label="removeToCreateScrewAndThreadedInsertHole052"
  Angle = 360
  Axis = (0,1,0)
  Base = (0,0,0)
  FaceMakerClass = Part::FaceMakerBullseye
  Placement = pos=(89.5,0,3.5) rot=(0,0,1;0rad)
  Solid = false
  Source = -> Face138
  Symmetric = false
FEATURE [Part::Feature] Face139
  shape: bbox 3.5 x 17.8 x 2e-07 mm, 1 faces, 0 solids (baked)
FEATURE [Part::Revolution] Revolve147  label="removeToCreateScrewAndThreadedInsertHole053"
  Angle = 360
  Axis = (0,1,0)
  Base = (0,0,0)
  FaceMakerClass = Part::FaceMakerBullseye
  Placement = pos=(109.5,4.7,3.5) rot=(0,0,1;0rad)
  Solid = false
  Source = -> Face139
  Symmetric = false
FEATURE [Part::Feature] Face140
  shape: bbox 3.5 x 17.8 x 2e-07 mm, 1 faces, 0 solids (baked)
FEATURE [Part::Revolution] Revolve148  label="removeToCreateScrewAndThreadedInsertHole054"
  Angle = 360
  Axis = (0,1,0)
  Base = (0,0,0)
  FaceMakerClass = Part::FaceMakerBullseye
  Placement = pos=(109.5,4.7,68.5) rot=(0,0,1;0rad)
  Solid = false
  Source = -> Face140
  Symmetric = false
FEATURE [Part::MultiFuse] Fusion114  label="removeToCreateScrewAndThreadedInsertHole055"
  Shapes = -> [Revolve148,Revolve147,Revolve146,Revolve145,Revolve144,Revolve143]
FEATURE [Part::Cut] Cut047  label="casePillars004"
  Base = -> Cut037
  Tool = -> Fusion114
FEATURE [Part::Feature] Face141
  shape: bbox 3.5 x 17.8 x 2e-07 mm, 1 faces, 0 solids (baked)
FEATURE [Part::Feature] Face142
  shape: bbox 3.5 x 17.8 x 2e-07 mm, 1 faces, 0 solids (baked)
FEATURE [Part::Feature] Face143
  shape: bbox 3.5 x 17.8 x 2e-07 mm, 1 faces, 0 solids (baked)
FEATURE [Part::Revolution] Revolve149  label="removeToCreateScrewAndThreadedInsertHole057"
  Angle = 360
  Axis = (0,1,0)
  Base = (0,0,0)
  FaceMakerClass = Part::FaceMakerBullseye
  Placement = pos=(12.5,0,10) rot=(0,0,1;0rad)
  Solid = false
  Source = -> Face141
  Symmetric = false
FEATURE [Part::Feature] Face144
  shape: bbox 3.5 x 17.8 x 2e-07 mm, 1 faces, 0 solids (baked)
FEATURE [Part::Feature] Face145
  shape: bbox 3.5 x 17.8 x 2e-07 mm, 1 faces, 0 solids (baked)
FEATURE [Part::Feature] Face146
  shape: bbox 3.5 x 17.8 x 2e-07 mm, 1 faces, 0 solids (baked)
FEATURE [Part::Revolution] Revolve150  label="removeToCreateScrewAndThreadedInsertHole058"
  Angle = 360
  Axis = (0,1,0)
  Base = (0,0,0)
  FaceMakerClass = Part::FaceMakerBullseye
  Placement = pos=(12.5,0,62) rot=(0,0,1;0rad)
  Solid = false
  Source = -> Face146
  Symmetric = false
FEATURE [Part::Revolution] Revolve151  label="removeToCreateScrewAndThreadedInsertHole059"
  Angle = 360
  Axis = (0,1,0)
  Base = (0,0,0)
  FaceMakerClass = Part::FaceMakerBullseye
  Placement = pos=(89.5,0,68.5) rot=(0,0,1;0rad)
  Solid = false
  Source = -> Face143
  Symmetric = false
FEATURE [Part::Revolution] Revolve152  label="removeToCreateScrewAndThreadedInsertHole060"
  Angle = 360
  Axis = (0,1,0)
  Base = (0,0,0)
  FaceMakerClass = Part::FaceMakerBullseye
  Placement = pos=(89.5,0,3.5) rot=(0,0,1;0rad)
  Solid = false
  Source = -> Face142
  Symmetric = false
FEATURE [Part::Revolution] Revolve153  label="removeToCreateScrewAndThreadedInsertHole061"
  Angle = 360
  Axis = (0,1,0)
  Base = (0,0,0)
  FaceMakerClass = Part::FaceMakerBullseye
  Placement = pos=(109.5,4.7,3.5) rot=(0,0,1;0rad)
  Solid = false
  Source = -> Face145
  Symmetric = false
FEATURE [Part::Revolution] Revolve154  label="removeToCreateScrewAndThreadedInsertHole062"
  Angle = 360
  Axis = (0,1,0)
  Base = (0,0,0)
  FaceMakerClass = Part::FaceMakerBullseye
  Placement = pos=(109.5,4.7,68.5) rot=(0,0,1;0rad)
  Solid = false
  Source = -> Face144
  Symmetric = false
FEATURE [Part::MultiFuse] Fusion115  label="removeToCreateScrewAndThreadedInsertHole056"
  Shapes = -> [Revolve154,Revolve153,Revolve152,Revolve151,Revolve150,Revolve149]
FEATURE [Part::Feature] Face147
  shape: bbox 9.8 x 26.5 x 2e-07 mm, 1 faces, 0 solids (baked)
FEATURE [Part::Revolution] Revolve155
  Angle = 360
  Axis = (0,1,0)
  Base = (0,0,0)
  FaceMakerClass = Part::FaceMakerBullseye
  Placement = pos=(0,0,0) rot=(0,0,1;1.5708rad)
  Solid = false
  Source = -> Face147
  Symmetric = false
FEATURE [Part::Feature] Face148
  shape: bbox 9.8 x 26.5 x 2e-07 mm, 1 faces, 0 solids (baked)
FEATURE [Part::Revolution] Revolve156
  Angle = 360
  Axis = (0,1,0)
  Base = (0,0,0)
  FaceMakerClass = Part::FaceMakerBullseye
  Placement = pos=(0,0,0) rot=(0,0,1;1.5708rad)
  Solid = false
  Source = -> Face148
  Symmetric = false
FEATURE [Part::MultiFuse] Fusion116
  Placement = pos=(-18,19,36) rot=(0,0,1;0rad)
  Shapes = -> [Revolve156,Revolve155]
FEATURE [Part::Box] Box029  label="Cube016"
  AttacherType = Attacher::AttachEngine3D
  Height = 28
  Length = 3
  Placement = pos=(110.7,19,22) rot=(0,0,1;0rad)
  Width = 15.7
FEATURE [Part::Cylinder] Cylinder046
  Angle = 360
  AttacherType = Attacher::AttachEngine3D
  Height = 10
  Placement = pos=(0,0,36.15) rot=(0,0,1;0rad)
  Radius = 4
FEATURE [Part::Cylinder] Cylinder047
  Angle = 360
  AttacherType = Attacher::AttachEngine3D
  Height = 20
  Placement = pos=(0,0,36.15) rot=(0,0,1;0rad)
  Radius = 10.3
FEATURE [Part::MultiFuse] Fusion117  label="removeToCreteHoleForPlugHousing041"
  Placement = pos=(70,19,36) rot=(0,1,0;1.5708rad)
  Shapes = -> [Cylinder047,Cylinder046]
FEATURE [Part::Cut] Cut049  label="plugHousingTab004"
  Base = -> Box029
  Placement = pos=(-107.4,-14,0) rot=(0,0,1;0rad)
  Tool = -> Fusion117
FEATURE [Part::Box] Box030  label="Cube017"
  AttacherType = Attacher::AttachEngine3D
  Height = 28
  Length = 3
  Placement = pos=(110.7,19,22) rot=(0,0,1;0rad)
  Width = 15.7
FEATURE [Part::Cylinder] Cylinder048
  Angle = 360
  AttacherType = Attacher::AttachEngine3D
  Height = 10
  Placement = pos=(0,0,36.15) rot=(0,0,1;0rad)
  Radius = 4
FEATURE [Part::Cylinder] Cylinder049
  Angle = 360
  AttacherType = Attacher::AttachEngine3D
  Height = 20
  Placement = pos=(0,0,36.15) rot=(0,0,1;0rad)
  Radius = 10.3
FEATURE [Part::MultiFuse] Fusion118  label="removeToCreteHoleForPlugHousing042"
  Placement = pos=(70,19,36) rot=(0,1,0;1.5708rad)
  Shapes = -> [Cylinder049,Cylinder048]
FEATURE [Part::Cut] Cut050  label="plugHousingTab005"
  Base = -> Box030
  Placement = pos=(-107.4,-14,0) rot=(0,0,1;0rad)
  Tool = -> Fusion118
FEATURE [Part::MultiFuse] Fusion119
  Placement = pos=(9.6,23,0) rot=(0,0,1;3.14159rad)
  Shapes = -> [Cut049,Cut050]
FEATURE [Part::Box] Box031  label="Cube018"
  AttacherType = Attacher::AttachEngine3D
  Height = 10
  Length = 3
  Placement = pos=(3.3,4,12) rot=(0,0,1;0rad)
  Width = 10
FEATURE [Part::Fillet] Fillet044
  Base = -> Box031
  Edges = 1 edges r=2: [Edge11]
FEATURE [Part::Box] Box032  label="Cube019"
  AttacherType = Attacher::AttachEngine3D
  Height = 10
  Length = 3
  Placement = pos=(3.3,4,50) rot=(0,0,1;0rad)
  Width = 10
FEATURE [Part::Fillet] Fillet045
  Base = -> Box032
  Edges = 1 edges r=2: [Edge12]
FEATURE [Part::Box] Box033  label="Cube020"
  AttacherType = Attacher::AttachEngine3D
  Height = 28
  Length = 4
  Placement = pos=(5,0,22) rot=(0,0,1;0rad)
  Width = 10
FEATURE [Part::Fillet] Fillet046
  Base = -> Box033
  Edges = 1 edges r=1: [Edge7]
FEATURE [Part::Fillet] Fillet047
  Base = -> Fillet046
  Edges = 1 edges r=2: [Edge5]
FEATURE [Part::Fillet] Fillet048
  Base = -> Fillet047
  Edges = 1 edges r=2: [Edge2]
FEATURE [Part::Cylinder] Cylinder050
  Angle = 360
  AttacherType = Attacher::AttachEngine3D
  Height = 20
  Placement = pos=(0,0,36.15) rot=(0,0,1;0rad)
  Radius = 8.2
FEATURE [Part::Cylinder] Cylinder051
  Angle = 360
  AttacherType = Attacher::AttachEngine3D
  Height = 10
  Placement = pos=(0,0,36.15) rot=(0,0,1;0rad)
  Radius = 4
FEATURE [Part::MultiFuse] Fusion120  label="removeToCreteHoleForPlugHousing043"
  Placement = pos=(-42,19,36) rot=(0,1,0;1.5708rad)
  Shapes = -> [Cylinder050,Cylinder051]
FEATURE [Sketcher::SketchObject] Sketch067  label="topSketch018"
  FullyConstrained = true
  sketch-geometry (4):
    g0: LineSegment StartX=16.8446 StartY=31.512 StartZ=0 EndX=16.3251 EndY=34.4666 EndZ=0
    g1: ArcOfCircle CenterX=19 CenterY=19.2524 CenterZ=0 NormalX=0 NormalY=0 NormalZ=1 AngleXU=0 Radius=15.4476 StartAngle=1.74483 EndAngle=2.72717
    g2: ArcOfCircle CenterX=19 CenterY=19.2524 CenterZ=0 NormalX=0 NormalY=0 NormalZ=1 AngleXU=0 Radius=12.4476 StartAngle=1.74483 EndAngle=2.73189
    g3: LineSegment StartX=4.86004 StartY=25.4725 StartZ=0 EndX=7.58253 EndY=24.2107 EndZ=0
  constraints (7):
    c: Block(g0)
    c: Coincident(g1,g0)
    c: Coincident(g2,g0)
    c: Coincident(g3,g1)
    c: Coincident(g3,g2)
    c: Block(g1)
    c: Block(g2)
FEATURE [Part::Extrusion] Extrude058
  Base = -> Sketch067
  Dir = (0,0,1)
  DirMode = 2
  FaceMakerClass = Part::FaceMakerBullseye
  LengthFwd = 10
  LengthRev = 0
  Placement = pos=(0,0,31) rot=(0,0,1;0rad)
  Solid = true
  Symmetric = false
FEATURE [Part::Cut] Cut051
  Base = -> Extrude058
  Tool = -> Fusion120
FEATURE [Part::Fillet] Fillet049
  Base = -> Cut051
  Edges = 1 edges r=2: [Edge1]
FEATURE [Part::Fillet] Fillet050
  Base = -> Fillet049
  Edges = 1 edges r=2.5: [Edge1]
FEATURE [Part::Fillet] Fillet051
  Base = -> Fillet050
  Edges = 1 edges r=2.5: [Edge2]
FEATURE [Part::MultiFuse] Fusion121  label="wireHolder003"
  Shapes = -> [Fusion116,Fillet051]
FEATURE [Part::MultiFuse] Fusion122
  Shapes = -> [Fillet045,Fusion121]
FEATURE [Part::MultiFuse] Fusion123  label="wireHolder004"
  Shapes = -> [Fusion122,Fillet048]
FEATURE [Part::MultiFuse] Fusion124  label="wireHolder005"
  Shapes = -> [Fillet044,Fusion119,Fusion123]
FEATURE [Sketcher::SketchObject] Sketch068  label="topSketch019"
  FullyConstrained = true
  sketch-geometry (6):
    g0: LineSegment StartX=19 StartY=38 StartZ=0 EndX=117 EndY=38 EndZ=0
    g1: ArcOfCircle CenterX=19 CenterY=19 CenterZ=0 NormalX=0 NormalY=0 NormalZ=1 AngleXU=0 Radius=19 StartAngle=1.5708 EndAngle=3.14159
    g2: LineSegment StartX=117 StartY=38 StartZ=0 EndX=117 EndY=19 EndZ=0
    g3: LineSegment StartX=98 StartY=1.0161e-12 StartZ=0 EndX=5.22862e-06 EndY=1.0161e-12 EndZ=0
    g4: LineSegment StartX=5.22862e-06 StartY=19 StartZ=0 EndX=5.22862e-06 EndY=1.0161e-12 EndZ=0
    g5: ArcOfCircle CenterX=98 CenterY=19 CenterZ=0 NormalX=0 NormalY=0 NormalZ=1 AngleXU=0 Radius=19 StartAngle=4.71239 EndAngle=6.28319
  constraints (16):
    c: Horizontal(g0)
    c: Distance(g0) = 98
    c: Coincident(g1,g0)
    c: Block(g1)
    c: Coincident(g2,g0)
    c: Vertical(g2)
    c: Distance(g2) = 19
    c: Horizontal(g3)
    c: Coincident(g4,g1)
    c: Vertical(g4)
    c: Coincident(g3,g4)
    c: Block(g3)
    c: Coincident(g5,g2)
    c: Coincident(g5,g3)
    c: Block(g0)
    c: Block(g5)
FEATURE [Part::Extrusion] Extrude059  label="sideA002"
  Base = -> Sketch068
  Dir = (0,0,1)
  DirMode = 2
  FaceMakerClass = Part::FaceMakerBullseye
  LengthFwd = 3
  LengthRev = 0
  Placement = pos=(0,0,-2.7) rot=(0,0,1;0rad)
  Solid = true
  Symmetric = false
FEATURE [Sketcher::SketchObject] Sketch069  label="topSketch020"
  FullyConstrained = true
  sketch-geometry (6):
    g0: LineSegment StartX=19 StartY=38 StartZ=0 EndX=117 EndY=38 EndZ=0
    g1: ArcOfCircle CenterX=19 CenterY=19 CenterZ=0 NormalX=0 NormalY=0 NormalZ=1 AngleXU=0 Radius=19 StartAngle=1.5708 EndAngle=3.14159
    g2: LineSegment StartX=117 StartY=38 StartZ=0 EndX=117 EndY=19 EndZ=0
    g3: LineSegment StartX=98 StartY=1.0161e-12 StartZ=0 EndX=5.22862e-06 EndY=1.0161e-12 EndZ=0
    g4: LineSegment StartX=5.22862e-06 StartY=19 StartZ=0 EndX=5.22862e-06 EndY=1.0161e-12 EndZ=0
    g5: ArcOfCircle CenterX=98 CenterY=19 CenterZ=0 NormalX=0 NormalY=0 NormalZ=1 AngleXU=0 Radius=19 StartAngle=4.71239 EndAngle=6.28319
  constraints (16):
    c: Horizontal(g0)
    c: Distance(g0) = 98
    c: Coincident(g1,g0)
    c: Block(g1)
    c: Coincident(g2,g0)
    c: Vertical(g2)
    c: Distance(g2) = 19
    c: Horizontal(g3)
    c: Coincident(g4,g1)
    c: Vertical(g4)
    c: Coincident(g3,g4)
    c: Block(g3)
    c: Coincident(g5,g2)
    c: Coincident(g5,g3)
    c: Block(g0)
    c: Block(g5)
FEATURE [Part::Extrusion] Extrude060  label="sideB002"
  Base = -> Sketch069
  Dir = (0,0,1)
  DirMode = 2
  FaceMakerClass = Part::FaceMakerBullseye
  LengthFwd = 3
  LengthRev = 0
  Placement = pos=(0,0,71.7) rot=(0,0,1;0rad)
  Solid = true
  Symmetric = false
FEATURE [Part::MultiFuse] Fusion127  label="removeFromBottom001"
  Placement = pos=(2,0,0) rot=(0,0,1;0rad)
  Shapes = -> [Extrude059,Extrude060]
FEATURE [Part::Cylinder] Cylinder052
  Angle = 360
  AttacherType = Attacher::AttachEngine3D
  Height = 20
  Placement = pos=(0,0,36.15) rot=(0,0,1;0rad)
  Radius = 14
FEATURE [Part::Cylinder] Cylinder053
  Angle = 360
  AttacherType = Attacher::AttachEngine3D
  Height = 10
  Placement = pos=(0,0,36.15) rot=(0,0,1;0rad)
  Radius = 4
FEATURE [Part::MultiFuse] Fusion128  label="removeToCreteHoleForPlugHousing044"
  Placement = pos=(70,19,36) rot=(0,1,0;1.5708rad)
  Shapes = -> [Cylinder052,Cylinder053]
FEATURE [Part::Cut] Cut052  label="bottom011"
  Base = -> Extrude043
  Tool = -> Fusion128
FEATURE [Part::Cut] Cut054  label="bottom012"
  Base = -> Cut052
  Tool = -> Fusion115
FEATURE [Sketcher::SketchObject] Sketch070
  FullyConstrained = true
  Placement = pos=(117,19,0) rot=(0.57735,0.57735,0.57735;2.0944rad)
  sketch-geometry (48):
    g0: LineSegment StartX=-49.19 StartY=69.25 StartZ=0 EndX=-49.19 EndY=66.25 EndZ=0
    g1: LineSegment StartX=-49.19 StartY=63.5 StartZ=0 EndX=-49.19 EndY=60.5 EndZ=0
    g2: LineSegment StartX=-49.19 StartY=57.75 StartZ=0 EndX=-49.19 EndY=54.75 EndZ=0
    g3: LineSegment StartX=-49.19 StartY=52 StartZ=0 EndX=-49.19 EndY=49 EndZ=0
    g4: LineSegment StartX=-49.19 StartY=46.25 StartZ=0 EndX=-49.19 EndY=43.25 EndZ=0
    g5: LineSegment StartX=-49.19 StartY=40.5 StartZ=0 EndX=-49.19 EndY=37.5 EndZ=0
    g6: LineSegment StartX=-49.19 StartY=34.5 StartZ=0 EndX=-49.19 EndY=31.5 EndZ=0
    g7: LineSegment StartX=-49.19 StartY=28.75 StartZ=0 EndX=-49.19 EndY=25.75 EndZ=0
    g8: LineSegment StartX=-49.19 StartY=23 StartZ=0 EndX=-49.19 EndY=20 EndZ=0
    g9: LineSegment StartX=-49.19 StartY=17.25 StartZ=0 EndX=-49.19 EndY=14.25 EndZ=0
    g10: LineSegment StartX=-49.19 StartY=11.5 StartZ=0 EndX=-49.19 EndY=8.5 EndZ=0
    g11: LineSegment StartX=-49.19 StartY=5.75 StartZ=0 EndX=-49.19 EndY=2.75 EndZ=0
    g12: ArcOfCircle CenterX=-1.5 CenterY=67.75 CenterZ=0 NormalX=0 NormalY=0 NormalZ=1 AngleXU=0 Radius=1.5 StartAngle=4.71239 EndAngle=7.85398
    g13: ArcOfCircle CenterX=-1.5 CenterY=62 CenterZ=0 NormalX=0 NormalY=0 NormalZ=1 AngleXU=0 Radius=1.5 StartAngle=4.71239 EndAngle=7.85398
    g14: ArcOfCircle CenterX=-1.5 CenterY=56.25 CenterZ=0 NormalX=0 NormalY=0 NormalZ=1 AngleXU=0 Radius=1.5 StartAngle=4.71239 EndAngle=7.85398
    g15: ArcOfCircle CenterX=-11.49 CenterY=50.5 CenterZ=0 NormalX=0 NormalY=0 NormalZ=1 AngleXU=0 Radius=1.5 StartAngle=4.71239 EndAngle=7.85398
    g16: ArcOfCircle CenterX=-16.28 CenterY=44.75 CenterZ=0 NormalX=0 NormalY=0 NormalZ=1 AngleXU=0 Radius=1.5 StartAngle=4.71239 EndAngle=7.85398
    g17: ArcOfCircle CenterX=-18.2337 CenterY=39 CenterZ=0 NormalX=0 NormalY=0 NormalZ=1 AngleXU=0 Radius=1.5 StartAngle=4.71485 EndAngle=7.85398
    g18: ArcOfCircle CenterX=-16.2837 CenterY=27.25 CenterZ=0 NormalX=0 NormalY=0 NormalZ=1 AngleXU=0 Radius=1.5 StartAngle=4.71485 EndAngle=7.85398
    g19: ArcOfCircle CenterX=-18.2337 CenterY=33 CenterZ=0 NormalX=0 NormalY=0 NormalZ=1 AngleXU=0 Radius=1.5 StartAngle=4.71485 EndAngle=7.85398
    g20: ArcOfCircle CenterX=-11.49 CenterY=21.5 CenterZ=0 NormalX=0 NormalY=0 NormalZ=1 AngleXU=0 Radius=1.5 StartAngle=4.71239 EndAngle=7.85398
    g21: ArcOfCircle CenterX=-1.5 CenterY=4.25 CenterZ=0 NormalX=0 NormalY=0 NormalZ=1 AngleXU=0 Radius=1.5 StartAngle=4.71239 EndAngle=7.85398
    g22: ArcOfCircle CenterX=-1.5 CenterY=10 CenterZ=0 NormalX=0 NormalY=0 NormalZ=1 AngleXU=0 Radius=1.5 StartAngle=4.71239 EndAngle=7.85398
    g23: ArcOfCircle CenterX=-1.5 CenterY=15.75 CenterZ=0 NormalX=0 NormalY=0 NormalZ=1 AngleXU=0 Radius=1.5 StartAngle=4.71239 EndAngle=7.85398
    g24: LineSegment StartX=-49.19 StartY=69.25 StartZ=0 EndX=-1.5 EndY=69.25 EndZ=0
    g25: LineSegment StartX=-49.19 StartY=66.25 StartZ=0 EndX=-1.5 EndY=66.25 EndZ=0
    g26: LineSegment StartX=-49.19 StartY=63.5 StartZ=0 EndX=-1.5 EndY=63.5 EndZ=0
    g27: LineSegment StartX=-49.19 StartY=60.5 StartZ=0 EndX=-1.5 EndY=60.5 EndZ=0
    g28: LineSegment StartX=-49.19 StartY=57.75 StartZ=0 EndX=-1.5 EndY=57.75 EndZ=0
    g29: LineSegment StartX=-49.19 StartY=54.75 StartZ=0 EndX=-1.5 EndY=54.75 EndZ=0
    g30: LineSegment StartX=-49.19 StartY=52 StartZ=0 EndX=-11.49 EndY=52 EndZ=0
    g31: LineSegment StartX=-49.19 StartY=49 StartZ=0 EndX=-11.49 EndY=49 EndZ=0
    g32: LineSegment StartX=-49.19 StartY=46.25 StartZ=0 EndX=-16.28 EndY=46.25 EndZ=0
    g33: LineSegment StartX=-49.19 StartY=43.25 StartZ=0 EndX=-16.28 EndY=43.25 EndZ=0
    g34: LineSegment StartX=-49.19 StartY=40.5 StartZ=0 EndX=-18.2337 EndY=40.5 EndZ=0
    g35: LineSegment StartX=-49.19 StartY=37.5 StartZ=0 EndX=-18.23 EndY=37.5 EndZ=0
    g36: LineSegment StartX=-49.19 StartY=34.5 StartZ=0 EndX=-18.2337 EndY=34.5 EndZ=0
    g37: LineSegment StartX=-49.19 StartY=31.5 StartZ=0 EndX=-18.23 EndY=31.5 EndZ=0
    g38: LineSegment StartX=-49.19 StartY=28.75 StartZ=0 EndX=-16.2837 EndY=28.75 EndZ=0
    g39: LineSegment StartX=-49.19 StartY=25.75 StartZ=0 EndX=-16.28 EndY=25.75 EndZ=0
    g40: LineSegment StartX=-49.19 StartY=23 StartZ=0 EndX=-11.49 EndY=23 EndZ=0
    g41: LineSegment StartX=-49.19 StartY=20 StartZ=0 EndX=-11.49 EndY=20 EndZ=0
    g42: LineSegment StartX=-49.19 StartY=17.25 StartZ=0 EndX=-1.5 EndY=17.25 EndZ=0
    g43: LineSegment StartX=-49.19 StartY=14.25 StartZ=0 EndX=-1.5 EndY=14.25 EndZ=0
    g44: LineSegment StartX=-49.19 StartY=11.5 StartZ=0 EndX=-1.5 EndY=11.5 EndZ=0
    g45: LineSegment StartX=-49.19 StartY=8.5 StartZ=0 EndX=-1.5 EndY=8.5 EndZ=0
    g46: LineSegment StartX=-49.19 StartY=5.75 StartZ=0 EndX=-1.5 EndY=5.75 EndZ=0
    g47: LineSegment StartX=-49.19 StartY=2.75 StartZ=0 EndX=-1.5 EndY=2.75 EndZ=0
  constraints (120):
    c: Vertical(g0)
    c: Distance(g0) = 3
    c: Block(g0)
    c: Vertical(g1)
    c: Distance(g1) = 3
    c: Vertical(g2)
    c: Equal(g0,g2) = 3
    c: Block(g2)
    c: Vertical(g3)
    c: Equal(g1,g3) = 3
    c: Vertical(g4)
    c: Equal(g0,g4) = 3
    c: Block(g4)
    c: Vertical(g5)
    c: Equal(g1,g5) = 3
    c: Vertical(g6)
    c: Equal(g0,g6) = 3
    c: Block(g6)
    c: Vertical(g7)
    c: Equal(g1,g7) = 3
    c: Vertical(g8)
    c: Equal(g0,g8) = 3
    c: Block(g8)
    c: Vertical(g9)
    c: Equal(g1,g9) = 3
    c: Vertical(g10)
    c: Equal(g0,g10) = 3
    c: Block(g10)
    c: Vertical(g11)
    c: Equal(g1,g11) = 3
    c: Block(g12)
    c: Block(g13)
    c: Block(g14)
    c: Block(g15)
    c: Block(g16)
    c: Block(g17)
    c: Block(g18)
    c: Block(g19)
    c: Block(g20)
    c: Block(g21)
    c: Block(g22)
    c: Block(g23)
    c: Block(g11)
    c: Block(g9)
    c: Block(g7)
    c: Block(g5)
    c: Block(g3)
    c: Block(g1)
    c: Coincident(g24,g0)
    c: Coincident(g24,g12)
    c: Horizontal(g24)
    c: Coincident(g25,g0)
    c: Coincident(g25,g12)
    c: Horizontal(g25)
    c: Coincident(g26,g1)
    c: Coincident(g26,g13)
    c: Horizontal(g26)
    c: Coincident(g27,g1)
    c: Coincident(g27,g13)
    c: Horizontal(g27)
    c: Coincident(g28,g2)
    c: Coincident(g28,g14)
    c: Horizontal(g28)
    c: Coincident(g29,g2)
    c: Coincident(g29,g14)
    c: Horizontal(g29)
    c: Coincident(g30,g3)
    c: Coincident(g30,g15)
    c: Horizontal(g30)
    c: Coincident(g31,g3)
    c: Coincident(g31,g15)
    c: Horizontal(g31)
    c: Coincident(g32,g4)
    c: Coincident(g32,g16)
    c: Horizontal(g32)
    c: Coincident(g33,g4)
    c: Coincident(g33,g16)
    c: Horizontal(g33)
    c: Coincident(g34,g5)
    c: Coincident(g34,g17)
    c: Horizontal(g34)
    c: Coincident(g35,g5)
    c: Coincident(g35,g17)
    c: Horizontal(g35)
    c: Coincident(g36,g6)
    c: Coincident(g36,g19)
    c: Horizontal(g36)
    c: Coincident(g37,g6)
    c: Coincident(g37,g19)
    c: Horizontal(g37)
    c: Coincident(g38,g7)
    c: Coincident(g38,g18)
    c: Horizontal(g38)
    c: Coincident(g39,g7)
    c: Coincident(g39,g18)
    c: Horizontal(g39)
    c: Coincident(g40,g8)
    c: Coincident(g40,g20)
    c: Horizontal(g40)
    c: Coincident(g41,g8)
    c: Coincident(g41,g20)
    c: Horizontal(g41)
    c: Coincident(g42,g9)
    c: Coincident(g42,g23)
    c: Horizontal(g42)
    c: Coincident(g43,g9)
    c: Coincident(g43,g23)
    c: Horizontal(g43)
    c: Coincident(g44,g10)
    c: Coincident(g44,g22)
    c: Horizontal(g44)
    c: Coincident(g45,g10)
    c: Coincident(g45,g22)
    c: Horizontal(g45)
    c: Coincident(g46,g11)
    c: Coincident(g46,g21)
    c: Horizontal(g46)
    c: Coincident(g47,g11)
    c: Coincident(g47,g21)
    c: Horizontal(g47)
FEATURE [Part::Extrusion] Extrude061
  Base = -> Sketch070
  Dir = (1,0,0)
  DirMode = 2
  FaceMakerClass = Part::FaceMakerBullseye
  LengthFwd = 23
  LengthRev = 0
  Placement = pos=(-19,0,0) rot=(0,0,1;0rad)
  Solid = true
  Symmetric = false
FEATURE [Part::Fillet] Fillet052  label="removeToCreateVentalationHoles002"
  Base = -> Extrude061
  Edges = <same value as first occurrence — deduplicated (x6 in doc)>
  Placement = pos=(7,0.02,0) rot=(0,0,1;0rad)
FEATURE [Part::MultiFuse] Fusion130  label="bottom013"
  Shapes = -> [Cut054,Cut034]
FEATURE [Part::Cut] Cut055
  Base = -> Fusion130
  Tool = -> Fillet052
FEATURE [Part::Cylinder] Cylinder054
  Angle = 360
  AttacherType = Attacher::AttachEngine3D
  Height = 20
  Placement = pos=(0,0,36.15) rot=(0,0,1;0rad)
  Radius = 4
FEATURE [Sketcher::SketchObject] Sketch071  label="bottomSketch002"
  FullyConstrained = true
  sketch-geometry (32):
    g0: LineSegment StartX=3.3 StartY=-6.03275e-07 StartZ=0 EndX=98 EndY=-6.03275e-07 EndZ=0
    g1: ArcOfCircle CenterX=98 CenterY=19 CenterZ=0 NormalX=0 NormalY=0 NormalZ=1 AngleXU=0 Radius=19 StartAngle=4.71239 EndAngle=5.71103
    g2: LineSegment StartX=6.3 StartY=8 StartZ=0 EndX=3.3 EndY=8 EndZ=0
    g3: LineSegment StartX=3.3 StartY=8 StartZ=0 EndX=3.3 EndY=-6.03275e-07 EndZ=0
    g4: ArcOfCircle CenterX=8.3 CenterY=5 CenterZ=0 NormalX=0 NormalY=0 NormalZ=1 AngleXU=0 Radius=2 StartAngle=3.14159 EndAngle=4.71239
    g5: LineSegment StartX=6.3 StartY=8 StartZ=0 EndX=6.3 EndY=5 EndZ=0
    g6: ArcOfCircle CenterX=98 CenterY=19 CenterZ=0 NormalX=0 NormalY=0 NormalZ=1 AngleXU=0 Radius=12.7 StartAngle=4.71239 EndAngle=6.28319
    g7: LineSegment StartX=94.7 StartY=3 StartZ=0 EndX=8.3 EndY=3 EndZ=0
    g8-g12: Circle x5 (B-spline internal-alignment scaffolding for g13; pole/knot coordinates omitted)
    g13: BSplineCurve PolesCount=5 KnotsCount=3 Degree=3 IsPeriodic=0
    g14: GeomPoint X=98 Y=6.3 Z=0
    g15: GeomPoint X=96.3938 Y=4.71946 Z=0
    g16: GeomPoint X=94.7 Y=3 Z=0
    g17-g23: Circle x7 (B-spline internal-alignment scaffolding for g24; pole/knot coordinates omitted)
    g24: BSplineCurve PolesCount=7 KnotsCount=5 Degree=3 IsPeriodic=0
    g25-g29: GeomPoint x5 (B-spline internal-alignment scaffolding for g24; pole/knot coordinates omitted)
    g30: ArcOfCircle CenterX=98 CenterY=19 CenterZ=0 NormalX=0 NormalY=0 NormalZ=1 AngleXU=0 Radius=15.7 StartAngle=5.81226 EndAngle=6.28319
    g31: LineSegment StartX=110.7 StartY=19 StartZ=0 EndX=113.7 EndY=19 EndZ=0
  constraints (41):
    c: Horizontal(g0)
    c: Coincident(g1,g0)
    c: Block(g1)
    c: Horizontal(g2)
    c: Distance(g2) = 3
    c: Coincident(g3,g2)
    c: Vertical(g3)
    c: Coincident(g3,g0)
    c: Block(g4)
    c: Block(g2)
    c: Coincident(g5,g2)
    c: Coincident(g5,g4)
    c: Vertical(g5)
    c: Coincident(g6,g1)
    c: Block(g6)
    c: Coincident(g7,g4)
    c: Horizontal(g7)
    c: Block(g0)
    c: Block(g7)
    c: Block(g3)
    c: Coincident(g13,g6)
    c: Weight(g8) = 1
    c: Equal(g8, g9-g12) x4
    c: Coincident(g13,g7)
    c: InternalAlignment(g8-g12 -> g13) x5
    c: InternalAlignment(g14,g13)
    c: InternalAlignment(g15,g13)
    c: InternalAlignment(g16,g13)
    c: Block(g13)
    c: Weight(g17) = 1
    c: Equal(g17, g18-g23) x6
    c: Coincident(g24,g1)
    c: InternalAlignment(g17-g23 -> g24) x7
    c: InternalAlignment(g25-g29 -> g24) x5
    c: Block(g24)
    c: Coincident(g30,g24)
    c: Coincident(g31,g6)
    c: Coincident(g31,g30)
    c: Horizontal(g31)
    c: Block(g31)
    c: Block(g30)
FEATURE [Part::Extrusion] Extrude062  label="bottom014"
  Base = -> Sketch071
  Dir = (0,0,1)
  DirMode = 2
  FaceMakerClass = Part::FaceMakerBullseye
  LengthFwd = 71.4
  LengthRev = 0
  Placement = pos=(0,0,0.3) rot=(0,0,1;0rad)
  Solid = true
  Symmetric = false
FEATURE [Part::Fillet] Fillet054
  Base = -> Extrude062
  Edges = 1 edges r=2.4: [Edge17]
FEATURE [Part::Fillet] Fillet055  label="bottom015"
  Base = -> Fillet054
  Edges = 1 edges r=2.4: [Edge36]
FEATURE [Part::Cylinder] Cylinder055
  Angle = 360
  AttacherType = Attacher::AttachEngine3D
  Height = 10
  Placement = pos=(0,0,36.15) rot=(0,0,1;0rad)
  Radius = 4
FEATURE [Part::MultiFuse] Fusion131  label="removeToCreateHoleForPlugHousing002"
  Placement = pos=(70,19,36.15) rot=(0,1,0;1.5708rad)
  Shapes = -> [Cylinder054,Cylinder055]
FEATURE [Part::Cut] Cut056  label="Bottom001"
  Base = -> Fillet055
  Placement = pos=(9,0,0) rot=(0,0,1;0rad)
  Tool = -> Fusion131
FEATURE [Part::Cut] Cut057
  Base = -> Cut055
  Tool = -> Cut056
FEATURE [Sketcher::SketchObject] Sketch072  label="topSketch021"
  FullyConstrained = true
  sketch-geometry (4):
    g0: ArcOfCircle CenterX=105 CenterY=19 CenterZ=0 NormalX=0 NormalY=0 NormalZ=1 AngleXU=0 Radius=20.6155 StartAngle=5.54125 EndAngle=6.28319
    g1: ArcOfCircle CenterX=105 CenterY=19 CenterZ=0 NormalX=0 NormalY=0 NormalZ=1 AngleXU=0 Radius=13 StartAngle=5.54125 EndAngle=6.28319
    g2: LineSegment StartX=118 StartY=19 StartZ=0 EndX=125.616 EndY=19 EndZ=0
    g3: LineSegment StartX=114.583 StartY=10.2157 StartZ=0 EndX=120.197 EndY=5.06982 EndZ=0
  constraints (7):
    c: Block(g0)
    c: Block(g1)
    c: Coincident(g2,g1)
    c: Coincident(g2,g0)
    c: Horizontal(g2)
    c: Coincident(g3,g1)
    c: Coincident(g3,g0)
FEATURE [Part::Extrusion] Extrude063  label="bottomPlugHousingBit003"
  Base = -> Sketch072
  Dir = (0,0,1)
  DirMode = 2
  FaceMakerClass = Part::FaceMakerBullseye
  LengthFwd = 72
  LengthRev = 0
  Solid = true
  Symmetric = false
FEATURE [Part::Cylinder] Cylinder056
  Angle = 360
  AttacherType = Attacher::AttachEngine3D
  Height = 20
  Placement = pos=(0,0,36.15) rot=(0,0,1;0rad)
  Radius = 14.3
FEATURE [Part::Cylinder] Cylinder057
  Angle = 360
  AttacherType = Attacher::AttachEngine3D
  Height = 10
  Placement = pos=(0,0,36.15) rot=(0,0,1;0rad)
  Radius = 4
FEATURE [Part::Box] Box034  label="removeToCreteHoleForPlugHousing047"
  AttacherType = Attacher::AttachEngine3D
  Height = 28.6
  Length = 20
  Placement = pos=(106.15,0,21.7) rot=(0,0,1;0rad)
  Width = 19
FEATURE [Part::Cylinder] Cylinder058
  Angle = 360
  AttacherType = Attacher::AttachEngine3D
  Height = 20
  Placement = pos=(0,0,36.15) rot=(0,0,1;0rad)
  Radius = 14.3
FEATURE [Part::Cylinder] Cylinder059
  Angle = 360
  AttacherType = Attacher::AttachEngine3D
  Height = 10
  Placement = pos=(0,0,36.15) rot=(0,0,1;0rad)
  Radius = 4
FEATURE [Part::MultiFuse] Fusion134  label="removeToCreteHoleForPlugHousing046"
  Placement = pos=(70,19,36) rot=(0,1,0;1.5708rad)
  Shapes = -> [Cylinder058,Cylinder059]
FEATURE [Part::Cylinder] Cylinder060
  Angle = 360
  AttacherType = Attacher::AttachEngine3D
  Height = 20
  Placement = pos=(0,0,36.15) rot=(0,0,1;0rad)
  Radius = 14
FEATURE [Part::Cylinder] Cylinder061
  Angle = 360
  AttacherType = Attacher::AttachEngine3D
  Height = 10
  Placement = pos=(0,0,36.15) rot=(0,0,1;0rad)
  Radius = 4
FEATURE [Part::MultiFuse] Fusion135  label="removeToCreteHoleForPlugHousing048"
  Placement = pos=(70,19,36) rot=(0,1,0;1.5708rad)
  Shapes = -> [Cylinder060,Cylinder061]
FEATURE [Part::Box] Box035  label="removeToCreteHoleForPlugHousing049"
  AttacherType = Attacher::AttachEngine3D
  Height = 28.6
  Length = 20
  Placement = pos=(106.15,0,21.7) rot=(0,0,1;0rad)
  Width = 19
FEATURE [Part::MultiFuse] Fusion133  label="removeToCreteHoleForPlugHousing045"
  Placement = pos=(0,0,-28.3) rot=(0,0,1;0rad)
  Shapes = -> [Box035,Fusion134]
FEATURE [Part::MultiFuse] Fusion138  label="removeToCreteHoleForPlugHousing051"
  Placement = pos=(70,19,36) rot=(0,1,0;1.5708rad)
  Shapes = -> [Cylinder056,Cylinder057]
FEATURE [Part::MultiFuse] Fusion137  label="removeToCreteHoleForPlugHousing050"
  Placement = pos=(0,0,28.3) rot=(0,0,1;0rad)
  Shapes = -> [Box034,Fusion138]
FEATURE [Part::MultiFuse] Fusion132  label="removeToCreatePlugHousingBottomBit002"
  Shapes = -> [Fusion133,Fusion137]
FEATURE [Part::MultiFuse] Fusion136  label="removeToCreatePlugHousingBottomBit003"
  Shapes = -> [Fusion135,Fusion132]
FEATURE [Part::Cut] Cut058  label="bottomPlugHousingBit002"
  Base = -> Extrude063
  Placement = pos=(-0.09,0,0) rot=(0,0,1;0rad)
  Tool = -> Fusion136
FEATURE [Sketcher::SketchObject] Sketch073  label="bottomSketch003"
  FullyConstrained = true
  sketch-geometry (45):
    g0: LineSegment StartX=6.29999 StartY=8 StartZ=0 EndX=3.29999 EndY=8 EndZ=0
    g1: LineSegment StartX=3.29999 StartY=8 StartZ=0 EndX=3.29999 EndY=-6.03275e-07 EndZ=0
    g2: ArcOfCircle CenterX=8.29999 CenterY=5 CenterZ=0 NormalX=0 NormalY=0 NormalZ=1 AngleXU=0 Radius=2 StartAngle=3.14159 EndAngle=4.71239
    g3: LineSegment StartX=6.29999 StartY=8 StartZ=0 EndX=6.29999 EndY=5 EndZ=0
    g4: ArcOfCircle CenterX=105 CenterY=19 CenterZ=0 NormalX=0 NormalY=0 NormalZ=1 AngleXU=0 Radius=12.7 StartAngle=4.71239 EndAngle=5.94289
    g5-g11: Circle x7 (B-spline internal-alignment scaffolding for g12; pole/knot coordinates omitted)
    g12: BSplineCurve PolesCount=7 KnotsCount=5 Degree=3 IsPeriodic=0
    g13-g17: GeomPoint x5 (B-spline internal-alignment scaffolding for g12; pole/knot coordinates omitted)
    g18: ArcOfCircle CenterX=105 CenterY=19 CenterZ=0 NormalX=0 NormalY=0 NormalZ=1 AngleXU=0 Radius=15.7 StartAngle=5.81226 EndAngle=6.28319
    g19: BSplineCurve PolesCount=5 KnotsCount=3 Degree=3 IsPeriodic=0
    g20: LineSegment StartX=8.29999 StartY=3 StartZ=0 EndX=101.7 EndY=3 EndZ=0
    g21: LineSegment StartX=3.29999 StartY=-6.03275e-07 StartZ=0 EndX=105 EndY=-6.03275e-07 EndZ=0
    g22: LineSegment StartX=120.974 StartY=8.71251 StartZ=0 EndX=122.332 EndY=7.83778 EndZ=0
    g23: LineSegment StartX=105 StartY=-6.03274e-07 StartZ=0 EndX=113 EndY=-6.03274e-07 EndZ=0
    g24: ArcOfCircle CenterX=105 CenterY=19 CenterZ=0 NormalX=0 NormalY=0 NormalZ=1 AngleXU=0 Radius=20.6155 StartAngle=5.11091 EndAngle=5.71103
    g25: ArcOfCircle CenterX=117.7 CenterY=19 CenterZ=0 NormalX=0 NormalY=0 NormalZ=1 AngleXU=0 Radius=3 StartAngle=1.2e-15 EndAngle=2.10468
    g26: Circle CenterX=116.345 CenterY=16.3232 CenterZ=0 NormalX=0 NormalY=0 NormalZ=1 AngleXU=0 Radius=1
    g27: Circle CenterX=117.24 CenterY=15.7584 CenterZ=0 NormalX=0 NormalY=0 NormalZ=1 AngleXU=0 Radius=1
    g28: Circle CenterX=116.972 CenterY=14.7612 CenterZ=0 NormalX=0 NormalY=0 NormalZ=1 AngleXU=0 Radius=1
    g29: BSplineCurve PolesCount=3 KnotsCount=2 Degree=2 IsPeriodic=0
    g30: GeomPoint X=116.345 Y=16.3232 Z=0
    g31: GeomPoint X=116.972 Y=14.7612 Z=0
    g32: Circle CenterX=115.828 CenterY=17.157 CenterZ=0 NormalX=0 NormalY=0 NormalZ=1 AngleXU=0 Radius=1
    g33: Circle CenterX=115.841 CenterY=16.639 CenterZ=0 NormalX=0 NormalY=0 NormalZ=1 AngleXU=0 Radius=1
    g34: Circle CenterX=116.345 CenterY=16.3232 CenterZ=0 NormalX=0 NormalY=0 NormalZ=1 AngleXU=0 Radius=1
    g35: BSplineCurve PolesCount=3 KnotsCount=2 Degree=2 IsPeriodic=0
    g36: GeomPoint X=115.828 Y=17.157 Z=0
    g37: GeomPoint X=116.345 Y=16.3232 Z=0
    g38: LineSegment StartX=115.828 StartY=17.157 StartZ=0 EndX=115.828 EndY=20.8307 EndZ=0
    g39: Circle CenterX=115.828 CenterY=20.8307 CenterZ=0 NormalX=0 NormalY=0 NormalZ=1 AngleXU=0 Radius=1
    g40: Circle CenterX=115.831 CenterY=21.3396 CenterZ=0 NormalX=0 NormalY=0 NormalZ=1 AngleXU=0 Radius=1
    g41: Circle CenterX=116.173 CenterY=21.5825 CenterZ=0 NormalX=0 NormalY=0 NormalZ=1 AngleXU=0 Radius=1
    g42: BSplineCurve PolesCount=3 KnotsCount=2 Degree=2 IsPeriodic=0
    g43: GeomPoint X=115.828 Y=20.8307 Z=0
    g44: GeomPoint X=116.173 Y=21.5825 Z=0
  constraints (70):
    c: Horizontal(g0)
    c: Distance(g0) = 3
    c: Coincident(g1,g0)
    c: Vertical(g1)
    c: Block(g2)
    c: Block(g0)
    c: Coincident(g3,g0)
    c: Coincident(g3,g2)
    c: Vertical(g3)
    c: Block(g1)
    c: Block(g4)
    c: Coincident(g19,g4)
    c: Block(g19)
    c: Equal(g5, g6-g11) x6
    c: InternalAlignment(g5-g11 -> g12) x7
    c: InternalAlignment(g13-g17 -> g12) x5
    c: Block(g12)
    c: Coincident(g18,g12)
    c: Block(g18)
    c: Coincident(g20,g2)
    c: Coincident(g20,g19)
    c: Horizontal(g20)
    c: Distance(g20) = 93.4
    c: Coincident(g21,g1)
    c: Horizontal(g21)
    c: Distance(g21) = 101.7
    c: Horizontal(g23)
    c: Distance(g23) = 8
    c: Coincident(g24,g23)
    c: Block(g23)
    c: Coincident(g22,g24)
    c: Block(g24)
    c: Block(g22)
    c: Distance(g22) = 1.61553
    c: Coincident(g25,g18)
    c: Block(g25)
    c: Weight(g26) = 1
    c: Equal(g26,g27)
    c: Equal(g26,g28)
    c: Coincident(g29,g4)
    c: InternalAlignment(g26,g29)
    c: InternalAlignment(g27,g29)
    c: InternalAlignment(g28,g29)
    c: InternalAlignment(g30,g29)
    c: InternalAlignment(g31,g29)
    c: Block(g29)
    c: Weight(g32) = 1
    c: Equal(g32,g33)
    c: Equal(g32,g34)
    c: Coincident(g35,g29)
    c: InternalAlignment(g32,g35)
    c: InternalAlignment(g33,g35)
    c: InternalAlignment(g34,g35)
    c: InternalAlignment(g36,g35)
    c: InternalAlignment(g37,g35)
    c: Block(g35)
    c: Coincident(g38,g35)
    c: Vertical(g38)
    c: Block(g38)
    c: Coincident(g42,g38)
    c: Weight(g39) = 1
    c: Equal(g39,g40)
    c: Equal(g39,g41)
    c: Coincident(g42,g25)
    c: InternalAlignment(g39,g42)
    c: InternalAlignment(g40,g42)
    c: InternalAlignment(g41,g42)
    c: InternalAlignment(g43,g42)
    c: InternalAlignment(g44,g42)
    c: Block(g42)
FEATURE [Part::Extrusion] Extrude064  label="bottom016"
  Base = -> Sketch073
  Dir = (0,0,1)
  DirMode = 2
  FaceMakerClass = Part::FaceMakerBullseye
  LengthFwd = 71.4
  LengthRev = 0
  Placement = pos=(0,0,0.3) rot=(0,0,1;0rad)
  Solid = true
  Symmetric = false
FEATURE [Part::Revolution] Revolve157  label="removeToCreateScrewAndThreadedInsertHole063"
  Angle = 360
  Axis = (0,1,0)
  Base = (0,0,0)
  FaceMakerClass = Part::FaceMakerBullseye
  Placement = pos=(12.5,0,10) rot=(0,0,1;0rad)
  Solid = false
  Source = -> Face141
  Symmetric = false
FEATURE [Sketcher::SketchObject] Sketch074
  FullyConstrained = true
  Placement = pos=(117,19,0) rot=(0.57735,0.57735,0.57735;2.0944rad)
  sketch-geometry (48):
    g0: LineSegment StartX=-49.19 StartY=69.25 StartZ=0 EndX=-49.19 EndY=66.25 EndZ=0
    g1: LineSegment StartX=-49.19 StartY=63.5 StartZ=0 EndX=-49.19 EndY=60.5 EndZ=0
    g2: LineSegment StartX=-49.19 StartY=57.75 StartZ=0 EndX=-49.19 EndY=54.75 EndZ=0
    g3: LineSegment StartX=-49.19 StartY=52 StartZ=0 EndX=-49.19 EndY=49 EndZ=0
    g4: LineSegment StartX=-49.19 StartY=46.25 StartZ=0 EndX=-49.19 EndY=43.25 EndZ=0
    g5: LineSegment StartX=-49.19 StartY=40.5 StartZ=0 EndX=-49.19 EndY=37.5 EndZ=0
    g6: LineSegment StartX=-49.19 StartY=34.5 StartZ=0 EndX=-49.19 EndY=31.5 EndZ=0
    g7: LineSegment StartX=-49.19 StartY=28.75 StartZ=0 EndX=-49.19 EndY=25.75 EndZ=0
    g8: LineSegment StartX=-49.19 StartY=23 StartZ=0 EndX=-49.19 EndY=20 EndZ=0
    g9: LineSegment StartX=-49.19 StartY=17.25 StartZ=0 EndX=-49.19 EndY=14.25 EndZ=0
    g10: LineSegment StartX=-49.19 StartY=11.5 StartZ=0 EndX=-49.19 EndY=8.5 EndZ=0
    g11: LineSegment StartX=-49.19 StartY=5.75 StartZ=0 EndX=-49.19 EndY=2.75 EndZ=0
    g12: ArcOfCircle CenterX=-1.5 CenterY=67.75 CenterZ=0 NormalX=0 NormalY=0 NormalZ=1 AngleXU=0 Radius=1.5 StartAngle=4.71239 EndAngle=7.85398
    g13: ArcOfCircle CenterX=-1.5 CenterY=62 CenterZ=0 NormalX=0 NormalY=0 NormalZ=1 AngleXU=0 Radius=1.5 StartAngle=4.71239 EndAngle=7.85398
    g14: ArcOfCircle CenterX=-1.5 CenterY=56.25 CenterZ=0 NormalX=0 NormalY=0 NormalZ=1 AngleXU=0 Radius=1.5 StartAngle=4.71239 EndAngle=7.85398
    g15: ArcOfCircle CenterX=-11.49 CenterY=50.5 CenterZ=0 NormalX=0 NormalY=0 NormalZ=1 AngleXU=0 Radius=1.5 StartAngle=4.71239 EndAngle=7.85398
    g16: ArcOfCircle CenterX=-16.28 CenterY=44.75 CenterZ=0 NormalX=0 NormalY=0 NormalZ=1 AngleXU=0 Radius=1.5 StartAngle=4.71239 EndAngle=7.85398
    g17: ArcOfCircle CenterX=-18.2337 CenterY=39 CenterZ=0 NormalX=0 NormalY=0 NormalZ=1 AngleXU=0 Radius=1.5 StartAngle=4.71485 EndAngle=7.85398
    g18: ArcOfCircle CenterX=-16.2837 CenterY=27.25 CenterZ=0 NormalX=0 NormalY=0 NormalZ=1 AngleXU=0 Radius=1.5 StartAngle=4.71485 EndAngle=7.85398
    g19: ArcOfCircle CenterX=-18.2337 CenterY=33 CenterZ=0 NormalX=0 NormalY=0 NormalZ=1 AngleXU=0 Radius=1.5 StartAngle=4.71485 EndAngle=7.85398
    g20: ArcOfCircle CenterX=-11.49 CenterY=21.5 CenterZ=0 NormalX=0 NormalY=0 NormalZ=1 AngleXU=0 Radius=1.5 StartAngle=4.71239 EndAngle=7.85398
    g21: ArcOfCircle CenterX=-1.5 CenterY=4.25 CenterZ=0 NormalX=0 NormalY=0 NormalZ=1 AngleXU=0 Radius=1.5 StartAngle=4.71239 EndAngle=7.85398
    g22: ArcOfCircle CenterX=-1.5 CenterY=10 CenterZ=0 NormalX=0 NormalY=0 NormalZ=1 AngleXU=0 Radius=1.5 StartAngle=4.71239 EndAngle=7.85398
    g23: ArcOfCircle CenterX=-1.5 CenterY=15.75 CenterZ=0 NormalX=0 NormalY=0 NormalZ=1 AngleXU=0 Radius=1.5 StartAngle=4.71239 EndAngle=7.85398
    g24: LineSegment StartX=-49.19 StartY=69.25 StartZ=0 EndX=-1.5 EndY=69.25 EndZ=0
    g25: LineSegment StartX=-49.19 StartY=66.25 StartZ=0 EndX=-1.5 EndY=66.25 EndZ=0
    g26: LineSegment StartX=-49.19 StartY=63.5 StartZ=0 EndX=-1.5 EndY=63.5 EndZ=0
    g27: LineSegment StartX=-49.19 StartY=60.5 StartZ=0 EndX=-1.5 EndY=60.5 EndZ=0
    g28: LineSegment StartX=-49.19 StartY=57.75 StartZ=0 EndX=-1.5 EndY=57.75 EndZ=0
    g29: LineSegment StartX=-49.19 StartY=54.75 StartZ=0 EndX=-1.5 EndY=54.75 EndZ=0
    g30: LineSegment StartX=-49.19 StartY=52 StartZ=0 EndX=-11.49 EndY=52 EndZ=0
    g31: LineSegment StartX=-49.19 StartY=49 StartZ=0 EndX=-11.49 EndY=49 EndZ=0
    g32: LineSegment StartX=-49.19 StartY=46.25 StartZ=0 EndX=-16.28 EndY=46.25 EndZ=0
    g33: LineSegment StartX=-49.19 StartY=43.25 StartZ=0 EndX=-16.28 EndY=43.25 EndZ=0
    g34: LineSegment StartX=-49.19 StartY=40.5 StartZ=0 EndX=-18.2337 EndY=40.5 EndZ=0
    g35: LineSegment StartX=-49.19 StartY=37.5 StartZ=0 EndX=-18.23 EndY=37.5 EndZ=0
    g36: LineSegment StartX=-49.19 StartY=34.5 StartZ=0 EndX=-18.2337 EndY=34.5 EndZ=0
    g37: LineSegment StartX=-49.19 StartY=31.5 StartZ=0 EndX=-18.23 EndY=31.5 EndZ=0
    g38: LineSegment StartX=-49.19 StartY=28.75 StartZ=0 EndX=-16.2837 EndY=28.75 EndZ=0
    g39: LineSegment StartX=-49.19 StartY=25.75 StartZ=0 EndX=-16.28 EndY=25.75 EndZ=0
    g40: LineSegment StartX=-49.19 StartY=23 StartZ=0 EndX=-11.49 EndY=23 EndZ=0
    g41: LineSegment StartX=-49.19 StartY=20 StartZ=0 EndX=-11.49 EndY=20 EndZ=0
    g42: LineSegment StartX=-49.19 StartY=17.25 StartZ=0 EndX=-1.5 EndY=17.25 EndZ=0
    g43: LineSegment StartX=-49.19 StartY=14.25 StartZ=0 EndX=-1.5 EndY=14.25 EndZ=0
    g44: LineSegment StartX=-49.19 StartY=11.5 StartZ=0 EndX=-1.5 EndY=11.5 EndZ=0
    g45: LineSegment StartX=-49.19 StartY=8.5 StartZ=0 EndX=-1.5 EndY=8.5 EndZ=0
    g46: LineSegment StartX=-49.19 StartY=5.75 StartZ=0 EndX=-1.5 EndY=5.75 EndZ=0
    g47: LineSegment StartX=-49.19 StartY=2.75 StartZ=0 EndX=-1.5 EndY=2.75 EndZ=0
  constraints (120):
    c: Vertical(g0)
    c: Distance(g0) = 3
    c: Block(g0)
    c: Vertical(g1)
    c: Distance(g1) = 3
    c: Vertical(g2)
    c: Equal(g0,g2) = 3
    c: Block(g2)
    c: Vertical(g3)
    c: Equal(g1,g3) = 3
    c: Vertical(g4)
    c: Equal(g0,g4) = 3
    c: Block(g4)
    c: Vertical(g5)
    c: Equal(g1,g5) = 3
    c: Vertical(g6)
    c: Equal(g0,g6) = 3
    c: Block(g6)
    c: Vertical(g7)
    c: Equal(g1,g7) = 3
    c: Vertical(g8)
    c: Equal(g0,g8) = 3
    c: Block(g8)
    c: Vertical(g9)
    c: Equal(g1,g9) = 3
    c: Vertical(g10)
    c: Equal(g0,g10) = 3
    c: Block(g10)
    c: Vertical(g11)
    c: Equal(g1,g11) = 3
    c: Block(g12)
    c: Block(g13)
    c: Block(g14)
    c: Block(g15)
    c: Block(g16)
    c: Block(g17)
    c: Block(g18)
    c: Block(g19)
    c: Block(g20)
    c: Block(g21)
    c: Block(g22)
    c: Block(g23)
    c: Block(g11)
    c: Block(g9)
    c: Block(g7)
    c: Block(g5)
    c: Block(g3)
    c: Block(g1)
    c: Coincident(g24,g0)
    c: Coincident(g24,g12)
    c: Horizontal(g24)
    c: Coincident(g25,g0)
    c: Coincident(g25,g12)
    c: Horizontal(g25)
    c: Coincident(g26,g1)
    c: Coincident(g26,g13)
    c: Horizontal(g26)
    c: Coincident(g27,g1)
    c: Coincident(g27,g13)
    c: Horizontal(g27)
    c: Coincident(g28,g2)
    c: Coincident(g28,g14)
    c: Horizontal(g28)
    c: Coincident(g29,g2)
    c: Coincident(g29,g14)
    c: Horizontal(g29)
    c: Coincident(g30,g3)
    c: Coincident(g30,g15)
    c: Horizontal(g30)
    c: Coincident(g31,g3)
    c: Coincident(g31,g15)
    c: Horizontal(g31)
    c: Coincident(g32,g4)
    c: Coincident(g32,g16)
    c: Horizontal(g32)
    c: Coincident(g33,g4)
    c: Coincident(g33,g16)
    c: Horizontal(g33)
    c: Coincident(g34,g5)
    c: Coincident(g34,g17)
    c: Horizontal(g34)
    c: Coincident(g35,g5)
    c: Coincident(g35,g17)
    c: Horizontal(g35)
    c: Coincident(g36,g6)
    c: Coincident(g36,g19)
    c: Horizontal(g36)
    c: Coincident(g37,g6)
    c: Coincident(g37,g19)
    c: Horizontal(g37)
    c: Coincident(g38,g7)
    c: Coincident(g38,g18)
    c: Horizontal(g38)
    c: Coincident(g39,g7)
    c: Coincident(g39,g18)
    c: Horizontal(g39)
    c: Coincident(g40,g8)
    c: Coincident(g40,g20)
    c: Horizontal(g40)
    c: Coincident(g41,g8)
    c: Coincident(g41,g20)
    c: Horizontal(g41)
    c: Coincident(g42,g9)
    c: Coincident(g42,g23)
    c: Horizontal(g42)
    c: Coincident(g43,g9)
    c: Coincident(g43,g23)
    c: Horizontal(g43)
    c: Coincident(g44,g10)
    c: Coincident(g44,g22)
    c: Horizontal(g44)
    c: Coincident(g45,g10)
    c: Coincident(g45,g22)
    c: Horizontal(g45)
    c: Coincident(g46,g11)
    c: Coincident(g46,g21)
    c: Horizontal(g46)
    c: Coincident(g47,g11)
    c: Coincident(g47,g21)
    c: Horizontal(g47)
FEATURE [Part::Extrusion] Extrude065
  Base = -> Sketch074
  Dir = (1,0,0)
  DirMode = 2
  FaceMakerClass = Part::FaceMakerBullseye
  LengthFwd = 23
  LengthRev = 0
  Placement = pos=(-19,0,0) rot=(0,0,1;0rad)
  Solid = true
  Symmetric = false
FEATURE [Part::Fillet] Fillet056  label="removeToCreateVentalationHoles003"
  Base = -> Extrude065
  Edges = <same value as first occurrence — deduplicated (x6 in doc)>
  Placement = pos=(7,0.02,0) rot=(0,0,1;0rad)
FEATURE [Part::Revolution] Revolve158  label="removeToCreateScrewAndThreadedInsertHole065"
  Angle = 360
  Axis = (0,1,0)
  Base = (0,0,0)
  FaceMakerClass = Part::FaceMakerBullseye
  Placement = pos=(12.5,0,62) rot=(0,0,1;0rad)
  Solid = false
  Source = -> Face146
  Symmetric = false
FEATURE [Part::Revolution] Revolve159  label="removeToCreateScrewAndThreadedInsertHole066"
  Angle = 360
  Axis = (0,1,0)
  Base = (0,0,0)
  FaceMakerClass = Part::FaceMakerBullseye
  Placement = pos=(89.5,0,68.5) rot=(0,0,1;0rad)
  Solid = false
  Source = -> Face143
  Symmetric = false
FEATURE [Part::Revolution] Revolve160  label="removeToCreateScrewAndThreadedInsertHole067"
  Angle = 360
  Axis = (0,1,0)
  Base = (0,0,0)
  FaceMakerClass = Part::FaceMakerBullseye
  Placement = pos=(89.5,0,3.5) rot=(0,0,1;0rad)
  Solid = false
  Source = -> Face142
  Symmetric = false
FEATURE [Part::Revolution] Revolve161  label="removeToCreateScrewAndThreadedInsertHole068"
  Angle = 360
  Axis = (0,1,0)
  Base = (0,0,0)
  FaceMakerClass = Part::FaceMakerBullseye
  Placement = pos=(109.5,4.7,3.5) rot=(0,0,1;0rad)
  Solid = false
  Source = -> Face145
  Symmetric = false
FEATURE [Part::Revolution] Revolve162  label="removeToCreateScrewAndThreadedInsertHole069"
  Angle = 360
  Axis = (0,1,0)
  Base = (0,0,0)
  FaceMakerClass = Part::FaceMakerBullseye
  Placement = pos=(109.5,4.7,68.5) rot=(0,0,1;0rad)
  Solid = false
  Source = -> Face144
  Symmetric = false
FEATURE [Part::MultiFuse] Fusion141  label="removeToCreateScrewAndThreadedInsertHole064"
  Shapes = -> [Revolve162,Revolve161,Revolve160,Revolve159,Revolve158,Revolve157]
FEATURE [Part::Cylinder] Cylinder062
  Angle = 360
  AttacherType = Attacher::AttachEngine3D
  Height = 20
  Placement = pos=(0,0,36.15) rot=(0,0,1;0rad)
  Radius = 14
FEATURE [Part::Cylinder] Cylinder063
  Angle = 360
  AttacherType = Attacher::AttachEngine3D
  Height = 10
  Placement = pos=(0,0,36.15) rot=(0,0,1;0rad)
  Radius = 4
FEATURE [Part::MultiFuse] Fusion139  label="removeToCreteHoleForPlugHousing052"
  Placement = pos=(70,19,36) rot=(0,1,0;1.5708rad)
  Shapes = -> [Cylinder062,Cylinder063]
FEATURE [Part::Cut] Cut060  label="bottom017"
  Base = -> Extrude064
  Tool = -> Fusion139
FEATURE [Part::Cut] Cut061  label="bottom019"
  Base = -> Cut060
  Tool = -> Fusion141
FEATURE [Part::MultiFuse] Fusion140  label="bottom018"
  Shapes = -> [Cut061,Cut058]
FEATURE [Part::Cut] Cut059  label="bottom020"
  Base = -> Fusion140
  Tool = -> Fillet056
FEATURE [Part::Box] Box036  label="Cube021"
  AttacherType = Attacher::AttachEngine3D
  Height = 80
  Length = 26
  Placement = pos=(0,-1,-5) rot=(0,0,1;0rad)
  Width = 11
FEATURE [Part::Cut] Cut062  label="removeFromBottom002"
  Base = -> Cut057
  Tool = -> Box036
FEATURE [Part::Cut] Cut063
  Base = -> Cut059
  Tool = -> Cut062
FEATURE [Part::Cut] Cut064  label="pcbStands"
  Base = -> Fusion095
  Tool = -> Fusion127
FEATURE [Sketcher::SketchObject] Sketch075  label="topSketch022"
  FullyConstrained = true
  sketch-geometry (6):
    g0: LineSegment StartX=19 StartY=38 StartZ=0 EndX=117 EndY=38 EndZ=0
    g1: ArcOfCircle CenterX=19 CenterY=19 CenterZ=0 NormalX=0 NormalY=0 NormalZ=1 AngleXU=0 Radius=19 StartAngle=1.5708 EndAngle=3.14159
    g2: LineSegment StartX=117 StartY=38 StartZ=0 EndX=117 EndY=19 EndZ=0
    g3: LineSegment StartX=98 StartY=1.0161e-12 StartZ=0 EndX=5.22862e-06 EndY=1.0161e-12 EndZ=0
    g4: LineSegment StartX=5.22862e-06 StartY=19 StartZ=0 EndX=5.22862e-06 EndY=1.0161e-12 EndZ=0
    g5: ArcOfCircle CenterX=98 CenterY=19 CenterZ=0 NormalX=0 NormalY=0 NormalZ=1 AngleXU=0 Radius=19 StartAngle=4.71239 EndAngle=6.28319
  constraints (16):
    c: Horizontal(g0)
    c: Distance(g0) = 98
    c: Coincident(g1,g0)
    c: Block(g1)
    c: Coincident(g2,g0)
    c: Vertical(g2)
    c: Distance(g2) = 19
    c: Horizontal(g3)
    c: Coincident(g4,g1)
    c: Vertical(g4)
    c: Coincident(g3,g4)
    c: Block(g3)
    c: Coincident(g5,g2)
    c: Coincident(g5,g3)
    c: Block(g0)
    c: Block(g5)
FEATURE [Part::Extrusion] Extrude067  label="sideB003"
  Base = -> Sketch075
  Dir = (0,0,1)
  DirMode = 2
  FaceMakerClass = Part::FaceMakerBullseye
  LengthFwd = 3
  LengthRev = 0
  Placement = pos=(0,0,71.7) rot=(0,0,1;0rad)
  Solid = true
  Symmetric = false
FEATURE [Sketcher::SketchObject] Sketch076  label="topSketch023"
  FullyConstrained = true
  sketch-geometry (6):
    g0: LineSegment StartX=19 StartY=38 StartZ=0 EndX=117 EndY=38 EndZ=0
    g1: ArcOfCircle CenterX=19 CenterY=19 CenterZ=0 NormalX=0 NormalY=0 NormalZ=1 AngleXU=0 Radius=19 StartAngle=1.5708 EndAngle=3.14159
    g2: LineSegment StartX=117 StartY=38 StartZ=0 EndX=117 EndY=19 EndZ=0
    g3: LineSegment StartX=98 StartY=1.0161e-12 StartZ=0 EndX=5.22862e-06 EndY=1.0161e-12 EndZ=0
    g4: LineSegment StartX=5.22862e-06 StartY=19 StartZ=0 EndX=5.22862e-06 EndY=1.0161e-12 EndZ=0
    g5: ArcOfCircle CenterX=98 CenterY=19 CenterZ=0 NormalX=0 NormalY=0 NormalZ=1 AngleXU=0 Radius=19 StartAngle=4.71239 EndAngle=6.28319
  constraints (16):
    c: Horizontal(g0)
    c: Distance(g0) = 98
    c: Coincident(g1,g0)
    c: Block(g1)
    c: Coincident(g2,g0)
    c: Vertical(g2)
    c: Distance(g2) = 19
    c: Horizontal(g3)
    c: Coincident(g4,g1)
    c: Vertical(g4)
    c: Coincident(g3,g4)
    c: Block(g3)
    c: Coincident(g5,g2)
    c: Coincident(g5,g3)
    c: Block(g0)
    c: Block(g5)
FEATURE [Part::Extrusion] Extrude066  label="sideA003"
  Base = -> Sketch076
  Dir = (0,0,1)
  DirMode = 2
  FaceMakerClass = Part::FaceMakerBullseye
  LengthFwd = 3
  LengthRev = 0
  Placement = pos=(0,0,-2.7) rot=(0,0,1;0rad)
  Solid = true
  Symmetric = false
FEATURE [Part::MultiFuse] Fusion142  label="removeFromBottom003"
  Placement = pos=(2,0,0) rot=(0,0,1;0rad)
  Shapes = -> [Extrude066,Extrude067]
FEATURE [Part::Cut] Cut065  label="screwRetainers002"
  Base = -> Fusion096
  Tool = -> Fusion142
FEATURE [Sketcher::SketchObject] Sketch077
  FullyConstrained = true
  Placement = pos=(117,19,0) rot=(0.57735,0.57735,0.57735;2.0944rad)
  sketch-geometry (8):
    g0: LineSegment StartX=-49.19 StartY=63.5 StartZ=0 EndX=-49.19 EndY=60.5 EndZ=0
    g1: LineSegment StartX=-49.19 StartY=11.5 StartZ=0 EndX=-49.19 EndY=8.5 EndZ=0
    g2: ArcOfCircle CenterX=-1.5 CenterY=62 CenterZ=0 NormalX=0 NormalY=0 NormalZ=1 AngleXU=0 Radius=1.5 StartAngle=4.71239 EndAngle=7.85398
    g3: ArcOfCircle CenterX=-1.5 CenterY=10 CenterZ=0 NormalX=0 NormalY=0 NormalZ=1 AngleXU=0 Radius=1.5 StartAngle=4.71239 EndAngle=7.85398
    g4: LineSegment StartX=-49.19 StartY=63.5 StartZ=0 EndX=-1.5 EndY=63.5 EndZ=0
    g5: LineSegment StartX=-49.19 StartY=60.5 StartZ=0 EndX=-1.5 EndY=60.5 EndZ=0
    g6: LineSegment StartX=-49.19 StartY=11.5 StartZ=0 EndX=-1.5 EndY=11.5 EndZ=0
    g7: LineSegment StartX=-49.19 StartY=8.5 StartZ=0 EndX=-1.5 EndY=8.5 EndZ=0
  constraints (19):
    c: Vertical(g0)
    c: Distance(g0) = 3
    c: Vertical(g1)
    c: Block(g1)
    c: Block(g2)
    c: Block(g3)
    c: Block(g0)
    c: Coincident(g4,g0)
    c: Coincident(g4,g2)
    c: Horizontal(g4)
    c: Coincident(g5,g0)
    c: Coincident(g5,g2)
    c: Horizontal(g5)
    c: Coincident(g6,g1)
    c: Coincident(g6,g3)
    c: Horizontal(g6)
    c: Coincident(g7,g1)
    c: Coincident(g7,g3)
    c: Horizontal(g7)
FEATURE [Part::Extrusion] Extrude068
  Base = -> Sketch077
  Dir = (1,0,0)
  DirMode = 2
  FaceMakerClass = Part::FaceMakerBullseye
  LengthFwd = 10
  LengthRev = 0
  Solid = true
  Symmetric = false
FEATURE [Part::Fillet] Fillet057  label="removeFromtMoreFrontCaseScrewRetainers002"
  Base = -> Extrude068
  Edges = 4 edges r=1.49: [Edge6,Edge11,Edge18,Edge23]
  Placement = pos=(-12,0,0) rot=(0,0,1;0rad)
FEATURE [Sketcher::SketchObject] Sketch078
  FullyConstrained = true
  Placement = pos=(117,19,0) rot=(0.57735,0.57735,0.57735;2.0944rad)
  sketch-geometry (8):
    g0: LineSegment StartX=-49.19 StartY=69.25 StartZ=0 EndX=-49.19 EndY=66.25 EndZ=0
    g1: LineSegment StartX=-49.19 StartY=5.75 StartZ=0 EndX=-49.19 EndY=2.75 EndZ=0
    g2: ArcOfCircle CenterX=-1.5 CenterY=67.75 CenterZ=0 NormalX=0 NormalY=0 NormalZ=1 AngleXU=0 Radius=1.5 StartAngle=4.71239 EndAngle=7.85398
    g3: ArcOfCircle CenterX=-1.5 CenterY=4.25 CenterZ=0 NormalX=0 NormalY=0 NormalZ=1 AngleXU=0 Radius=1.5 StartAngle=4.71239 EndAngle=7.85398
    g4: LineSegment StartX=-49.19 StartY=69.25 StartZ=0 EndX=-1.5 EndY=69.25 EndZ=0
    g5: LineSegment StartX=-49.19 StartY=66.25 StartZ=0 EndX=-1.5 EndY=66.25 EndZ=0
    g6: LineSegment StartX=-49.19 StartY=5.75 StartZ=0 EndX=-1.5 EndY=5.75 EndZ=0
    g7: LineSegment StartX=-49.19 StartY=2.75 StartZ=0 EndX=-1.5 EndY=2.75 EndZ=0
  constraints (19):
    c: Vertical(g0)
    c: Distance(g0) = 3
    c: Block(g0)
    c: Vertical(g1)
    c: Block(g2)
    c: Block(g3)
    c: Block(g1)
    c: Coincident(g4,g0)
    c: Coincident(g4,g2)
    c: Horizontal(g4)
    c: Coincident(g5,g0)
    c: Coincident(g5,g2)
    c: Horizontal(g5)
    c: Coincident(g6,g1)
    c: Coincident(g6,g3)
    c: Horizontal(g6)
    c: Coincident(g7,g1)
    c: Coincident(g7,g3)
    c: Horizontal(g7)
FEATURE [Part::Extrusion] Extrude069
  Base = -> Sketch078
  Dir = (1,0,0)
  DirMode = 2
  FaceMakerClass = Part::FaceMakerBullseye
  LengthFwd = 10
  LengthRev = 0
  Solid = true
  Symmetric = false
FEATURE [Part::Fillet] Fillet058  label="removeFromtMoreFrontCaseScrewRetainers003"
  Base = -> Extrude069
  Edges = 4 edges r=1.49: [Edge6,Edge11,Edge18,Edge23]
  Placement = pos=(-4,0,0) rot=(0,0,1;0rad)
FEATURE [Part::Cut] Cut066
  Base = -> Cut065
  Tool = -> Fillet058
FEATURE [Part::Cut] Cut067  label="screwPillars"
  Base = -> Cut066
  Tool = -> Fillet057
FEATURE [Part::MultiFuse] Fusion143  label="bottom021"
  Shapes = -> [Cut031,Cut063]
FEATURE [Part::Cylinder] Cylinder
  Angle = 360
  AttacherType = Attacher::AttachEngine3D
  Height = 10
  Placement = pos=(20.65,12,4.68) rot=(1,0,0;1.5708rad)
  Radius = 2
FEATURE [Part::Cylinder] Cylinder064
  Angle = 360
  AttacherType = Attacher::AttachEngine3D
  Height = 10
  Placement = pos=(20.65,12,67.38) rot=(1,0,0;1.5708rad)
  Radius = 2
FEATURE [Part::Cylinder] Cylinder065
  Angle = 360
  AttacherType = Attacher::AttachEngine3D
  Height = 10
  Placement = pos=(77.15,12,67.38) rot=(1,0,0;1.5708rad)
  Radius = 2
FEATURE [Part::Cylinder] Cylinder066
  Angle = 360
  AttacherType = Attacher::AttachEngine3D
  Height = 10
  Placement = pos=(77.15,12,4.68) rot=(1,0,0;1.5708rad)
  Radius = 2
FEATURE [Part::MultiFuse] Fusion144  label="removeFromThreadedInsertHousing"
  Shapes = -> [Cylinder065,Cylinder064,Cylinder,Cylinder066]
FEATURE [Part::Cut] Cut068  label="pcbStands001"
  Base = -> Cut064
  Tool = -> Fusion144
FEATURE [Part::MultiFuse] Fusion145
  Shapes = -> [Cut068,Fusion143]
FEATURE [Part::MultiFuse] Fusion146
  Shapes = -> [Fusion145]
FEATURE [Part::MultiFuse] Fusion147  label="bottom022"
  Shapes = -> [Cut067,Fusion146]
FEATURE [Part::MultiFuse] Fusion148  label="casePillars005"
  Shapes = -> [Cut047,Fusion092]
FEATURE [Part::MultiFuse] Fusion149  label="bottom023"
  Shapes = -> [Fusion124,Fusion113,Fusion147]
FEATURE [Part::MultiFuse] Fusion150  label="topBits"
  Shapes = -> [Cut025,Fusion148,Cut030,Fillet034]
FEATURE [Part::Feature] Face149 .. Face152  x4 (patterned run collapsed; names and placements below)
  shape: bbox 3.2 x 1.5 x 2e-07 mm, 1 faces, 0 solids (baked)
FEATURE [Part::Feature] Face153
  shape: bbox 3.6 x 3.2 x 2e-07 mm, 1 faces, 0 solids (baked)
FEATURE [Part::Feature] Face154
  shape: bbox 3.6 x 3.2 x 2e-07 mm, 1 faces, 0 solids (baked)
FEATURE [Sketcher::SketchObject] Sketch079  label="topSketch024"
  FullyConstrained = true
  sketch-geometry (6):
    g0: LineSegment StartX=19 StartY=38 StartZ=0 EndX=117 EndY=38 EndZ=0
    g1: ArcOfCircle CenterX=19 CenterY=19 CenterZ=0 NormalX=0 NormalY=0 NormalZ=1 AngleXU=0 Radius=19 StartAngle=1.5708 EndAngle=3.14159
    g2: LineSegment StartX=117 StartY=38 StartZ=0 EndX=117 EndY=19 EndZ=0
    g3: LineSegment StartX=98 StartY=1.0161e-12 StartZ=0 EndX=5.22862e-06 EndY=1.0161e-12 EndZ=0
    g4: LineSegment StartX=5.22862e-06 StartY=19 StartZ=0 EndX=5.22862e-06 EndY=1.0161e-12 EndZ=0
    g5: ArcOfCircle CenterX=98 CenterY=19 CenterZ=0 NormalX=0 NormalY=0 NormalZ=1 AngleXU=0 Radius=19 StartAngle=4.71239 EndAngle=6.28319
  constraints (16):
    c: Horizontal(g0)
    c: Distance(g0) = 98
    c: Coincident(g1,g0)
    c: Block(g1)
    c: Coincident(g2,g0)
    c: Vertical(g2)
    c: Distance(g2) = 19
    c: Horizontal(g3)
    c: Coincident(g4,g1)
    c: Vertical(g4)
    c: Coincident(g3,g4)
    c: Block(g3)
    c: Coincident(g5,g2)
    c: Coincident(g5,g3)
    c: Block(g0)
    c: Block(g5)
FEATURE [Sketcher::SketchObject] Sketch080  label="topSketch025"
  FullyConstrained = true
  sketch-geometry (6):
    g0: LineSegment StartX=19 StartY=38 StartZ=0 EndX=117 EndY=38 EndZ=0
    g1: ArcOfCircle CenterX=19 CenterY=19 CenterZ=0 NormalX=0 NormalY=0 NormalZ=1 AngleXU=0 Radius=19 StartAngle=1.5708 EndAngle=3.14159
    g2: LineSegment StartX=117 StartY=38 StartZ=0 EndX=117 EndY=19 EndZ=0
    g3: LineSegment StartX=98 StartY=1.0161e-12 StartZ=0 EndX=5.22862e-06 EndY=1.0161e-12 EndZ=0
    g4: LineSegment StartX=5.22862e-06 StartY=19 StartZ=0 EndX=5.22862e-06 EndY=1.0161e-12 EndZ=0
    g5: ArcOfCircle CenterX=98 CenterY=19 CenterZ=0 NormalX=0 NormalY=0 NormalZ=1 AngleXU=0 Radius=19 StartAngle=4.71239 EndAngle=6.28319
  constraints (16):
    c: Horizontal(g0)
    c: Distance(g0) = 98
    c: Coincident(g1,g0)
    c: Block(g1)
    c: Coincident(g2,g0)
    c: Vertical(g2)
    c: Distance(g2) = 19
    c: Horizontal(g3)
    c: Coincident(g4,g1)
    c: Vertical(g4)
    c: Coincident(g3,g4)
    c: Block(g3)
    c: Coincident(g5,g2)
    c: Coincident(g5,g3)
    c: Block(g0)
    c: Block(g5)
FEATURE [Part::Extrusion] Extrude070  label="sideA004"
  Base = -> Sketch080
  Dir = (0,0,1)
  DirMode = 2
  FaceMakerClass = Part::FaceMakerBullseye
  LengthFwd = 3
  LengthRev = 0
  Placement = pos=(0,0,-2.7) rot=(0,0,1;0rad)
  Solid = true
  Symmetric = false
FEATURE [Sketcher::SketchObject] Sketch081
  FullyConstrained = true
  Placement = pos=(117,19,0) rot=(0.57735,0.57735,0.57735;2.0944rad)
  sketch-geometry (8):
    g0: LineSegment StartX=-49.19 StartY=63.5 StartZ=0 EndX=-49.19 EndY=60.5 EndZ=0
    g1: LineSegment StartX=-49.19 StartY=11.5 StartZ=0 EndX=-49.19 EndY=8.5 EndZ=0
    g2: ArcOfCircle CenterX=-1.5 CenterY=62 CenterZ=0 NormalX=0 NormalY=0 NormalZ=1 AngleXU=0 Radius=1.5 StartAngle=4.71239 EndAngle=7.85398
    g3: ArcOfCircle CenterX=-1.5 CenterY=10 CenterZ=0 NormalX=0 NormalY=0 NormalZ=1 AngleXU=0 Radius=1.5 StartAngle=4.71239 EndAngle=7.85398
    g4: LineSegment StartX=-49.19 StartY=63.5 StartZ=0 EndX=-1.5 EndY=63.5 EndZ=0
    g5: LineSegment StartX=-49.19 StartY=60.5 StartZ=0 EndX=-1.5 EndY=60.5 EndZ=0
    g6: LineSegment StartX=-49.19 StartY=11.5 StartZ=0 EndX=-1.5 EndY=11.5 EndZ=0
    g7: LineSegment StartX=-49.19 StartY=8.5 StartZ=0 EndX=-1.5 EndY=8.5 EndZ=0
  constraints (19):
    c: Vertical(g0)
    c: Distance(g0) = 3
    c: Vertical(g1)
    c: Block(g1)
    c: Block(g2)
    c: Block(g3)
    c: Block(g0)
    c: Coincident(g4,g0)
    c: Coincident(g4,g2)
    c: Horizontal(g4)
    c: Coincident(g5,g0)
    c: Coincident(g5,g2)
    c: Horizontal(g5)
    c: Coincident(g6,g1)
    c: Coincident(g6,g3)
    c: Horizontal(g6)
    c: Coincident(g7,g1)
    c: Coincident(g7,g3)
    c: Horizontal(g7)
FEATURE [Part::Extrusion] Extrude071  label="sideB004"
  Base = -> Sketch079
  Dir = (0,0,1)
  DirMode = 2
  FaceMakerClass = Part::FaceMakerBullseye
  LengthFwd = 3
  LengthRev = 0
  Placement = pos=(0,0,71.7) rot=(0,0,1;0rad)
  Solid = true
  Symmetric = false
FEATURE [Part::MultiFuse] Fusion152  label="removeFromBottom004"
  Placement = pos=(2,0,0) rot=(0,0,1;0rad)
  Shapes = -> [Extrude070,Extrude071]
FEATURE [Part::Extrusion] Extrude072
  Base = -> Sketch081
  Dir = (1,0,0)
  DirMode = 2
  FaceMakerClass = Part::FaceMakerBullseye
  LengthFwd = 10
  LengthRev = 0
  Solid = true
  Symmetric = false
FEATURE [Part::Fillet] Fillet059  label="removeFromtMoreFrontCaseScrewRetainers004"
  Base = -> Extrude072
  Edges = 4 edges r=1.49: [Edge6,Edge11,Edge18,Edge23]
  Placement = pos=(-12,0,0) rot=(0,0,1;0rad)
FEATURE [Sketcher::SketchObject] Sketch082
  FullyConstrained = true
  Placement = pos=(117,19,0) rot=(0.57735,0.57735,0.57735;2.0944rad)
  sketch-geometry (8):
    g0: LineSegment StartX=-49.19 StartY=69.25 StartZ=0 EndX=-49.19 EndY=66.25 EndZ=0
    g1: LineSegment StartX=-49.19 StartY=5.75 StartZ=0 EndX=-49.19 EndY=2.75 EndZ=0
    g2: ArcOfCircle CenterX=-1.5 CenterY=67.75 CenterZ=0 NormalX=0 NormalY=0 NormalZ=1 AngleXU=0 Radius=1.5 StartAngle=4.71239 EndAngle=7.85398
    g3: ArcOfCircle CenterX=-1.5 CenterY=4.25 CenterZ=0 NormalX=0 NormalY=0 NormalZ=1 AngleXU=0 Radius=1.5 StartAngle=4.71239 EndAngle=7.85398
    g4: LineSegment StartX=-49.19 StartY=69.25 StartZ=0 EndX=-1.5 EndY=69.25 EndZ=0
    g5: LineSegment StartX=-49.19 StartY=66.25 StartZ=0 EndX=-1.5 EndY=66.25 EndZ=0
    g6: LineSegment StartX=-49.19 StartY=5.75 StartZ=0 EndX=-1.5 EndY=5.75 EndZ=0
    g7: LineSegment StartX=-49.19 StartY=2.75 StartZ=0 EndX=-1.5 EndY=2.75 EndZ=0
  constraints (19):
    c: Vertical(g0)
    c: Distance(g0) = 3
    c: Block(g0)
    c: Vertical(g1)
    c: Block(g2)
    c: Block(g3)
    c: Block(g1)
    c: Coincident(g4,g0)
    c: Coincident(g4,g2)
    c: Horizontal(g4)
    c: Coincident(g5,g0)
    c: Coincident(g5,g2)
    c: Horizontal(g5)
    c: Coincident(g6,g1)
    c: Coincident(g6,g3)
    c: Horizontal(g6)
    c: Coincident(g7,g1)
    c: Coincident(g7,g3)
    c: Horizontal(g7)
FEATURE [Part::Extrusion] Extrude073
  Base = -> Sketch082
  Dir = (1,0,0)
  DirMode = 2
  FaceMakerClass = Part::FaceMakerBullseye
  LengthFwd = 10
  LengthRev = 0
  Solid = true
  Symmetric = false
FEATURE [Part::Fillet] Fillet060  label="removeFromtMoreFrontCaseScrewRetainers005"
  Base = -> Extrude073
  Edges = 4 edges r=1.49: [Edge6,Edge11,Edge18,Edge23]
  Placement = pos=(-4,0,0) rot=(0,0,1;0rad)
FEATURE [Part::Revolution] Revolve163  label="backCaseScrewRetainer004"
  Angle = 360
  Axis = (0,1,0)
  Base = (0,0,0)
  FaceMakerClass = Part::FaceMakerBullseye
  Placement = pos=(12.5,3,62) rot=(0,0,1;0rad)
  Solid = false
  Source = -> Face149
  Symmetric = false
FEATURE [Part::Revolution] Revolve164  label="frontCaseScrewRetainer006"
  Angle = 360
  Axis = (0,1,0)
  Base = (0,0,0)
  FaceMakerClass = Part::FaceMakerBullseye
  Placement = pos=(89.5,3,68.5) rot=(0,0,1;0rad)
  Solid = false
  Source = -> Face151
  Symmetric = false
FEATURE [Part::Revolution] Revolve165  label="frontCaseScrewRetainer007"
  Angle = 360
  Axis = (0,1,0)
  Base = (0,0,0)
  FaceMakerClass = Part::FaceMakerBullseye
  Placement = pos=(89.5,3,3.5) rot=(0,0,1;0rad)
  Solid = false
  Source = -> Face152
  Symmetric = false
FEATURE [Part::Revolution] Revolve166  label="backCaseScrewRetainer005"
  Angle = 360
  Axis = (0,1,0)
  Base = (0,0,0)
  FaceMakerClass = Part::FaceMakerBullseye
  Placement = pos=(12.5,3,10) rot=(0,0,1;0rad)
  Solid = false
  Source = -> Face150
  Symmetric = false
FEATURE [Part::Revolution] Revolve167  label="moreFrontCaseScrewRetainer006"
  Angle = 360
  Axis = (0,1,0)
  Base = (0,0,0)
  FaceMakerClass = Part::FaceMakerBullseye
  Placement = pos=(109.5,4.5,68.5) rot=(0,0,1;0rad)
  Solid = false
  Source = -> Face153
  Symmetric = false
FEATURE [Part::Revolution] Revolve168  label="moreFrontCaseScrewRetainer007"
  Angle = 360
  Axis = (0,1,0)
  Base = (0,0,0)
  FaceMakerClass = Part::FaceMakerBullseye
  Placement = pos=(109.5,4.5,3.5) rot=(0,0,1;0rad)
  Solid = false
  Source = -> Face154
  Symmetric = false
FEATURE [Part::MultiFuse] Fusion151  label="screwRetainers003"
  Shapes = -> [Revolve168,Revolve167,Revolve166,Revolve165,Revolve164,Revolve163]
FEATURE [Part::Cut] Cut069  label="screwRetainers004"
  Base = -> Fusion151
  Tool = -> Fusion152
FEATURE [Part::Cut] Cut070
  Base = -> Cut069
  Tool = -> Fillet060
FEATURE [Part::Cut] Cut071  label="screwPillars001"
  Base = -> Cut070
  Tool = -> Fillet059
FEATURE [Part::MultiFuse] Fusion153  label="bottom024"
  Shapes = -> [Fusion149,Cut071]
FEATURE [Part::Cylinder] Cylinder067
  Angle = 360
  AttacherType = Attacher::AttachEngine3D
  Height = 10
  Placement = pos=(20.65,12,4.68) rot=(1,0,0;1.5708rad)
  Radius = 2
FEATURE [Part::Cylinder] Cylinder068
  Angle = 360
  AttacherType = Attacher::AttachEngine3D
  Height = 10
  Placement = pos=(20.65,12,67.38) rot=(1,0,0;1.5708rad)
  Radius = 2
FEATURE [Part::Cylinder] Cylinder069
  Angle = 360
  AttacherType = Attacher::AttachEngine3D
  Height = 10
  Placement = pos=(77.15,12,67.38) rot=(1,0,0;1.5708rad)
  Radius = 2
FEATURE [Part::Cylinder] Cylinder070
  Angle = 360
  AttacherType = Attacher::AttachEngine3D
  Height = 10
  Placement = pos=(77.15,12,4.68) rot=(1,0,0;1.5708rad)
  Radius = 2
FEATURE [Part::MultiFuse] Fusion154  label="removeFromThreadedInsertHousing001"
  Shapes = -> [Cylinder069,Cylinder068,Cylinder067,Cylinder070]
FEATURE [Part::Cut] Cut072  label="bottom025"
  Base = -> Fusion153
  Tool = -> Fusion154
FEATURE [Image::ImagePlane] ImagePlane
  XSize = 339
  YSize = 72
FEATURE [Sketcher::SketchObject] Sketch083
  FullyConstrained = true
  MapMode = 5
  Support = -> [XY_Plane]
  sketch-geometry (338):
    g0: LineSegment StartX=-151.619 StartY=28.8932 StartZ=0 EndX=-140.819 EndY=28.8932 EndZ=0
    g1: LineSegment StartX=-151.619 StartY=24.0313 StartZ=0 EndX=-151.619 EndY=28.8932 EndZ=0
    g2: LineSegment StartX=-140.819 StartY=17.7713 StartZ=0 EndX=-151.619 EndY=17.7713 EndZ=0
    g3: LineSegment StartX=-151.619 StartY=17.7713 StartZ=0 EndX=-151.619 EndY=22.6313 EndZ=0
    g4: LineSegment StartX=-151.619 StartY=22.6313 StartZ=0 EndX=-145.128 EndY=22.6313 EndZ=0
    g5: LineSegment StartX=-145.128 StartY=24.0313 StartZ=0 EndX=-140.819 EndY=28.8932 EndZ=0
    g6: LineSegment StartX=-145.128 StartY=22.6313 StartZ=0 EndX=-140.819 EndY=17.7713 EndZ=0
    g7: ArcOfCircle CenterX=-155.157 CenterY=23.3323 CenterZ=0 NormalX=0 NormalY=0 NormalZ=1 AngleXU=0 Radius=6.92354 StartAngle=1.03434 EndAngle=5.24885
    g8: ArcOfCircle CenterX=-155.157 CenterY=23.3323 CenterZ=0 NormalX=0 NormalY=0 NormalZ=1 AngleXU=0 Radius=12.6269 StartAngle=1.28675 EndAngle=4.99643
    g9: LineSegment StartX=-151.619 StartY=35.4532 StartZ=0 EndX=-151.619 EndY=29.2832 EndZ=0
    g10: LineSegment StartX=-151.619 StartY=17.3813 StartZ=0 EndX=-151.619 EndY=11.2113 EndZ=0
    g11-g21: Circle x11 (B-spline internal-alignment scaffolding for g22; pole/knot coordinates omitted)
    g22: BSplineCurve PolesCount=11 KnotsCount=9 Degree=3 IsPeriodic=0
    g23-g31: GeomPoint x9 (B-spline internal-alignment scaffolding for g22; pole/knot coordinates omitted)
    g32-g49: Circle x18 (B-spline internal-alignment scaffolding for g50; pole/knot coordinates omitted)
    g50: BSplineCurve PolesCount=18 KnotsCount=16 Degree=3 IsPeriodic=0
    g51-g66: GeomPoint x16 (B-spline internal-alignment scaffolding for g50; pole/knot coordinates omitted)
    g67: LineSegment StartX=-117.124 StartY=30.093 StartZ=0 EndX=-117.603 EndY=26.5272 EndZ=0
    g68: LineSegment StartX=-117.603 StartY=17.8472 StartZ=0 EndX=-117.124 EndY=14.2659 EndZ=0
    g69: Ellipse CenterX=-109.671 CenterY=20.025 CenterZ=0 NormalX=0 NormalY=0 NormalZ=1 MajorRadius=3.34798 MinorRadius=2.71052 AngleXU=-1.56793
    g70: GeomPoint X=-109.666 Y=18.0598 Z=0
    g71: GeomPoint X=-109.677 Y=21.9902 Z=0
    g72: Ellipse CenterX=-109.671 CenterY=20.0123 CenterZ=0 NormalX=0 NormalY=0 NormalZ=1 MajorRadius=6.93002 MinorRadius=6.36273 AngleXU=-3.13976
    g73: GeomPoint X=-112.417 Y=20.0073 Z=0
    g74: GeomPoint X=-106.925 Y=20.0173 Z=0
    g75: Ellipse CenterX=-51.7682 CenterY=20.1463 CenterZ=0 NormalX=0 NormalY=0 NormalZ=1 MajorRadius=3.19279 MinorRadius=2.71052 AngleXU=-1.52774
    g76: GeomPoint X=-51.6955 Y=18.4606 Z=0
    g77: GeomPoint X=-51.8408 Y=21.832 Z=0
    g78: GeomPoint X=-54.5142 Y=20.1413 Z=0
    g79: GeomPoint X=-49.0221 Y=20.1513 Z=0
    g80: Ellipse CenterX=-51.7682 CenterY=20.1463 CenterZ=0 NormalX=0 NormalY=0 NormalZ=1 MajorRadius=6.93002 MinorRadius=6.36273 AngleXU=-3.13976
    g81: Ellipse CenterX=-22.8436 CenterY=20.1783 CenterZ=0 NormalX=0 NormalY=0 NormalZ=1 MajorRadius=3.31512 MinorRadius=2.71052 AngleXU=-1.60214
    g82: GeomPoint X=-22.9034 Y=18.2706 Z=0
    g83: GeomPoint X=-22.7838 Y=22.0861 Z=0
    g84: GeomPoint X=-25.5897 Y=20.1733 Z=0
    g85: GeomPoint X=-20.0976 Y=20.1833 Z=0
    g86: Ellipse CenterX=-22.8436 CenterY=20.1783 CenterZ=0 NormalX=0 NormalY=0 NormalZ=1 MajorRadius=6.93002 MinorRadius=6.36273 AngleXU=-3.13976
    g87: LineSegment StartX=-101.889 StartY=14.1107 StartZ=0 EndX=-97.7455 EndY=14.1107 EndZ=0
    g88: LineSegment StartX=-93.8155 StartY=14.1107 StartZ=0 EndX=-89.6755 EndY=14.1107 EndZ=0
    g89: LineSegment StartX=-85.7455 StartY=14.1107 StartZ=0 EndX=-81.6055 EndY=14.1107 EndZ=0
    g90: LineSegment StartX=-101.889 StartY=14.1107 StartZ=0 EndX=-101.889 EndY=25.9907 EndZ=0
    g91: LineSegment StartX=-101.889 StartY=25.9907 StartZ=0 EndX=-97.8594 EndY=25.9907 EndZ=0
    g92: LineSegment StartX=-97.8594 StartY=25.9907 StartZ=0 EndX=-97.8594 EndY=24.0907 EndZ=0
    g93: LineSegment StartX=-97.7455 StartY=14.1107 StartZ=0 EndX=-97.7455 EndY=19.9107 EndZ=0
    g94: LineSegment StartX=-89.6755 StartY=14.1107 StartZ=0 EndX=-89.6755 EndY=19.9107 EndZ=0
    g95: LineSegment StartX=-93.8155 StartY=14.1107 StartZ=0 EndX=-93.8155 EndY=21.0107 EndZ=0
    g96-g106: Circle x11 (B-spline internal-alignment scaffolding for g107; pole/knot coordinates omitted)
    g107: BSplineCurve PolesCount=11 KnotsCount=9 Degree=3 IsPeriodic=0
    g108-g116: GeomPoint x9 (B-spline internal-alignment scaffolding for g107; pole/knot coordinates omitted)
    g117: BSplineCurve PolesCount=11 KnotsCount=9 Degree=3 IsPeriodic=0
    g118-g125: Circle x8 (B-spline internal-alignment scaffolding for g126; pole/knot coordinates omitted)
    g126: BSplineCurve PolesCount=8 KnotsCount=6 Degree=3 IsPeriodic=0
    g127-g132: GeomPoint x6 (B-spline internal-alignment scaffolding for g126; pole/knot coordinates omitted)
    g133: BSplineCurve PolesCount=8 KnotsCount=6 Degree=3 IsPeriodic=0
    g134: LineSegment StartX=-85.7455 StartY=21.0107 StartZ=0 EndX=-85.7455 EndY=14.1107 EndZ=0
    g135: LineSegment StartX=-80.0879 StartY=14.1107 StartZ=0 EndX=-75.944 EndY=14.1107 EndZ=0
    g136: LineSegment StartX=-72.014 StartY=14.1107 StartZ=0 EndX=-67.874 EndY=14.1107 EndZ=0
    g137: LineSegment StartX=-63.944 StartY=14.1107 StartZ=0 EndX=-59.804 EndY=14.1107 EndZ=0
    g138: LineSegment StartX=-80.0879 StartY=14.1107 StartZ=0 EndX=-80.0879 EndY=25.9907 EndZ=0
    g139: LineSegment StartX=-80.0879 StartY=25.9907 StartZ=0 EndX=-76.0579 EndY=25.9907 EndZ=0
    g140: LineSegment StartX=-76.0579 StartY=25.9907 StartZ=0 EndX=-76.0579 EndY=24.0907 EndZ=0
    g141: LineSegment StartX=-75.944 StartY=14.1107 StartZ=0 EndX=-75.944 EndY=19.9107 EndZ=0
    g142: LineSegment StartX=-67.874 StartY=14.1107 StartZ=0 EndX=-67.874 EndY=19.9107 EndZ=0
    g143: LineSegment StartX=-72.014 StartY=14.1107 StartZ=0 EndX=-72.014 EndY=21.0107 EndZ=0
    g144-g148: Circle x5 (B-spline internal-alignment scaffolding for g149; pole/knot coordinates omitted)
    g149: BSplineCurve PolesCount=11 KnotsCount=9 Degree=3 IsPeriodic=0
    g150-g158: GeomPoint x9 (B-spline internal-alignment scaffolding for g149; pole/knot coordinates omitted)
    g159: BSplineCurve PolesCount=11 KnotsCount=9 Degree=3 IsPeriodic=0
    g160-g167: Circle x8 (B-spline internal-alignment scaffolding for g168; pole/knot coordinates omitted)
    g168: BSplineCurve PolesCount=8 KnotsCount=6 Degree=3 IsPeriodic=0
    g169-g174: GeomPoint x6 (B-spline internal-alignment scaffolding for g168; pole/knot coordinates omitted)
    g175: BSplineCurve PolesCount=8 KnotsCount=6 Degree=3 IsPeriodic=0
    g176: LineSegment StartX=-63.944 StartY=21.0107 StartZ=0 EndX=-63.944 EndY=14.1107 EndZ=0
    g177: LineSegment StartX=-59.804 StartY=14.1107 StartZ=0 EndX=-59.804 EndY=21.5868 EndZ=0
    g178: BSplineCurve PolesCount=4 KnotsCount=2 Degree=3 IsPeriodic=0
    g179: GeomPoint X=-59.804 Y=21.5868 Z=0
    g180: GeomPoint X=-60.2379 Y=24.0907 Z=0
    g181: LineSegment StartX=-81.6055 StartY=14.1107 StartZ=0 EndX=-81.6055 EndY=21.5868 EndZ=0
    g182: LineSegment StartX=-151.619 StartY=24.0313 StartZ=0 EndX=-145.128 EndY=24.0313 EndZ=0
    g183: Circle CenterX=-82.0394 CenterY=24.0907 CenterZ=0 NormalX=0 NormalY=0 NormalZ=1 AngleXU=0 Radius=1
    g184: Circle CenterX=-81.7131 CenterY=23.2736 CenterZ=0 NormalX=0 NormalY=0 NormalZ=1 AngleXU=0 Radius=1
    g185: Circle CenterX=-81.6055 CenterY=21.5868 CenterZ=0 NormalX=0 NormalY=0 NormalZ=1 AngleXU=0 Radius=1
    g186: BSplineCurve PolesCount=3 KnotsCount=2 Degree=2 IsPeriodic=0
    g187: GeomPoint X=-82.0394 Y=24.0907 Z=0
    g188: GeomPoint X=-81.6055 Y=21.5868 Z=0
    g189: Ellipse CenterX=-37.3522 CenterY=19.9515 CenterZ=0 NormalX=0 NormalY=0 NormalZ=1 MajorRadius=2.99755 MinorRadius=2.49 AngleXU=1.5708
    g190: GeomPoint X=-37.3522 Y=21.6203 Z=0
    g191: GeomPoint X=-37.3522 Y=18.2826 Z=0
    g192: ArcOfEllipse CenterX=-38.7647 CenterY=20.06 CenterZ=0 NormalX=0 NormalY=0 NormalZ=1 MajorRadius=6.30025 MinorRadius=5.3849 AngleXU=1.57276 StartAngle=5.50632 EndAngle=10.3035
    g193: GeomPoint X=-38.7711 Y=23.3304 Z=0
    g194: GeomPoint X=-38.7583 Y=16.7895 Z=0
    g195: LineSegment StartX=-34.6109 StartY=14.1107 StartZ=0 EndX=-30.8984 EndY=14.1107 EndZ=0
    g196: LineSegment StartX=-30.8984 StartY=14.1107 StartZ=0 EndX=-30.8984 EndY=31.1784 EndZ=0
    g197: LineSegment StartX=-30.8984 StartY=31.1784 StartZ=0 EndX=-34.9984 EndY=31.1784 EndZ=0
    g198: LineSegment StartX=-34.9984 StartY=24.5602 StartZ=0 EndX=-34.9984 EndY=31.1784 EndZ=0
    g199: LineSegment StartX=-34.6109 StartY=16.0476 StartZ=0 EndX=-34.6109 EndY=14.1107 EndZ=0
    g200: LineSegment StartX=-14.8781 StartY=14.1107 StartZ=0 EndX=-10.5106 EndY=14.1107 EndZ=0
    g201: LineSegment StartX=-14.8781 StartY=14.1107 StartZ=0 EndX=-14.8781 EndY=25.8504 EndZ=0
    g202: LineSegment StartX=-14.8781 StartY=25.8504 StartZ=0 EndX=-10.8534 EndY=25.8504 EndZ=0
    g203: LineSegment StartX=-10.8534 StartY=25.8504 StartZ=0 EndX=-10.8534 EndY=24.0923 EndZ=0
    g204: LineSegment StartX=-10.5106 StartY=14.1107 StartZ=0 EndX=-10.5106 EndY=19.7752 EndZ=0
    g205: LineSegment StartX=-5.96397 StartY=25.9304 StartZ=0 EndX=-5.96397 EndY=22.574 EndZ=0
    g206-g214: Circle x9 (B-spline internal-alignment scaffolding for g215; pole/knot coordinates omitted)
    g215: BSplineCurve PolesCount=9 KnotsCount=7 Degree=3 IsPeriodic=0
    g216-g222: GeomPoint x7 (B-spline internal-alignment scaffolding for g215; pole/knot coordinates omitted)
    g223-g232: Circle x10 (B-spline internal-alignment scaffolding for g233; pole/knot coordinates omitted)
    g233: BSplineCurve PolesCount=10 KnotsCount=8 Degree=3 IsPeriodic=0
    g234-g241: GeomPoint x8 (B-spline internal-alignment scaffolding for g233; pole/knot coordinates omitted)
    g242: LineSegment StartX=-1.58923 StartY=21.0696 StartZ=0 EndX=2.62034 EndY=21.0696 EndZ=0
    g243: LineSegment StartX=-1.55856 StartY=18.7342 StartZ=0 EndX=6.45946 EndY=18.7342 EndZ=0
    g244: LineSegment StartX=5.29231 StartY=17.386 StartZ=0 EndX=5.29231 EndY=14.3674 EndZ=0
    g245-g269: Circle x25 (B-spline internal-alignment scaffolding for g270; pole/knot coordinates omitted)
    g270: BSplineCurve PolesCount=25 KnotsCount=23 Degree=3 IsPeriodic=0
    g271-g293: GeomPoint x23 (B-spline internal-alignment scaffolding for g270; pole/knot coordinates omitted)
    g294-g304: Circle x11 (B-spline internal-alignment scaffolding for g305; pole/knot coordinates omitted)
    g305: BSplineCurve PolesCount=11 KnotsCount=9 Degree=3 IsPeriodic=0
    g306-g314: GeomPoint x9 (B-spline internal-alignment scaffolding for g305; pole/knot coordinates omitted)
    g315-g326: Circle x12 (B-spline internal-alignment scaffolding for g327; pole/knot coordinates omitted)
    g327: BSplineCurve PolesCount=12 KnotsCount=10 Degree=3 IsPeriodic=0
    g328-g337: GeomPoint x10 (B-spline internal-alignment scaffolding for g327; pole/knot coordinates omitted)
  constraints (252):
    c: Coincident(g1,g0)
    c: Horizontal(g0)
    c: Vertical(g1)
    c: Coincident(g2,g3)
    c: Coincident(g3,g4)
    c: Horizontal(g4)
    c: Horizontal(g2)
    c: Vertical(g3)
    c: Block(g1)
    c: Distance(g3) = 4.86
    c: Block(g4)
    c: Distance(g0) = 10.8
    c: Distance(g2) = 10.8
    c: Coincident(g5,g0)
    c: Coincident(g6,g4)
    c: Coincident(g6,g2)
    c: Block(g8)
    c: Block(g7)
    c: Coincident(g9,g8)
    c: Coincident(g9,g7)
    c: Vertical(g9)
    c: Coincident(g10,g7)
    c: Coincident(g10,g8)
    c: Vertical(g10)
    c: Weight(g11) = 1
    c: Equal(g11, g12-g21) x10
    c: InternalAlignment(g11-g21 -> g22) x11
    c: InternalAlignment(g23-g31 -> g22) x9
    c: Block(g22)
    c: Weight(g32) = 1
    c: Equal(g32, g33-g49) x17
    c: InternalAlignment(g32-g49 -> g50) x18
    c: InternalAlignment(g51-g66 -> g50) x16
    c: Block(g50)
    c: Coincident(g67,g50)
    c: Coincident(g67,g22)
    c: Coincident(g68,g22)
    c: Coincident(g68,g50)
    c: InternalAlignment(g70,g69)
    c: InternalAlignment(g71,g69)
    c: Block(g69)
    c: InternalAlignment(g73,g72)
    c: InternalAlignment(g74,g72)
    c: Block(g72)
    c: InternalAlignment(g76,g75)
    c: InternalAlignment(g77,g75)
    c: InternalAlignment(g78,g80)
    c: InternalAlignment(g79,g80)
    c: Block(g80)
    c: Coincident(g75,g80)
    c: Block(g75)
    c: InternalAlignment(g82,g81)
    c: InternalAlignment(g83,g81)
    c: InternalAlignment(g84,g86)
    c: InternalAlignment(g85,g86)
    c: Block(g86)
    c: Coincident(g81,g86)
    c: Block(g81)
    c: Horizontal(g87)
    c: Block(g87)
    c: Horizontal(g88)
    c: Distance(g88) = 4.14
    c: Horizontal(g89)
    c: Equal(g88,g89) = 4.14
    c: Block(g89)
    c: Block(g88)
    c: Coincident(g90,g87)
    c: Vertical(g90)
    c: Distance(g90) = 11.88
    c: Coincident(g91,g90)
    c: Horizontal(g91)
    c: Coincident(g92,g91)
    c: Vertical(g92)
    c: Distance(g91) = 4.03
    c: Distance(g92) = 1.9
    c: Coincident(g93,g87)
    c: Vertical(g93)
    c: Vertical(g94)
    c: Coincident(g94,g88)
    c: Distance(g93) = 5.8
    c: Distance(g94) = 5.8
    c: Vertical(g95)
    c: Coincident(g95,g88)
    c: Distance(g95) = 6.9
    c: Coincident(g107,g92)
    c: Weight(g96) = 1
    c: Equal(g96, g97-g106) x10
    c: InternalAlignment(g96-g106 -> g107) x11
    c: InternalAlignment(g108-g116 -> g107) x9
    c: Block(g107)
    c: Block(g117)
    c: Coincident(g126,g93)
    c: Weight(g118) = 1
    c: Equal(g118, g119-g125) x7
    c: Coincident(g126,g95)
    c: InternalAlignment(g118-g125 -> g126) x8
    c: InternalAlignment(g127-g132 -> g126) x6
    c: Coincident(g133,g94)
    c: Block(g126)
    c: Block(g133)
    c: Coincident(g134,g133)
    c: Coincident(g134,g89)
    c: Vertical(g134)
    c: Horizontal(g135)
    c: Block(g135)
    c: Horizontal(g136)
    c: Equal(g88,g136) = 4.14
    c: Horizontal(g137)
    c: Equal(g136,g137) = 4.14
    c: Block(g137)
    c: Block(g136)
    c: Coincident(g138,g135)
    c: Vertical(g138)
    c: Equal(g90,g138) = 11.88
    c: Coincident(g139,g138)
    c: Horizontal(g139)
    c: Coincident(g140,g139)
    c: Vertical(g140)
    c: Equal(g91,g139) = 4.03
    c: Equal(g92,g140) = 1.9
    c: Coincident(g141,g135)
    c: Vertical(g141)
    c: Vertical(g142)
    c: Coincident(g142,g136)
    c: Equal(g93,g141) = 5.8
    c: Equal(g94,g142) = 5.8
    c: Vertical(g143)
    c: Coincident(g143,g136)
    c: Equal(g95,g143) = 6.9
    c: Coincident(g149,g140)
    c: Equal(g96,g144) = 1
    c: Equal(g144, g145-g148) x4
    c: InternalAlignment(g144-g148 -> g149) x5
    c: InternalAlignment(g150-g158 -> g149) x9
    c: Block(g149)
    c: Block(g159)
    c: Coincident(g168,g141)
    c: Equal(g118,g160) = 1
    c: Equal(g160, g161-g167) x7
    c: Coincident(g168,g143)
    c: InternalAlignment(g160-g167 -> g168) x8
    c: InternalAlignment(g169-g174 -> g168) x6
    c: Coincident(g175,g142)
    c: Block(g168)
    c: Block(g175)
    c: Coincident(g176,g175)
    c: Coincident(g176,g137)
    c: Vertical(g176)
    c: Coincident(g177,g137)
    c: Vertical(g177)
    c: Coincident(g178,g177)
    c: Coincident(g178,g159)
    c: InternalAlignment(g179,g178)
    c: InternalAlignment(g180,g178)
    c: Block(g178)
    c: Vertical(g181)
    c: Coincident(g181,g89)
    c: Block(g5)
    c: Coincident(g182,g1)
    c: Coincident(g182,g5)
    c: Horizontal(g182)
    c: Coincident(g186,g117)
    c: Weight(g183) = 1
    c: Equal(g183,g184)
    c: Equal(g183,g185)
    c: Coincident(g186,g181)
    c: InternalAlignment(g183,g186)
    c: InternalAlignment(g184,g186)
    c: InternalAlignment(g185,g186)
    c: InternalAlignment(g187,g186)
    c: InternalAlignment(g188,g186)
    c: Block(g186)
    c: InternalAlignment(g190,g189)
    c: InternalAlignment(g191,g189)
    c: Block(g189)
    c: InternalAlignment(g193,g192)
    c: InternalAlignment(g194,g192)
    c: Block(g192)
    c: Horizontal(g195)
    c: Block(g195)
    c: Coincident(g196,g195)
    c: Vertical(g196)
    c: Block(g196)
    c: Distance(g195) = 3.71244
    c: Coincident(g197,g196)
    c: Horizontal(g197)
    c: Distance(g197) = 4.1
    c: Coincident(g198,g192)
    c: Coincident(g198,g197)
    c: Vertical(g198)
    c: Block(g198)
    c: Coincident(g199,g192)
    c: Coincident(g199,g195)
    c: Vertical(g199)
    c: Block(g199)
    c: Horizontal(g200)
    c: Block(g200)
    c: Coincident(g201,g200)
    c: Vertical(g201)
    c: Block(g201)
    c: Coincident(g202,g201)
    c: Horizontal(g202)
    c: Block(g202)
    c: Coincident(g203,g202)
    c: Vertical(g203)
    c: Block(g203)
    c: Coincident(g204,g200)
    c: Vertical(g204)
    c: Block(g204)
    c: Coincident(g215,g203)
    c: Weight(g206) = 1
    c: Equal(g206, g207-g214) x8
    c: Coincident(g215,g205)
    c: InternalAlignment(g206-g214 -> g215) x9
    c: InternalAlignment(g216-g222 -> g215) x7
    c: Coincident(g233,g204)
    c: Weight(g223) = 1
    c: Equal(g223, g224-g232) x9
    c: Coincident(g233,g205)
    c: InternalAlignment(g223-g232 -> g233) x10
    c: InternalAlignment(g234-g241 -> g233) x8
    c: Vertical(g205)
    c: Block(g205)
    c: Block(g215)
    c: Block(g233)
    c: Horizontal(g242)
    c: Horizontal(g243)
    c: Block(g242)
    c: Block(g243)
    c: Vertical(g244)
    c: Block(g244)
    c: Coincident(g270,g243)
    c: Weight(g245) = 1
    c: Equal(g245, g246-g269) x24
    c: Coincident(g270,g244)
    c: InternalAlignment(g245-g269 -> g270) x25
    c: InternalAlignment(g271-g293 -> g270) x23
    c: Coincident(g305,g242)
    c: Weight(g294) = 1
    c: Equal(g294, g295-g304) x10
    c: Coincident(g305,g242)
    c: InternalAlignment(g294-g304 -> g305) x11
    c: InternalAlignment(g306-g314 -> g305) x9
    c: Block(g305)
    c: Coincident(g327,g243)
    c: Weight(g315) = 1
    c: Equal(g315, g316-g326) x11
    c: Coincident(g327,g244)
    c: InternalAlignment(g315-g326 -> g327) x12
    c: InternalAlignment(g328-g337 -> g327) x10
    c: Block(g327)
    c: Block(g270)
FEATURE [PartDesign::Body] Body  label="CommodoreLogoAndText"
  Group = -> [Sketch083]
  Origin = -> Origin
FEATURE [Part::Extrusion] Extrude074  label="CommodoreLogoAndText001"
  Base = -> Sketch083
  Dir = (0,0,1)
  DirMode = 2
  FaceMakerClass = Part::FaceMakerBullseye
  LengthFwd = 10
  LengthRev = 0
  Solid = true
  Symmetric = false
FEATURE [Part::FeaturePython] Clone  label="CommodoreLogoAndTextScale"  # Draft clone (typed FeaturePython)
  AttacherType = Attacher::AttachEngine3D
  Fuse = false
  Objects = -> [Extrude074]
  Placement = pos=(111,5.37,-11.6) rot=(0,0,1;0rad)
  Scale = (0.62,0.62,1)
FEATURE [Part::Mirroring] Part__Mirroring  label="CommodoreLogoAndTextScale (Mirror #1)"
  Base = (0,0,0)
  Normal = (1,0,0)
  Placement = pos=(123.576,0,0) rot=(0,0,1;0rad)
  Source = -> Clone
FEATURE [Sketcher::SketchObject] Sketch084
  FullyConstrained = true
  MapMode = 5
  Support = -> [XY_Plane001]
  sketch-geometry (338):
    g0: LineSegment StartX=-151.619 StartY=28.8932 StartZ=0 EndX=-140.819 EndY=28.8932 EndZ=0
    g1: LineSegment StartX=-151.619 StartY=24.0313 StartZ=0 EndX=-151.619 EndY=28.8932 EndZ=0
    g2: LineSegment StartX=-140.819 StartY=17.7713 StartZ=0 EndX=-151.619 EndY=17.7713 EndZ=0
    g3: LineSegment StartX=-151.619 StartY=17.7713 StartZ=0 EndX=-151.619 EndY=22.6313 EndZ=0
    g4: LineSegment StartX=-151.619 StartY=22.6313 StartZ=0 EndX=-145.128 EndY=22.6313 EndZ=0
    g5: LineSegment StartX=-145.128 StartY=24.0313 StartZ=0 EndX=-140.819 EndY=28.8932 EndZ=0
    g6: LineSegment StartX=-145.128 StartY=22.6313 StartZ=0 EndX=-140.819 EndY=17.7713 EndZ=0
    g7: ArcOfCircle CenterX=-155.157 CenterY=23.3323 CenterZ=0 NormalX=0 NormalY=0 NormalZ=1 AngleXU=0 Radius=6.92354 StartAngle=1.03434 EndAngle=5.24885
    g8: ArcOfCircle CenterX=-155.157 CenterY=23.3323 CenterZ=0 NormalX=0 NormalY=0 NormalZ=1 AngleXU=0 Radius=12.6269 StartAngle=1.28675 EndAngle=4.99643
    g9: LineSegment StartX=-151.619 StartY=35.4532 StartZ=0 EndX=-151.619 EndY=29.2832 EndZ=0
    g10: LineSegment StartX=-151.619 StartY=17.3813 StartZ=0 EndX=-151.619 EndY=11.2113 EndZ=0
    g11-g21: Circle x11 (B-spline internal-alignment scaffolding for g22; pole/knot coordinates omitted)
    g22: BSplineCurve PolesCount=11 KnotsCount=9 Degree=3 IsPeriodic=0
    g23-g31: GeomPoint x9 (B-spline internal-alignment scaffolding for g22; pole/knot coordinates omitted)
    g32-g49: Circle x18 (B-spline internal-alignment scaffolding for g50; pole/knot coordinates omitted)
    g50: BSplineCurve PolesCount=18 KnotsCount=16 Degree=3 IsPeriodic=0
    g51-g66: GeomPoint x16 (B-spline internal-alignment scaffolding for g50; pole/knot coordinates omitted)
    g67: LineSegment StartX=-117.124 StartY=30.093 StartZ=0 EndX=-117.603 EndY=26.5272 EndZ=0
    g68: LineSegment StartX=-117.603 StartY=17.8472 StartZ=0 EndX=-117.124 EndY=14.2659 EndZ=0
    g69: Ellipse CenterX=-109.671 CenterY=20.025 CenterZ=0 NormalX=0 NormalY=0 NormalZ=1 MajorRadius=3.34798 MinorRadius=2.71052 AngleXU=-1.56793
    g70: GeomPoint X=-109.666 Y=18.0598 Z=0
    g71: GeomPoint X=-109.677 Y=21.9902 Z=0
    g72: Ellipse CenterX=-109.671 CenterY=20.0123 CenterZ=0 NormalX=0 NormalY=0 NormalZ=1 MajorRadius=6.93002 MinorRadius=6.36273 AngleXU=-3.13976
    g73: GeomPoint X=-112.417 Y=20.0073 Z=0
    g74: GeomPoint X=-106.925 Y=20.0173 Z=0
    g75: Ellipse CenterX=-51.7682 CenterY=20.1463 CenterZ=0 NormalX=0 NormalY=0 NormalZ=1 MajorRadius=3.19279 MinorRadius=2.71052 AngleXU=-1.52774
    g76: GeomPoint X=-51.6955 Y=18.4606 Z=0
    g77: GeomPoint X=-51.8408 Y=21.832 Z=0
    g78: GeomPoint X=-54.5142 Y=20.1413 Z=0
    g79: GeomPoint X=-49.0221 Y=20.1513 Z=0
    g80: Ellipse CenterX=-51.7682 CenterY=20.1463 CenterZ=0 NormalX=0 NormalY=0 NormalZ=1 MajorRadius=6.93002 MinorRadius=6.36273 AngleXU=-3.13976
    g81: Ellipse CenterX=-22.8436 CenterY=20.1783 CenterZ=0 NormalX=0 NormalY=0 NormalZ=1 MajorRadius=3.31512 MinorRadius=2.71052 AngleXU=-1.60214
    g82: GeomPoint X=-22.9034 Y=18.2706 Z=0
    g83: GeomPoint X=-22.7838 Y=22.0861 Z=0
    g84: GeomPoint X=-25.5897 Y=20.1733 Z=0
    g85: GeomPoint X=-20.0976 Y=20.1833 Z=0
    g86: Ellipse CenterX=-22.8436 CenterY=20.1783 CenterZ=0 NormalX=0 NormalY=0 NormalZ=1 MajorRadius=6.93002 MinorRadius=6.36273 AngleXU=-3.13976
    g87: LineSegment StartX=-101.889 StartY=14.1107 StartZ=0 EndX=-97.7455 EndY=14.1107 EndZ=0
    g88: LineSegment StartX=-93.8155 StartY=14.1107 StartZ=0 EndX=-89.6755 EndY=14.1107 EndZ=0
    g89: LineSegment StartX=-85.7455 StartY=14.1107 StartZ=0 EndX=-81.6055 EndY=14.1107 EndZ=0
    g90: LineSegment StartX=-101.889 StartY=14.1107 StartZ=0 EndX=-101.889 EndY=25.9907 EndZ=0
    g91: LineSegment StartX=-101.889 StartY=25.9907 StartZ=0 EndX=-97.8594 EndY=25.9907 EndZ=0
    g92: LineSegment StartX=-97.8594 StartY=25.9907 StartZ=0 EndX=-97.8594 EndY=24.0907 EndZ=0
    g93: LineSegment StartX=-97.7455 StartY=14.1107 StartZ=0 EndX=-97.7455 EndY=19.9107 EndZ=0
    g94: LineSegment StartX=-89.6755 StartY=14.1107 StartZ=0 EndX=-89.6755 EndY=19.9107 EndZ=0
    g95: LineSegment StartX=-93.8155 StartY=14.1107 StartZ=0 EndX=-93.8155 EndY=21.0107 EndZ=0
    g96-g106: Circle x11 (B-spline internal-alignment scaffolding for g107; pole/knot coordinates omitted)
    g107: BSplineCurve PolesCount=11 KnotsCount=9 Degree=3 IsPeriodic=0
    g108-g116: GeomPoint x9 (B-spline internal-alignment scaffolding for g107; pole/knot coordinates omitted)
    g117: BSplineCurve PolesCount=11 KnotsCount=9 Degree=3 IsPeriodic=0
    g118-g125: Circle x8 (B-spline internal-alignment scaffolding for g126; pole/knot coordinates omitted)
    g126: BSplineCurve PolesCount=8 KnotsCount=6 Degree=3 IsPeriodic=0
    g127-g132: GeomPoint x6 (B-spline internal-alignment scaffolding for g126; pole/knot coordinates omitted)
    g133: BSplineCurve PolesCount=8 KnotsCount=6 Degree=3 IsPeriodic=0
    g134: LineSegment StartX=-85.7455 StartY=21.0107 StartZ=0 EndX=-85.7455 EndY=14.1107 EndZ=0
    g135: LineSegment StartX=-80.0879 StartY=14.1107 StartZ=0 EndX=-75.944 EndY=14.1107 EndZ=0
    g136: LineSegment StartX=-72.014 StartY=14.1107 StartZ=0 EndX=-67.874 EndY=14.1107 EndZ=0
    g137: LineSegment StartX=-63.944 StartY=14.1107 StartZ=0 EndX=-59.804 EndY=14.1107 EndZ=0
    g138: LineSegment StartX=-80.0879 StartY=14.1107 StartZ=0 EndX=-80.0879 EndY=25.9907 EndZ=0
    g139: LineSegment StartX=-80.0879 StartY=25.9907 StartZ=0 EndX=-76.0579 EndY=25.9907 EndZ=0
    g140: LineSegment StartX=-76.0579 StartY=25.9907 StartZ=0 EndX=-76.0579 EndY=24.0907 EndZ=0
    g141: LineSegment StartX=-75.944 StartY=14.1107 StartZ=0 EndX=-75.944 EndY=19.9107 EndZ=0
    g142: LineSegment StartX=-67.874 StartY=14.1107 StartZ=0 EndX=-67.874 EndY=19.9107 EndZ=0
    g143: LineSegment StartX=-72.014 StartY=14.1107 StartZ=0 EndX=-72.014 EndY=21.0107 EndZ=0
    g144-g148: Circle x5 (B-spline internal-alignment scaffolding for g149; pole/knot coordinates omitted)
    g149: BSplineCurve PolesCount=11 KnotsCount=9 Degree=3 IsPeriodic=0
    g150-g158: GeomPoint x9 (B-spline internal-alignment scaffolding for g149; pole/knot coordinates omitted)
    g159: BSplineCurve PolesCount=11 KnotsCount=9 Degree=3 IsPeriodic=0
    g160-g167: Circle x8 (B-spline internal-alignment scaffolding for g168; pole/knot coordinates omitted)
    g168: BSplineCurve PolesCount=8 KnotsCount=6 Degree=3 IsPeriodic=0
    g169-g174: GeomPoint x6 (B-spline internal-alignment scaffolding for g168; pole/knot coordinates omitted)
    g175: BSplineCurve PolesCount=8 KnotsCount=6 Degree=3 IsPeriodic=0
    g176: LineSegment StartX=-63.944 StartY=21.0107 StartZ=0 EndX=-63.944 EndY=14.1107 EndZ=0
    g177: LineSegment StartX=-59.804 StartY=14.1107 StartZ=0 EndX=-59.804 EndY=21.5868 EndZ=0
    g178: BSplineCurve PolesCount=4 KnotsCount=2 Degree=3 IsPeriodic=0
    g179: GeomPoint X=-59.804 Y=21.5868 Z=0
    g180: GeomPoint X=-60.2379 Y=24.0907 Z=0
    g181: LineSegment StartX=-81.6055 StartY=14.1107 StartZ=0 EndX=-81.6055 EndY=21.5868 EndZ=0
    g182: LineSegment StartX=-151.619 StartY=24.0313 StartZ=0 EndX=-145.128 EndY=24.0313 EndZ=0
    g183: Circle CenterX=-82.0394 CenterY=24.0907 CenterZ=0 NormalX=0 NormalY=0 NormalZ=1 AngleXU=0 Radius=1
    g184: Circle CenterX=-81.7131 CenterY=23.2736 CenterZ=0 NormalX=0 NormalY=0 NormalZ=1 AngleXU=0 Radius=1
    g185: Circle CenterX=-81.6055 CenterY=21.5868 CenterZ=0 NormalX=0 NormalY=0 NormalZ=1 AngleXU=0 Radius=1
    g186: BSplineCurve PolesCount=3 KnotsCount=2 Degree=2 IsPeriodic=0
    g187: GeomPoint X=-82.0394 Y=24.0907 Z=0
    g188: GeomPoint X=-81.6055 Y=21.5868 Z=0
    g189: Ellipse CenterX=-37.3522 CenterY=19.9515 CenterZ=0 NormalX=0 NormalY=0 NormalZ=1 MajorRadius=2.99755 MinorRadius=2.49 AngleXU=1.5708
    g190: GeomPoint X=-37.3522 Y=21.6203 Z=0
    g191: GeomPoint X=-37.3522 Y=18.2826 Z=0
    g192: ArcOfEllipse CenterX=-38.7647 CenterY=20.06 CenterZ=0 NormalX=0 NormalY=0 NormalZ=1 MajorRadius=6.30025 MinorRadius=5.3849 AngleXU=1.57276 StartAngle=5.50632 EndAngle=10.3035
    g193: GeomPoint X=-38.7711 Y=23.3304 Z=0
    g194: GeomPoint X=-38.7583 Y=16.7895 Z=0
    g195: LineSegment StartX=-34.6109 StartY=14.1107 StartZ=0 EndX=-30.8984 EndY=14.1107 EndZ=0
    g196: LineSegment StartX=-30.8984 StartY=14.1107 StartZ=0 EndX=-30.8984 EndY=31.1784 EndZ=0
    g197: LineSegment StartX=-30.8984 StartY=31.1784 StartZ=0 EndX=-34.9984 EndY=31.1784 EndZ=0
    g198: LineSegment StartX=-34.9984 StartY=24.5602 StartZ=0 EndX=-34.9984 EndY=31.1784 EndZ=0
    g199: LineSegment StartX=-34.6109 StartY=16.0476 StartZ=0 EndX=-34.6109 EndY=14.1107 EndZ=0
    g200: LineSegment StartX=-14.8781 StartY=14.1107 StartZ=0 EndX=-10.5106 EndY=14.1107 EndZ=0
    g201: LineSegment StartX=-14.8781 StartY=14.1107 StartZ=0 EndX=-14.8781 EndY=25.8504 EndZ=0
    g202: LineSegment StartX=-14.8781 StartY=25.8504 StartZ=0 EndX=-10.8534 EndY=25.8504 EndZ=0
    g203: LineSegment StartX=-10.8534 StartY=25.8504 StartZ=0 EndX=-10.8534 EndY=24.0923 EndZ=0
    g204: LineSegment StartX=-10.5106 StartY=14.1107 StartZ=0 EndX=-10.5106 EndY=19.7752 EndZ=0
    g205: LineSegment StartX=-5.96397 StartY=25.9304 StartZ=0 EndX=-5.96397 EndY=22.574 EndZ=0
    g206-g214: Circle x9 (B-spline internal-alignment scaffolding for g215; pole/knot coordinates omitted)
    g215: BSplineCurve PolesCount=9 KnotsCount=7 Degree=3 IsPeriodic=0
    g216-g222: GeomPoint x7 (B-spline internal-alignment scaffolding for g215; pole/knot coordinates omitted)
    g223-g232: Circle x10 (B-spline internal-alignment scaffolding for g233; pole/knot coordinates omitted)
    g233: BSplineCurve PolesCount=10 KnotsCount=8 Degree=3 IsPeriodic=0
    g234-g241: GeomPoint x8 (B-spline internal-alignment scaffolding for g233; pole/knot coordinates omitted)
    g242: LineSegment StartX=-1.58923 StartY=21.0696 StartZ=0 EndX=2.62034 EndY=21.0696 EndZ=0
    g243: LineSegment StartX=-1.55856 StartY=18.7342 StartZ=0 EndX=6.45946 EndY=18.7342 EndZ=0
    g244: LineSegment StartX=5.29231 StartY=17.386 StartZ=0 EndX=5.29231 EndY=14.3674 EndZ=0
    g245-g269: Circle x25 (B-spline internal-alignment scaffolding for g270; pole/knot coordinates omitted)
    g270: BSplineCurve PolesCount=25 KnotsCount=23 Degree=3 IsPeriodic=0
    g271-g293: GeomPoint x23 (B-spline internal-alignment scaffolding for g270; pole/knot coordinates omitted)
    g294-g304: Circle x11 (B-spline internal-alignment scaffolding for g305; pole/knot coordinates omitted)
    g305: BSplineCurve PolesCount=11 KnotsCount=9 Degree=3 IsPeriodic=0
    g306-g314: GeomPoint x9 (B-spline internal-alignment scaffolding for g305; pole/knot coordinates omitted)
    g315-g326: Circle x12 (B-spline internal-alignment scaffolding for g327; pole/knot coordinates omitted)
    g327: BSplineCurve PolesCount=12 KnotsCount=10 Degree=3 IsPeriodic=0
    g328-g337: GeomPoint x10 (B-spline internal-alignment scaffolding for g327; pole/knot coordinates omitted)
  constraints (252):
    c: Coincident(g1,g0)
    c: Horizontal(g0)
    c: Vertical(g1)
    c: Coincident(g2,g3)
    c: Coincident(g3,g4)
    c: Horizontal(g4)
    c: Horizontal(g2)
    c: Vertical(g3)
    c: Block(g1)
    c: Distance(g3) = 4.86
    c: Block(g4)
    c: Distance(g0) = 10.8
    c: Distance(g2) = 10.8
    c: Coincident(g5,g0)
    c: Coincident(g6,g4)
    c: Coincident(g6,g2)
    c: Block(g8)
    c: Block(g7)
    c: Coincident(g9,g8)
    c: Coincident(g9,g7)
    c: Vertical(g9)
    c: Coincident(g10,g7)
    c: Coincident(g10,g8)
    c: Vertical(g10)
    c: Weight(g11) = 1
    c: Equal(g11, g12-g21) x10
    c: InternalAlignment(g11-g21 -> g22) x11
    c: InternalAlignment(g23-g31 -> g22) x9
    c: Block(g22)
    c: Weight(g32) = 1
    c: Equal(g32, g33-g49) x17
    c: InternalAlignment(g32-g49 -> g50) x18
    c: InternalAlignment(g51-g66 -> g50) x16
    c: Block(g50)
    c: Coincident(g67,g50)
    c: Coincident(g67,g22)
    c: Coincident(g68,g22)
    c: Coincident(g68,g50)
    c: InternalAlignment(g70,g69)
    c: InternalAlignment(g71,g69)
    c: Block(g69)
    c: InternalAlignment(g73,g72)
    c: InternalAlignment(g74,g72)
    c: Block(g72)
    c: InternalAlignment(g76,g75)
    c: InternalAlignment(g77,g75)
    c: InternalAlignment(g78,g80)
    c: InternalAlignment(g79,g80)
    c: Block(g80)
    c: Coincident(g75,g80)
    c: Block(g75)
    c: InternalAlignment(g82,g81)
    c: InternalAlignment(g83,g81)
    c: InternalAlignment(g84,g86)
    c: InternalAlignment(g85,g86)
    c: Block(g86)
    c: Coincident(g81,g86)
    c: Block(g81)
    c: Horizontal(g87)
    c: Block(g87)
    c: Horizontal(g88)
    c: Distance(g88) = 4.14
    c: Horizontal(g89)
    c: Equal(g88,g89) = 4.14
    c: Block(g89)
    c: Block(g88)
    c: Coincident(g90,g87)
    c: Vertical(g90)
    c: Distance(g90) = 11.88
    c: Coincident(g91,g90)
    c: Horizontal(g91)
    c: Coincident(g92,g91)
    c: Vertical(g92)
    c: Distance(g91) = 4.03
    c: Distance(g92) = 1.9
    c: Coincident(g93,g87)
    c: Vertical(g93)
    c: Vertical(g94)
    c: Coincident(g94,g88)
    c: Distance(g93) = 5.8
    c: Distance(g94) = 5.8
    c: Vertical(g95)
    c: Coincident(g95,g88)
    c: Distance(g95) = 6.9
    c: Coincident(g107,g92)
    c: Weight(g96) = 1
    c: Equal(g96, g97-g106) x10
    c: InternalAlignment(g96-g106 -> g107) x11
    c: InternalAlignment(g108-g116 -> g107) x9
    c: Block(g107)
    c: Block(g117)
    c: Coincident(g126,g93)
    c: Weight(g118) = 1
    c: Equal(g118, g119-g125) x7
    c: Coincident(g126,g95)
    c: InternalAlignment(g118-g125 -> g126) x8
    c: InternalAlignment(g127-g132 -> g126) x6
    c: Coincident(g133,g94)
    c: Block(g126)
    c: Block(g133)
    c: Coincident(g134,g133)
    c: Coincident(g134,g89)
    c: Vertical(g134)
    c: Horizontal(g135)
    c: Block(g135)
    c: Horizontal(g136)
    c: Equal(g88,g136) = 4.14
    c: Horizontal(g137)
    c: Equal(g136,g137) = 4.14
    c: Block(g137)
    c: Block(g136)
    c: Coincident(g138,g135)
    c: Vertical(g138)
    c: Equal(g90,g138) = 11.88
    c: Coincident(g139,g138)
    c: Horizontal(g139)
    c: Coincident(g140,g139)
    c: Vertical(g140)
    c: Equal(g91,g139) = 4.03
    c: Equal(g92,g140) = 1.9
    c: Coincident(g141,g135)
    c: Vertical(g141)
    c: Vertical(g142)
    c: Coincident(g142,g136)
    c: Equal(g93,g141) = 5.8
    c: Equal(g94,g142) = 5.8
    c: Vertical(g143)
    c: Coincident(g143,g136)
    c: Equal(g95,g143) = 6.9
    c: Coincident(g149,g140)
    c: Equal(g96,g144) = 1
    c: Equal(g144, g145-g148) x4
    c: InternalAlignment(g144-g148 -> g149) x5
    c: InternalAlignment(g150-g158 -> g149) x9
    c: Block(g149)
    c: Block(g159)
    c: Coincident(g168,g141)
    c: Equal(g118,g160) = 1
    c: Equal(g160, g161-g167) x7
    c: Coincident(g168,g143)
    c: InternalAlignment(g160-g167 -> g168) x8
    c: InternalAlignment(g169-g174 -> g168) x6
    c: Coincident(g175,g142)
    c: Block(g168)
    c: Block(g175)
    c: Coincident(g176,g175)
    c: Coincident(g176,g137)
    c: Vertical(g176)
    c: Coincident(g177,g137)
    c: Vertical(g177)
    c: Coincident(g178,g177)
    c: Coincident(g178,g159)
    c: InternalAlignment(g179,g178)
    c: InternalAlignment(g180,g178)
    c: Block(g178)
    c: Vertical(g181)
    c: Coincident(g181,g89)
    c: Block(g5)
    c: Coincident(g182,g1)
    c: Coincident(g182,g5)
    c: Horizontal(g182)
    c: Coincident(g186,g117)
    c: Weight(g183) = 1
    c: Equal(g183,g184)
    c: Equal(g183,g185)
    c: Coincident(g186,g181)
    c: InternalAlignment(g183,g186)
    c: InternalAlignment(g184,g186)
    c: InternalAlignment(g185,g186)
    c: InternalAlignment(g187,g186)
    c: InternalAlignment(g188,g186)
    c: Block(g186)
    c: InternalAlignment(g190,g189)
    c: InternalAlignment(g191,g189)
    c: Block(g189)
    c: InternalAlignment(g193,g192)
    c: InternalAlignment(g194,g192)
    c: Block(g192)
    c: Horizontal(g195)
    c: Block(g195)
    c: Coincident(g196,g195)
    c: Vertical(g196)
    c: Block(g196)
    c: Distance(g195) = 3.71244
    c: Coincident(g197,g196)
    c: Horizontal(g197)
    c: Distance(g197) = 4.1
    c: Coincident(g198,g192)
    c: Coincident(g198,g197)
    c: Vertical(g198)
    c: Block(g198)
    c: Coincident(g199,g192)
    c: Coincident(g199,g195)
    c: Vertical(g199)
    c: Block(g199)
    c: Horizontal(g200)
    c: Block(g200)
    c: Coincident(g201,g200)
    c: Vertical(g201)
    c: Block(g201)
    c: Coincident(g202,g201)
    c: Horizontal(g202)
    c: Block(g202)
    c: Coincident(g203,g202)
    c: Vertical(g203)
    c: Block(g203)
    c: Coincident(g204,g200)
    c: Vertical(g204)
    c: Block(g204)
    c: Coincident(g215,g203)
    c: Weight(g206) = 1
    c: Equal(g206, g207-g214) x8
    c: Coincident(g215,g205)
    c: InternalAlignment(g206-g214 -> g215) x9
    c: InternalAlignment(g216-g222 -> g215) x7
    c: Coincident(g233,g204)
    c: Weight(g223) = 1
    c: Equal(g223, g224-g232) x9
    c: Coincident(g233,g205)
    c: InternalAlignment(g223-g232 -> g233) x10
    c: InternalAlignment(g234-g241 -> g233) x8
    c: Vertical(g205)
    c: Block(g205)
    c: Block(g215)
    c: Block(g233)
    c: Horizontal(g242)
    c: Horizontal(g243)
    c: Block(g242)
    c: Block(g243)
    c: Vertical(g244)
    c: Block(g244)
    c: Coincident(g270,g243)
    c: Weight(g245) = 1
    c: Equal(g245, g246-g269) x24
    c: Coincident(g270,g244)
    c: InternalAlignment(g245-g269 -> g270) x25
    c: InternalAlignment(g271-g293 -> g270) x23
    c: Coincident(g305,g242)
    c: Weight(g294) = 1
    c: Equal(g294, g295-g304) x10
    c: Coincident(g305,g242)
    c: InternalAlignment(g294-g304 -> g305) x11
    c: InternalAlignment(g306-g314 -> g305) x9
    c: Block(g305)
    c: Coincident(g327,g243)
    c: Weight(g315) = 1
    c: Equal(g315, g316-g326) x11
    c: Coincident(g327,g244)
    c: InternalAlignment(g315-g326 -> g327) x12
    c: InternalAlignment(g328-g337 -> g327) x10
    c: Block(g327)
    c: Block(g270)
FEATURE [Part::Extrusion] Extrude075  label="CommodoreLogoAndText002"
  Base = -> Sketch084
  Dir = (0,0,1)
  DirMode = 2
  FaceMakerClass = Part::FaceMakerBullseye
  LengthFwd = 10
  LengthRev = 0
  Solid = true
  Symmetric = false
FEATURE [Part::FeaturePython] Clone001  label="CommodoreLogoAndTextScale001"  # Draft clone (typed FeaturePython)
  AttacherType = Attacher::AttachEngine3D
  Fuse = false
  Objects = -> [Extrude075]
  Placement = pos=(112.566,5.37,73.6) rot=(0,0,1;0rad)
  Scale = (0.62,0.62,1)
FEATURE [Part::Cut] Cut073  label="sideA005"
  Base = -> Extrude002
  Tool = -> Part__Mirroring
FEATURE [Part::Cut] Cut074  label="sideB005"
  Base = -> Extrude028
  Tool = -> Clone001
FEATURE [Sketcher::SketchObject] Sketch085
  FullyConstrained = true
  Placement = pos=(0,0,0) rot=(1,0,0;1.5708rad)
  sketch-geometry (10):
    g0: LineSegment StartX=0 StartY=0 StartZ=0 EndX=-7 EndY=0 EndZ=0
    g1: LineSegment StartX=-7 StartY=10 StartZ=0 EndX=-6.5 EndY=10 EndZ=0
    g2: LineSegment StartX=0 StartY=10 StartZ=0 EndX=-0.5 EndY=10 EndZ=0
    g3: ArcOfCircle CenterX=-3.5 CenterY=10 CenterZ=0 NormalX=0 NormalY=0 NormalZ=1 AngleXU=0 Radius=3 StartAngle=3.14159 EndAngle=6.28319
    g4: LineSegment StartX=-7 StartY=0 StartZ=0 EndX=-10.5 EndY=0 EndZ=0
    g5: LineSegment StartX=0 StartY=0 StartZ=0 EndX=3.5 EndY=0 EndZ=0
    g6: ArcOfCircle CenterX=-10.5 CenterY=3.5 CenterZ=0 NormalX=0 NormalY=0 NormalZ=1 AngleXU=0 Radius=3.5 StartAngle=4.71239 EndAngle=6.28319
    g7: ArcOfCircle CenterX=3.5 CenterY=3.5 CenterZ=0 NormalX=0 NormalY=0 NormalZ=1 AngleXU=0 Radius=3.5 StartAngle=3.14159 EndAngle=4.71239
    g8: LineSegment StartX=-7 StartY=3.5 StartZ=0 EndX=-7 EndY=10 EndZ=0
    g9: LineSegment StartX=0 StartY=10 StartZ=0 EndX=0 EndY=3.5 EndZ=0
  constraints (26):
    c: Coincident(g0,g-1)
    c: Horizontal(g0)
    c: Distance(g0) = 7
    c: Horizontal(g1)
    c: Distance(g1) = 0.5
    c: Horizontal(g2)
    c: Distance(g2) = 0.5
    c: Coincident(g3,g1)
    c: Coincident(g3,g2)
    c: Block(g3)
    c: Coincident(g4,g0)
    c: Horizontal(g4)
    c: Distance(g4) = 3.5
    c: Coincident(g5,g0)
    c: Distance(g5) = 3.5
    c: Horizontal(g5)
    c: Coincident(g6,g4)
    c: Block(g6)
    c: Coincident(g7,g5)
    c: Block(g7)
    c: Coincident(g8,g6)
    c: Coincident(g8,g1)
    c: Vertical(g8)
    c: Coincident(g9,g2)
    c: Coincident(g9,g7)
    c: Vertical(g9)
FEATURE [Part::Extrusion] Extrude076  label="backRightCasePillarSideBracket"
  Base = -> Sketch085
  Dir = (0,-1,3e-16)
  DirMode = 2
  FaceMakerClass = Part::FaceMakerBullseye
  LengthFwd = 6.7
  LengthRev = 0
  Placement = pos=(16,11.5,0) rot=(0,0,1;0rad)
  Solid = true
  Symmetric = false
FEATURE [Sketcher::SketchObject] Sketch086
  FullyConstrained = true
  Placement = pos=(0,0,0) rot=(1,0,0;1.5708rad)
  sketch-geometry (10):
    g0: LineSegment StartX=0 StartY=0 StartZ=0 EndX=-7 EndY=0 EndZ=0
    g1: LineSegment StartX=-7 StartY=10 StartZ=0 EndX=-6.5 EndY=10 EndZ=0
    g2: LineSegment StartX=0 StartY=10 StartZ=0 EndX=-0.5 EndY=10 EndZ=0
    g3: ArcOfCircle CenterX=-3.5 CenterY=10 CenterZ=0 NormalX=0 NormalY=0 NormalZ=1 AngleXU=0 Radius=3 StartAngle=3.14159 EndAngle=6.28319
    g4: LineSegment StartX=-7 StartY=0 StartZ=0 EndX=-10.5 EndY=0 EndZ=0
    g5: LineSegment StartX=0 StartY=0 StartZ=0 EndX=3.5 EndY=0 EndZ=0
    g6: ArcOfCircle CenterX=-10.5 CenterY=3.5 CenterZ=0 NormalX=0 NormalY=0 NormalZ=1 AngleXU=0 Radius=3.5 StartAngle=4.71239 EndAngle=6.28319
    g7: ArcOfCircle CenterX=3.5 CenterY=3.5 CenterZ=0 NormalX=0 NormalY=0 NormalZ=1 AngleXU=0 Radius=3.5 StartAngle=3.14159 EndAngle=4.71239
    g8: LineSegment StartX=-7 StartY=3.5 StartZ=0 EndX=-7 EndY=10 EndZ=0
    g9: LineSegment StartX=0 StartY=10 StartZ=0 EndX=0 EndY=3.5 EndZ=0
  constraints (26):
    c: Coincident(g0,g-1)
    c: Horizontal(g0)
    c: Distance(g0) = 7
    c: Horizontal(g1)
    c: Distance(g1) = 0.5
    c: Horizontal(g2)
    c: Distance(g2) = 0.5
    c: Coincident(g3,g1)
    c: Coincident(g3,g2)
    c: Block(g3)
    c: Coincident(g4,g0)
    c: Horizontal(g4)
    c: Distance(g4) = 3.5
    c: Coincident(g5,g0)
    c: Distance(g5) = 3.5
    c: Horizontal(g5)
    c: Coincident(g6,g4)
    c: Block(g6)
    c: Coincident(g7,g5)
    c: Block(g7)
    c: Coincident(g8,g6)
    c: Coincident(g8,g1)
    c: Vertical(g8)
    c: Coincident(g9,g2)
    c: Coincident(g9,g7)
    c: Vertical(g9)
FEATURE [Part::Extrusion] Extrude077  label="backLeftCasePillarSideBracket001"
  Base = -> Sketch086
  Dir = (0,-1,3e-16)
  DirMode = 2
  FaceMakerClass = Part::FaceMakerBullseye
  LengthFwd = 6.7
  LengthRev = 0
  Placement = pos=(9,11.5,72) rot=(0,1,0;3.14159rad)
  Solid = true
  Symmetric = false
FEATURE [Sketcher::SketchObject] Sketch087
  FullyConstrained = true
  Placement = pos=(0,0,0) rot=(1,0,0;1.5708rad)
  sketch-geometry (8):
    g0: LineSegment StartX=0 StartY=4e-16 StartZ=0 EndX=-7 EndY=4e-16 EndZ=0
    g1: LineSegment StartX=-7 StartY=4e-16 StartZ=0 EndX=-10.5 EndY=4e-16 EndZ=0
    g2: LineSegment StartX=0 StartY=4e-16 StartZ=0 EndX=3.5 EndY=4e-16 EndZ=0
    g3: ArcOfCircle CenterX=-10.5 CenterY=3.5 CenterZ=0 NormalX=0 NormalY=0 NormalZ=1 AngleXU=0 Radius=3.5 StartAngle=4.71239 EndAngle=6.28319
    g4: ArcOfCircle CenterX=3.5 CenterY=3.5 CenterZ=0 NormalX=0 NormalY=0 NormalZ=1 AngleXU=0 Radius=3.5 StartAngle=3.14159 EndAngle=4.71239
    g5: ArcOfCircle CenterX=-3.5 CenterY=3.5 CenterZ=0 NormalX=0 NormalY=0 NormalZ=1 AngleXU=0 Radius=3 StartAngle=3.14159 EndAngle=6.28319
    g6: LineSegment StartX=-7 StartY=3.5 StartZ=0 EndX=-6.5 EndY=3.5 EndZ=0
    g7: LineSegment StartX=-0.5 StartY=3.5 StartZ=0 EndX=0 EndY=3.5 EndZ=0
  constraints (20):
    c: Coincident(g0,g-1)
    c: Horizontal(g0)
    c: Distance(g0) = 7
    c: Coincident(g1,g0)
    c: Horizontal(g1)
    c: Distance(g1) = 3.5
    c: Coincident(g2,g0)
    c: Distance(g2) = 3.5
    c: Horizontal(g2)
    c: Coincident(g3,g1)
    c: Block(g3)
    c: Coincident(g4,g2)
    c: Block(g4)
    c: Horizontal(g6)
    c: Coincident(g5,g6)
    c: Block(g5)
    c: Coincident(g6,g3)
    c: Coincident(g7,g5)
    c: Coincident(g7,g4)
    c: Horizontal(g7)
FEATURE [Part::Extrusion] Extrude078  label="frontBackLeftCasePillarSideBracket001"
  Base = -> Sketch087
  Dir = (0,-1,2e-16)
  DirMode = 2
  FaceMakerClass = Part::FaceMakerBullseye
  LengthFwd = 6.7
  LengthRev = 0
  Placement = pos=(93,11.5,0) rot=(0,0,1;0rad)
  Solid = true
  Symmetric = false
FEATURE [Sketcher::SketchObject] Sketch088
  FullyConstrained = true
  Placement = pos=(0,0,0) rot=(1,0,0;1.5708rad)
  sketch-geometry (8):
    g0: LineSegment StartX=0 StartY=4e-16 StartZ=0 EndX=-7 EndY=4e-16 EndZ=0
    g1: LineSegment StartX=-7 StartY=4e-16 StartZ=0 EndX=-10.5 EndY=4e-16 EndZ=0
    g2: LineSegment StartX=0 StartY=4e-16 StartZ=0 EndX=3.5 EndY=4e-16 EndZ=0
    g3: ArcOfCircle CenterX=-10.5 CenterY=3.5 CenterZ=0 NormalX=0 NormalY=0 NormalZ=1 AngleXU=0 Radius=3.5 StartAngle=4.71239 EndAngle=6.28319
    g4: ArcOfCircle CenterX=3.5 CenterY=3.5 CenterZ=0 NormalX=0 NormalY=0 NormalZ=1 AngleXU=0 Radius=3.5 StartAngle=3.14159 EndAngle=4.71239
    g5: ArcOfCircle CenterX=-3.5 CenterY=3.5 CenterZ=0 NormalX=0 NormalY=0 NormalZ=1 AngleXU=0 Radius=3 StartAngle=3.14159 EndAngle=6.28319
    g6: LineSegment StartX=-7 StartY=3.5 StartZ=0 EndX=-6.5 EndY=3.5 EndZ=0
    g7: LineSegment StartX=-0.5 StartY=3.5 StartZ=0 EndX=0 EndY=3.5 EndZ=0
  constraints (20):
    c: Coincident(g0,g-1)
    c: Horizontal(g0)
    c: Distance(g0) = 7
    c: Coincident(g1,g0)
    c: Horizontal(g1)
    c: Distance(g1) = 3.5
    c: Coincident(g2,g0)
    c: Distance(g2) = 3.5
    c: Horizontal(g2)
    c: Coincident(g3,g1)
    c: Block(g3)
    c: Coincident(g4,g2)
    c: Block(g4)
    c: Horizontal(g6)
    c: Coincident(g5,g6)
    c: Block(g5)
    c: Coincident(g6,g3)
    c: Coincident(g7,g5)
    c: Coincident(g7,g4)
    c: Horizontal(g7)
FEATURE [Part::Extrusion] Extrude079  label="frontFrontRightCasePillarSideBracket002"
  Base = -> Sketch088
  Dir = (0,-1,2e-16)
  DirMode = 2
  FaceMakerClass = Part::FaceMakerBullseye
  LengthFwd = 2
  LengthRev = 0
  Placement = pos=(106,11.5,72) rot=(0,1,0;3.14159rad)
  Solid = true
  Symmetric = false
FEATURE [Part::Chamfer] Chamfer
  Base = -> Extrude076
  Edges = 1 edges r=3: [Edge19]
FEATURE [Part::Chamfer] Chamfer002
  Base = -> Extrude077
  Edges = 1 edges r=3: [Edge7]
FEATURE [Part::Chamfer] Chamfer003  label="backLeftCasePillarSideBracket002"
  Base = -> Chamfer002
  Edges = 1 edges r=3.8: [Edge29]
FEATURE [Part::Chamfer] Chamfer004  label="backRightCasePillarSideBracket001"
  Base = -> Chamfer
  Edges = 1 edges r=3.8: [Edge24]
FEATURE [Sketcher::SketchObject] Sketch089
  FullyConstrained = true
  Placement = pos=(0,0,0) rot=(1,0,0;1.5708rad)
  sketch-geometry (8):
    g0: LineSegment StartX=0 StartY=4e-16 StartZ=0 EndX=-7 EndY=4e-16 EndZ=0
    g1: LineSegment StartX=-7 StartY=4e-16 StartZ=0 EndX=-10.5 EndY=4e-16 EndZ=0
    g2: LineSegment StartX=0 StartY=4e-16 StartZ=0 EndX=3.5 EndY=4e-16 EndZ=0
    g3: ArcOfCircle CenterX=-10.5 CenterY=3.5 CenterZ=0 NormalX=0 NormalY=0 NormalZ=1 AngleXU=0 Radius=3.5 StartAngle=4.71239 EndAngle=6.28319
    g4: ArcOfCircle CenterX=3.5 CenterY=3.5 CenterZ=0 NormalX=0 NormalY=0 NormalZ=1 AngleXU=0 Radius=3.5 StartAngle=3.14159 EndAngle=4.71239
    g5: ArcOfCircle CenterX=-3.5 CenterY=3.5 CenterZ=0 NormalX=0 NormalY=0 NormalZ=1 AngleXU=0 Radius=3 StartAngle=3.14159 EndAngle=6.28319
    g6: LineSegment StartX=-7 StartY=3.5 StartZ=0 EndX=-6.5 EndY=3.5 EndZ=0
    g7: LineSegment StartX=-0.5 StartY=3.5 StartZ=0 EndX=0 EndY=3.5 EndZ=0
  constraints (20):
    c: Coincident(g0,g-1)
    c: Horizontal(g0)
    c: Distance(g0) = 7
    c: Coincident(g1,g0)
    c: Horizontal(g1)
    c: Distance(g1) = 3.5
    c: Coincident(g2,g0)
    c: Distance(g2) = 3.5
    c: Horizontal(g2)
    c: Coincident(g3,g1)
    c: Block(g3)
    c: Coincident(g4,g2)
    c: Block(g4)
    c: Horizontal(g6)
    c: Coincident(g5,g6)
    c: Block(g5)
    c: Coincident(g6,g3)
    c: Coincident(g7,g5)
    c: Coincident(g7,g4)
    c: Horizontal(g7)
FEATURE [Part::Extrusion] Extrude080  label="frontBackLeftCasePillarSideBracket002"
  Base = -> Sketch089
  Dir = (0,-1,2e-16)
  DirMode = 2
  FaceMakerClass = Part::FaceMakerBullseye
  LengthFwd = 6.7
  LengthRev = 0
  Placement = pos=(86,11.5,72) rot=(0,1,0;3.14159rad)
  Solid = true
  Symmetric = false
FEATURE [Part::Box] Box037  label="backLeftCasePillarAngledSideBracket"
  AttacherType = Attacher::AttachEngine3D
  Height = 14
  Length = 3.4
  Placement = pos=(0,10.8,0) rot=(0,1,0;0.785398rad)
  Width = 4
FEATURE [Part::Box] Box038  label="backRightCasePillarAngledSideBracket"
  AttacherType = Attacher::AttachEngine3D
  Height = 14
  Length = 3.4
  Placement = pos=(9.9,10.8,62.1) rot=(0,-1,0;0.785398rad)
  Width = 4
FEATURE [Sketcher::SketchObject] Sketch090  label="topSketch026"
  FullyConstrained = true
  sketch-geometry (8):
    g0: ArcOfCircle CenterX=19 CenterY=19.1201 CenterZ=0 NormalX=0 NormalY=0 NormalZ=1 AngleXU=0 Radius=18.8799 StartAngle=1.5708 EndAngle=3.14793
    g1: LineSegment StartX=0.120501 StartY=19.0004 StartZ=0 EndX=0.120501 EndY=0.000382114 EndZ=0
    g2: LineSegment StartX=19 StartY=38 StartZ=0 EndX=124 EndY=38 EndZ=0
    g3: LineSegment StartX=0.120501 StartY=0.000382114 StartZ=0 EndX=105.121 EndY=0.000382114 EndZ=0
    g4: LineSegment StartX=124 StartY=38 StartZ=0 EndX=125.616 EndY=38 EndZ=0
    g5: LineSegment StartX=105.121 StartY=0.000382114 StartZ=0 EndX=106.736 EndY=0.000382114 EndZ=0
    g6: ArcOfCircle CenterX=106.616 CenterY=19 CenterZ=0 NormalX=0 NormalY=0 NormalZ=1 AngleXU=0 Radius=19 StartAngle=4.71873 EndAngle=6.28319
    g7: LineSegment StartX=125.616 StartY=38 StartZ=0 EndX=125.616 EndY=19 EndZ=0
  constraints (21):
    c: Block(g0)
    c: Coincident(g1,g0)
    c: Vertical(g1)
    c: Horizontal(g2)
    c: Distance(g2) = 105
    c: Coincident(g2,g0)
    c: Distance(g1) = 19
    c: Coincident(g3,g1)
    c: Horizontal(g3)
    c: Distance(g3) = 105
    c: Coincident(g4,g2)
    c: Horizontal(g4)
    c: Distance(g4) = 1.61553
    c: Horizontal(g5)
    c: Equal(g4,g5) = 1.61553
    c: Coincident(g5,g3)
    c: Block(g6)
    c: Coincident(g6,g5)
    c: Coincident(g7,g4)
    c: Coincident(g7,g6)
    c: Vertical(g7)
FEATURE [Part::Extrusion] Extrude081  label="sideB006"
  Base = -> Sketch090
  Dir = (0,0,1)
  DirMode = 2
  FaceMakerClass = Part::FaceMakerBullseye
  LengthFwd = 3
  LengthRev = 0
  Placement = pos=(-0.1205,0,72) rot=(0,0,1;0rad)
  Solid = true
  Symmetric = false
FEATURE [Sketcher::SketchObject] Sketch091  label="topSketch027"
  FullyConstrained = true
  sketch-geometry (8):
    g0: ArcOfCircle CenterX=19 CenterY=19.1201 CenterZ=0 NormalX=0 NormalY=0 NormalZ=1 AngleXU=0 Radius=18.8799 StartAngle=1.5708 EndAngle=3.14793
    g1: LineSegment StartX=0.120501 StartY=19.0004 StartZ=0 EndX=0.120501 EndY=0.000382114 EndZ=0
    g2: LineSegment StartX=19 StartY=38 StartZ=0 EndX=124 EndY=38 EndZ=0
    g3: LineSegment StartX=0.120501 StartY=0.000382114 StartZ=0 EndX=105.121 EndY=0.000382114 EndZ=0
    g4: LineSegment StartX=124 StartY=38 StartZ=0 EndX=125.616 EndY=38 EndZ=0
    g5: LineSegment StartX=105.121 StartY=0.000382114 StartZ=0 EndX=106.736 EndY=0.000382114 EndZ=0
    g6: ArcOfCircle CenterX=106.616 CenterY=19 CenterZ=0 NormalX=0 NormalY=0 NormalZ=1 AngleXU=0 Radius=19 StartAngle=4.71873 EndAngle=6.28319
    g7: LineSegment StartX=125.616 StartY=38 StartZ=0 EndX=125.616 EndY=19 EndZ=0
  constraints (21):
    c: Block(g0)
    c: Coincident(g1,g0)
    c: Vertical(g1)
    c: Horizontal(g2)
    c: Distance(g2) = 105
    c: Coincident(g2,g0)
    c: Distance(g1) = 19
    c: Coincident(g3,g1)
    c: Horizontal(g3)
    c: Distance(g3) = 105
    c: Coincident(g4,g2)
    c: Horizontal(g4)
    c: Distance(g4) = 1.61553
    c: Horizontal(g5)
    c: Equal(g4,g5) = 1.61553
    c: Coincident(g5,g3)
    c: Block(g6)
    c: Coincident(g6,g5)
    c: Coincident(g7,g4)
    c: Coincident(g7,g6)
    c: Vertical(g7)
FEATURE [Part::Extrusion] Extrude082  label="sideB007"
  Base = -> Sketch091
  Dir = (0,0,1)
  DirMode = 2
  FaceMakerClass = Part::FaceMakerBullseye
  LengthFwd = 3
  LengthRev = 0
  Placement = pos=(0,0,72) rot=(0,0,1;0rad)
  Solid = true
  Symmetric = false
FEATURE [Part::Cut] Cut075
  Base = -> Extrude081
  Placement = pos=(0.05,0,0) rot=(0,0,1;0rad)
  Tool = -> Extrude082
FEATURE [Sketcher::SketchObject] Sketch092  label="topSketch028"
  FullyConstrained = true
  sketch-geometry (8):
    g0: ArcOfCircle CenterX=19 CenterY=19.1201 CenterZ=0 NormalX=0 NormalY=0 NormalZ=1 AngleXU=0 Radius=18.8799 StartAngle=1.5708 EndAngle=3.14793
    g1: LineSegment StartX=0.120501 StartY=19.0004 StartZ=0 EndX=0.120501 EndY=0.000382114 EndZ=0
    g2: LineSegment StartX=19 StartY=38 StartZ=0 EndX=124 EndY=38 EndZ=0
    g3: LineSegment StartX=0.120501 StartY=0.000382114 StartZ=0 EndX=105.121 EndY=0.000382114 EndZ=0
    g4: LineSegment StartX=124 StartY=38 StartZ=0 EndX=125.616 EndY=38 EndZ=0
    g5: LineSegment StartX=105.121 StartY=0.000382114 StartZ=0 EndX=106.736 EndY=0.000382114 EndZ=0
    g6: ArcOfCircle CenterX=106.616 CenterY=19 CenterZ=0 NormalX=0 NormalY=0 NormalZ=1 AngleXU=0 Radius=19 StartAngle=4.71873 EndAngle=6.28319
    g7: LineSegment StartX=125.616 StartY=38 StartZ=0 EndX=125.616 EndY=19 EndZ=0
  constraints (21):
    c: Block(g0)
    c: Coincident(g1,g0)
    c: Vertical(g1)
    c: Horizontal(g2)
    c: Distance(g2) = 105
    c: Coincident(g2,g0)
    c: Distance(g1) = 19
    c: Coincident(g3,g1)
    c: Horizontal(g3)
    c: Distance(g3) = 105
    c: Coincident(g4,g2)
    c: Horizontal(g4)
    c: Distance(g4) = 1.61553
    c: Horizontal(g5)
    c: Equal(g4,g5) = 1.61553
    c: Coincident(g5,g3)
    c: Block(g6)
    c: Coincident(g6,g5)
    c: Coincident(g7,g4)
    c: Coincident(g7,g6)
    c: Vertical(g7)
FEATURE [Part::Extrusion] Extrude083  label="sideB008"
  Base = -> Sketch092
  Dir = (0,0,1)
  DirMode = 2
  FaceMakerClass = Part::FaceMakerBullseye
  LengthFwd = 3
  LengthRev = 0
  Placement = pos=(-0.1205,0,72) rot=(0,0,1;0rad)
  Solid = true
  Symmetric = false
FEATURE [Sketcher::SketchObject] Sketch093  label="topSketch029"
  FullyConstrained = true
  sketch-geometry (8):
    g0: ArcOfCircle CenterX=19 CenterY=19.1201 CenterZ=0 NormalX=0 NormalY=0 NormalZ=1 AngleXU=0 Radius=18.8799 StartAngle=1.5708 EndAngle=3.14793
    g1: LineSegment StartX=0.120501 StartY=19.0004 StartZ=0 EndX=0.120501 EndY=0.000382114 EndZ=0
    g2: LineSegment StartX=19 StartY=38 StartZ=0 EndX=124 EndY=38 EndZ=0
    g3: LineSegment StartX=0.120501 StartY=0.000382114 StartZ=0 EndX=105.121 EndY=0.000382114 EndZ=0
    g4: LineSegment StartX=124 StartY=38 StartZ=0 EndX=125.616 EndY=38 EndZ=0
    g5: LineSegment StartX=105.121 StartY=0.000382114 StartZ=0 EndX=106.736 EndY=0.000382114 EndZ=0
    g6: ArcOfCircle CenterX=106.616 CenterY=19 CenterZ=0 NormalX=0 NormalY=0 NormalZ=1 AngleXU=0 Radius=19 StartAngle=4.71873 EndAngle=6.28319
    g7: LineSegment StartX=125.616 StartY=38 StartZ=0 EndX=125.616 EndY=19 EndZ=0
  constraints (21):
    c: Block(g0)
    c: Coincident(g1,g0)
    c: Vertical(g1)
    c: Horizontal(g2)
    c: Distance(g2) = 105
    c: Coincident(g2,g0)
    c: Distance(g1) = 19
    c: Coincident(g3,g1)
    c: Horizontal(g3)
    c: Distance(g3) = 105
    c: Coincident(g4,g2)
    c: Horizontal(g4)
    c: Distance(g4) = 1.61553
    c: Horizontal(g5)
    c: Equal(g4,g5) = 1.61553
    c: Coincident(g5,g3)
    c: Block(g6)
    c: Coincident(g6,g5)
    c: Coincident(g7,g4)
    c: Coincident(g7,g6)
    c: Vertical(g7)
FEATURE [Part::Extrusion] Extrude084  label="sideB009"
  Base = -> Sketch093
  Dir = (0,0,1)
  DirMode = 2
  FaceMakerClass = Part::FaceMakerBullseye
  LengthFwd = 3
  LengthRev = 0
  Placement = pos=(0,0,72) rot=(0,0,1;0rad)
  Solid = true
  Symmetric = false
FEATURE [Part::Cut] Cut076
  Base = -> Extrude083
  Placement = pos=(0.05,0,-75) rot=(0,0,1;0rad)
  Tool = -> Extrude084
FEATURE [Part::MultiFuse] Fusion155  label="sideA006"
  Shapes = -> [Cut076,Cut073]
FEATURE [Part::MultiFuse] Fusion156  label="sideB010"
  Shapes = -> [Cut075,Cut074]
FEATURE [Sketcher::SketchObject] Sketch094
  FullyConstrained = true
  Placement = pos=(0,0,0) rot=(1,0,0;1.5708rad)
  sketch-geometry (8):
    g0: LineSegment StartX=0 StartY=4e-16 StartZ=0 EndX=-7 EndY=4e-16 EndZ=0
    g1: LineSegment StartX=-7 StartY=4e-16 StartZ=0 EndX=-10.5 EndY=4e-16 EndZ=0
    g2: LineSegment StartX=0 StartY=4e-16 StartZ=0 EndX=3.5 EndY=4e-16 EndZ=0
    g3: ArcOfCircle CenterX=-10.5 CenterY=3.5 CenterZ=0 NormalX=0 NormalY=0 NormalZ=1 AngleXU=0 Radius=3.5 StartAngle=4.71239 EndAngle=6.28319
    g4: ArcOfCircle CenterX=3.5 CenterY=3.5 CenterZ=0 NormalX=0 NormalY=0 NormalZ=1 AngleXU=0 Radius=3.5 StartAngle=3.14159 EndAngle=4.71239
    g5: ArcOfCircle CenterX=-3.5 CenterY=3.5 CenterZ=0 NormalX=0 NormalY=0 NormalZ=1 AngleXU=0 Radius=3 StartAngle=3.14159 EndAngle=6.28319
    g6: LineSegment StartX=-7 StartY=3.5 StartZ=0 EndX=-6.5 EndY=3.5 EndZ=0
    g7: LineSegment StartX=-0.5 StartY=3.5 StartZ=0 EndX=0 EndY=3.5 EndZ=0
  constraints (20):
    c: Coincident(g0,g-1)
    c: Horizontal(g0)
    c: Distance(g0) = 7
    c: Coincident(g1,g0)
    c: Horizontal(g1)
    c: Distance(g1) = 3.5
    c: Coincident(g2,g0)
    c: Distance(g2) = 3.5
    c: Horizontal(g2)
    c: Coincident(g3,g1)
    c: Block(g3)
    c: Coincident(g4,g2)
    c: Block(g4)
    c: Horizontal(g6)
    c: Coincident(g5,g6)
    c: Block(g5)
    c: Coincident(g6,g3)
    c: Coincident(g7,g5)
    c: Coincident(g7,g4)
    c: Horizontal(g7)
FEATURE [Part::Extrusion] Extrude085  label="frontLeftRightCasePillarSideBracket003"
  Base = -> Sketch094
  Dir = (0,-1,2e-16)
  DirMode = 2
  FaceMakerClass = Part::FaceMakerBullseye
  LengthFwd = 2
  LengthRev = 0
  Placement = pos=(113,11.5,0) rot=(0,1,0;0rad)
  Solid = true
  Symmetric = false
FEATURE [Part::Cylinder] Cylinder071  label="removeFromPlugHousingHole"
  Angle = 360
  AttacherType = Attacher::AttachEngine3D
  Height = 40
  Placement = pos=(-27,19,36) rot=(0,1,0;1.5708rad)
  Radius = 4.34
FEATURE [Part::Cut] Cut077  label="bottom026"
  Base = -> Cut072
  Tool = -> Cylinder071
